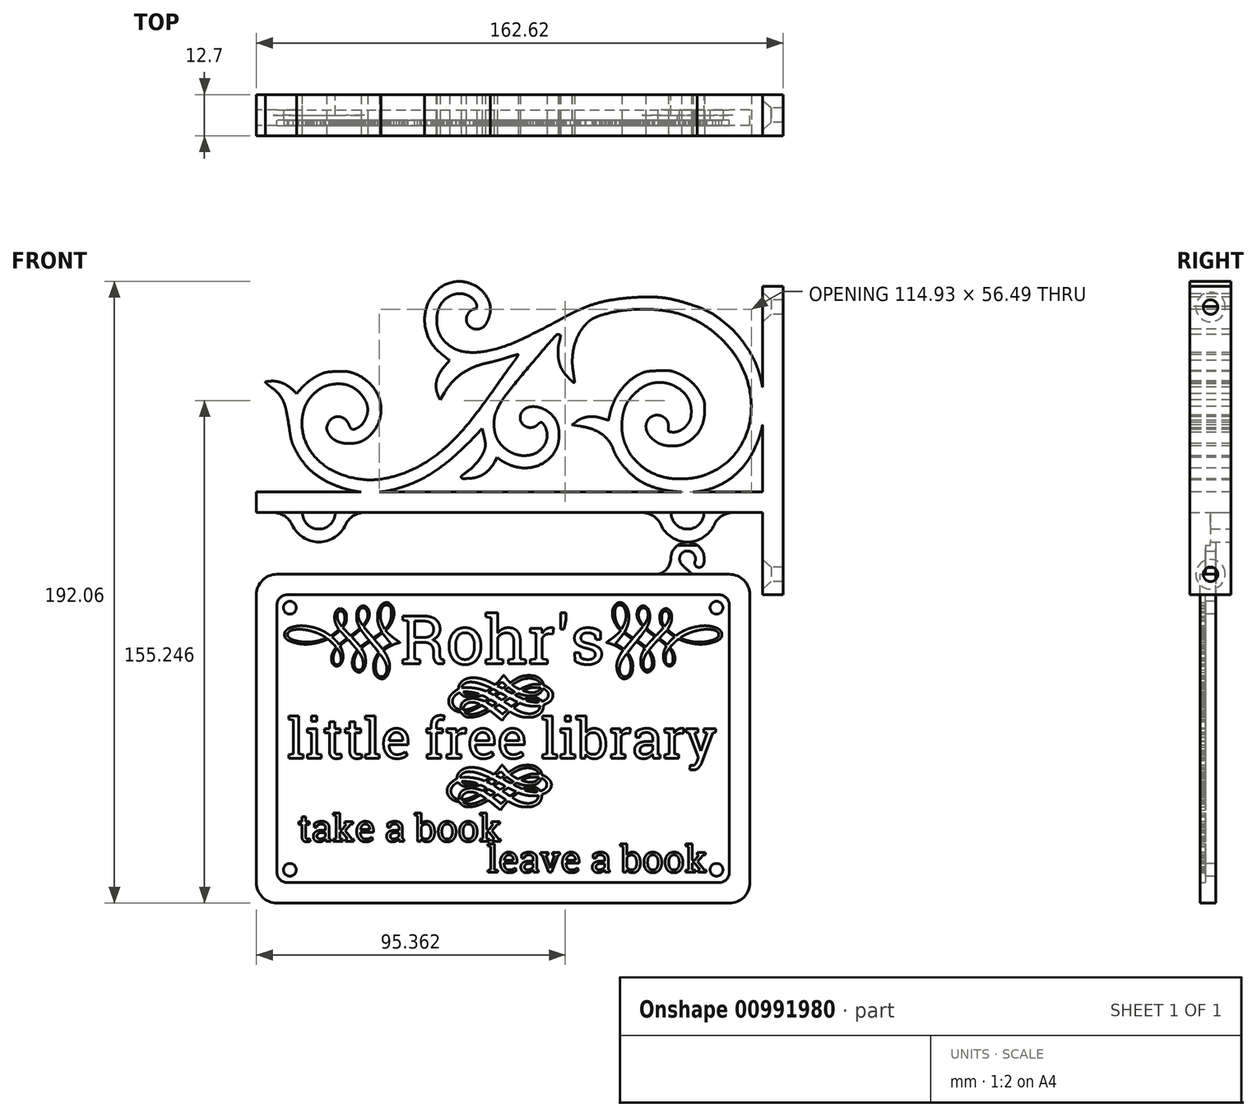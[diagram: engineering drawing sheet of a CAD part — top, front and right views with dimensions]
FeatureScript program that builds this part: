
annotation { "Feature Type Name" : "Feature", "Feature Type Description" : "" }
export const myFeature = defineFeature(function(context is Context, id is Id, definition is map)
    precondition{}
    {
        {
            var Q0;
            Q0=qCreatedBy(makeId("Front.planeOp"),FACE);
            var sketch = newSketch(context, id + "F0", { "sketchPlane" : qUnion([Q0])});
            skLineSegment(sketch, "E0.bottom", {"start": v(-69.85, 50.8) * mm, "end": v(69.85, 50.8) * mm});
            skLineSegment(sketch, "E0.top", {"start": v(-69.85, -50.8) * mm, "end": v(69.85, -50.8) * mm});
            skLineSegment(sketch, "E0.left", {"start": v(-76.2, 44.45) * mm, "end": v(-76.2, -44.45) * mm});
            skLineSegment(sketch, "E0.right", {"start": v(76.2, 44.45) * mm, "end": v(76.2, -44.45) * mm});
            skPoint(sketch, "E0.middle", {"position": v(0, 0) * mm});
            skPoint(sketch, "E1.visualSharp", {"position": v(-76.2, 50.8) * mm});
            skArc(sketch, "E1.filletArc", {"start": v(-69.85, 50.8) * mm, "mid": v(-74.34, 48.94) * mm, "end": v(-76.2, 44.45) * mm});
            skPoint(sketch, "E2.visualSharp", {"position": v(76.2, 50.8) * mm});
            skArc(sketch, "E2.filletArc", {"start": v(76.2, 44.45) * mm, "mid": v(74.34, 48.94) * mm, "end": v(69.85, 50.8) * mm});
            skPoint(sketch, "E3.visualSharp", {"position": v(76.2, -50.8) * mm});
            skArc(sketch, "E3.filletArc", {"start": v(69.85, -50.8) * mm, "mid": v(74.34, -48.94) * mm, "end": v(76.2, -44.45) * mm});
            skPoint(sketch, "E4.visualSharp", {"position": v(-76.2, -50.8) * mm});
            skArc(sketch, "E4.filletArc", {"start": v(-76.2, -44.45) * mm, "mid": v(-74.34, -48.94) * mm, "end": v(-69.85, -50.8) * mm});
            skSolve(sketch);
        }
        {
            var Q0;
            Q0=makeQuery(id+"F0.imprint","IMPRINT",FACE,{"disambiguationData":[TD([[makeQuery(id+"F0.imprint","IMPRINT",EDGE,{"derivedFrom":sQuery(id+"F0.wireOp",EDGE,"E0.bottom")}),-1.0]])]});
            extrude(context, id + "F1", {"entities" : qUnion([Q0]), "endBound" : BoundingType.SYMMETRIC, "depth" : 3.17 * mm, "offsetDistance" : 25.4 * mm});
        }
        {
            var Q0;
            Q0=makeQuery(id+"F1.opExtrude","CAP_FACE",FACE,{"disambiguationData":[OSD([sQuery(id+"F0.wireOp",EDGE,"E0.bottom"),sQuery(id+"F0.wireOp",EDGE,"E0.top"),sQuery(id+"F0.wireOp",EDGE,"E0.left"),sQuery(id+"F0.wireOp",EDGE,"E0.right"),sQuery(id+"F0.wireOp",EDGE,"E1.filletArc"),sQuery(id+"F0.wireOp",EDGE,"E2.filletArc"),sQuery(id+"F0.wireOp",EDGE,"E3.filletArc"),sQuery(id+"F0.wireOp",EDGE,"E4.filletArc")])],"isStart":false});
            var sketch = newSketch(context, id + "F2", { "sketchPlane" : qUnion([Q0])});
            skLineSegment(sketch, "E5.bottom", {"start": v(-66.67, 44.45) * mm, "end": v(66.67, 44.45) * mm});
            skLineSegment(sketch, "E5.top", {"start": v(-66.67, -44.45) * mm, "end": v(66.67, -44.45) * mm});
            skLineSegment(sketch, "E5.left", {"start": v(-69.85, 41.28) * mm, "end": v(-69.85, -41.27) * mm});
            skLineSegment(sketch, "E5.right", {"start": v(69.85, 41.28) * mm, "end": v(69.85, -41.27) * mm});
            skPoint(sketch, "E5.middle", {"position": v(0, 0) * mm});
            skPoint(sketch, "E6.visualSharp", {"position": v(-69.85, 44.45) * mm});
            skArc(sketch, "E6.filletArc", {"start": v(-66.67, 44.45) * mm, "mid": v(-68.92, 43.52) * mm, "end": v(-69.85, 41.28) * mm});
            skPoint(sketch, "E7.visualSharp", {"position": v(69.85, 44.45) * mm});
            skArc(sketch, "E7.filletArc", {"start": v(69.85, 41.28) * mm, "mid": v(68.92, 43.52) * mm, "end": v(66.67, 44.45) * mm});
            skPoint(sketch, "E8.visualSharp", {"position": v(69.85, -44.45) * mm});
            skArc(sketch, "E8.filletArc", {"start": v(66.67, -44.45) * mm, "mid": v(68.92, -43.52) * mm, "end": v(69.85, -41.27) * mm});
            skPoint(sketch, "E9.visualSharp", {"position": v(-69.85, -44.45) * mm});
            skArc(sketch, "E9.filletArc", {"start": v(-69.85, -41.27) * mm, "mid": v(-68.92, -43.52) * mm, "end": v(-66.67, -44.45) * mm});
            skSolve(sketch);
        }
        {
            var Q0;
            Q0=makeQuery(id+"F2.imprint","IMPRINT",FACE,{"disambiguationData":[TD([[makeQuery(id+"F2.imprint","IMPRINT",EDGE,{"derivedFrom":sQuery(id+"F2.wireOp",EDGE,"E5.bottom")}),1.0]])]});
            extrude(context, id + "F3", {"entities" : qUnion([Q0]), "operationType" : NewBodyOperationType.ADD, "depth" : 1.59 * mm, "offsetDistance" : 25.4 * mm});
        }
        {
            var Q0;
            Q0=makeQuery(id+"F1.opExtrude","CAP_FACE",FACE,{"disambiguationData":[OSD([sQuery(id+"F0.wireOp",EDGE,"E0.bottom"),sQuery(id+"F0.wireOp",EDGE,"E0.top"),sQuery(id+"F0.wireOp",EDGE,"E0.left"),sQuery(id+"F0.wireOp",EDGE,"E0.right"),sQuery(id+"F0.wireOp",EDGE,"E1.filletArc"),sQuery(id+"F0.wireOp",EDGE,"E2.filletArc"),sQuery(id+"F0.wireOp",EDGE,"E3.filletArc"),sQuery(id+"F0.wireOp",EDGE,"E4.filletArc")])],"isStart":false});
            var sketch = newSketch(context, id + "F4", { "sketchPlane" : qUnion([Q0])});
            skLineSegment(sketch, "E10", {"start": v(0, 0) * mm, "end": v(0, 25.75) * mm, "construction": true});
            skArc(sketch, "E11", {"start": v(-36.9, 41.88) * mm, "mid": v(-37.36, 41.59) * mm, "end": v(-37.75, 41.2) * mm});
            skArc(sketch, "E12", {"start": v(-37.75, 41.2) * mm, "mid": v(-38.1, 40.67) * mm, "end": v(-38.38, 40.1) * mm});
            skArc(sketch, "E13", {"start": v(-38.38, 40.1) * mm, "mid": v(-38.6, 39.42) * mm, "end": v(-38.75, 38.7) * mm});
            skArc(sketch, "E14", {"start": v(-38.75, 38.7) * mm, "mid": v(-38.82, 37.9) * mm, "end": v(-38.8, 37.1) * mm});
            skArc(sketch, "E15", {"start": v(-38.8, 37.1) * mm, "mid": v(-38.78, 36.68) * mm, "end": v(-38.72, 36.26) * mm});
            skArc(sketch, "E16", {"start": v(-38.72, 36.26) * mm, "mid": v(-38.65, 35.87) * mm, "end": v(-38.56, 35.49) * mm});
            skArc(sketch, "E17", {"start": v(-38.56, 35.49) * mm, "mid": v(-38.44, 35.1) * mm, "end": v(-38.3, 34.7) * mm});
            skArc(sketch, "E18", {"start": v(-38.3, 34.7) * mm, "mid": v(-38.1, 34.27) * mm, "end": v(-37.9, 33.83) * mm});
            skLineSegment(sketch, "E19", {"start": v(-37.9, 33.83) * mm, "end": v(-37.5, 32.99) * mm});
            skLineSegment(sketch, "E20", {"start": v(-37.5, 32.99) * mm, "end": v(-37.74, 32.8) * mm});
            skArc(sketch, "E21", {"start": v(-37.74, 32.8) * mm, "mid": v(-38, 32.6) * mm, "end": v(-38.27, 32.4) * mm});
            skArc(sketch, "E22", {"start": v(-38.27, 32.4) * mm, "mid": v(-38.7, 32.12) * mm, "end": v(-39.12, 31.84) * mm});
            skArc(sketch, "E23", {"start": v(-39.12, 31.84) * mm, "mid": v(-39.59, 31.53) * mm, "end": v(-40.05, 31.23) * mm});
            skArc(sketch, "E24", {"start": v(-40.05, 31.23) * mm, "mid": v(-40.1, 31.21) * mm, "end": v(-40.15, 31.22) * mm});
            skArc(sketch, "E25", {"start": v(-40.15, 31.22) * mm, "mid": v(-40.18, 31.23) * mm, "end": v(-40.2, 31.25) * mm});
            skArc(sketch, "E26", {"start": v(-40.2, 31.25) * mm, "mid": v(-40.41, 31.5) * mm, "end": v(-40.62, 31.74) * mm});
            skArc(sketch, "E27", {"start": v(-40.62, 31.74) * mm, "mid": v(-40.86, 32.01) * mm, "end": v(-41.1, 32.29) * mm});
            skArc(sketch, "E28", {"start": v(-41.1, 32.29) * mm, "mid": v(-41.38, 32.61) * mm, "end": v(-41.66, 32.94) * mm});
            skLineSegment(sketch, "E29", {"start": v(-41.66, 32.94) * mm, "end": v(-43.09, 34.63) * mm});
            skLineSegment(sketch, "E30", {"start": v(-43.09, 34.63) * mm, "end": v(-42.74, 35.06) * mm});
            skArc(sketch, "E31", {"start": v(-42.74, 35.06) * mm, "mid": v(-42.33, 35.6) * mm, "end": v(-41.96, 36.17) * mm});
            skArc(sketch, "E32", {"start": v(-41.96, 36.17) * mm, "mid": v(-41.7, 36.7) * mm, "end": v(-41.49, 37.24) * mm});
            skArc(sketch, "E33", {"start": v(-41.49, 37.24) * mm, "mid": v(-41.36, 37.75) * mm, "end": v(-41.3, 38.28) * mm});
            skArc(sketch, "E34", {"start": v(-41.3, 38.28) * mm, "mid": v(-41.32, 38.78) * mm, "end": v(-41.4, 39.28) * mm});
            skArc(sketch, "E35", {"start": v(-41.4, 39.28) * mm, "mid": v(-41.49, 39.56) * mm, "end": v(-41.6, 39.84) * mm});
            skArc(sketch, "E36", {"start": v(-41.6, 39.84) * mm, "mid": v(-41.7, 40.07) * mm, "end": v(-41.84, 40.29) * mm});
            skArc(sketch, "E37", {"start": v(-41.84, 40.29) * mm, "mid": v(-41.98, 40.47) * mm, "end": v(-42.14, 40.63) * mm});
            skArc(sketch, "E38", {"start": v(-42.14, 40.63) * mm, "mid": v(-42.32, 40.77) * mm, "end": v(-42.51, 40.88) * mm});
            skArc(sketch, "E39", {"start": v(-42.51, 40.88) * mm, "mid": v(-42.7, 40.96) * mm, "end": v(-42.9, 41.03) * mm});
            skArc(sketch, "E40", {"start": v(-42.9, 41.03) * mm, "mid": v(-43.07, 41.06) * mm, "end": v(-43.25, 41.07) * mm});
            skArc(sketch, "E41", {"start": v(-43.25, 41.07) * mm, "mid": v(-43.42, 41.06) * mm, "end": v(-43.6, 41.02) * mm});
            skArc(sketch, "E42", {"start": v(-43.6, 41.02) * mm, "mid": v(-43.8, 40.95) * mm, "end": v(-43.99, 40.86) * mm});
            skArc(sketch, "E43", {"start": v(-43.99, 40.86) * mm, "mid": v(-44.28, 40.67) * mm, "end": v(-44.53, 40.41) * mm});
            skArc(sketch, "E44", {"start": v(-44.53, 40.41) * mm, "mid": v(-44.76, 40.08) * mm, "end": v(-44.95, 39.7) * mm});
            skArc(sketch, "E45", {"start": v(-44.95, 39.7) * mm, "mid": v(-45.1, 39.26) * mm, "end": v(-45.2, 38.79) * mm});
            skArc(sketch, "E46", {"start": v(-45.2, 38.79) * mm, "mid": v(-45.27, 38.25) * mm, "end": v(-45.3, 37.7) * mm});
            skArc(sketch, "E47", {"start": v(-45.3, 37.7) * mm, "mid": v(-45.29, 37.34) * mm, "end": v(-45.26, 36.98) * mm});
            skArc(sketch, "E48", {"start": v(-45.26, 36.98) * mm, "mid": v(-45.2, 36.64) * mm, "end": v(-45.14, 36.3) * mm});
            skArc(sketch, "E49", {"start": v(-45.14, 36.3) * mm, "mid": v(-45.04, 35.97) * mm, "end": v(-44.93, 35.63) * mm});
            skArc(sketch, "E50", {"start": v(-44.93, 35.63) * mm, "mid": v(-44.78, 35.27) * mm, "end": v(-44.6, 34.9) * mm});
            skLineSegment(sketch, "E51", {"start": v(-44.6, 34.9) * mm, "end": v(-44.22, 34.12) * mm});
            skLineSegment(sketch, "E52", {"start": v(-44.22, 34.12) * mm, "end": v(-44.73, 33.68) * mm});
            skArc(sketch, "E53", {"start": v(-44.73, 33.68) * mm, "mid": v(-44.86, 33.57) * mm, "end": v(-45, 33.47) * mm});
            skArc(sketch, "E54", {"start": v(-45, 33.47) * mm, "mid": v(-45.19, 33.32) * mm, "end": v(-45.38, 33.16) * mm});
            skArc(sketch, "E55", {"start": v(-45.38, 33.16) * mm, "mid": v(-45.59, 33) * mm, "end": v(-45.8, 32.83) * mm});
            skArc(sketch, "E56", {"start": v(-45.8, 32.83) * mm, "mid": v(-46, 32.68) * mm, "end": v(-46.2, 32.53) * mm});
            skArc(sketch, "E57", {"start": v(-46.2, 32.53) * mm, "mid": v(-46.45, 32.34) * mm, "end": v(-46.7, 32.16) * mm});
            skArc(sketch, "E58", {"start": v(-46.7, 32.16) * mm, "mid": v(-46.84, 32.07) * mm, "end": v(-46.98, 31.98) * mm});
            skArc(sketch, "E59", {"start": v(-46.98, 31.98) * mm, "mid": v(-47.07, 31.93) * mm, "end": v(-47.17, 31.9) * mm});
            skArc(sketch, "E60", {"start": v(-47.17, 31.9) * mm, "mid": v(-47.22, 31.9) * mm, "end": v(-47.27, 31.93) * mm});
            skArc(sketch, "E61", {"start": v(-47.27, 31.93) * mm, "mid": v(-47.31, 31.97) * mm, "end": v(-47.36, 32.02) * mm});
            skArc(sketch, "E62", {"start": v(-47.36, 32.02) * mm, "mid": v(-47.51, 32.19) * mm, "end": v(-47.67, 32.35) * mm});
            skArc(sketch, "E63", {"start": v(-47.67, 32.35) * mm, "mid": v(-47.85, 32.55) * mm, "end": v(-48.04, 32.75) * mm});
            skArc(sketch, "E64", {"start": v(-48.04, 32.75) * mm, "mid": v(-48.25, 32.97) * mm, "end": v(-48.46, 33.2) * mm});
            skLineSegment(sketch, "E65", {"start": v(-48.46, 33.2) * mm, "end": v(-49.53, 34.33) * mm});
            skLineSegment(sketch, "E66", {"start": v(-49.53, 34.33) * mm, "end": v(-49.19, 34.78) * mm});
            skArc(sketch, "E67", {"start": v(-49.19, 34.78) * mm, "mid": v(-48.98, 35.07) * mm, "end": v(-48.8, 35.37) * mm});
            skArc(sketch, "E68", {"start": v(-48.8, 35.37) * mm, "mid": v(-48.67, 35.66) * mm, "end": v(-48.56, 35.96) * mm});
            skArc(sketch, "E69", {"start": v(-48.56, 35.96) * mm, "mid": v(-48.48, 36.29) * mm, "end": v(-48.42, 36.62) * mm});
            skArc(sketch, "E70", {"start": v(-48.42, 36.62) * mm, "mid": v(-48.39, 37.04) * mm, "end": v(-48.38, 37.45) * mm});
            skArc(sketch, "E71", {"start": v(-48.38, 37.45) * mm, "mid": v(-48.38, 37.75) * mm, "end": v(-48.38, 38.05) * mm});
            skArc(sketch, "E72", {"start": v(-48.38, 38.05) * mm, "mid": v(-48.4, 38.23) * mm, "end": v(-48.42, 38.4) * mm});
            skArc(sketch, "E73", {"start": v(-48.42, 38.4) * mm, "mid": v(-48.44, 38.54) * mm, "end": v(-48.48, 38.68) * mm});
            skArc(sketch, "E74", {"start": v(-48.48, 38.68) * mm, "mid": v(-48.54, 38.82) * mm, "end": v(-48.6, 38.97) * mm});
            skArc(sketch, "E75", {"start": v(-48.6, 38.97) * mm, "mid": v(-48.73, 39.18) * mm, "end": v(-48.85, 39.38) * mm});
            skArc(sketch, "E76", {"start": v(-48.85, 39.38) * mm, "mid": v(-48.97, 39.54) * mm, "end": v(-49.1, 39.68) * mm});
            skArc(sketch, "E77", {"start": v(-49.1, 39.68) * mm, "mid": v(-49.23, 39.8) * mm, "end": v(-49.37, 39.9) * mm});
            skArc(sketch, "E78", {"start": v(-49.37, 39.9) * mm, "mid": v(-49.54, 40.01) * mm, "end": v(-49.72, 40.1) * mm});
            skArc(sketch, "E79", {"start": v(-49.72, 40.1) * mm, "mid": v(-49.92, 40.18) * mm, "end": v(-50.13, 40.23) * mm});
            skArc(sketch, "E80", {"start": v(-50.13, 40.23) * mm, "mid": v(-50.32, 40.24) * mm, "end": v(-50.5, 40.23) * mm});
            skArc(sketch, "E81", {"start": v(-50.5, 40.23) * mm, "mid": v(-50.7, 40.17) * mm, "end": v(-50.87, 40.09) * mm});
            skArc(sketch, "E82", {"start": v(-50.87, 40.09) * mm, "mid": v(-51.07, 39.96) * mm, "end": v(-51.25, 39.81) * mm});
            skArc(sketch, "E83", {"start": v(-51.25, 39.81) * mm, "mid": v(-51.64, 39.34) * mm, "end": v(-51.89, 38.79) * mm});
            skArc(sketch, "E84", {"start": v(-51.89, 38.79) * mm, "mid": v(-52.04, 38.07) * mm, "end": v(-52.07, 37.34) * mm});
            skArc(sketch, "E85", {"start": v(-52.07, 37.34) * mm, "mid": v(-51.98, 36.52) * mm, "end": v(-51.77, 35.73) * mm});
            skArc(sketch, "E86", {"start": v(-51.77, 35.73) * mm, "mid": v(-51.46, 34.97) * mm, "end": v(-51.04, 34.26) * mm});
            skLineSegment(sketch, "E87", {"start": v(-51.04, 34.26) * mm, "end": v(-50.7, 33.78) * mm});
            skLineSegment(sketch, "E88", {"start": v(-50.7, 33.78) * mm, "end": v(-51.26, 33.3) * mm});
            skArc(sketch, "E89", {"start": v(-51.26, 33.3) * mm, "mid": v(-51.39, 33.18) * mm, "end": v(-51.52, 33.07) * mm});
            skArc(sketch, "E90", {"start": v(-51.52, 33.07) * mm, "mid": v(-51.69, 32.94) * mm, "end": v(-51.85, 32.8) * mm});
            skArc(sketch, "E91", {"start": v(-51.85, 32.8) * mm, "mid": v(-52.03, 32.67) * mm, "end": v(-52.2, 32.54) * mm});
            skArc(sketch, "E92", {"start": v(-52.2, 32.54) * mm, "mid": v(-52.37, 32.42) * mm, "end": v(-52.52, 32.3) * mm});
            skLineSegment(sketch, "E93", {"start": v(-52.52, 32.3) * mm, "end": v(-53.25, 31.8) * mm});
            skLineSegment(sketch, "E94", {"start": v(-53.25, 31.8) * mm, "end": v(-54.37, 32.55) * mm});
            skArc(sketch, "E95", {"start": v(-54.37, 32.55) * mm, "mid": v(-55.03, 32.97) * mm, "end": v(-55.72, 33.33) * mm});
            skArc(sketch, "E96", {"start": v(-55.72, 33.33) * mm, "mid": v(-56.45, 33.67) * mm, "end": v(-57.2, 33.95) * mm});
            skArc(sketch, "E97", {"start": v(-57.2, 33.95) * mm, "mid": v(-58.01, 34.22) * mm, "end": v(-58.85, 34.43) * mm});
            skArc(sketch, "E98", {"start": v(-58.85, 34.43) * mm, "mid": v(-59.79, 34.63) * mm, "end": v(-60.73, 34.79) * mm});
            skArc(sketch, "E99", {"start": v(-60.73, 34.79) * mm, "mid": v(-61.26, 34.85) * mm, "end": v(-61.78, 34.9) * mm});
            skArc(sketch, "E100", {"start": v(-61.78, 34.9) * mm, "mid": v(-62.29, 34.9) * mm, "end": v(-62.79, 34.9) * mm});
            skArc(sketch, "E101", {"start": v(-62.79, 34.9) * mm, "mid": v(-63.28, 34.86) * mm, "end": v(-63.77, 34.8) * mm});
            skArc(sketch, "E102", {"start": v(-63.77, 34.8) * mm, "mid": v(-64.28, 34.7) * mm, "end": v(-64.78, 34.6) * mm});
            skArc(sketch, "E103", {"start": v(-64.78, 34.6) * mm, "mid": v(-65.27, 34.45) * mm, "end": v(-65.75, 34.3) * mm});
            skArc(sketch, "E104", {"start": v(-65.75, 34.3) * mm, "mid": v(-66.11, 34.14) * mm, "end": v(-66.46, 33.95) * mm});
            skArc(sketch, "E105", {"start": v(-66.46, 33.95) * mm, "mid": v(-66.73, 33.75) * mm, "end": v(-66.98, 33.52) * mm});
            skArc(sketch, "E106", {"start": v(-66.98, 33.52) * mm, "mid": v(-67.19, 33.26) * mm, "end": v(-67.36, 32.98) * mm});
            skArc(sketch, "E107", {"start": v(-67.36, 32.98) * mm, "mid": v(-67.45, 32.78) * mm, "end": v(-67.5, 32.57) * mm});
            skArc(sketch, "E108", {"start": v(-67.5, 32.57) * mm, "mid": v(-67.53, 32.32) * mm, "end": v(-67.54, 32.06) * mm});
            skArc(sketch, "E109", {"start": v(-67.54, 32.06) * mm, "mid": v(-67.52, 31.82) * mm, "end": v(-67.48, 31.57) * mm});
            skArc(sketch, "E110", {"start": v(-67.48, 31.57) * mm, "mid": v(-67.43, 31.4) * mm, "end": v(-67.33, 31.23) * mm});
            skArc(sketch, "E111", {"start": v(-67.33, 31.23) * mm, "mid": v(-66.8, 30.66) * mm, "end": v(-66.12, 30.26) * mm});
            skArc(sketch, "E112", {"start": v(-66.12, 30.26) * mm, "mid": v(-65.05, 29.85) * mm, "end": v(-63.95, 29.55) * mm});
            skArc(sketch, "E113", {"start": v(-63.95, 29.55) * mm, "mid": v(-62.7, 29.31) * mm, "end": v(-61.44, 29.2) * mm});
            skArc(sketch, "E114", {"start": v(-61.44, 29.2) * mm, "mid": v(-60.25, 29.2) * mm, "end": v(-59.07, 29.33) * mm});
            skArc(sketch, "E115", {"start": v(-59.07, 29.33) * mm, "mid": v(-58.52, 29.42) * mm, "end": v(-57.97, 29.53) * mm});
            skArc(sketch, "E116", {"start": v(-57.97, 29.53) * mm, "mid": v(-57.44, 29.65) * mm, "end": v(-56.92, 29.78) * mm});
            skArc(sketch, "E117", {"start": v(-56.92, 29.78) * mm, "mid": v(-56.44, 29.92) * mm, "end": v(-55.96, 30.07) * mm});
            skArc(sketch, "E118", {"start": v(-55.96, 30.07) * mm, "mid": v(-55.53, 30.23) * mm, "end": v(-55.1, 30.4) * mm});
            skArc(sketch, "E119", {"start": v(-55.1, 30.4) * mm, "mid": v(-54.8, 30.52) * mm, "end": v(-54.5, 30.64) * mm});
            skArc(sketch, "E120", {"start": v(-54.5, 30.64) * mm, "mid": v(-54.37, 30.69) * mm, "end": v(-54.24, 30.72) * mm});
            skArc(sketch, "E121", {"start": v(-54.24, 30.72) * mm, "mid": v(-54.16, 30.72) * mm, "end": v(-54.09, 30.7) * mm});
            skArc(sketch, "E122", {"start": v(-54.09, 30.7) * mm, "mid": v(-54, 30.67) * mm, "end": v(-53.93, 30.62) * mm});
            skArc(sketch, "E123", {"start": v(-53.93, 30.62) * mm, "mid": v(-53.71, 30.43) * mm, "end": v(-53.5, 30.24) * mm});
            skArc(sketch, "E124", {"start": v(-53.5, 30.24) * mm, "mid": v(-53.25, 30) * mm, "end": v(-53, 29.77) * mm});
            skArc(sketch, "E125", {"start": v(-53, 29.77) * mm, "mid": v(-52.74, 29.53) * mm, "end": v(-52.5, 29.28) * mm});
            skArc(sketch, "E126", {"start": v(-52.5, 29.28) * mm, "mid": v(-52.29, 29.07) * mm, "end": v(-52.09, 28.85) * mm});
            skLineSegment(sketch, "E127", {"start": v(-52.09, 28.85) * mm, "end": v(-51.55, 28.28) * mm});
            skLineSegment(sketch, "E128", {"start": v(-51.55, 28.28) * mm, "end": v(-51.96, 27.74) * mm});
            skArc(sketch, "E129", {"start": v(-51.96, 27.74) * mm, "mid": v(-52.24, 27.34) * mm, "end": v(-52.49, 26.92) * mm});
            skArc(sketch, "E130", {"start": v(-52.49, 26.92) * mm, "mid": v(-52.69, 26.5) * mm, "end": v(-52.84, 26.06) * mm});
            skArc(sketch, "E131", {"start": v(-52.84, 26.06) * mm, "mid": v(-52.96, 25.63) * mm, "end": v(-53.02, 25.2) * mm});
            skArc(sketch, "E132", {"start": v(-53.02, 25.2) * mm, "mid": v(-53.04, 24.75) * mm, "end": v(-53.02, 24.31) * mm});
            skArc(sketch, "E133", {"start": v(-53.02, 24.31) * mm, "mid": v(-52.93, 23.82) * mm, "end": v(-52.75, 23.34) * mm});
            skArc(sketch, "E134", {"start": v(-52.75, 23.34) * mm, "mid": v(-52.52, 22.97) * mm, "end": v(-52.2, 22.68) * mm});
            skArc(sketch, "E135", {"start": v(-52.2, 22.68) * mm, "mid": v(-51.85, 22.5) * mm, "end": v(-51.46, 22.43) * mm});
            skArc(sketch, "E136", {"start": v(-51.46, 22.43) * mm, "mid": v(-51.04, 22.48) * mm, "end": v(-50.64, 22.62) * mm});
            skArc(sketch, "E137", {"start": v(-50.64, 22.62) * mm, "mid": v(-50.38, 22.8) * mm, "end": v(-50.17, 23.03) * mm});
            skArc(sketch, "E138", {"start": v(-50.17, 23.03) * mm, "mid": v(-49.95, 23.36) * mm, "end": v(-49.78, 23.7) * mm});
            skArc(sketch, "E139", {"start": v(-49.78, 23.7) * mm, "mid": v(-49.63, 24.13) * mm, "end": v(-49.52, 24.57) * mm});
            skArc(sketch, "E140", {"start": v(-49.52, 24.57) * mm, "mid": v(-49.45, 25.03) * mm, "end": v(-49.43, 25.5) * mm});
            skArc(sketch, "E141", {"start": v(-49.43, 25.5) * mm, "mid": v(-49.45, 25.8) * mm, "end": v(-49.48, 26.1) * mm});
            skArc(sketch, "E142", {"start": v(-49.48, 26.1) * mm, "mid": v(-49.55, 26.46) * mm, "end": v(-49.64, 26.82) * mm});
            skArc(sketch, "E143", {"start": v(-49.64, 26.82) * mm, "mid": v(-49.74, 27.19) * mm, "end": v(-49.86, 27.55) * mm});
            skArc(sketch, "E144", {"start": v(-49.86, 27.55) * mm, "mid": v(-49.99, 27.87) * mm, "end": v(-50.13, 28.18) * mm});
            skLineSegment(sketch, "E145", {"start": v(-50.13, 28.18) * mm, "end": v(-50.42, 28.74) * mm});
            skLineSegment(sketch, "E146", {"start": v(-50.42, 28.74) * mm, "end": v(-50.05, 29.04) * mm});
            skArc(sketch, "E147", {"start": v(-50.05, 29.04) * mm, "mid": v(-49.95, 29.12) * mm, "end": v(-49.85, 29.2) * mm});
            skArc(sketch, "E148", {"start": v(-49.85, 29.2) * mm, "mid": v(-49.7, 29.33) * mm, "end": v(-49.54, 29.46) * mm});
            skArc(sketch, "E149", {"start": v(-49.54, 29.46) * mm, "mid": v(-49.36, 29.6) * mm, "end": v(-49.17, 29.74) * mm});
            skArc(sketch, "E150", {"start": v(-49.17, 29.74) * mm, "mid": v(-49, 29.88) * mm, "end": v(-48.81, 30.02) * mm});
            skLineSegment(sketch, "E151", {"start": v(-48.81, 30.02) * mm, "end": v(-47.94, 30.7) * mm});
            skLineSegment(sketch, "E152", {"start": v(-47.94, 30.7) * mm, "end": v(-47.2, 29.86) * mm});
            skArc(sketch, "E153", {"start": v(-47.2, 29.86) * mm, "mid": v(-46.91, 29.54) * mm, "end": v(-46.63, 29.22) * mm});
            skArc(sketch, "E154", {"start": v(-46.63, 29.22) * mm, "mid": v(-46.32, 28.87) * mm, "end": v(-46.02, 28.52) * mm});
            skArc(sketch, "E155", {"start": v(-46.02, 28.52) * mm, "mid": v(-45.75, 28.2) * mm, "end": v(-45.48, 27.89) * mm});
            skArc(sketch, "E156", {"start": v(-45.48, 27.89) * mm, "mid": v(-45.34, 27.72) * mm, "end": v(-45.2, 27.55) * mm});
            skArc(sketch, "E157", {"start": v(-45.2, 27.55) * mm, "mid": v(-45.18, 27.5) * mm, "end": v(-45.16, 27.43) * mm});
            skArc(sketch, "E158", {"start": v(-45.16, 27.43) * mm, "mid": v(-45.16, 27.36) * mm, "end": v(-45.18, 27.3) * mm});
            skArc(sketch, "E159", {"start": v(-45.18, 27.3) * mm, "mid": v(-45.22, 27.2) * mm, "end": v(-45.27, 27.1) * mm});
            skArc(sketch, "E160", {"start": v(-45.27, 27.1) * mm, "mid": v(-45.38, 26.93) * mm, "end": v(-45.5, 26.76) * mm});
            skArc(sketch, "E161", {"start": v(-45.5, 26.76) * mm, "mid": v(-45.78, 26.3) * mm, "end": v(-46.03, 25.84) * mm});
            skArc(sketch, "E162", {"start": v(-46.03, 25.84) * mm, "mid": v(-46.23, 25.39) * mm, "end": v(-46.39, 24.92) * mm});
            skArc(sketch, "E163", {"start": v(-46.39, 24.92) * mm, "mid": v(-46.5, 24.46) * mm, "end": v(-46.57, 23.99) * mm});
            skArc(sketch, "E164", {"start": v(-46.57, 23.99) * mm, "mid": v(-46.6, 23.5) * mm, "end": v(-46.58, 23.02) * mm});
            skArc(sketch, "E165", {"start": v(-46.58, 23.02) * mm, "mid": v(-46.53, 22.6) * mm, "end": v(-46.43, 22.17) * mm});
            skArc(sketch, "E166", {"start": v(-46.43, 22.17) * mm, "mid": v(-46.28, 21.81) * mm, "end": v(-46.09, 21.48) * mm});
            skArc(sketch, "E167", {"start": v(-46.09, 21.48) * mm, "mid": v(-45.86, 21.2) * mm, "end": v(-45.58, 20.95) * mm});
            skArc(sketch, "E168", {"start": v(-45.58, 20.95) * mm, "mid": v(-45.26, 20.75) * mm, "end": v(-44.91, 20.6) * mm});
            skArc(sketch, "E169", {"start": v(-44.91, 20.6) * mm, "mid": v(-44.64, 20.54) * mm, "end": v(-44.35, 20.54) * mm});
            skArc(sketch, "E170", {"start": v(-44.35, 20.54) * mm, "mid": v(-44.06, 20.61) * mm, "end": v(-43.8, 20.74) * mm});
            skArc(sketch, "E171", {"start": v(-43.8, 20.74) * mm, "mid": v(-43.52, 20.95) * mm, "end": v(-43.29, 21.2) * mm});
            skArc(sketch, "E172", {"start": v(-43.29, 21.2) * mm, "mid": v(-43.05, 21.53) * mm, "end": v(-42.86, 21.9) * mm});
            skArc(sketch, "E173", {"start": v(-42.86, 21.9) * mm, "mid": v(-42.76, 22.1) * mm, "end": v(-42.67, 22.3) * mm});
            skArc(sketch, "E174", {"start": v(-42.67, 22.3) * mm, "mid": v(-42.61, 22.47) * mm, "end": v(-42.57, 22.63) * mm});
            skArc(sketch, "E175", {"start": v(-42.57, 22.63) * mm, "mid": v(-42.54, 22.82) * mm, "end": v(-42.52, 23) * mm});
            skArc(sketch, "E176", {"start": v(-42.52, 23) * mm, "mid": v(-42.5, 23.32) * mm, "end": v(-42.49, 23.64) * mm});
            skArc(sketch, "E177", {"start": v(-42.49, 23.64) * mm, "mid": v(-42.48, 24.17) * mm, "end": v(-42.51, 24.7) * mm});
            skArc(sketch, "E178", {"start": v(-42.51, 24.7) * mm, "mid": v(-42.57, 25.17) * mm, "end": v(-42.66, 25.63) * mm});
            skArc(sketch, "E179", {"start": v(-42.66, 25.63) * mm, "mid": v(-42.8, 26.07) * mm, "end": v(-42.96, 26.5) * mm});
            skArc(sketch, "E180", {"start": v(-42.96, 26.5) * mm, "mid": v(-43.18, 26.96) * mm, "end": v(-43.42, 27.4) * mm});
            skLineSegment(sketch, "E181", {"start": v(-43.42, 27.4) * mm, "end": v(-43.77, 27.97) * mm});
            skLineSegment(sketch, "E182", {"start": v(-43.77, 27.97) * mm, "end": v(-43.33, 28.34) * mm});
            skArc(sketch, "E183", {"start": v(-43.33, 28.34) * mm, "mid": v(-43.22, 28.43) * mm, "end": v(-43.1, 28.52) * mm});
            skArc(sketch, "E184", {"start": v(-43.1, 28.52) * mm, "mid": v(-42.93, 28.65) * mm, "end": v(-42.76, 28.78) * mm});
            skArc(sketch, "E185", {"start": v(-42.76, 28.78) * mm, "mid": v(-42.57, 28.93) * mm, "end": v(-42.37, 29.07) * mm});
            skArc(sketch, "E186", {"start": v(-42.37, 29.07) * mm, "mid": v(-42.19, 29.2) * mm, "end": v(-42, 29.34) * mm});
            skArc(sketch, "E187", {"start": v(-42, 29.34) * mm, "mid": v(-41.78, 29.5) * mm, "end": v(-41.55, 29.66) * mm});
            skArc(sketch, "E188", {"start": v(-41.55, 29.66) * mm, "mid": v(-41.42, 29.74) * mm, "end": v(-41.28, 29.82) * mm});
            skArc(sketch, "E189", {"start": v(-41.28, 29.82) * mm, "mid": v(-41.2, 29.86) * mm, "end": v(-41.1, 29.89) * mm});
            skArc(sketch, "E190", {"start": v(-41.1, 29.89) * mm, "mid": v(-41.05, 29.88) * mm, "end": v(-41, 29.86) * mm});
            skArc(sketch, "E191", {"start": v(-41, 29.86) * mm, "mid": v(-40.97, 29.8) * mm, "end": v(-40.93, 29.76) * mm});
            skArc(sketch, "E192", {"start": v(-40.93, 29.76) * mm, "mid": v(-40.75, 29.54) * mm, "end": v(-40.57, 29.31) * mm});
            skArc(sketch, "E193", {"start": v(-40.57, 29.31) * mm, "mid": v(-40.36, 29.05) * mm, "end": v(-40.15, 28.79) * mm});
            skArc(sketch, "E194", {"start": v(-40.15, 28.79) * mm, "mid": v(-39.9, 28.49) * mm, "end": v(-39.67, 28.2) * mm});
            skLineSegment(sketch, "E195", {"start": v(-39.67, 28.2) * mm, "end": v(-38.42, 26.65) * mm});
            skLineSegment(sketch, "E196", {"start": v(-38.42, 26.65) * mm, "end": v(-38.72, 26.28) * mm});
            skArc(sketch, "E197", {"start": v(-38.72, 26.28) * mm, "mid": v(-38.9, 26.04) * mm, "end": v(-39.05, 25.8) * mm});
            skArc(sketch, "E198", {"start": v(-39.05, 25.8) * mm, "mid": v(-39.21, 25.5) * mm, "end": v(-39.36, 25.2) * mm});
            skArc(sketch, "E199", {"start": v(-39.36, 25.2) * mm, "mid": v(-39.51, 24.87) * mm, "end": v(-39.64, 24.53) * mm});
            skArc(sketch, "E200", {"start": v(-39.64, 24.53) * mm, "mid": v(-39.76, 24.2) * mm, "end": v(-39.86, 23.87) * mm});
            skArc(sketch, "E201", {"start": v(-39.86, 23.87) * mm, "mid": v(-39.92, 23.64) * mm, "end": v(-39.97, 23.41) * mm});
            skArc(sketch, "E202", {"start": v(-39.97, 23.41) * mm, "mid": v(-40, 23.22) * mm, "end": v(-40.02, 23.02) * mm});
            skArc(sketch, "E203", {"start": v(-40.02, 23.02) * mm, "mid": v(-40.04, 22.8) * mm, "end": v(-40.04, 22.59) * mm});
            skArc(sketch, "E204", {"start": v(-40.04, 22.59) * mm, "mid": v(-40.04, 22.28) * mm, "end": v(-40.03, 21.97) * mm});
            skArc(sketch, "E205", {"start": v(-40.03, 21.97) * mm, "mid": v(-39.98, 21.37) * mm, "end": v(-39.9, 20.78) * mm});
            skArc(sketch, "E206", {"start": v(-39.9, 20.78) * mm, "mid": v(-39.78, 20.33) * mm, "end": v(-39.6, 19.9) * mm});
            skArc(sketch, "E207", {"start": v(-39.6, 19.9) * mm, "mid": v(-39.38, 19.54) * mm, "end": v(-39.11, 19.24) * mm});
            skArc(sketch, "E208", {"start": v(-39.11, 19.24) * mm, "mid": v(-38.78, 18.97) * mm, "end": v(-38.41, 18.75) * mm});
            skArc(sketch, "E209", {"start": v(-38.41, 18.75) * mm, "mid": v(-37.94, 18.57) * mm, "end": v(-37.45, 18.49) * mm});
            skArc(sketch, "E210", {"start": v(-37.45, 18.49) * mm, "mid": v(-37.01, 18.53) * mm, "end": v(-36.6, 18.7) * mm});
            skArc(sketch, "E211", {"start": v(-36.6, 18.7) * mm, "mid": v(-36.2, 19) * mm, "end": v(-35.9, 19.39) * mm});
            skArc(sketch, "E212", {"start": v(-35.9, 19.39) * mm, "mid": v(-35.6, 19.96) * mm, "end": v(-35.35, 20.55) * mm});
            skArc(sketch, "E213", {"start": v(-35.35, 20.55) * mm, "mid": v(-35.23, 20.97) * mm, "end": v(-35.15, 21.4) * mm});
            skArc(sketch, "E214", {"start": v(-35.15, 21.4) * mm, "mid": v(-35.1, 21.86) * mm, "end": v(-35.07, 22.33) * mm});
            skArc(sketch, "E215", {"start": v(-35.07, 22.33) * mm, "mid": v(-35.08, 22.79) * mm, "end": v(-35.12, 23.25) * mm});
            skArc(sketch, "E216", {"start": v(-35.12, 23.25) * mm, "mid": v(-35.2, 23.67) * mm, "end": v(-35.3, 24.09) * mm});
            skArc(sketch, "E217", {"start": v(-35.3, 24.09) * mm, "mid": v(-35.42, 24.4) * mm, "end": v(-35.54, 24.72) * mm});
            skArc(sketch, "E218", {"start": v(-35.54, 24.72) * mm, "mid": v(-35.7, 25.09) * mm, "end": v(-35.88, 25.45) * mm});
            skArc(sketch, "E219", {"start": v(-35.88, 25.45) * mm, "mid": v(-36.06, 25.82) * mm, "end": v(-36.25, 26.17) * mm});
            skArc(sketch, "E220", {"start": v(-36.25, 26.17) * mm, "mid": v(-36.43, 26.47) * mm, "end": v(-36.61, 26.76) * mm});
            skArc(sketch, "E221", {"start": v(-36.61, 26.76) * mm, "mid": v(-36.67, 26.85) * mm, "end": v(-36.73, 26.94) * mm});
            skArc(sketch, "E222", {"start": v(-36.73, 26.94) * mm, "mid": v(-36.78, 27.02) * mm, "end": v(-36.83, 27.1) * mm});
            skArc(sketch, "E223", {"start": v(-36.83, 27.1) * mm, "mid": v(-36.87, 27.17) * mm, "end": v(-36.91, 27.24) * mm});
            skArc(sketch, "E224", {"start": v(-36.91, 27.24) * mm, "mid": v(-36.92, 27.26) * mm, "end": v(-36.92, 27.28) * mm});
            skArc(sketch, "E225", {"start": v(-36.92, 27.28) * mm, "mid": v(-36.9, 27.36) * mm, "end": v(-36.85, 27.42) * mm});
            skArc(sketch, "E226", {"start": v(-36.85, 27.42) * mm, "mid": v(-36.44, 27.68) * mm, "end": v(-36.03, 27.94) * mm});
            skArc(sketch, "E227", {"start": v(-36.03, 27.94) * mm, "mid": v(-35.61, 28.2) * mm, "end": v(-35.2, 28.44) * mm});
            skArc(sketch, "E228", {"start": v(-35.2, 28.44) * mm, "mid": v(-34.83, 28.64) * mm, "end": v(-34.46, 28.83) * mm});
            skArc(sketch, "E229", {"start": v(-34.46, 28.83) * mm, "mid": v(-34.25, 28.92) * mm, "end": v(-34.05, 29.02) * mm});
            skArc(sketch, "E230", {"start": v(-34.05, 29.02) * mm, "mid": v(-33.81, 29.11) * mm, "end": v(-33.57, 29.2) * mm});
            skArc(sketch, "E231", {"start": v(-33.57, 29.2) * mm, "mid": v(-33.34, 29.3) * mm, "end": v(-33.11, 29.38) * mm});
            skArc(sketch, "E232", {"start": v(-33.11, 29.38) * mm, "mid": v(-32.92, 29.44) * mm, "end": v(-32.74, 29.5) * mm});
            skArc(sketch, "E233", {"start": v(-32.74, 29.5) * mm, "mid": v(-32.58, 29.53) * mm, "end": v(-32.42, 29.58) * mm});
            skArc(sketch, "E234", {"start": v(-32.42, 29.58) * mm, "mid": v(-32.3, 29.61) * mm, "end": v(-32.16, 29.65) * mm});
            skArc(sketch, "E235", {"start": v(-32.16, 29.65) * mm, "mid": v(-32.04, 29.69) * mm, "end": v(-31.93, 29.72) * mm});
            skArc(sketch, "E236", {"start": v(-31.93, 29.72) * mm, "mid": v(-31.91, 29.73) * mm, "end": v(-31.9, 29.73) * mm});
            skArc(sketch, "E237", {"start": v(-31.9, 29.73) * mm, "mid": v(-31.9, 29.74) * mm, "end": v(-31.9, 29.75) * mm});
            skArc(sketch, "E238", {"start": v(-31.9, 29.75) * mm, "mid": v(-32.08, 29.89) * mm, "end": v(-32.26, 30.02) * mm});
            skArc(sketch, "E239", {"start": v(-32.26, 30.02) * mm, "mid": v(-32.46, 30.16) * mm, "end": v(-32.67, 30.31) * mm});
            skArc(sketch, "E240", {"start": v(-32.67, 30.31) * mm, "mid": v(-32.91, 30.48) * mm, "end": v(-33.16, 30.66) * mm});
            skArc(sketch, "E241", {"start": v(-33.16, 30.66) * mm, "mid": v(-33.63, 31) * mm, "end": v(-34.09, 31.34) * mm});
            skArc(sketch, "E242", {"start": v(-34.09, 31.34) * mm, "mid": v(-34.56, 31.72) * mm, "end": v(-35.03, 32.12) * mm});
            skArc(sketch, "E243", {"start": v(-35.03, 32.12) * mm, "mid": v(-35.43, 32.48) * mm, "end": v(-35.83, 32.85) * mm});
            skArc(sketch, "E244", {"start": v(-35.83, 32.85) * mm, "mid": v(-36, 33.03) * mm, "end": v(-36.13, 33.25) * mm});
            skArc(sketch, "E245", {"start": v(-36.13, 33.25) * mm, "mid": v(-36.16, 33.3) * mm, "end": v(-36.17, 33.36) * mm});
            skArc(sketch, "E246", {"start": v(-36.17, 33.36) * mm, "mid": v(-36.16, 33.42) * mm, "end": v(-36.15, 33.47) * mm});
            skArc(sketch, "E247", {"start": v(-36.15, 33.47) * mm, "mid": v(-36.11, 33.54) * mm, "end": v(-36.07, 33.6) * mm});
            skArc(sketch, "E248", {"start": v(-36.07, 33.6) * mm, "mid": v(-35.98, 33.7) * mm, "end": v(-35.89, 33.8) * mm});
            skArc(sketch, "E249", {"start": v(-35.89, 33.8) * mm, "mid": v(-35.13, 34.7) * mm, "end": v(-34.5, 35.7) * mm});
            skArc(sketch, "E250", {"start": v(-34.5, 35.7) * mm, "mid": v(-34.06, 36.72) * mm, "end": v(-33.78, 37.8) * mm});
            skArc(sketch, "E251", {"start": v(-33.78, 37.8) * mm, "mid": v(-33.7, 38.77) * mm, "end": v(-33.8, 39.75) * mm});
            skArc(sketch, "E252", {"start": v(-33.8, 39.75) * mm, "mid": v(-34.08, 40.57) * mm, "end": v(-34.57, 41.28) * mm});
            skArc(sketch, "E253", {"start": v(-34.57, 41.28) * mm, "mid": v(-34.66, 41.39) * mm, "end": v(-34.77, 41.5) * mm});
            skArc(sketch, "E254", {"start": v(-34.77, 41.5) * mm, "mid": v(-34.87, 41.6) * mm, "end": v(-34.98, 41.7) * mm});
            skArc(sketch, "E255", {"start": v(-34.98, 41.7) * mm, "mid": v(-35.08, 41.77) * mm, "end": v(-35.18, 41.86) * mm});
            skArc(sketch, "E256", {"start": v(-35.18, 41.86) * mm, "mid": v(-35.24, 41.9) * mm, "end": v(-35.32, 41.95) * mm});
            skArc(sketch, "E257", {"start": v(-35.32, 41.95) * mm, "mid": v(-35.48, 42.02) * mm, "end": v(-35.66, 42.06) * mm});
            skArc(sketch, "E258", {"start": v(-35.66, 42.06) * mm, "mid": v(-35.86, 42.08) * mm, "end": v(-36.07, 42.09) * mm});
            skArc(sketch, "E259", {"start": v(-36.07, 42.09) * mm, "mid": v(-36.29, 42.07) * mm, "end": v(-36.5, 42.03) * mm});
            skArc(sketch, "E260", {"start": v(-36.5, 42.03) * mm, "mid": v(-36.7, 41.97) * mm, "end": v(-36.9, 41.88) * mm});
            skArc(sketch, "E261", {"start": v(-35.33, 41.15) * mm, "mid": v(-35.26, 41.1) * mm, "end": v(-35.2, 41.06) * mm});
            skArc(sketch, "E262", {"start": v(-35.2, 41.06) * mm, "mid": v(-35.13, 41) * mm, "end": v(-35.06, 40.92) * mm});
            skArc(sketch, "E263", {"start": v(-35.06, 40.92) * mm, "mid": v(-34.99, 40.83) * mm, "end": v(-34.92, 40.74) * mm});
            skArc(sketch, "E264", {"start": v(-34.92, 40.74) * mm, "mid": v(-34.86, 40.66) * mm, "end": v(-34.8, 40.57) * mm});
            skArc(sketch, "E265", {"start": v(-34.8, 40.57) * mm, "mid": v(-34.73, 40.43) * mm, "end": v(-34.67, 40.29) * mm});
            skArc(sketch, "E266", {"start": v(-34.67, 40.29) * mm, "mid": v(-34.63, 40.15) * mm, "end": v(-34.6, 40.01) * mm});
            skArc(sketch, "E267", {"start": v(-34.6, 40.01) * mm, "mid": v(-34.57, 39.83) * mm, "end": v(-34.55, 39.65) * mm});
            skArc(sketch, "E268", {"start": v(-34.55, 39.65) * mm, "mid": v(-34.53, 39.35) * mm, "end": v(-34.52, 39.05) * mm});
            skArc(sketch, "E269", {"start": v(-34.52, 39.05) * mm, "mid": v(-34.52, 38.37) * mm, "end": v(-34.58, 37.69) * mm});
            skArc(sketch, "E270", {"start": v(-34.58, 37.69) * mm, "mid": v(-34.68, 37.07) * mm, "end": v(-34.85, 36.46) * mm});
            skArc(sketch, "E271", {"start": v(-34.85, 36.46) * mm, "mid": v(-35.07, 35.9) * mm, "end": v(-35.34, 35.35) * mm});
            skArc(sketch, "E272", {"start": v(-35.34, 35.35) * mm, "mid": v(-35.67, 34.85) * mm, "end": v(-36.05, 34.38) * mm});
            skLineSegment(sketch, "E273", {"start": v(-36.05, 34.38) * mm, "end": v(-36.6, 33.77) * mm});
            skLineSegment(sketch, "E274", {"start": v(-36.6, 33.77) * mm, "end": v(-37.1, 34.83) * mm});
            skArc(sketch, "E275", {"start": v(-37.1, 34.83) * mm, "mid": v(-37.3, 35.28) * mm, "end": v(-37.5, 35.73) * mm});
            skArc(sketch, "E276", {"start": v(-37.5, 35.73) * mm, "mid": v(-37.64, 36.12) * mm, "end": v(-37.75, 36.51) * mm});
            skArc(sketch, "E277", {"start": v(-37.75, 36.51) * mm, "mid": v(-37.83, 36.88) * mm, "end": v(-37.89, 37.26) * mm});
            skArc(sketch, "E278", {"start": v(-37.89, 37.26) * mm, "mid": v(-37.92, 37.67) * mm, "end": v(-37.93, 38.08) * mm});
            skArc(sketch, "E279", {"start": v(-37.93, 38.08) * mm, "mid": v(-37.91, 38.57) * mm, "end": v(-37.85, 39.06) * mm});
            skArc(sketch, "E280", {"start": v(-37.85, 39.06) * mm, "mid": v(-37.76, 39.5) * mm, "end": v(-37.62, 39.93) * mm});
            skArc(sketch, "E281", {"start": v(-37.62, 39.93) * mm, "mid": v(-37.45, 40.29) * mm, "end": v(-37.24, 40.63) * mm});
            skArc(sketch, "E282", {"start": v(-37.24, 40.63) * mm, "mid": v(-37.02, 40.89) * mm, "end": v(-36.75, 41.1) * mm});
            skArc(sketch, "E283", {"start": v(-36.75, 41.1) * mm, "mid": v(-36.6, 41.18) * mm, "end": v(-36.45, 41.23) * mm});
            skArc(sketch, "E284", {"start": v(-36.45, 41.23) * mm, "mid": v(-36.25, 41.26) * mm, "end": v(-36.06, 41.28) * mm});
            skArc(sketch, "E285", {"start": v(-36.06, 41.28) * mm, "mid": v(-35.85, 41.28) * mm, "end": v(-35.65, 41.25) * mm});
            skArc(sketch, "E286", {"start": v(-35.65, 41.25) * mm, "mid": v(-35.49, 41.21) * mm, "end": v(-35.33, 41.15) * mm});
            skArc(sketch, "E287", {"start": v(-42.47, 40) * mm, "mid": v(-42.22, 39.7) * mm, "end": v(-42.03, 39.35) * mm});
            skArc(sketch, "E288", {"start": v(-42.03, 39.35) * mm, "mid": v(-41.89, 38.96) * mm, "end": v(-41.81, 38.55) * mm});
            skArc(sketch, "E289", {"start": v(-41.81, 38.55) * mm, "mid": v(-41.8, 38.1) * mm, "end": v(-41.84, 37.67) * mm});
            skArc(sketch, "E290", {"start": v(-41.84, 37.67) * mm, "mid": v(-41.94, 37.22) * mm, "end": v(-42.1, 36.8) * mm});
            skArc(sketch, "E291", {"start": v(-42.1, 36.8) * mm, "mid": v(-42.23, 36.56) * mm, "end": v(-42.36, 36.32) * mm});
            skArc(sketch, "E292", {"start": v(-42.36, 36.32) * mm, "mid": v(-42.56, 36.01) * mm, "end": v(-42.78, 35.7) * mm});
            skArc(sketch, "E293", {"start": v(-42.78, 35.7) * mm, "mid": v(-43, 35.4) * mm, "end": v(-43.22, 35.1) * mm});
            skArc(sketch, "E294", {"start": v(-43.22, 35.1) * mm, "mid": v(-43.28, 35.05) * mm, "end": v(-43.36, 35.03) * mm});
            skArc(sketch, "E295", {"start": v(-43.36, 35.03) * mm, "mid": v(-43.41, 35.05) * mm, "end": v(-43.45, 35.08) * mm});
            skArc(sketch, "E296", {"start": v(-43.45, 35.08) * mm, "mid": v(-43.62, 35.34) * mm, "end": v(-43.79, 35.6) * mm});
            skArc(sketch, "E297", {"start": v(-43.79, 35.6) * mm, "mid": v(-43.96, 35.87) * mm, "end": v(-44.12, 36.14) * mm});
            skArc(sketch, "E298", {"start": v(-44.12, 36.14) * mm, "mid": v(-44.25, 36.36) * mm, "end": v(-44.37, 36.6) * mm});
            skArc(sketch, "E299", {"start": v(-44.37, 36.6) * mm, "mid": v(-44.56, 37.06) * mm, "end": v(-44.69, 37.56) * mm});
            skArc(sketch, "E300", {"start": v(-44.69, 37.56) * mm, "mid": v(-44.75, 38.07) * mm, "end": v(-44.74, 38.58) * mm});
            skArc(sketch, "E301", {"start": v(-44.74, 38.58) * mm, "mid": v(-44.66, 39.05) * mm, "end": v(-44.52, 39.5) * mm});
            skArc(sketch, "E302", {"start": v(-44.52, 39.5) * mm, "mid": v(-44.33, 39.84) * mm, "end": v(-44.07, 40.13) * mm});
            skArc(sketch, "E303", {"start": v(-44.07, 40.13) * mm, "mid": v(-43.99, 40.2) * mm, "end": v(-43.9, 40.25) * mm});
            skArc(sketch, "E304", {"start": v(-43.9, 40.25) * mm, "mid": v(-43.82, 40.29) * mm, "end": v(-43.73, 40.32) * mm});
            skArc(sketch, "E305", {"start": v(-43.73, 40.32) * mm, "mid": v(-43.64, 40.35) * mm, "end": v(-43.54, 40.37) * mm});
            skArc(sketch, "E306", {"start": v(-43.54, 40.37) * mm, "mid": v(-43.43, 40.38) * mm, "end": v(-43.3, 40.38) * mm});
            skArc(sketch, "E307", {"start": v(-43.3, 40.38) * mm, "mid": v(-43.18, 40.37) * mm, "end": v(-43.05, 40.36) * mm});
            skArc(sketch, "E308", {"start": v(-43.05, 40.36) * mm, "mid": v(-42.95, 40.34) * mm, "end": v(-42.86, 40.31) * mm});
            skArc(sketch, "E309", {"start": v(-42.86, 40.31) * mm, "mid": v(-42.78, 40.26) * mm, "end": v(-42.7, 40.2) * mm});
            skArc(sketch, "E310", {"start": v(-42.7, 40.2) * mm, "mid": v(-42.58, 40.1) * mm, "end": v(-42.47, 40) * mm});
            skArc(sketch, "E311", {"start": v(-49.48, 39.14) * mm, "mid": v(-49.34, 38.98) * mm, "end": v(-49.22, 38.8) * mm});
            skArc(sketch, "E312", {"start": v(-49.22, 38.8) * mm, "mid": v(-49.12, 38.6) * mm, "end": v(-49.05, 38.4) * mm});
            skArc(sketch, "E313", {"start": v(-49.05, 38.4) * mm, "mid": v(-49, 38.15) * mm, "end": v(-48.96, 37.9) * mm});
            skArc(sketch, "E314", {"start": v(-48.96, 37.9) * mm, "mid": v(-48.94, 37.55) * mm, "end": v(-48.93, 37.2) * mm});
            skArc(sketch, "E315", {"start": v(-48.93, 37.2) * mm, "mid": v(-48.94, 36.9) * mm, "end": v(-48.96, 36.6) * mm});
            skArc(sketch, "E316", {"start": v(-48.96, 36.6) * mm, "mid": v(-49, 36.37) * mm, "end": v(-49.05, 36.14) * mm});
            skArc(sketch, "E317", {"start": v(-49.05, 36.14) * mm, "mid": v(-49.12, 35.91) * mm, "end": v(-49.2, 35.7) * mm});
            skArc(sketch, "E318", {"start": v(-49.2, 35.7) * mm, "mid": v(-49.34, 35.43) * mm, "end": v(-49.48, 35.17) * mm});
            skLineSegment(sketch, "E319", {"start": v(-49.48, 35.17) * mm, "end": v(-49.77, 34.69) * mm});
            skLineSegment(sketch, "E320", {"start": v(-49.77, 34.69) * mm, "end": v(-50.16, 35.14) * mm});
            skArc(sketch, "E321", {"start": v(-50.16, 35.14) * mm, "mid": v(-50.54, 35.65) * mm, "end": v(-50.86, 36.2) * mm});
            skArc(sketch, "E322", {"start": v(-50.86, 36.2) * mm, "mid": v(-51.08, 36.8) * mm, "end": v(-51.21, 37.4) * mm});
            skArc(sketch, "E323", {"start": v(-51.21, 37.4) * mm, "mid": v(-51.24, 37.94) * mm, "end": v(-51.17, 38.48) * mm});
            skArc(sketch, "E324", {"start": v(-51.17, 38.48) * mm, "mid": v(-51.02, 38.88) * mm, "end": v(-50.73, 39.21) * mm});
            skArc(sketch, "E325", {"start": v(-50.73, 39.21) * mm, "mid": v(-50.58, 39.32) * mm, "end": v(-50.41, 39.41) * mm});
            skArc(sketch, "E326", {"start": v(-50.41, 39.41) * mm, "mid": v(-50.26, 39.46) * mm, "end": v(-50.1, 39.47) * mm});
            skArc(sketch, "E327", {"start": v(-50.1, 39.47) * mm, "mid": v(-49.94, 39.44) * mm, "end": v(-49.8, 39.38) * mm});
            skArc(sketch, "E328", {"start": v(-49.8, 39.38) * mm, "mid": v(-49.63, 39.27) * mm, "end": v(-49.48, 39.14) * mm});
            skArc(sketch, "E329", {"start": v(-61.16, 33.66) * mm, "mid": v(-60.4, 33.53) * mm, "end": v(-59.65, 33.35) * mm});
            skArc(sketch, "E330", {"start": v(-59.65, 33.35) * mm, "mid": v(-58.83, 33.12) * mm, "end": v(-58.03, 32.86) * mm});
            skArc(sketch, "E331", {"start": v(-58.03, 32.86) * mm, "mid": v(-57.26, 32.57) * mm, "end": v(-56.5, 32.24) * mm});
            skArc(sketch, "E332", {"start": v(-56.5, 32.24) * mm, "mid": v(-55.88, 31.94) * mm, "end": v(-55.29, 31.59) * mm});
            skArc(sketch, "E333", {"start": v(-55.29, 31.59) * mm, "mid": v(-55.1, 31.46) * mm, "end": v(-54.9, 31.34) * mm});
            skArc(sketch, "E334", {"start": v(-54.9, 31.34) * mm, "mid": v(-54.83, 31.28) * mm, "end": v(-54.77, 31.22) * mm});
            skArc(sketch, "E335", {"start": v(-54.77, 31.22) * mm, "mid": v(-54.75, 31.18) * mm, "end": v(-54.75, 31.13) * mm});
            skArc(sketch, "E336", {"start": v(-54.75, 31.13) * mm, "mid": v(-54.78, 31.08) * mm, "end": v(-54.82, 31.04) * mm});
            skArc(sketch, "E337", {"start": v(-54.82, 31.04) * mm, "mid": v(-55, 30.93) * mm, "end": v(-55.2, 30.85) * mm});
            skArc(sketch, "E338", {"start": v(-55.2, 30.85) * mm, "mid": v(-55.72, 30.68) * mm, "end": v(-56.24, 30.52) * mm});
            skArc(sketch, "E339", {"start": v(-56.24, 30.52) * mm, "mid": v(-56.79, 30.36) * mm, "end": v(-57.34, 30.21) * mm});
            skArc(sketch, "E340", {"start": v(-57.34, 30.21) * mm, "mid": v(-57.77, 30.1) * mm, "end": v(-58.2, 30.02) * mm});
            skArc(sketch, "E341", {"start": v(-58.2, 30.02) * mm, "mid": v(-59.34, 29.88) * mm, "end": v(-60.47, 29.84) * mm});
            skArc(sketch, "E342", {"start": v(-60.47, 29.84) * mm, "mid": v(-61.66, 29.89) * mm, "end": v(-62.84, 30.03) * mm});
            skArc(sketch, "E343", {"start": v(-62.84, 30.03) * mm, "mid": v(-63.89, 30.24) * mm, "end": v(-64.91, 30.53) * mm});
            skArc(sketch, "E344", {"start": v(-64.91, 30.53) * mm, "mid": v(-65.6, 30.84) * mm, "end": v(-66.19, 31.3) * mm});
            skArc(sketch, "E345", {"start": v(-66.19, 31.3) * mm, "mid": v(-66.3, 31.4) * mm, "end": v(-66.4, 31.52) * mm});
            skArc(sketch, "E346", {"start": v(-66.4, 31.52) * mm, "mid": v(-66.47, 31.6) * mm, "end": v(-66.52, 31.69) * mm});
            skArc(sketch, "E347", {"start": v(-66.52, 31.69) * mm, "mid": v(-66.55, 31.77) * mm, "end": v(-66.57, 31.87) * mm});
            skArc(sketch, "E348", {"start": v(-66.57, 31.87) * mm, "mid": v(-66.58, 32) * mm, "end": v(-66.58, 32.13) * mm});
            skArc(sketch, "E349", {"start": v(-66.58, 32.13) * mm, "mid": v(-66.57, 32.34) * mm, "end": v(-66.52, 32.54) * mm});
            skArc(sketch, "E350", {"start": v(-66.52, 32.54) * mm, "mid": v(-66.44, 32.72) * mm, "end": v(-66.33, 32.89) * mm});
            skArc(sketch, "E351", {"start": v(-66.33, 32.89) * mm, "mid": v(-66.19, 33.04) * mm, "end": v(-66.01, 33.17) * mm});
            skArc(sketch, "E352", {"start": v(-66.01, 33.17) * mm, "mid": v(-65.78, 33.3) * mm, "end": v(-65.54, 33.41) * mm});
            skArc(sketch, "E353", {"start": v(-65.54, 33.41) * mm, "mid": v(-65.1, 33.56) * mm, "end": v(-64.66, 33.67) * mm});
            skArc(sketch, "E354", {"start": v(-64.66, 33.67) * mm, "mid": v(-64.15, 33.75) * mm, "end": v(-63.62, 33.8) * mm});
            skArc(sketch, "E355", {"start": v(-63.62, 33.8) * mm, "mid": v(-63.03, 33.81) * mm, "end": v(-62.44, 33.8) * mm});
            skArc(sketch, "E356", {"start": v(-62.44, 33.8) * mm, "mid": v(-61.8, 33.74) * mm, "end": v(-61.16, 33.66) * mm});
            skArc(sketch, "E357", {"start": v(-43.88, 33.64) * mm, "mid": v(-43.87, 33.58) * mm, "end": v(-43.84, 33.52) * mm});
            skArc(sketch, "E358", {"start": v(-43.84, 33.52) * mm, "mid": v(-43.55, 33.12) * mm, "end": v(-43.26, 32.71) * mm});
            skArc(sketch, "E359", {"start": v(-43.26, 32.71) * mm, "mid": v(-42.95, 32.3) * mm, "end": v(-42.64, 31.88) * mm});
            skArc(sketch, "E360", {"start": v(-42.64, 31.88) * mm, "mid": v(-42.34, 31.5) * mm, "end": v(-42.04, 31.12) * mm});
            skArc(sketch, "E361", {"start": v(-42.04, 31.12) * mm, "mid": v(-41.93, 30.98) * mm, "end": v(-41.82, 30.84) * mm});
            skArc(sketch, "E362", {"start": v(-41.82, 30.84) * mm, "mid": v(-41.73, 30.72) * mm, "end": v(-41.63, 30.6) * mm});
            skArc(sketch, "E363", {"start": v(-41.63, 30.6) * mm, "mid": v(-41.55, 30.5) * mm, "end": v(-41.47, 30.39) * mm});
            skArc(sketch, "E364", {"start": v(-41.47, 30.39) * mm, "mid": v(-41.47, 30.38) * mm, "end": v(-41.46, 30.36) * mm});
            skArc(sketch, "E365", {"start": v(-41.46, 30.36) * mm, "mid": v(-41.47, 30.35) * mm, "end": v(-41.48, 30.34) * mm});
            skArc(sketch, "E366", {"start": v(-41.48, 30.34) * mm, "mid": v(-41.57, 30.27) * mm, "end": v(-41.67, 30.2) * mm});
            skArc(sketch, "E367", {"start": v(-41.67, 30.2) * mm, "mid": v(-41.78, 30.12) * mm, "end": v(-41.89, 30.04) * mm});
            skArc(sketch, "E368", {"start": v(-41.89, 30.04) * mm, "mid": v(-42.02, 29.95) * mm, "end": v(-42.15, 29.86) * mm});
            skArc(sketch, "E369", {"start": v(-42.15, 29.86) * mm, "mid": v(-42.3, 29.76) * mm, "end": v(-42.46, 29.65) * mm});
            skArc(sketch, "E370", {"start": v(-42.46, 29.65) * mm, "mid": v(-42.63, 29.53) * mm, "end": v(-42.8, 29.4) * mm});
            skArc(sketch, "E371", {"start": v(-42.8, 29.4) * mm, "mid": v(-42.98, 29.28) * mm, "end": v(-43.14, 29.15) * mm});
            skArc(sketch, "E372", {"start": v(-43.14, 29.15) * mm, "mid": v(-43.28, 29.04) * mm, "end": v(-43.41, 28.94) * mm});
            skArc(sketch, "E373", {"start": v(-43.41, 28.94) * mm, "mid": v(-43.52, 28.85) * mm, "end": v(-43.64, 28.76) * mm});
            skArc(sketch, "E374", {"start": v(-43.64, 28.76) * mm, "mid": v(-43.74, 28.69) * mm, "end": v(-43.84, 28.61) * mm});
            skArc(sketch, "E375", {"start": v(-43.84, 28.61) * mm, "mid": v(-43.92, 28.55) * mm, "end": v(-44, 28.5) * mm});
            skArc(sketch, "E376", {"start": v(-44, 28.5) * mm, "mid": v(-44.03, 28.48) * mm, "end": v(-44.06, 28.48) * mm});
            skArc(sketch, "E377", {"start": v(-44.06, 28.48) * mm, "mid": v(-44.08, 28.48) * mm, "end": v(-44.1, 28.5) * mm});
            skArc(sketch, "E378", {"start": v(-44.1, 28.5) * mm, "mid": v(-44.16, 28.55) * mm, "end": v(-44.21, 28.6) * mm});
            skArc(sketch, "E379", {"start": v(-44.21, 28.6) * mm, "mid": v(-44.27, 28.68) * mm, "end": v(-44.33, 28.75) * mm});
            skArc(sketch, "E380", {"start": v(-44.33, 28.75) * mm, "mid": v(-44.4, 28.83) * mm, "end": v(-44.47, 28.92) * mm});
            skArc(sketch, "E381", {"start": v(-44.47, 28.92) * mm, "mid": v(-44.56, 29.04) * mm, "end": v(-44.66, 29.15) * mm});
            skArc(sketch, "E382", {"start": v(-44.66, 29.15) * mm, "mid": v(-44.82, 29.35) * mm, "end": v(-45, 29.54) * mm});
            skArc(sketch, "E383", {"start": v(-45, 29.54) * mm, "mid": v(-45.2, 29.76) * mm, "end": v(-45.4, 29.98) * mm});
            skArc(sketch, "E384", {"start": v(-45.4, 29.98) * mm, "mid": v(-45.6, 30.2) * mm, "end": v(-45.8, 30.42) * mm});
            skLineSegment(sketch, "E385", {"start": v(-45.8, 30.42) * mm, "end": v(-46.81, 31.48) * mm});
            skLineSegment(sketch, "E386", {"start": v(-46.81, 31.48) * mm, "end": v(-45.56, 32.45) * mm});
            skArc(sketch, "E387", {"start": v(-45.56, 32.45) * mm, "mid": v(-45.31, 32.64) * mm, "end": v(-45.07, 32.84) * mm});
            skArc(sketch, "E388", {"start": v(-45.07, 32.84) * mm, "mid": v(-44.85, 33) * mm, "end": v(-44.64, 33.18) * mm});
            skArc(sketch, "E389", {"start": v(-44.64, 33.18) * mm, "mid": v(-44.46, 33.33) * mm, "end": v(-44.28, 33.48) * mm});
            skArc(sketch, "E390", {"start": v(-44.28, 33.48) * mm, "mid": v(-44.23, 33.52) * mm, "end": v(-44.18, 33.57) * mm});
            skArc(sketch, "E391", {"start": v(-44.18, 33.57) * mm, "mid": v(-44.14, 33.62) * mm, "end": v(-44.08, 33.67) * mm});
            skArc(sketch, "E392", {"start": v(-44.08, 33.67) * mm, "mid": v(-44.04, 33.7) * mm, "end": v(-43.98, 33.71) * mm});
            skArc(sketch, "E393", {"start": v(-43.98, 33.71) * mm, "mid": v(-43.95, 33.72) * mm, "end": v(-43.91, 33.7) * mm});
            skArc(sketch, "E394", {"start": v(-43.91, 33.7) * mm, "mid": v(-43.9, 33.68) * mm, "end": v(-43.88, 33.64) * mm});
            skArc(sketch, "E395", {"start": v(-49.35, 32.22) * mm, "mid": v(-49.15, 32) * mm, "end": v(-48.95, 31.79) * mm});
            skArc(sketch, "E396", {"start": v(-48.95, 31.79) * mm, "mid": v(-48.79, 31.6) * mm, "end": v(-48.62, 31.41) * mm});
            skArc(sketch, "E397", {"start": v(-48.62, 31.41) * mm, "mid": v(-48.48, 31.25) * mm, "end": v(-48.35, 31.08) * mm});
            skArc(sketch, "E398", {"start": v(-48.35, 31.08) * mm, "mid": v(-48.33, 31.05) * mm, "end": v(-48.32, 31.02) * mm});
            skArc(sketch, "E399", {"start": v(-48.32, 31.02) * mm, "mid": v(-48.33, 31) * mm, "end": v(-48.34, 30.97) * mm});
            skArc(sketch, "E400", {"start": v(-48.34, 30.97) * mm, "mid": v(-48.37, 30.93) * mm, "end": v(-48.4, 30.9) * mm});
            skArc(sketch, "E401", {"start": v(-48.4, 30.9) * mm, "mid": v(-48.45, 30.85) * mm, "end": v(-48.5, 30.81) * mm});
            skArc(sketch, "E402", {"start": v(-48.5, 30.81) * mm, "mid": v(-48.55, 30.77) * mm, "end": v(-48.6, 30.74) * mm});
            skArc(sketch, "E403", {"start": v(-48.6, 30.74) * mm, "mid": v(-48.68, 30.68) * mm, "end": v(-48.76, 30.63) * mm});
            skArc(sketch, "E404", {"start": v(-48.76, 30.63) * mm, "mid": v(-48.9, 30.52) * mm, "end": v(-49.06, 30.4) * mm});
            skArc(sketch, "E405", {"start": v(-49.06, 30.4) * mm, "mid": v(-49.23, 30.27) * mm, "end": v(-49.4, 30.14) * mm});
            skArc(sketch, "E406", {"start": v(-49.4, 30.14) * mm, "mid": v(-49.59, 30) * mm, "end": v(-49.77, 29.85) * mm});
            skLineSegment(sketch, "E407", {"start": v(-49.77, 29.85) * mm, "end": v(-50.66, 29.15) * mm});
            skLineSegment(sketch, "E408", {"start": v(-50.66, 29.15) * mm, "end": v(-51.13, 29.7) * mm});
            skArc(sketch, "E409", {"start": v(-51.13, 29.7) * mm, "mid": v(-51.24, 29.82) * mm, "end": v(-51.35, 29.95) * mm});
            skArc(sketch, "E410", {"start": v(-51.35, 29.95) * mm, "mid": v(-51.5, 30.1) * mm, "end": v(-51.65, 30.26) * mm});
            skArc(sketch, "E411", {"start": v(-51.65, 30.26) * mm, "mid": v(-51.8, 30.42) * mm, "end": v(-51.96, 30.58) * mm});
            skArc(sketch, "E412", {"start": v(-51.96, 30.58) * mm, "mid": v(-52.1, 30.72) * mm, "end": v(-52.25, 30.86) * mm});
            skLineSegment(sketch, "E413", {"start": v(-52.25, 30.86) * mm, "end": v(-52.9, 31.47) * mm});
            skLineSegment(sketch, "E414", {"start": v(-52.9, 31.47) * mm, "end": v(-52.3, 31.88) * mm});
            skArc(sketch, "E415", {"start": v(-52.3, 31.88) * mm, "mid": v(-52.16, 31.98) * mm, "end": v(-52.03, 32.08) * mm});
            skArc(sketch, "E416", {"start": v(-52.03, 32.08) * mm, "mid": v(-51.86, 32.2) * mm, "end": v(-51.7, 32.32) * mm});
            skArc(sketch, "E417", {"start": v(-51.7, 32.32) * mm, "mid": v(-51.54, 32.45) * mm, "end": v(-51.37, 32.58) * mm});
            skArc(sketch, "E418", {"start": v(-51.37, 32.58) * mm, "mid": v(-51.23, 32.69) * mm, "end": v(-51.1, 32.8) * mm});
            skArc(sketch, "E419", {"start": v(-51.1, 32.8) * mm, "mid": v(-50.98, 32.9) * mm, "end": v(-50.86, 33) * mm});
            skArc(sketch, "E420", {"start": v(-50.86, 33) * mm, "mid": v(-50.76, 33.08) * mm, "end": v(-50.65, 33.16) * mm});
            skArc(sketch, "E421", {"start": v(-50.65, 33.16) * mm, "mid": v(-50.56, 33.23) * mm, "end": v(-50.47, 33.3) * mm});
            skArc(sketch, "E422", {"start": v(-50.47, 33.3) * mm, "mid": v(-50.45, 33.3) * mm, "end": v(-50.43, 33.31) * mm});
            skArc(sketch, "E423", {"start": v(-50.43, 33.31) * mm, "mid": v(-50.4, 33.3) * mm, "end": v(-50.39, 33.3) * mm});
            skArc(sketch, "E424", {"start": v(-50.39, 33.3) * mm, "mid": v(-50.24, 33.14) * mm, "end": v(-50.09, 33) * mm});
            skArc(sketch, "E425", {"start": v(-50.09, 33) * mm, "mid": v(-49.91, 32.82) * mm, "end": v(-49.74, 32.64) * mm});
            skArc(sketch, "E426", {"start": v(-49.74, 32.64) * mm, "mid": v(-49.54, 32.43) * mm, "end": v(-49.35, 32.22) * mm});
            skArc(sketch, "E427", {"start": v(-36.54, 31.68) * mm, "mid": v(-36.38, 31.47) * mm, "end": v(-36.23, 31.27) * mm});
            skArc(sketch, "E428", {"start": v(-36.23, 31.27) * mm, "mid": v(-36.05, 31.05) * mm, "end": v(-35.87, 30.83) * mm});
            skArc(sketch, "E429", {"start": v(-35.87, 30.83) * mm, "mid": v(-35.7, 30.62) * mm, "end": v(-35.54, 30.4) * mm});
            skArc(sketch, "E430", {"start": v(-35.54, 30.4) * mm, "mid": v(-35.4, 30.25) * mm, "end": v(-35.27, 30.1) * mm});
            skArc(sketch, "E431", {"start": v(-35.27, 30.1) * mm, "mid": v(-35.17, 29.97) * mm, "end": v(-35.06, 29.84) * mm});
            skArc(sketch, "E432", {"start": v(-35.06, 29.84) * mm, "mid": v(-34.98, 29.73) * mm, "end": v(-34.9, 29.61) * mm});
            skArc(sketch, "E433", {"start": v(-34.9, 29.61) * mm, "mid": v(-34.83, 29.52) * mm, "end": v(-34.76, 29.42) * mm});
            skArc(sketch, "E434", {"start": v(-34.76, 29.42) * mm, "mid": v(-34.75, 29.4) * mm, "end": v(-34.76, 29.37) * mm});
            skArc(sketch, "E435", {"start": v(-34.76, 29.37) * mm, "mid": v(-34.78, 29.35) * mm, "end": v(-34.8, 29.33) * mm});
            skArc(sketch, "E436", {"start": v(-34.8, 29.33) * mm, "mid": v(-34.9, 29.27) * mm, "end": v(-35, 29.2) * mm});
            skArc(sketch, "E437", {"start": v(-35, 29.2) * mm, "mid": v(-35.13, 29.12) * mm, "end": v(-35.25, 29.05) * mm});
            skArc(sketch, "E438", {"start": v(-35.25, 29.05) * mm, "mid": v(-35.4, 28.96) * mm, "end": v(-35.53, 28.88) * mm});
            skArc(sketch, "E439", {"start": v(-35.53, 28.88) * mm, "mid": v(-35.7, 28.78) * mm, "end": v(-35.85, 28.68) * mm});
            skArc(sketch, "E440", {"start": v(-35.85, 28.68) * mm, "mid": v(-36.03, 28.57) * mm, "end": v(-36.2, 28.46) * mm});
            skArc(sketch, "E441", {"start": v(-36.2, 28.46) * mm, "mid": v(-36.37, 28.35) * mm, "end": v(-36.53, 28.25) * mm});
            skArc(sketch, "E442", {"start": v(-36.53, 28.25) * mm, "mid": v(-36.65, 28.16) * mm, "end": v(-36.77, 28.07) * mm});
            skLineSegment(sketch, "E443", {"start": v(-36.77, 28.07) * mm, "end": v(-37.28, 27.7) * mm});
            skLineSegment(sketch, "E444", {"start": v(-37.28, 27.7) * mm, "end": v(-38.54, 29.21) * mm});
            skArc(sketch, "E445", {"start": v(-38.54, 29.21) * mm, "mid": v(-38.78, 29.5) * mm, "end": v(-39.02, 29.8) * mm});
            skArc(sketch, "E446", {"start": v(-39.02, 29.8) * mm, "mid": v(-39.23, 30.05) * mm, "end": v(-39.43, 30.3) * mm});
            skArc(sketch, "E447", {"start": v(-39.43, 30.3) * mm, "mid": v(-39.6, 30.52) * mm, "end": v(-39.79, 30.74) * mm});
            skArc(sketch, "E448", {"start": v(-39.79, 30.74) * mm, "mid": v(-39.8, 30.75) * mm, "end": v(-39.8, 30.77) * mm});
            skArc(sketch, "E449", {"start": v(-39.8, 30.77) * mm, "mid": v(-39.8, 30.78) * mm, "end": v(-39.78, 30.8) * mm});
            skArc(sketch, "E450", {"start": v(-39.78, 30.8) * mm, "mid": v(-39.17, 31.25) * mm, "end": v(-38.55, 31.7) * mm});
            skArc(sketch, "E451", {"start": v(-38.55, 31.7) * mm, "mid": v(-37.94, 32.14) * mm, "end": v(-37.33, 32.58) * mm});
            skArc(sketch, "E452", {"start": v(-37.33, 32.58) * mm, "mid": v(-37.3, 32.6) * mm, "end": v(-37.27, 32.6) * mm});
            skArc(sketch, "E453", {"start": v(-37.27, 32.6) * mm, "mid": v(-37.26, 32.6) * mm, "end": v(-37.26, 32.6) * mm});
            skArc(sketch, "E454", {"start": v(-37.26, 32.6) * mm, "mid": v(-37.15, 32.47) * mm, "end": v(-37.05, 32.34) * mm});
            skArc(sketch, "E455", {"start": v(-37.05, 32.34) * mm, "mid": v(-36.93, 32.19) * mm, "end": v(-36.82, 32.04) * mm});
            skArc(sketch, "E456", {"start": v(-36.82, 32.04) * mm, "mid": v(-36.68, 31.86) * mm, "end": v(-36.54, 31.68) * mm});
            skArc(sketch, "E457", {"start": v(-50.81, 27.22) * mm, "mid": v(-50.64, 26.9) * mm, "end": v(-50.48, 26.59) * mm});
            skArc(sketch, "E458", {"start": v(-50.48, 26.59) * mm, "mid": v(-50.36, 26.3) * mm, "end": v(-50.27, 26.03) * mm});
            skArc(sketch, "E459", {"start": v(-50.27, 26.03) * mm, "mid": v(-50.2, 25.74) * mm, "end": v(-50.15, 25.44) * mm});
            skArc(sketch, "E460", {"start": v(-50.15, 25.44) * mm, "mid": v(-50.12, 25.1) * mm, "end": v(-50.1, 24.74) * mm});
            skArc(sketch, "E461", {"start": v(-50.1, 24.74) * mm, "mid": v(-50.1, 24.52) * mm, "end": v(-50.1, 24.3) * mm});
            skArc(sketch, "E462", {"start": v(-50.1, 24.3) * mm, "mid": v(-50.11, 24.15) * mm, "end": v(-50.13, 24) * mm});
            skArc(sketch, "E463", {"start": v(-50.13, 24) * mm, "mid": v(-50.15, 23.88) * mm, "end": v(-50.18, 23.76) * mm});
            skArc(sketch, "E464", {"start": v(-50.18, 23.76) * mm, "mid": v(-50.22, 23.66) * mm, "end": v(-50.27, 23.56) * mm});
            skArc(sketch, "E465", {"start": v(-50.27, 23.56) * mm, "mid": v(-50.48, 23.27) * mm, "end": v(-50.75, 23.04) * mm});
            skArc(sketch, "E466", {"start": v(-50.75, 23.04) * mm, "mid": v(-51.06, 22.9) * mm, "end": v(-51.39, 22.88) * mm});
            skArc(sketch, "E467", {"start": v(-51.39, 22.88) * mm, "mid": v(-51.7, 22.95) * mm, "end": v(-51.98, 23.13) * mm});
            skArc(sketch, "E468", {"start": v(-51.98, 23.13) * mm, "mid": v(-52.22, 23.4) * mm, "end": v(-52.37, 23.72) * mm});
            skArc(sketch, "E469", {"start": v(-52.37, 23.72) * mm, "mid": v(-52.43, 23.94) * mm, "end": v(-52.46, 24.17) * mm});
            skArc(sketch, "E470", {"start": v(-52.46, 24.17) * mm, "mid": v(-52.48, 24.48) * mm, "end": v(-52.48, 24.8) * mm});
            skArc(sketch, "E471", {"start": v(-52.48, 24.8) * mm, "mid": v(-52.46, 25.13) * mm, "end": v(-52.43, 25.45) * mm});
            skArc(sketch, "E472", {"start": v(-52.43, 25.45) * mm, "mid": v(-52.38, 25.74) * mm, "end": v(-52.31, 26.02) * mm});
            skArc(sketch, "E473", {"start": v(-52.31, 26.02) * mm, "mid": v(-52.23, 26.25) * mm, "end": v(-52.13, 26.48) * mm});
            skArc(sketch, "E474", {"start": v(-52.13, 26.48) * mm, "mid": v(-51.96, 26.81) * mm, "end": v(-51.78, 27.14) * mm});
            skArc(sketch, "E475", {"start": v(-51.78, 27.14) * mm, "mid": v(-51.59, 27.46) * mm, "end": v(-51.4, 27.8) * mm});
            skArc(sketch, "E476", {"start": v(-51.4, 27.8) * mm, "mid": v(-51.33, 27.85) * mm, "end": v(-51.25, 27.87) * mm});
            skArc(sketch, "E477", {"start": v(-51.25, 27.87) * mm, "mid": v(-51.23, 27.86) * mm, "end": v(-51.22, 27.85) * mm});
            skArc(sketch, "E478", {"start": v(-51.22, 27.85) * mm, "mid": v(-51.16, 27.76) * mm, "end": v(-51.1, 27.68) * mm});
            skArc(sketch, "E479", {"start": v(-51.1, 27.68) * mm, "mid": v(-51.03, 27.57) * mm, "end": v(-50.96, 27.46) * mm});
            skArc(sketch, "E480", {"start": v(-50.96, 27.46) * mm, "mid": v(-50.89, 27.34) * mm, "end": v(-50.81, 27.22) * mm});
            skArc(sketch, "E481", {"start": v(-44.19, 26.18) * mm, "mid": v(-43.97, 25.82) * mm, "end": v(-43.77, 25.45) * mm});
            skArc(sketch, "E482", {"start": v(-43.77, 25.45) * mm, "mid": v(-43.6, 25.1) * mm, "end": v(-43.48, 24.72) * mm});
            skArc(sketch, "E483", {"start": v(-43.48, 24.72) * mm, "mid": v(-43.38, 24.36) * mm, "end": v(-43.3, 23.98) * mm});
            skArc(sketch, "E484", {"start": v(-43.3, 23.98) * mm, "mid": v(-43.26, 23.59) * mm, "end": v(-43.24, 23.19) * mm});
            skArc(sketch, "E485", {"start": v(-43.24, 23.19) * mm, "mid": v(-43.24, 22.97) * mm, "end": v(-43.25, 22.76) * mm});
            skArc(sketch, "E486", {"start": v(-43.25, 22.76) * mm, "mid": v(-43.26, 22.6) * mm, "end": v(-43.28, 22.45) * mm});
            skArc(sketch, "E487", {"start": v(-43.28, 22.45) * mm, "mid": v(-43.3, 22.33) * mm, "end": v(-43.35, 22.2) * mm});
            skArc(sketch, "E488", {"start": v(-43.35, 22.2) * mm, "mid": v(-43.4, 22.08) * mm, "end": v(-43.45, 21.96) * mm});
            skArc(sketch, "E489", {"start": v(-43.45, 21.96) * mm, "mid": v(-43.68, 21.64) * mm, "end": v(-43.98, 21.4) * mm});
            skArc(sketch, "E490", {"start": v(-43.98, 21.4) * mm, "mid": v(-44.32, 21.28) * mm, "end": v(-44.68, 21.26) * mm});
            skArc(sketch, "E491", {"start": v(-44.68, 21.26) * mm, "mid": v(-45.05, 21.36) * mm, "end": v(-45.37, 21.57) * mm});
            skArc(sketch, "E492", {"start": v(-45.37, 21.57) * mm, "mid": v(-45.65, 21.88) * mm, "end": v(-45.86, 22.24) * mm});
            skArc(sketch, "E493", {"start": v(-45.86, 22.24) * mm, "mid": v(-45.95, 22.52) * mm, "end": v(-46, 22.8) * mm});
            skArc(sketch, "E494", {"start": v(-46, 22.8) * mm, "mid": v(-46.03, 23.17) * mm, "end": v(-46.03, 23.53) * mm});
            skArc(sketch, "E495", {"start": v(-46.03, 23.53) * mm, "mid": v(-46, 23.93) * mm, "end": v(-45.95, 24.32) * mm});
            skArc(sketch, "E496", {"start": v(-45.95, 24.32) * mm, "mid": v(-45.88, 24.7) * mm, "end": v(-45.77, 25.08) * mm});
            skArc(sketch, "E497", {"start": v(-45.77, 25.08) * mm, "mid": v(-45.67, 25.37) * mm, "end": v(-45.55, 25.66) * mm});
            skArc(sketch, "E498", {"start": v(-45.55, 25.66) * mm, "mid": v(-45.4, 25.99) * mm, "end": v(-45.24, 26.3) * mm});
            skArc(sketch, "E499", {"start": v(-45.24, 26.3) * mm, "mid": v(-45.08, 26.6) * mm, "end": v(-44.92, 26.88) * mm});
            skArc(sketch, "E500", {"start": v(-44.92, 26.88) * mm, "mid": v(-44.86, 26.94) * mm, "end": v(-44.78, 26.96) * mm});
            skArc(sketch, "E501", {"start": v(-44.78, 26.96) * mm, "mid": v(-44.75, 26.96) * mm, "end": v(-44.73, 26.94) * mm});
            skArc(sketch, "E502", {"start": v(-44.73, 26.94) * mm, "mid": v(-44.65, 26.84) * mm, "end": v(-44.57, 26.73) * mm});
            skArc(sketch, "E503", {"start": v(-44.57, 26.73) * mm, "mid": v(-44.48, 26.6) * mm, "end": v(-44.4, 26.48) * mm});
            skArc(sketch, "E504", {"start": v(-44.4, 26.48) * mm, "mid": v(-44.29, 26.33) * mm, "end": v(-44.19, 26.18) * mm});
            skArc(sketch, "E505", {"start": v(-37.66, 25.62) * mm, "mid": v(-37.29, 25.1) * mm, "end": v(-36.94, 24.58) * mm});
            skArc(sketch, "E506", {"start": v(-36.94, 24.58) * mm, "mid": v(-36.66, 24.1) * mm, "end": v(-36.42, 23.6) * mm});
            skArc(sketch, "E507", {"start": v(-36.42, 23.6) * mm, "mid": v(-36.24, 23.16) * mm, "end": v(-36.09, 22.7) * mm});
            skArc(sketch, "E508", {"start": v(-36.09, 22.7) * mm, "mid": v(-36, 22.28) * mm, "end": v(-35.94, 21.84) * mm});
            skArc(sketch, "E509", {"start": v(-35.94, 21.84) * mm, "mid": v(-35.93, 21.5) * mm, "end": v(-35.93, 21.15) * mm});
            skArc(sketch, "E510", {"start": v(-35.93, 21.15) * mm, "mid": v(-35.97, 20.87) * mm, "end": v(-36.03, 20.6) * mm});
            skArc(sketch, "E511", {"start": v(-36.03, 20.6) * mm, "mid": v(-36.13, 20.36) * mm, "end": v(-36.26, 20.14) * mm});
            skArc(sketch, "E512", {"start": v(-36.26, 20.14) * mm, "mid": v(-36.43, 19.9) * mm, "end": v(-36.62, 19.68) * mm});
            skArc(sketch, "E513", {"start": v(-36.62, 19.68) * mm, "mid": v(-36.76, 19.53) * mm, "end": v(-36.91, 19.39) * mm});
            skArc(sketch, "E514", {"start": v(-36.91, 19.39) * mm, "mid": v(-37, 19.32) * mm, "end": v(-37.1, 19.26) * mm});
            skArc(sketch, "E515", {"start": v(-37.1, 19.26) * mm, "mid": v(-37.2, 19.23) * mm, "end": v(-37.3, 19.2) * mm});
            skArc(sketch, "E516", {"start": v(-37.3, 19.2) * mm, "mid": v(-37.45, 19.2) * mm, "end": v(-37.61, 19.2) * mm});
            skArc(sketch, "E517", {"start": v(-37.61, 19.2) * mm, "mid": v(-37.76, 19.2) * mm, "end": v(-37.91, 19.2) * mm});
            skArc(sketch, "E518", {"start": v(-37.91, 19.2) * mm, "mid": v(-38.01, 19.22) * mm, "end": v(-38.11, 19.25) * mm});
            skArc(sketch, "E519", {"start": v(-38.11, 19.25) * mm, "mid": v(-38.2, 19.3) * mm, "end": v(-38.3, 19.35) * mm});
            skArc(sketch, "E520", {"start": v(-38.3, 19.35) * mm, "mid": v(-38.4, 19.45) * mm, "end": v(-38.52, 19.55) * mm});
            skArc(sketch, "E521", {"start": v(-38.52, 19.55) * mm, "mid": v(-38.72, 19.75) * mm, "end": v(-38.9, 19.97) * mm});
            skArc(sketch, "E522", {"start": v(-38.9, 19.97) * mm, "mid": v(-39.04, 20.22) * mm, "end": v(-39.16, 20.49) * mm});
            skArc(sketch, "E523", {"start": v(-39.16, 20.49) * mm, "mid": v(-39.27, 20.8) * mm, "end": v(-39.34, 21.11) * mm});
            skArc(sketch, "E524", {"start": v(-39.34, 21.11) * mm, "mid": v(-39.4, 21.5) * mm, "end": v(-39.42, 21.88) * mm});
            skArc(sketch, "E525", {"start": v(-39.42, 21.88) * mm, "mid": v(-39.43, 22.24) * mm, "end": v(-39.43, 22.61) * mm});
            skArc(sketch, "E526", {"start": v(-39.43, 22.61) * mm, "mid": v(-39.4, 22.98) * mm, "end": v(-39.36, 23.34) * mm});
            skArc(sketch, "E527", {"start": v(-39.36, 23.34) * mm, "mid": v(-39.3, 23.7) * mm, "end": v(-39.24, 24.05) * mm});
            skArc(sketch, "E528", {"start": v(-39.24, 24.05) * mm, "mid": v(-39.15, 24.38) * mm, "end": v(-39.05, 24.7) * mm});
            skArc(sketch, "E529", {"start": v(-39.05, 24.7) * mm, "mid": v(-38.96, 24.93) * mm, "end": v(-38.86, 25.14) * mm});
            skArc(sketch, "E530", {"start": v(-38.86, 25.14) * mm, "mid": v(-38.72, 25.39) * mm, "end": v(-38.58, 25.63) * mm});
            skArc(sketch, "E531", {"start": v(-38.58, 25.63) * mm, "mid": v(-38.43, 25.86) * mm, "end": v(-38.28, 26.08) * mm});
            skArc(sketch, "E532", {"start": v(-38.28, 26.08) * mm, "mid": v(-38.22, 26.13) * mm, "end": v(-38.14, 26.15) * mm});
            skArc(sketch, "E533", {"start": v(-38.14, 26.15) * mm, "mid": v(-38.11, 26.15) * mm, "end": v(-38.1, 26.13) * mm});
            skArc(sketch, "E534", {"start": v(-38.1, 26.13) * mm, "mid": v(-38.03, 26.07) * mm, "end": v(-37.96, 26) * mm});
            skArc(sketch, "E535", {"start": v(-37.96, 26) * mm, "mid": v(-37.89, 25.91) * mm, "end": v(-37.82, 25.83) * mm});
            skArc(sketch, "E536", {"start": v(-37.82, 25.83) * mm, "mid": v(-37.74, 25.73) * mm, "end": v(-37.66, 25.62) * mm});
            skArc(sketch, "E537.MirrorCS", {"start": v(42.04, 31.12) * mm, "mid": v(41.93, 30.98) * mm, "end": v(41.82, 30.84) * mm});
            skArc(sketch, "E538.MirrorCS", {"start": v(44.06, 28.48) * mm, "mid": v(44.08, 28.48) * mm, "end": v(44.1, 28.5) * mm});
            skArc(sketch, "E539.MirrorCS", {"start": v(44.1, 28.5) * mm, "mid": v(44.16, 28.55) * mm, "end": v(44.21, 28.6) * mm});
            skArc(sketch, "E540.MirrorCS", {"start": v(41.82, 30.84) * mm, "mid": v(41.73, 30.72) * mm, "end": v(41.63, 30.6) * mm});
            skArc(sketch, "E541.MirrorCS", {"start": v(44.21, 28.6) * mm, "mid": v(44.27, 28.68) * mm, "end": v(44.33, 28.75) * mm});
            skArc(sketch, "E542.MirrorCS", {"start": v(41.63, 30.6) * mm, "mid": v(41.55, 30.5) * mm, "end": v(41.47, 30.39) * mm});
            skArc(sketch, "E543.MirrorCS", {"start": v(44.33, 28.75) * mm, "mid": v(44.4, 28.83) * mm, "end": v(44.47, 28.92) * mm});
            skArc(sketch, "E544.MirrorCS", {"start": v(41.47, 30.39) * mm, "mid": v(41.47, 30.38) * mm, "end": v(41.46, 30.36) * mm});
            skArc(sketch, "E545.MirrorCS", {"start": v(42, 29.34) * mm, "mid": v(41.78, 29.5) * mm, "end": v(41.55, 29.66) * mm});
            skArc(sketch, "E546.MirrorCS", {"start": v(43.41, 28.94) * mm, "mid": v(43.52, 28.85) * mm, "end": v(43.64, 28.76) * mm});
            skArc(sketch, "E547.MirrorCS", {"start": v(39.43, 30.3) * mm, "mid": v(39.6, 30.52) * mm, "end": v(39.79, 30.74) * mm});
            skArc(sketch, "E548.MirrorCS", {"start": v(41.1, 29.89) * mm, "mid": v(41.05, 29.88) * mm, "end": v(41, 29.86) * mm});
            skArc(sketch, "E549.MirrorCS", {"start": v(41.46, 30.36) * mm, "mid": v(41.47, 30.35) * mm, "end": v(41.48, 30.34) * mm});
            skArc(sketch, "E550.MirrorCS", {"start": v(41.55, 29.66) * mm, "mid": v(41.42, 29.74) * mm, "end": v(41.28, 29.82) * mm});
            skArc(sketch, "E551.MirrorCS", {"start": v(43.64, 28.76) * mm, "mid": v(43.74, 28.69) * mm, "end": v(43.84, 28.61) * mm});
            skArc(sketch, "E552.MirrorCS", {"start": v(42.46, 29.65) * mm, "mid": v(42.63, 29.53) * mm, "end": v(42.8, 29.4) * mm});
            skArc(sketch, "E553.MirrorCS", {"start": v(39.79, 30.74) * mm, "mid": v(39.8, 30.75) * mm, "end": v(39.8, 30.77) * mm});
            skArc(sketch, "E554.MirrorCS", {"start": v(41, 29.86) * mm, "mid": v(40.97, 29.8) * mm, "end": v(40.93, 29.76) * mm});
            skArc(sketch, "E555.MirrorCS", {"start": v(41.48, 30.34) * mm, "mid": v(41.57, 30.27) * mm, "end": v(41.67, 30.2) * mm});
            skArc(sketch, "E556.MirrorCS", {"start": v(41.28, 29.82) * mm, "mid": v(41.2, 29.86) * mm, "end": v(41.1, 29.89) * mm});
            skArc(sketch, "E557.MirrorCS", {"start": v(40.2, 31.25) * mm, "mid": v(40.41, 31.5) * mm, "end": v(40.62, 31.74) * mm});
            skArc(sketch, "E558.MirrorCS", {"start": v(42.76, 28.78) * mm, "mid": v(42.57, 28.93) * mm, "end": v(42.37, 29.07) * mm});
            skArc(sketch, "E559.MirrorCS", {"start": v(40.05, 31.23) * mm, "mid": v(40.1, 31.21) * mm, "end": v(40.15, 31.22) * mm});
            skArc(sketch, "E560.MirrorCS", {"start": v(39.12, 31.84) * mm, "mid": v(39.59, 31.53) * mm, "end": v(40.05, 31.23) * mm});
            skArc(sketch, "E561.MirrorCS", {"start": v(43.33, 28.34) * mm, "mid": v(43.22, 28.43) * mm, "end": v(43.1, 28.52) * mm});
            skArc(sketch, "E562.MirrorCS", {"start": v(43.84, 28.61) * mm, "mid": v(43.92, 28.55) * mm, "end": v(44, 28.5) * mm});
            skArc(sketch, "E563.MirrorCS", {"start": v(42.8, 29.4) * mm, "mid": v(42.98, 29.28) * mm, "end": v(43.14, 29.15) * mm});
            skArc(sketch, "E564.MirrorCS", {"start": v(39.8, 30.77) * mm, "mid": v(39.8, 30.78) * mm, "end": v(39.78, 30.8) * mm});
            skArc(sketch, "E565.MirrorCS", {"start": v(41.89, 30.04) * mm, "mid": v(42.02, 29.95) * mm, "end": v(42.15, 29.86) * mm});
            skArc(sketch, "E566.MirrorCS", {"start": v(40.93, 29.76) * mm, "mid": v(40.75, 29.54) * mm, "end": v(40.57, 29.31) * mm});
            skArc(sketch, "E567.MirrorCS", {"start": v(41.67, 30.2) * mm, "mid": v(41.78, 30.12) * mm, "end": v(41.89, 30.04) * mm});
            skArc(sketch, "E568.MirrorCS", {"start": v(40.62, 31.74) * mm, "mid": v(40.86, 32.01) * mm, "end": v(41.1, 32.29) * mm});
            skArc(sketch, "E569.MirrorCS", {"start": v(43.1, 28.52) * mm, "mid": v(42.93, 28.65) * mm, "end": v(42.76, 28.78) * mm});
            skArc(sketch, "E570.MirrorCS", {"start": v(38.27, 32.4) * mm, "mid": v(38.7, 32.12) * mm, "end": v(39.12, 31.84) * mm});
            skArc(sketch, "E571.MirrorCS", {"start": v(44, 28.5) * mm, "mid": v(44.03, 28.48) * mm, "end": v(44.06, 28.48) * mm});
            skArc(sketch, "E572.MirrorCS", {"start": v(42.64, 31.88) * mm, "mid": v(42.34, 31.5) * mm, "end": v(42.04, 31.12) * mm});
            skArc(sketch, "E573.MirrorCS", {"start": v(40.15, 31.22) * mm, "mid": v(40.18, 31.23) * mm, "end": v(40.2, 31.25) * mm});
            skArc(sketch, "E574.MirrorCS", {"start": v(43.26, 32.71) * mm, "mid": v(42.95, 32.3) * mm, "end": v(42.64, 31.88) * mm});
            skArc(sketch, "E575.MirrorCS", {"start": v(43.84, 33.52) * mm, "mid": v(43.55, 33.12) * mm, "end": v(43.26, 32.71) * mm});
            skLineSegment(sketch, "E576.MirrorCS", {"start": v(43.77, 27.97) * mm, "end": v(43.33, 28.34) * mm});
            skLineSegment(sketch, "E577.MirrorCS", {"start": v(43.42, 27.4) * mm, "end": v(43.77, 27.97) * mm});
            skArc(sketch, "E578.MirrorCS", {"start": v(43.14, 29.15) * mm, "mid": v(43.28, 29.04) * mm, "end": v(43.41, 28.94) * mm});
            skArc(sketch, "E579.MirrorCS", {"start": v(39.78, 30.8) * mm, "mid": v(39.17, 31.25) * mm, "end": v(38.55, 31.7) * mm});
            skArc(sketch, "E580.MirrorCS", {"start": v(40.15, 28.79) * mm, "mid": v(39.9, 28.49) * mm, "end": v(39.67, 28.2) * mm});
            skArc(sketch, "E581.MirrorCS", {"start": v(42.15, 29.86) * mm, "mid": v(42.3, 29.76) * mm, "end": v(42.46, 29.65) * mm});
            skArc(sketch, "E582.MirrorCS", {"start": v(40.57, 29.31) * mm, "mid": v(40.36, 29.05) * mm, "end": v(40.15, 28.79) * mm});
            skArc(sketch, "E583.MirrorCS", {"start": v(39.02, 29.8) * mm, "mid": v(39.23, 30.05) * mm, "end": v(39.43, 30.3) * mm});
            skArc(sketch, "E584.MirrorCS", {"start": v(48.35, 31.08) * mm, "mid": v(48.33, 31.05) * mm, "end": v(48.32, 31.02) * mm});
            skArc(sketch, "E585.MirrorCS", {"start": v(38.54, 29.21) * mm, "mid": v(38.78, 29.5) * mm, "end": v(39.02, 29.8) * mm});
            skArc(sketch, "E586.MirrorCS", {"start": v(41.1, 32.29) * mm, "mid": v(41.38, 32.61) * mm, "end": v(41.66, 32.94) * mm});
            skArc(sketch, "E587.MirrorCS", {"start": v(42.37, 29.07) * mm, "mid": v(42.19, 29.2) * mm, "end": v(42, 29.34) * mm});
            skArc(sketch, "E588.MirrorCS", {"start": v(48.32, 31.02) * mm, "mid": v(48.33, 31) * mm, "end": v(48.34, 30.97) * mm});
            skArc(sketch, "E589.MirrorCS", {"start": v(51.1, 32.8) * mm, "mid": v(50.98, 32.9) * mm, "end": v(50.86, 33) * mm});
            skArc(sketch, "E590.MirrorCS", {"start": v(48.34, 30.97) * mm, "mid": v(48.37, 30.93) * mm, "end": v(48.4, 30.9) * mm});
            skArc(sketch, "E591.MirrorCS", {"start": v(45.48, 27.89) * mm, "mid": v(45.34, 27.72) * mm, "end": v(45.2, 27.55) * mm});
            skArc(sketch, "E592.MirrorCS", {"start": v(43.98, 33.71) * mm, "mid": v(43.95, 33.72) * mm, "end": v(43.91, 33.7) * mm});
            skArc(sketch, "E593.MirrorCS", {"start": v(50.86, 33) * mm, "mid": v(50.76, 33.08) * mm, "end": v(50.65, 33.16) * mm});
            skArc(sketch, "E594.MirrorCS", {"start": v(48.4, 30.9) * mm, "mid": v(48.45, 30.85) * mm, "end": v(48.5, 30.81) * mm});
            skArc(sketch, "E595.MirrorCS", {"start": v(45.2, 27.55) * mm, "mid": v(45.18, 27.5) * mm, "end": v(45.16, 27.43) * mm});
            skArc(sketch, "E596.MirrorCS", {"start": v(46.98, 31.98) * mm, "mid": v(47.07, 31.93) * mm, "end": v(47.17, 31.9) * mm});
            skArc(sketch, "E597.MirrorCS", {"start": v(43.91, 33.7) * mm, "mid": v(43.9, 33.68) * mm, "end": v(43.88, 33.64) * mm});
            skArc(sketch, "E598.MirrorCS", {"start": v(50.65, 33.16) * mm, "mid": v(50.56, 33.23) * mm, "end": v(50.47, 33.3) * mm});
            skArc(sketch, "E599.MirrorCS", {"start": v(43.88, 33.64) * mm, "mid": v(43.87, 33.58) * mm, "end": v(43.84, 33.52) * mm});
            skArc(sketch, "E600.MirrorCS", {"start": v(45.07, 32.84) * mm, "mid": v(44.85, 33) * mm, "end": v(44.64, 33.18) * mm});
            skArc(sketch, "E601.MirrorCS", {"start": v(49.85, 29.2) * mm, "mid": v(49.7, 29.33) * mm, "end": v(49.54, 29.46) * mm});
            skArc(sketch, "E602.MirrorCS", {"start": v(48.5, 30.81) * mm, "mid": v(48.55, 30.77) * mm, "end": v(48.6, 30.74) * mm});
            skArc(sketch, "E603.MirrorCS", {"start": v(45.18, 27.3) * mm, "mid": v(45.22, 27.2) * mm, "end": v(45.27, 27.1) * mm});
            skArc(sketch, "E604.MirrorCS", {"start": v(47.17, 31.9) * mm, "mid": v(47.22, 31.9) * mm, "end": v(47.27, 31.93) * mm});
            skArc(sketch, "E605.MirrorCS", {"start": v(51.26, 33.3) * mm, "mid": v(51.39, 33.18) * mm, "end": v(51.52, 33.07) * mm});
            skArc(sketch, "E606.MirrorCS", {"start": v(50.47, 33.3) * mm, "mid": v(50.45, 33.3) * mm, "end": v(50.43, 33.31) * mm});
            skArc(sketch, "E607.MirrorCS", {"start": v(44.28, 33.48) * mm, "mid": v(44.23, 33.52) * mm, "end": v(44.18, 33.57) * mm});
            skArc(sketch, "E608.MirrorCS", {"start": v(44.64, 33.18) * mm, "mid": v(44.46, 33.33) * mm, "end": v(44.28, 33.48) * mm});
            skArc(sketch, "E609.MirrorCS", {"start": v(49.54, 29.46) * mm, "mid": v(49.36, 29.6) * mm, "end": v(49.17, 29.74) * mm});
            skArc(sketch, "E610.MirrorCS", {"start": v(44.92, 26.88) * mm, "mid": v(44.86, 26.94) * mm, "end": v(44.78, 26.96) * mm});
            skLineSegment(sketch, "E611.MirrorCS", {"start": v(38.42, 26.65) * mm, "end": v(38.72, 26.28) * mm});
            skArc(sketch, "E612.MirrorCS", {"start": v(48.6, 30.74) * mm, "mid": v(48.68, 30.68) * mm, "end": v(48.76, 30.63) * mm});
            skArc(sketch, "E613.MirrorCS", {"start": v(44.66, 29.15) * mm, "mid": v(44.82, 29.35) * mm, "end": v(45, 29.54) * mm});
            skArc(sketch, "E614.MirrorCS", {"start": v(47.27, 31.93) * mm, "mid": v(47.31, 31.97) * mm, "end": v(47.36, 32.02) * mm});
            skArc(sketch, "E615.MirrorCS", {"start": v(51.52, 33.07) * mm, "mid": v(51.69, 32.94) * mm, "end": v(51.85, 32.8) * mm});
            skLineSegment(sketch, "E616.MirrorCS", {"start": v(51.04, 34.26) * mm, "end": v(50.7, 33.78) * mm});
            skArc(sketch, "E617.MirrorCS", {"start": v(44.18, 33.57) * mm, "mid": v(44.14, 33.62) * mm, "end": v(44.08, 33.67) * mm});
            skArc(sketch, "E618.MirrorCS", {"start": v(50.43, 33.31) * mm, "mid": v(50.4, 33.3) * mm, "end": v(50.39, 33.3) * mm});
            skArc(sketch, "E619.MirrorCS", {"start": v(49.4, 30.14) * mm, "mid": v(49.59, 30) * mm, "end": v(49.77, 29.85) * mm});
            skArc(sketch, "E620.MirrorCS", {"start": v(49.17, 29.74) * mm, "mid": v(49, 29.88) * mm, "end": v(48.81, 30.02) * mm});
            skArc(sketch, "E621.MirrorCS", {"start": v(45, 33.47) * mm, "mid": v(45.19, 33.32) * mm, "end": v(45.38, 33.16) * mm});
            skArc(sketch, "E622.MirrorCS", {"start": v(44.78, 26.96) * mm, "mid": v(44.75, 26.96) * mm, "end": v(44.73, 26.94) * mm});
            skArc(sketch, "E623.MirrorCS", {"start": v(38.28, 26.08) * mm, "mid": v(38.22, 26.13) * mm, "end": v(38.14, 26.15) * mm});
            skArc(sketch, "E624.MirrorCS", {"start": v(37.33, 32.58) * mm, "mid": v(37.3, 32.6) * mm, "end": v(37.27, 32.6) * mm});
            skArc(sketch, "E625.MirrorCS", {"start": v(48.76, 30.63) * mm, "mid": v(48.9, 30.52) * mm, "end": v(49.06, 30.4) * mm});
            skLineSegment(sketch, "E626.MirrorCS", {"start": v(44.22, 34.12) * mm, "end": v(44.73, 33.68) * mm});
            skArc(sketch, "E627.MirrorCS", {"start": v(45.24, 26.3) * mm, "mid": v(45.08, 26.6) * mm, "end": v(44.92, 26.88) * mm});
            skLineSegment(sketch, "E628.MirrorCS", {"start": v(39.67, 28.2) * mm, "end": v(38.42, 26.65) * mm});
            skLineSegment(sketch, "E629.MirrorCS", {"start": v(50.13, 28.18) * mm, "end": v(50.42, 28.74) * mm});
            skArc(sketch, "E630.MirrorCS", {"start": v(48.04, 32.75) * mm, "mid": v(48.25, 32.97) * mm, "end": v(48.46, 33.2) * mm});
            skArc(sketch, "E631.MirrorCS", {"start": v(52.03, 32.08) * mm, "mid": v(51.86, 32.2) * mm, "end": v(51.7, 32.32) * mm});
            skArc(sketch, "E632.MirrorCS", {"start": v(45, 29.54) * mm, "mid": v(45.2, 29.76) * mm, "end": v(45.4, 29.98) * mm});
            skArc(sketch, "E633.MirrorCS", {"start": v(47.36, 32.02) * mm, "mid": v(47.51, 32.19) * mm, "end": v(47.67, 32.35) * mm});
            skArc(sketch, "E634.MirrorCS", {"start": v(51.78, 27.14) * mm, "mid": v(51.59, 27.46) * mm, "end": v(51.4, 27.8) * mm});
            skArc(sketch, "E635.MirrorCS", {"start": v(49.35, 32.22) * mm, "mid": v(49.15, 32) * mm, "end": v(48.95, 31.79) * mm});
            skArc(sketch, "E636.MirrorCS", {"start": v(51.65, 30.26) * mm, "mid": v(51.8, 30.42) * mm, "end": v(51.96, 30.58) * mm});
            skArc(sketch, "E637.MirrorCS", {"start": v(51.85, 32.8) * mm, "mid": v(52.03, 32.67) * mm, "end": v(52.2, 32.54) * mm});
            skArc(sketch, "E638.MirrorCS", {"start": v(47.2, 29.86) * mm, "mid": v(46.91, 29.54) * mm, "end": v(46.63, 29.22) * mm});
            skArc(sketch, "E639.MirrorCS", {"start": v(46.2, 32.53) * mm, "mid": v(46.45, 32.34) * mm, "end": v(46.7, 32.16) * mm});
            skArc(sketch, "E640.MirrorCS", {"start": v(51.13, 29.7) * mm, "mid": v(51.24, 29.82) * mm, "end": v(51.35, 29.95) * mm});
            skArc(sketch, "E641.MirrorCS", {"start": v(50.09, 33) * mm, "mid": v(49.91, 32.82) * mm, "end": v(49.74, 32.64) * mm});
            skLineSegment(sketch, "E642.MirrorCS", {"start": v(47.94, 30.7) * mm, "end": v(47.2, 29.86) * mm});
            skArc(sketch, "E643.MirrorCS", {"start": v(45.8, 32.83) * mm, "mid": v(46, 32.68) * mm, "end": v(46.2, 32.53) * mm});
            skLineSegment(sketch, "E644.MirrorCS", {"start": v(50.7, 33.78) * mm, "end": v(51.26, 33.3) * mm});
            skArc(sketch, "E645.MirrorCS", {"start": v(44.4, 26.48) * mm, "mid": v(44.29, 26.33) * mm, "end": v(44.19, 26.18) * mm});
            skArc(sketch, "E646.MirrorCS", {"start": v(44.08, 33.67) * mm, "mid": v(44.04, 33.7) * mm, "end": v(43.98, 33.71) * mm});
            skLineSegment(sketch, "E647.MirrorCS", {"start": v(50.66, 29.15) * mm, "end": v(51.13, 29.7) * mm});
            skArc(sketch, "E648.MirrorCS", {"start": v(50.39, 33.3) * mm, "mid": v(50.24, 33.14) * mm, "end": v(50.09, 33) * mm});
            skLineSegment(sketch, "E649.MirrorCS", {"start": v(48.81, 30.02) * mm, "end": v(47.94, 30.7) * mm});
            skArc(sketch, "E650.MirrorCS", {"start": v(45.38, 33.16) * mm, "mid": v(45.59, 33) * mm, "end": v(45.8, 32.83) * mm});
            skArc(sketch, "E651.MirrorCS", {"start": v(44.57, 26.73) * mm, "mid": v(44.48, 26.6) * mm, "end": v(44.4, 26.48) * mm});
            skLineSegment(sketch, "E652.MirrorCS", {"start": v(49.77, 29.85) * mm, "end": v(50.66, 29.15) * mm});
            skArc(sketch, "E653.MirrorCS", {"start": v(44.73, 26.94) * mm, "mid": v(44.65, 26.84) * mm, "end": v(44.57, 26.73) * mm});
            skArc(sketch, "E654.MirrorCS", {"start": v(38.14, 26.15) * mm, "mid": v(38.11, 26.15) * mm, "end": v(38.1, 26.13) * mm});
            skArc(sketch, "E655.MirrorCS", {"start": v(37.27, 32.6) * mm, "mid": v(37.26, 32.6) * mm, "end": v(37.26, 32.6) * mm});
            skArc(sketch, "E656.MirrorCS", {"start": v(49.06, 30.4) * mm, "mid": v(49.23, 30.27) * mm, "end": v(49.4, 30.14) * mm});
            skArc(sketch, "E657.MirrorCS", {"start": v(42.78, 35.7) * mm, "mid": v(43, 35.4) * mm, "end": v(43.22, 35.1) * mm});
            skArc(sketch, "E658.MirrorCS", {"start": v(38.72, 26.28) * mm, "mid": v(38.9, 26.04) * mm, "end": v(39.05, 25.8) * mm});
            skArc(sketch, "E659.MirrorCS", {"start": v(44.73, 33.68) * mm, "mid": v(44.86, 33.57) * mm, "end": v(45, 33.47) * mm});
            skArc(sketch, "E660.MirrorCS", {"start": v(42.96, 26.5) * mm, "mid": v(43.18, 26.96) * mm, "end": v(43.42, 27.4) * mm});
            skArc(sketch, "E661.MirrorCS", {"start": v(38.55, 31.7) * mm, "mid": v(37.94, 32.14) * mm, "end": v(37.33, 32.58) * mm});
            skArc(sketch, "E662.MirrorCS", {"start": v(45.56, 32.45) * mm, "mid": v(45.31, 32.64) * mm, "end": v(45.07, 32.84) * mm});
            skArc(sketch, "E663.MirrorCS", {"start": v(50.05, 29.04) * mm, "mid": v(49.95, 29.12) * mm, "end": v(49.85, 29.2) * mm});
            skArc(sketch, "E664.MirrorCS", {"start": v(51.37, 32.58) * mm, "mid": v(51.23, 32.69) * mm, "end": v(51.1, 32.8) * mm});
            skLineSegment(sketch, "E665.MirrorCS", {"start": v(46.81, 31.48) * mm, "end": v(45.56, 32.45) * mm});
            skLineSegment(sketch, "E666.MirrorCS", {"start": v(50.42, 28.74) * mm, "end": v(50.05, 29.04) * mm});
            skArc(sketch, "E667.MirrorCS", {"start": v(51.7, 32.32) * mm, "mid": v(51.54, 32.45) * mm, "end": v(51.37, 32.58) * mm});
            skLineSegment(sketch, "E668.MirrorCS", {"start": v(45.8, 30.42) * mm, "end": v(46.81, 31.48) * mm});
            skLineSegment(sketch, "E669.MirrorCS", {"start": v(48.46, 33.2) * mm, "end": v(49.53, 34.33) * mm});
            skArc(sketch, "E670.MirrorCS", {"start": v(45.4, 29.98) * mm, "mid": v(45.6, 30.2) * mm, "end": v(45.8, 30.42) * mm});
            skArc(sketch, "E671.MirrorCS", {"start": v(36.83, 27.1) * mm, "mid": v(36.87, 27.17) * mm, "end": v(36.91, 27.24) * mm});
            skLineSegment(sketch, "E672.MirrorCS", {"start": v(52.09, 28.85) * mm, "end": v(51.55, 28.28) * mm});
            skArc(sketch, "E673.MirrorCS", {"start": v(47.67, 32.35) * mm, "mid": v(47.85, 32.55) * mm, "end": v(48.04, 32.75) * mm});
            skArc(sketch, "E674.MirrorCS", {"start": v(35.27, 30.1) * mm, "mid": v(35.17, 29.97) * mm, "end": v(35.06, 29.84) * mm});
            skArc(sketch, "E675.MirrorCS", {"start": v(44.47, 28.92) * mm, "mid": v(44.56, 29.04) * mm, "end": v(44.66, 29.15) * mm});
            skArc(sketch, "E676.MirrorCS", {"start": v(48.62, 31.41) * mm, "mid": v(48.48, 31.25) * mm, "end": v(48.35, 31.08) * mm});
            skArc(sketch, "E677.MirrorCS", {"start": v(51.4, 27.8) * mm, "mid": v(51.33, 27.85) * mm, "end": v(51.25, 27.87) * mm});
            skArc(sketch, "E678.MirrorCS", {"start": v(48.95, 31.79) * mm, "mid": v(48.79, 31.6) * mm, "end": v(48.62, 31.41) * mm});
            skArc(sketch, "E679.MirrorCS", {"start": v(51.96, 30.58) * mm, "mid": v(52.1, 30.72) * mm, "end": v(52.25, 30.86) * mm});
            skArc(sketch, "E680.MirrorCS", {"start": v(46.02, 28.52) * mm, "mid": v(45.75, 28.2) * mm, "end": v(45.48, 27.89) * mm});
            skArc(sketch, "E681.MirrorCS", {"start": v(49.74, 32.64) * mm, "mid": v(49.54, 32.43) * mm, "end": v(49.35, 32.22) * mm});
            skArc(sketch, "E682.MirrorCS", {"start": v(51.35, 29.95) * mm, "mid": v(51.5, 30.1) * mm, "end": v(51.65, 30.26) * mm});
            skArc(sketch, "E683.MirrorCS", {"start": v(46.63, 29.22) * mm, "mid": v(46.32, 28.87) * mm, "end": v(46.02, 28.52) * mm});
            skArc(sketch, "E684.MirrorCS", {"start": v(46.7, 32.16) * mm, "mid": v(46.84, 32.07) * mm, "end": v(46.98, 31.98) * mm});
            skLineSegment(sketch, "E685.MirrorCS", {"start": v(37.5, 32.99) * mm, "end": v(37.74, 32.8) * mm});
            skArc(sketch, "E686.MirrorCS", {"start": v(38.1, 26.13) * mm, "mid": v(38.03, 26.07) * mm, "end": v(37.96, 26) * mm});
            skArc(sketch, "E687.MirrorCS", {"start": v(37.26, 32.6) * mm, "mid": v(37.15, 32.47) * mm, "end": v(37.05, 32.34) * mm});
            skArc(sketch, "E688.MirrorCS", {"start": v(43.22, 35.1) * mm, "mid": v(43.28, 35.05) * mm, "end": v(43.36, 35.03) * mm});
            skArc(sketch, "E689.MirrorCS", {"start": v(35.83, 32.85) * mm, "mid": v(36, 33.03) * mm, "end": v(36.13, 33.25) * mm});
            skArc(sketch, "E690.MirrorCS", {"start": v(44.93, 35.63) * mm, "mid": v(44.78, 35.27) * mm, "end": v(44.6, 34.9) * mm});
            skLineSegment(sketch, "E691.MirrorCS", {"start": v(49.53, 34.33) * mm, "end": v(49.19, 34.78) * mm});
            skArc(sketch, "E692.MirrorCS", {"start": v(45.5, 26.76) * mm, "mid": v(45.78, 26.3) * mm, "end": v(46.03, 25.84) * mm});
            skArc(sketch, "E693.MirrorCS", {"start": v(44.19, 26.18) * mm, "mid": v(43.97, 25.82) * mm, "end": v(43.77, 25.45) * mm});
            skArc(sketch, "E694.MirrorCS", {"start": v(45.77, 25.08) * mm, "mid": v(45.67, 25.37) * mm, "end": v(45.55, 25.66) * mm});
            skArc(sketch, "E695.MirrorCS", {"start": v(36.91, 27.24) * mm, "mid": v(36.92, 27.26) * mm, "end": v(36.92, 27.28) * mm});
            skArc(sketch, "E696.MirrorCS", {"start": v(35.06, 29.84) * mm, "mid": v(34.98, 29.73) * mm, "end": v(34.9, 29.61) * mm});
            skArc(sketch, "E697.MirrorCS", {"start": v(42.57, 22.63) * mm, "mid": v(42.54, 22.82) * mm, "end": v(42.52, 23) * mm});
            skLineSegment(sketch, "E698.MirrorCS", {"start": v(49.48, 35.17) * mm, "end": v(49.77, 34.69) * mm});
            skArc(sketch, "E699.MirrorCS", {"start": v(45.16, 27.43) * mm, "mid": v(45.16, 27.36) * mm, "end": v(45.18, 27.3) * mm});
            skLineSegment(sketch, "E700.MirrorCS", {"start": v(43.09, 34.63) * mm, "end": v(42.74, 35.06) * mm});
            skArc(sketch, "E701.MirrorCS", {"start": v(49.2, 35.7) * mm, "mid": v(49.34, 35.43) * mm, "end": v(49.48, 35.17) * mm});
            skLineSegment(sketch, "E702.MirrorCS", {"start": v(41.66, 32.94) * mm, "end": v(43.09, 34.63) * mm});
            skArc(sketch, "E703.MirrorCS", {"start": v(51.25, 27.87) * mm, "mid": v(51.23, 27.86) * mm, "end": v(51.22, 27.85) * mm});
            skLineSegment(sketch, "E704.MirrorCS", {"start": v(37.28, 27.7) * mm, "end": v(38.54, 29.21) * mm});
            skArc(sketch, "E705.MirrorCS", {"start": v(43.79, 35.6) * mm, "mid": v(43.96, 35.87) * mm, "end": v(44.12, 36.14) * mm});
            skArc(sketch, "E706.MirrorCS", {"start": v(43.45, 35.08) * mm, "mid": v(43.62, 35.34) * mm, "end": v(43.79, 35.6) * mm});
            skArc(sketch, "E707.MirrorCS", {"start": v(37.74, 32.8) * mm, "mid": v(38, 32.6) * mm, "end": v(38.27, 32.4) * mm});
            skLineSegment(sketch, "E708.MirrorCS", {"start": v(37.9, 33.83) * mm, "end": v(37.5, 32.99) * mm});
            skArc(sketch, "E709.MirrorCS", {"start": v(37.96, 26) * mm, "mid": v(37.89, 25.91) * mm, "end": v(37.82, 25.83) * mm});
            skArc(sketch, "E710.MirrorCS", {"start": v(37.05, 32.34) * mm, "mid": v(36.93, 32.19) * mm, "end": v(36.82, 32.04) * mm});
            skArc(sketch, "E711.MirrorCS", {"start": v(43.36, 35.03) * mm, "mid": v(43.41, 35.05) * mm, "end": v(43.45, 35.08) * mm});
            skArc(sketch, "E712.MirrorCS", {"start": v(43.25, 22.76) * mm, "mid": v(43.26, 22.6) * mm, "end": v(43.28, 22.45) * mm});
            skArc(sketch, "E713.MirrorCS", {"start": v(36.13, 33.25) * mm, "mid": v(36.16, 33.3) * mm, "end": v(36.17, 33.36) * mm});
            skArc(sketch, "E714.MirrorCS", {"start": v(48.8, 35.37) * mm, "mid": v(48.67, 35.66) * mm, "end": v(48.56, 35.96) * mm});
            skArc(sketch, "E715.MirrorCS", {"start": v(42.66, 25.63) * mm, "mid": v(42.8, 26.07) * mm, "end": v(42.96, 26.5) * mm});
            skLineSegment(sketch, "E716.MirrorCS", {"start": v(44.6, 34.9) * mm, "end": v(44.22, 34.12) * mm});
            skArc(sketch, "E717.MirrorCS", {"start": v(49.19, 34.78) * mm, "mid": v(48.98, 35.07) * mm, "end": v(48.8, 35.37) * mm});
            skArc(sketch, "E718.MirrorCS", {"start": v(43.77, 25.45) * mm, "mid": v(43.6, 25.1) * mm, "end": v(43.48, 24.72) * mm});
            skArc(sketch, "E719.MirrorCS", {"start": v(45.55, 25.66) * mm, "mid": v(45.4, 25.99) * mm, "end": v(45.24, 26.3) * mm});
            skArc(sketch, "E720.MirrorCS", {"start": v(46.03, 25.84) * mm, "mid": v(46.23, 25.39) * mm, "end": v(46.39, 24.92) * mm});
            skArc(sketch, "E721.MirrorCS", {"start": v(42.51, 24.7) * mm, "mid": v(42.57, 25.17) * mm, "end": v(42.66, 25.63) * mm});
            skArc(sketch, "E722.MirrorCS", {"start": v(34.9, 29.61) * mm, "mid": v(34.83, 29.52) * mm, "end": v(34.76, 29.42) * mm});
            skArc(sketch, "E723.MirrorCS", {"start": v(36.92, 27.28) * mm, "mid": v(36.9, 27.36) * mm, "end": v(36.85, 27.42) * mm});
            skArc(sketch, "E724.MirrorCS", {"start": v(41.49, 37.24) * mm, "mid": v(41.36, 37.75) * mm, "end": v(41.3, 38.28) * mm});
            skArc(sketch, "E725.MirrorCS", {"start": v(39.05, 24.7) * mm, "mid": v(38.96, 24.93) * mm, "end": v(38.86, 25.14) * mm});
            skLineSegment(sketch, "E726.MirrorCS", {"start": v(49.77, 34.69) * mm, "end": v(50.16, 35.14) * mm});
            skArc(sketch, "E727.MirrorCS", {"start": v(45.27, 27.1) * mm, "mid": v(45.38, 26.93) * mm, "end": v(45.5, 26.76) * mm});
            skArc(sketch, "E728.MirrorCS", {"start": v(42.52, 23) * mm, "mid": v(42.5, 23.32) * mm, "end": v(42.49, 23.64) * mm});
            skArc(sketch, "E729.MirrorCS", {"start": v(41.96, 36.17) * mm, "mid": v(41.7, 36.7) * mm, "end": v(41.49, 37.24) * mm});
            skArc(sketch, "E730.MirrorCS", {"start": v(45.95, 24.32) * mm, "mid": v(45.88, 24.7) * mm, "end": v(45.77, 25.08) * mm});
            skArc(sketch, "E731.MirrorCS", {"start": v(51.1, 27.68) * mm, "mid": v(51.03, 27.57) * mm, "end": v(50.96, 27.46) * mm});
            skArc(sketch, "E732.MirrorCS", {"start": v(42.67, 22.3) * mm, "mid": v(42.61, 22.47) * mm, "end": v(42.57, 22.63) * mm});
            skArc(sketch, "E733.MirrorCS", {"start": v(51.22, 27.85) * mm, "mid": v(51.16, 27.76) * mm, "end": v(51.1, 27.68) * mm});
            skArc(sketch, "E734.MirrorCS", {"start": v(44.69, 37.56) * mm, "mid": v(44.75, 38.07) * mm, "end": v(44.74, 38.58) * mm});
            skLineSegment(sketch, "E735.MirrorCS", {"start": v(36.77, 28.07) * mm, "end": v(37.28, 27.7) * mm});
            skArc(sketch, "E736.MirrorCS", {"start": v(44.12, 36.14) * mm, "mid": v(44.25, 36.36) * mm, "end": v(44.37, 36.6) * mm});
            skArc(sketch, "E737.MirrorCS", {"start": v(39.97, 23.41) * mm, "mid": v(40, 23.22) * mm, "end": v(40.02, 23.02) * mm});
            skArc(sketch, "E738.MirrorCS", {"start": v(43.28, 22.45) * mm, "mid": v(43.3, 22.33) * mm, "end": v(43.35, 22.2) * mm});
            skArc(sketch, "E739.MirrorCS", {"start": v(36.17, 33.36) * mm, "mid": v(36.16, 33.42) * mm, "end": v(36.15, 33.47) * mm});
            skArc(sketch, "E740.MirrorCS", {"start": v(39.05, 25.8) * mm, "mid": v(39.21, 25.5) * mm, "end": v(39.36, 25.2) * mm});
            skArc(sketch, "E741.MirrorCS", {"start": v(51.77, 35.73) * mm, "mid": v(51.46, 34.97) * mm, "end": v(51.04, 34.26) * mm});
            skArc(sketch, "E742.MirrorCS", {"start": v(43.24, 23.19) * mm, "mid": v(43.24, 22.97) * mm, "end": v(43.25, 22.76) * mm});
            skArc(sketch, "E743.MirrorCS", {"start": v(48.56, 35.96) * mm, "mid": v(48.48, 36.29) * mm, "end": v(48.42, 36.62) * mm});
            skArc(sketch, "E744.MirrorCS", {"start": v(43.3, 23.98) * mm, "mid": v(43.26, 23.59) * mm, "end": v(43.24, 23.19) * mm});
            skArc(sketch, "E745.MirrorCS", {"start": v(42.36, 36.32) * mm, "mid": v(42.56, 36.01) * mm, "end": v(42.78, 35.7) * mm});
            skArc(sketch, "E746.MirrorCS", {"start": v(46.57, 23.99) * mm, "mid": v(46.6, 23.5) * mm, "end": v(46.58, 23.02) * mm});
            skArc(sketch, "E747.MirrorCS", {"start": v(43.48, 24.72) * mm, "mid": v(43.38, 24.36) * mm, "end": v(43.3, 23.98) * mm});
            skArc(sketch, "E748.MirrorCS", {"start": v(43.3, 40.38) * mm, "mid": v(43.18, 40.37) * mm, "end": v(43.05, 40.36) * mm});
            skArc(sketch, "E749.MirrorCS", {"start": v(42.1, 36.8) * mm, "mid": v(42.23, 36.56) * mm, "end": v(42.36, 36.32) * mm});
            skArc(sketch, "E750.MirrorCS", {"start": v(46.39, 24.92) * mm, "mid": v(46.5, 24.46) * mm, "end": v(46.57, 23.99) * mm});
            skArc(sketch, "E751.MirrorCS", {"start": v(34.76, 29.42) * mm, "mid": v(34.75, 29.4) * mm, "end": v(34.76, 29.37) * mm});
            skArc(sketch, "E752.MirrorCS", {"start": v(41.84, 37.67) * mm, "mid": v(41.94, 37.22) * mm, "end": v(42.1, 36.8) * mm});
            skArc(sketch, "E753.MirrorCS", {"start": v(38.86, 25.14) * mm, "mid": v(38.72, 25.39) * mm, "end": v(38.58, 25.63) * mm});
            skArc(sketch, "E754.MirrorCS", {"start": v(41.81, 38.55) * mm, "mid": v(41.8, 38.1) * mm, "end": v(41.84, 37.67) * mm});
            skArc(sketch, "E755.MirrorCS", {"start": v(50.16, 35.14) * mm, "mid": v(50.54, 35.65) * mm, "end": v(50.86, 36.2) * mm});
            skLineSegment(sketch, "E756.MirrorCS", {"start": v(36.05, 34.38) * mm, "end": v(36.6, 33.77) * mm});
            skArc(sketch, "E757.MirrorCS", {"start": v(42.49, 23.64) * mm, "mid": v(42.48, 24.17) * mm, "end": v(42.51, 24.7) * mm});
            skArc(sketch, "E758.MirrorCS", {"start": v(45.14, 36.3) * mm, "mid": v(45.04, 35.97) * mm, "end": v(44.93, 35.63) * mm});
            skLineSegment(sketch, "E759.MirrorCS", {"start": v(51.55, 28.28) * mm, "end": v(51.96, 27.74) * mm});
            skArc(sketch, "E760.MirrorCS", {"start": v(49.86, 27.55) * mm, "mid": v(49.99, 27.87) * mm, "end": v(50.13, 28.18) * mm});
            skArc(sketch, "E761.MirrorCS", {"start": v(45.26, 36.98) * mm, "mid": v(45.2, 36.64) * mm, "end": v(45.14, 36.3) * mm});
            skArc(sketch, "E762.MirrorCS", {"start": v(50.96, 27.46) * mm, "mid": v(50.89, 27.34) * mm, "end": v(50.81, 27.22) * mm});
            skArc(sketch, "E763.MirrorCS", {"start": v(42.74, 35.06) * mm, "mid": v(42.33, 35.6) * mm, "end": v(41.96, 36.17) * mm});
            skArc(sketch, "E764.MirrorCS", {"start": v(45.3, 37.7) * mm, "mid": v(45.29, 37.34) * mm, "end": v(45.26, 36.98) * mm});
            skArc(sketch, "E765.MirrorCS", {"start": v(46.03, 23.53) * mm, "mid": v(46, 23.93) * mm, "end": v(45.95, 24.32) * mm});
            skArc(sketch, "E766.MirrorCS", {"start": v(50.13, 24) * mm, "mid": v(50.15, 23.88) * mm, "end": v(50.18, 23.76) * mm});
            skArc(sketch, "E767.MirrorCS", {"start": v(45.2, 38.79) * mm, "mid": v(45.27, 38.25) * mm, "end": v(45.3, 37.7) * mm});
            skArc(sketch, "E768.MirrorCS", {"start": v(46, 22.8) * mm, "mid": v(46.03, 23.17) * mm, "end": v(46.03, 23.53) * mm});
            skArc(sketch, "E769.MirrorCS", {"start": v(50.1, 24.3) * mm, "mid": v(50.11, 24.15) * mm, "end": v(50.13, 24) * mm});
            skArc(sketch, "E770.MirrorCS", {"start": v(45.86, 22.24) * mm, "mid": v(45.95, 22.52) * mm, "end": v(46, 22.8) * mm});
            skArc(sketch, "E771.MirrorCS", {"start": v(48.96, 36.6) * mm, "mid": v(49, 36.37) * mm, "end": v(49.05, 36.14) * mm});
            skArc(sketch, "E772.MirrorCS", {"start": v(36.54, 31.68) * mm, "mid": v(36.38, 31.47) * mm, "end": v(36.23, 31.27) * mm});
            skArc(sketch, "E773.MirrorCS", {"start": v(48.93, 37.2) * mm, "mid": v(48.94, 36.9) * mm, "end": v(48.96, 36.6) * mm});
            skArc(sketch, "E774.MirrorCS", {"start": v(44.37, 36.6) * mm, "mid": v(44.56, 37.06) * mm, "end": v(44.69, 37.56) * mm});
            skArc(sketch, "E775.MirrorCS", {"start": v(40.02, 23.02) * mm, "mid": v(40.04, 22.8) * mm, "end": v(40.04, 22.59) * mm});
            skArc(sketch, "E776.MirrorCS", {"start": v(34.8, 40.57) * mm, "mid": v(34.73, 40.43) * mm, "end": v(34.67, 40.29) * mm});
            skArc(sketch, "E777.MirrorCS", {"start": v(39.86, 23.87) * mm, "mid": v(39.92, 23.64) * mm, "end": v(39.97, 23.41) * mm});
            skArc(sketch, "E778.MirrorCS", {"start": v(48.42, 38.4) * mm, "mid": v(48.44, 38.54) * mm, "end": v(48.48, 38.68) * mm});
            skArc(sketch, "E779.MirrorCS", {"start": v(43.25, 41.07) * mm, "mid": v(43.42, 41.06) * mm, "end": v(43.6, 41.02) * mm});
            skArc(sketch, "E780.MirrorCS", {"start": v(43.45, 21.96) * mm, "mid": v(43.68, 21.64) * mm, "end": v(43.98, 21.4) * mm});
            skArc(sketch, "E781.MirrorCS", {"start": v(36.2, 28.46) * mm, "mid": v(36.37, 28.35) * mm, "end": v(36.53, 28.25) * mm});
            skArc(sketch, "E782.MirrorCS", {"start": v(50.81, 27.22) * mm, "mid": v(50.64, 26.9) * mm, "end": v(50.48, 26.59) * mm});
            skArc(sketch, "E783.MirrorCS", {"start": v(36.07, 33.6) * mm, "mid": v(35.98, 33.7) * mm, "end": v(35.89, 33.8) * mm});
            skArc(sketch, "E784.MirrorCS", {"start": v(39.64, 24.53) * mm, "mid": v(39.76, 24.2) * mm, "end": v(39.86, 23.87) * mm});
            skArc(sketch, "E785.MirrorCS", {"start": v(37.82, 25.83) * mm, "mid": v(37.74, 25.73) * mm, "end": v(37.66, 25.62) * mm});
            skArc(sketch, "E786.MirrorCS", {"start": v(43.35, 22.2) * mm, "mid": v(43.4, 22.08) * mm, "end": v(43.45, 21.96) * mm});
            skArc(sketch, "E787.MirrorCS", {"start": v(35.85, 28.68) * mm, "mid": v(36.03, 28.57) * mm, "end": v(36.2, 28.46) * mm});
            skArc(sketch, "E788.MirrorCS", {"start": v(36.82, 32.04) * mm, "mid": v(36.68, 31.86) * mm, "end": v(36.54, 31.68) * mm});
            skArc(sketch, "E789.MirrorCS", {"start": v(38.56, 35.49) * mm, "mid": v(38.44, 35.1) * mm, "end": v(38.3, 34.7) * mm});
            skArc(sketch, "E790.MirrorCS", {"start": v(39.36, 25.2) * mm, "mid": v(39.51, 24.87) * mm, "end": v(39.64, 24.53) * mm});
            skArc(sketch, "E791.MirrorCS", {"start": v(36.15, 33.47) * mm, "mid": v(36.11, 33.54) * mm, "end": v(36.07, 33.6) * mm});
            skArc(sketch, "E792.MirrorCS", {"start": v(48.42, 36.62) * mm, "mid": v(48.39, 37.04) * mm, "end": v(48.38, 37.45) * mm});
            skArc(sketch, "E793.MirrorCS", {"start": v(46.58, 23.02) * mm, "mid": v(46.53, 22.6) * mm, "end": v(46.43, 22.17) * mm});
            skArc(sketch, "E794.MirrorCS", {"start": v(43.05, 40.36) * mm, "mid": v(42.95, 40.34) * mm, "end": v(42.86, 40.31) * mm});
            skArc(sketch, "E795.MirrorCS", {"start": v(38.58, 25.63) * mm, "mid": v(38.43, 25.86) * mm, "end": v(38.28, 26.08) * mm});
            skArc(sketch, "E796.MirrorCS", {"start": v(34.76, 29.37) * mm, "mid": v(34.78, 29.35) * mm, "end": v(34.8, 29.33) * mm});
            skArc(sketch, "E797.MirrorCS", {"start": v(52.84, 26.06) * mm, "mid": v(52.96, 25.63) * mm, "end": v(53.02, 25.2) * mm});
            skArc(sketch, "E798.MirrorCS", {"start": v(50.86, 36.2) * mm, "mid": v(51.08, 36.8) * mm, "end": v(51.21, 37.4) * mm});
            skArc(sketch, "E799.MirrorCS", {"start": v(51.96, 27.74) * mm, "mid": v(52.24, 27.34) * mm, "end": v(52.49, 26.92) * mm});
            skArc(sketch, "E800.MirrorCS", {"start": v(50.5, 40.23) * mm, "mid": v(50.7, 40.17) * mm, "end": v(50.87, 40.09) * mm});
            skArc(sketch, "E801.MirrorCS", {"start": v(43.9, 40.25) * mm, "mid": v(43.82, 40.29) * mm, "end": v(43.73, 40.32) * mm});
            skArc(sketch, "E802.MirrorCS", {"start": v(50.18, 23.76) * mm, "mid": v(50.22, 23.66) * mm, "end": v(50.27, 23.56) * mm});
            skArc(sketch, "E803.MirrorCS", {"start": v(42.47, 40) * mm, "mid": v(42.22, 39.7) * mm, "end": v(42.03, 39.35) * mm});
            skArc(sketch, "E804.MirrorCS", {"start": v(39.36, 23.34) * mm, "mid": v(39.3, 23.7) * mm, "end": v(39.24, 24.05) * mm});
            skArc(sketch, "E805.MirrorCS", {"start": v(49.48, 26.1) * mm, "mid": v(49.55, 26.46) * mm, "end": v(49.64, 26.82) * mm});
            skArc(sketch, "E806.MirrorCS", {"start": v(53, 29.77) * mm, "mid": v(52.74, 29.53) * mm, "end": v(52.5, 29.28) * mm});
            skArc(sketch, "E807.MirrorCS", {"start": v(42.86, 21.9) * mm, "mid": v(42.76, 22.1) * mm, "end": v(42.67, 22.3) * mm});
            skArc(sketch, "E808.MirrorCS", {"start": v(49.1, 39.68) * mm, "mid": v(49.23, 39.8) * mm, "end": v(49.37, 39.9) * mm});
            skLineSegment(sketch, "E809.MirrorCS", {"start": v(52.52, 32.3) * mm, "end": v(53.25, 31.8) * mm});
            skArc(sketch, "E810.MirrorCS", {"start": v(49.05, 36.14) * mm, "mid": v(49.12, 35.91) * mm, "end": v(49.2, 35.7) * mm});
            skArc(sketch, "E811.MirrorCS", {"start": v(34.57, 41.28) * mm, "mid": v(34.66, 41.39) * mm, "end": v(34.77, 41.5) * mm});
            skArc(sketch, "E812.MirrorCS", {"start": v(44.74, 38.58) * mm, "mid": v(44.66, 39.05) * mm, "end": v(44.52, 39.5) * mm});
            skArc(sketch, "E813.MirrorCS", {"start": v(45.37, 21.57) * mm, "mid": v(45.65, 21.88) * mm, "end": v(45.86, 22.24) * mm});
            skArc(sketch, "E814.MirrorCS", {"start": v(36.23, 31.27) * mm, "mid": v(36.05, 31.05) * mm, "end": v(35.87, 30.83) * mm});
            skArc(sketch, "E815.MirrorCS", {"start": v(50.15, 25.44) * mm, "mid": v(50.12, 25.1) * mm, "end": v(50.1, 24.74) * mm});
            skArc(sketch, "E816.MirrorCS", {"start": v(49.78, 23.7) * mm, "mid": v(49.63, 24.13) * mm, "end": v(49.52, 24.57) * mm});
            skArc(sketch, "E817.MirrorCS", {"start": v(36.53, 28.25) * mm, "mid": v(36.65, 28.16) * mm, "end": v(36.77, 28.07) * mm});
            skArc(sketch, "E818.MirrorCS", {"start": v(50.48, 26.59) * mm, "mid": v(50.36, 26.3) * mm, "end": v(50.27, 26.03) * mm});
            skArc(sketch, "E819.MirrorCS", {"start": v(48.96, 37.9) * mm, "mid": v(48.94, 37.55) * mm, "end": v(48.93, 37.2) * mm});
            skArc(sketch, "E820.MirrorCS", {"start": v(48.48, 38.68) * mm, "mid": v(48.54, 38.82) * mm, "end": v(48.6, 38.97) * mm});
            skArc(sketch, "E821.MirrorCS", {"start": v(32.74, 29.5) * mm, "mid": v(32.58, 29.53) * mm, "end": v(32.42, 29.58) * mm});
            skArc(sketch, "E822.MirrorCS", {"start": v(50.64, 22.62) * mm, "mid": v(50.38, 22.8) * mm, "end": v(50.17, 23.03) * mm});
            skArc(sketch, "E823.MirrorCS", {"start": v(44.91, 20.6) * mm, "mid": v(44.64, 20.54) * mm, "end": v(44.35, 20.54) * mm});
            skArc(sketch, "E824.MirrorCS", {"start": v(52.31, 26.02) * mm, "mid": v(52.23, 26.25) * mm, "end": v(52.13, 26.48) * mm});
            skArc(sketch, "E825.MirrorCS", {"start": v(52.43, 25.45) * mm, "mid": v(52.38, 25.74) * mm, "end": v(52.31, 26.02) * mm});
            skArc(sketch, "E826.MirrorCS", {"start": v(38.3, 34.7) * mm, "mid": v(38.1, 34.27) * mm, "end": v(37.9, 33.83) * mm});
            skArc(sketch, "E827.MirrorCS", {"start": v(48.38, 37.45) * mm, "mid": v(48.38, 37.75) * mm, "end": v(48.38, 38.05) * mm});
            skArc(sketch, "E828.MirrorCS", {"start": v(42.51, 40.88) * mm, "mid": v(42.7, 40.96) * mm, "end": v(42.9, 41.03) * mm});
            skArc(sketch, "E829.MirrorCS", {"start": v(52.48, 24.8) * mm, "mid": v(52.46, 25.13) * mm, "end": v(52.43, 25.45) * mm});
            skArc(sketch, "E830.MirrorCS", {"start": v(52.46, 24.17) * mm, "mid": v(52.48, 24.48) * mm, "end": v(52.48, 24.8) * mm});
            skArc(sketch, "E831.MirrorCS", {"start": v(52.37, 23.72) * mm, "mid": v(52.43, 23.94) * mm, "end": v(52.46, 24.17) * mm});
            skArc(sketch, "E832.MirrorCS", {"start": v(42.86, 40.31) * mm, "mid": v(42.78, 40.26) * mm, "end": v(42.7, 40.2) * mm});
            skArc(sketch, "E833.MirrorCS", {"start": v(50.73, 39.21) * mm, "mid": v(50.58, 39.32) * mm, "end": v(50.41, 39.41) * mm});
            skArc(sketch, "E834.MirrorCS", {"start": v(35.33, 41.15) * mm, "mid": v(35.26, 41.1) * mm, "end": v(35.2, 41.06) * mm});
            skArc(sketch, "E835.MirrorCS", {"start": v(41.84, 40.29) * mm, "mid": v(41.98, 40.47) * mm, "end": v(42.14, 40.63) * mm});
            skArc(sketch, "E836.MirrorCS", {"start": v(51.98, 23.13) * mm, "mid": v(52.22, 23.4) * mm, "end": v(52.37, 23.72) * mm});
            skArc(sketch, "E837.MirrorCS", {"start": v(34.8, 29.33) * mm, "mid": v(34.9, 29.27) * mm, "end": v(35, 29.2) * mm});
            skArc(sketch, "E838.MirrorCS", {"start": v(35.2, 28.44) * mm, "mid": v(34.83, 28.64) * mm, "end": v(34.46, 28.83) * mm});
            skArc(sketch, "E839.MirrorCS", {"start": v(51.21, 37.4) * mm, "mid": v(51.24, 37.94) * mm, "end": v(51.17, 38.48) * mm});
            skArc(sketch, "E840.MirrorCS", {"start": v(37.1, 34.83) * mm, "mid": v(37.3, 35.28) * mm, "end": v(37.5, 35.73) * mm});
            skArc(sketch, "E841.MirrorCS", {"start": v(50.75, 23.04) * mm, "mid": v(51.06, 22.9) * mm, "end": v(51.39, 22.88) * mm});
            skLineSegment(sketch, "E842.MirrorCS", {"start": v(36.6, 33.77) * mm, "end": v(37.1, 34.83) * mm});
            skArc(sketch, "E843.MirrorCS", {"start": v(52.49, 26.92) * mm, "mid": v(52.69, 26.5) * mm, "end": v(52.84, 26.06) * mm});
            skArc(sketch, "E844.MirrorCS", {"start": v(43.73, 40.32) * mm, "mid": v(43.64, 40.35) * mm, "end": v(43.54, 40.37) * mm});
            skArc(sketch, "E845.MirrorCS", {"start": v(50.27, 23.56) * mm, "mid": v(50.48, 23.27) * mm, "end": v(50.75, 23.04) * mm});
            skArc(sketch, "E846.MirrorCS", {"start": v(42.03, 39.35) * mm, "mid": v(41.89, 38.96) * mm, "end": v(41.81, 38.55) * mm});
            skArc(sketch, "E847.MirrorCS", {"start": v(49.64, 26.82) * mm, "mid": v(49.74, 27.19) * mm, "end": v(49.86, 27.55) * mm});
            skArc(sketch, "E848.MirrorCS", {"start": v(36.73, 26.94) * mm, "mid": v(36.78, 27.02) * mm, "end": v(36.83, 27.1) * mm});
            skArc(sketch, "E849.MirrorCS", {"start": v(52.5, 29.28) * mm, "mid": v(52.29, 29.07) * mm, "end": v(52.09, 28.85) * mm});
            skArc(sketch, "E850.MirrorCS", {"start": v(49.37, 39.9) * mm, "mid": v(49.54, 40.01) * mm, "end": v(49.72, 40.1) * mm});
            skLineSegment(sketch, "E851.MirrorCS", {"start": v(52.9, 31.47) * mm, "end": v(52.3, 31.88) * mm});
            skArc(sketch, "E852.MirrorCS", {"start": v(34.77, 41.5) * mm, "mid": v(34.87, 41.6) * mm, "end": v(34.98, 41.7) * mm});
            skArc(sketch, "E853.MirrorCS", {"start": v(49.43, 25.5) * mm, "mid": v(49.45, 25.8) * mm, "end": v(49.48, 26.1) * mm});
            skArc(sketch, "E854.MirrorCS", {"start": v(44.95, 39.7) * mm, "mid": v(45.1, 39.26) * mm, "end": v(45.2, 38.79) * mm});
            skArc(sketch, "E855.MirrorCS", {"start": v(35.87, 30.83) * mm, "mid": v(35.7, 30.62) * mm, "end": v(35.54, 30.4) * mm});
            skArc(sketch, "E856.MirrorCS", {"start": v(50.1, 24.74) * mm, "mid": v(50.1, 24.52) * mm, "end": v(50.1, 24.3) * mm});
            skArc(sketch, "E857.MirrorCS", {"start": v(36.25, 26.17) * mm, "mid": v(36.43, 26.47) * mm, "end": v(36.61, 26.76) * mm});
            skArc(sketch, "E858.MirrorCS", {"start": v(49.52, 24.57) * mm, "mid": v(49.45, 25.03) * mm, "end": v(49.43, 25.5) * mm});
            skArc(sketch, "E859.MirrorCS", {"start": v(44.68, 21.26) * mm, "mid": v(45.05, 21.36) * mm, "end": v(45.37, 21.57) * mm});
            skArc(sketch, "E860.MirrorCS", {"start": v(43.99, 40.86) * mm, "mid": v(44.28, 40.67) * mm, "end": v(44.53, 40.41) * mm});
            skArc(sketch, "E861.MirrorCS", {"start": v(50.27, 26.03) * mm, "mid": v(50.2, 25.74) * mm, "end": v(50.15, 25.44) * mm});
            skArc(sketch, "E862.MirrorCS", {"start": v(32.16, 29.65) * mm, "mid": v(32.04, 29.69) * mm, "end": v(31.93, 29.72) * mm});
            skArc(sketch, "E863.MirrorCS", {"start": v(52.13, 26.48) * mm, "mid": v(51.96, 26.81) * mm, "end": v(51.78, 27.14) * mm});
            skArc(sketch, "E864.MirrorCS", {"start": v(43.98, 21.4) * mm, "mid": v(44.32, 21.28) * mm, "end": v(44.68, 21.26) * mm});
            skArc(sketch, "E865.MirrorCS", {"start": v(32.42, 29.58) * mm, "mid": v(32.3, 29.61) * mm, "end": v(32.16, 29.65) * mm});
            skArc(sketch, "E866.MirrorCS", {"start": v(49.05, 38.4) * mm, "mid": v(49, 38.15) * mm, "end": v(48.96, 37.9) * mm});
            skArc(sketch, "E867.MirrorCS", {"start": v(54.24, 30.72) * mm, "mid": v(54.16, 30.72) * mm, "end": v(54.09, 30.7) * mm});
            skArc(sketch, "E868.MirrorCS", {"start": v(37.66, 25.62) * mm, "mid": v(37.29, 25.1) * mm, "end": v(36.94, 24.58) * mm});
            skArc(sketch, "E869.MirrorCS", {"start": v(51.46, 22.43) * mm, "mid": v(51.04, 22.48) * mm, "end": v(50.64, 22.62) * mm});
            skArc(sketch, "E870.MirrorCS", {"start": v(45.58, 20.95) * mm, "mid": v(45.26, 20.75) * mm, "end": v(44.91, 20.6) * mm});
            skArc(sketch, "E871.MirrorCS", {"start": v(48.38, 38.05) * mm, "mid": v(48.4, 38.23) * mm, "end": v(48.42, 38.4) * mm});
            skArc(sketch, "E872.MirrorCS", {"start": v(42.9, 41.03) * mm, "mid": v(43.07, 41.06) * mm, "end": v(43.25, 41.07) * mm});
            skArc(sketch, "E873.MirrorCS", {"start": v(49.22, 38.8) * mm, "mid": v(49.12, 38.6) * mm, "end": v(49.05, 38.4) * mm});
            skArc(sketch, "E874.MirrorCS", {"start": v(46.09, 21.48) * mm, "mid": v(45.86, 21.2) * mm, "end": v(45.58, 20.95) * mm});
            skArc(sketch, "E875.MirrorCS", {"start": v(49.48, 39.14) * mm, "mid": v(49.34, 38.98) * mm, "end": v(49.22, 38.8) * mm});
            skArc(sketch, "E876.MirrorCS", {"start": v(35.25, 29.05) * mm, "mid": v(35.4, 28.96) * mm, "end": v(35.53, 28.88) * mm});
            skArc(sketch, "E877.MirrorCS", {"start": v(42.7, 40.2) * mm, "mid": v(42.58, 40.1) * mm, "end": v(42.47, 40) * mm});
            skArc(sketch, "E878.MirrorCS", {"start": v(50.41, 39.41) * mm, "mid": v(50.26, 39.46) * mm, "end": v(50.1, 39.47) * mm});
            skArc(sketch, "E879.MirrorCS", {"start": v(35.2, 41.06) * mm, "mid": v(35.13, 41) * mm, "end": v(35.06, 40.92) * mm});
            skArc(sketch, "E880.MirrorCS", {"start": v(46.43, 22.17) * mm, "mid": v(46.28, 21.81) * mm, "end": v(46.09, 21.48) * mm});
            skArc(sketch, "E881.MirrorCS", {"start": v(42.14, 40.63) * mm, "mid": v(42.32, 40.77) * mm, "end": v(42.51, 40.88) * mm});
            skArc(sketch, "E882.MirrorCS", {"start": v(35, 29.2) * mm, "mid": v(35.13, 29.12) * mm, "end": v(35.25, 29.05) * mm});
            skArc(sketch, "E883.MirrorCS", {"start": v(34.46, 28.83) * mm, "mid": v(34.25, 28.92) * mm, "end": v(34.05, 29.02) * mm});
            skArc(sketch, "E884.MirrorCS", {"start": v(51.17, 38.48) * mm, "mid": v(51.02, 38.88) * mm, "end": v(50.73, 39.21) * mm});
            skArc(sketch, "E885.MirrorCS", {"start": v(37.5, 35.73) * mm, "mid": v(37.64, 36.12) * mm, "end": v(37.75, 36.51) * mm});
            skArc(sketch, "E886.MirrorCS", {"start": v(41.6, 39.84) * mm, "mid": v(41.7, 40.07) * mm, "end": v(41.84, 40.29) * mm});
            skArc(sketch, "E887.MirrorCS", {"start": v(51.39, 22.88) * mm, "mid": v(51.7, 22.95) * mm, "end": v(51.98, 23.13) * mm});
            skArc(sketch, "E888.MirrorCS", {"start": v(35.03, 32.12) * mm, "mid": v(35.43, 32.48) * mm, "end": v(35.83, 32.85) * mm});
            skArc(sketch, "E889.MirrorCS", {"start": v(41.4, 39.28) * mm, "mid": v(41.49, 39.56) * mm, "end": v(41.6, 39.84) * mm});
            skArc(sketch, "E890.MirrorCS", {"start": v(43.54, 40.37) * mm, "mid": v(43.43, 40.38) * mm, "end": v(43.3, 40.38) * mm});
            skArc(sketch, "E891.MirrorCS", {"start": v(36.85, 27.42) * mm, "mid": v(36.44, 27.68) * mm, "end": v(36.03, 27.94) * mm});
            skArc(sketch, "E892.MirrorCS", {"start": v(35.66, 42.06) * mm, "mid": v(35.86, 42.08) * mm, "end": v(36.07, 42.09) * mm});
            skArc(sketch, "E893.MirrorCS", {"start": v(41.3, 38.28) * mm, "mid": v(41.32, 38.78) * mm, "end": v(41.4, 39.28) * mm});
            skArc(sketch, "E894.MirrorCS", {"start": v(35.34, 35.35) * mm, "mid": v(35.67, 34.85) * mm, "end": v(36.05, 34.38) * mm});
            skArc(sketch, "E895.MirrorCS", {"start": v(39.24, 24.05) * mm, "mid": v(39.15, 24.38) * mm, "end": v(39.05, 24.7) * mm});
            skArc(sketch, "E896.MirrorCS", {"start": v(34.98, 41.7) * mm, "mid": v(35.08, 41.77) * mm, "end": v(35.18, 41.86) * mm});
            skArc(sketch, "E897.MirrorCS", {"start": v(44.07, 40.13) * mm, "mid": v(43.99, 40.2) * mm, "end": v(43.9, 40.25) * mm});
            skArc(sketch, "E898.MirrorCS", {"start": v(32.26, 30.02) * mm, "mid": v(32.46, 30.16) * mm, "end": v(32.67, 30.31) * mm});
            skArc(sketch, "E899.MirrorCS", {"start": v(52.3, 31.88) * mm, "mid": v(52.16, 31.98) * mm, "end": v(52.03, 32.08) * mm});
            skArc(sketch, "E900.MirrorCS", {"start": v(39.43, 22.61) * mm, "mid": v(39.4, 22.98) * mm, "end": v(39.36, 23.34) * mm});
            skArc(sketch, "E901.MirrorCS", {"start": v(35.54, 30.4) * mm, "mid": v(35.4, 30.25) * mm, "end": v(35.27, 30.1) * mm});
            skArc(sketch, "E902.MirrorCS", {"start": v(44.52, 39.5) * mm, "mid": v(44.33, 39.84) * mm, "end": v(44.07, 40.13) * mm});
            skLineSegment(sketch, "E903.MirrorCS", {"start": v(52.25, 30.86) * mm, "end": v(52.9, 31.47) * mm});
            skArc(sketch, "E904.MirrorCS", {"start": v(36.61, 26.76) * mm, "mid": v(36.67, 26.85) * mm, "end": v(36.73, 26.94) * mm});
            skArc(sketch, "E905.MirrorCS", {"start": v(44.53, 40.41) * mm, "mid": v(44.76, 40.08) * mm, "end": v(44.95, 39.7) * mm});
            skArc(sketch, "E906.MirrorCS", {"start": v(36.45, 41.23) * mm, "mid": v(36.25, 41.26) * mm, "end": v(36.06, 41.28) * mm});
            skArc(sketch, "E907.MirrorCS", {"start": v(31.93, 29.72) * mm, "mid": v(31.91, 29.73) * mm, "end": v(31.9, 29.73) * mm});
            skArc(sketch, "E908.MirrorCS", {"start": v(43.29, 21.2) * mm, "mid": v(43.05, 21.53) * mm, "end": v(42.86, 21.9) * mm});
            skArc(sketch, "E909.MirrorCS", {"start": v(36.42, 23.6) * mm, "mid": v(36.24, 23.16) * mm, "end": v(36.09, 22.7) * mm});
            skArc(sketch, "E910.MirrorCS", {"start": v(35.88, 25.45) * mm, "mid": v(36.06, 25.82) * mm, "end": v(36.25, 26.17) * mm});
            skArc(sketch, "E911.MirrorCS", {"start": v(43.8, 20.74) * mm, "mid": v(43.52, 20.95) * mm, "end": v(43.29, 21.2) * mm});
            skArc(sketch, "E912.MirrorCS", {"start": v(48.6, 38.97) * mm, "mid": v(48.73, 39.18) * mm, "end": v(48.85, 39.38) * mm});
            skArc(sketch, "E913.MirrorCS", {"start": v(36.94, 24.58) * mm, "mid": v(36.66, 24.1) * mm, "end": v(36.42, 23.6) * mm});
            skArc(sketch, "E914.MirrorCS", {"start": v(37.24, 40.63) * mm, "mid": v(37.02, 40.89) * mm, "end": v(36.75, 41.1) * mm});
            skArc(sketch, "E915.MirrorCS", {"start": v(54.09, 30.7) * mm, "mid": v(54, 30.67) * mm, "end": v(53.93, 30.62) * mm});
            skArc(sketch, "E916.MirrorCS", {"start": v(50.17, 23.03) * mm, "mid": v(49.95, 23.36) * mm, "end": v(49.78, 23.7) * mm});
            skArc(sketch, "E917.MirrorCS", {"start": v(49.8, 39.38) * mm, "mid": v(49.63, 39.27) * mm, "end": v(49.48, 39.14) * mm});
            skArc(sketch, "E918.MirrorCS", {"start": v(38.72, 36.26) * mm, "mid": v(38.65, 35.87) * mm, "end": v(38.56, 35.49) * mm});
            skArc(sketch, "E919.MirrorCS", {"start": v(38.75, 38.7) * mm, "mid": v(38.82, 37.9) * mm, "end": v(38.8, 37.1) * mm});
            skArc(sketch, "E920.MirrorCS", {"start": v(33.57, 29.2) * mm, "mid": v(33.34, 29.3) * mm, "end": v(33.11, 29.38) * mm});
            skArc(sketch, "E921.MirrorCS", {"start": v(52.2, 22.68) * mm, "mid": v(51.85, 22.5) * mm, "end": v(51.46, 22.43) * mm});
            skArc(sketch, "E922.MirrorCS", {"start": v(35.53, 28.88) * mm, "mid": v(35.7, 28.78) * mm, "end": v(35.85, 28.68) * mm});
            skArc(sketch, "E923.MirrorCS", {"start": v(50.1, 39.47) * mm, "mid": v(49.94, 39.44) * mm, "end": v(49.8, 39.38) * mm});
            skArc(sketch, "E924.MirrorCS", {"start": v(35.06, 40.92) * mm, "mid": v(34.99, 40.83) * mm, "end": v(34.92, 40.74) * mm});
            skArc(sketch, "E925.MirrorCS", {"start": v(34.05, 29.02) * mm, "mid": v(33.81, 29.11) * mm, "end": v(33.57, 29.2) * mm});
            skArc(sketch, "E926.MirrorCS", {"start": v(52.75, 23.34) * mm, "mid": v(52.52, 22.97) * mm, "end": v(52.2, 22.68) * mm});
            skArc(sketch, "E927.MirrorCS", {"start": v(37.75, 36.51) * mm, "mid": v(37.83, 36.88) * mm, "end": v(37.89, 37.26) * mm});
            skArc(sketch, "E928.MirrorCS", {"start": v(36.03, 27.94) * mm, "mid": v(35.61, 28.2) * mm, "end": v(35.2, 28.44) * mm});
            skArc(sketch, "E929.MirrorCS", {"start": v(36.07, 42.09) * mm, "mid": v(36.29, 42.07) * mm, "end": v(36.5, 42.03) * mm});
            skArc(sketch, "E930.MirrorCS", {"start": v(51.25, 39.81) * mm, "mid": v(51.64, 39.34) * mm, "end": v(51.89, 38.79) * mm});
            skArc(sketch, "E931.MirrorCS", {"start": v(50.87, 40.09) * mm, "mid": v(51.07, 39.96) * mm, "end": v(51.25, 39.81) * mm});
            skArc(sketch, "E932.MirrorCS", {"start": v(35.18, 41.86) * mm, "mid": v(35.24, 41.9) * mm, "end": v(35.32, 41.95) * mm});
            skArc(sketch, "E933.MirrorCS", {"start": v(32.67, 30.31) * mm, "mid": v(32.91, 30.48) * mm, "end": v(33.16, 30.66) * mm});
            skArc(sketch, "E934.MirrorCS", {"start": v(50.13, 40.23) * mm, "mid": v(50.32, 40.24) * mm, "end": v(50.5, 40.23) * mm});
            skArc(sketch, "E935.MirrorCS", {"start": v(34.85, 36.46) * mm, "mid": v(35.07, 35.9) * mm, "end": v(35.34, 35.35) * mm});
            skArc(sketch, "E936.MirrorCS", {"start": v(49.72, 40.1) * mm, "mid": v(49.92, 40.18) * mm, "end": v(50.13, 40.23) * mm});
            skArc(sketch, "E937.MirrorCS", {"start": v(36.06, 41.28) * mm, "mid": v(35.85, 41.28) * mm, "end": v(35.65, 41.25) * mm});
            skArc(sketch, "E938.MirrorCS", {"start": v(31.9, 29.73) * mm, "mid": v(31.9, 29.74) * mm, "end": v(31.9, 29.75) * mm});
            skArc(sketch, "E939.MirrorCS", {"start": v(48.85, 39.38) * mm, "mid": v(48.97, 39.54) * mm, "end": v(49.1, 39.68) * mm});
            skArc(sketch, "E940.MirrorCS", {"start": v(40.04, 22.59) * mm, "mid": v(40.04, 22.28) * mm, "end": v(40.03, 21.97) * mm});
            skArc(sketch, "E941.MirrorCS", {"start": v(39.16, 20.49) * mm, "mid": v(39.27, 20.8) * mm, "end": v(39.34, 21.11) * mm});
            skArc(sketch, "E942.MirrorCS", {"start": v(36.75, 41.1) * mm, "mid": v(36.6, 41.18) * mm, "end": v(36.45, 41.23) * mm});
            skArc(sketch, "E943.MirrorCS", {"start": v(53.93, 30.62) * mm, "mid": v(53.71, 30.43) * mm, "end": v(53.5, 30.24) * mm});
            skArc(sketch, "E944.MirrorCS", {"start": v(34.67, 40.29) * mm, "mid": v(34.63, 40.15) * mm, "end": v(34.6, 40.01) * mm});
            skArc(sketch, "E945.MirrorCS", {"start": v(35.54, 24.72) * mm, "mid": v(35.7, 25.09) * mm, "end": v(35.88, 25.45) * mm});
            skArc(sketch, "E946.MirrorCS", {"start": v(43.6, 41.02) * mm, "mid": v(43.8, 40.95) * mm, "end": v(43.99, 40.86) * mm});
            skArc(sketch, "E947.MirrorCS", {"start": v(37.62, 39.93) * mm, "mid": v(37.45, 40.29) * mm, "end": v(37.24, 40.63) * mm});
            skArc(sketch, "E948.MirrorCS", {"start": v(35.3, 24.09) * mm, "mid": v(35.42, 24.4) * mm, "end": v(35.54, 24.72) * mm});
            skArc(sketch, "E949.MirrorCS", {"start": v(34.92, 40.74) * mm, "mid": v(34.86, 40.66) * mm, "end": v(34.8, 40.57) * mm});
            skArc(sketch, "E950.MirrorCS", {"start": v(37.85, 39.06) * mm, "mid": v(37.76, 39.5) * mm, "end": v(37.62, 39.93) * mm});
            skArc(sketch, "E951.MirrorCS", {"start": v(35.12, 23.25) * mm, "mid": v(35.2, 23.67) * mm, "end": v(35.3, 24.09) * mm});
            skArc(sketch, "E952.MirrorCS", {"start": v(33.11, 29.38) * mm, "mid": v(32.92, 29.44) * mm, "end": v(32.74, 29.5) * mm});
            skArc(sketch, "E953.MirrorCS", {"start": v(54.5, 30.64) * mm, "mid": v(54.37, 30.69) * mm, "end": v(54.24, 30.72) * mm});
            skArc(sketch, "E954.MirrorCS", {"start": v(38.8, 37.1) * mm, "mid": v(38.78, 36.68) * mm, "end": v(38.72, 36.26) * mm});
            skArc(sketch, "E955.MirrorCS", {"start": v(38.38, 40.1) * mm, "mid": v(38.6, 39.42) * mm, "end": v(38.75, 38.7) * mm});
            skArc(sketch, "E956.MirrorCS", {"start": v(37.75, 41.2) * mm, "mid": v(38.1, 40.67) * mm, "end": v(38.38, 40.1) * mm});
            skArc(sketch, "E957.MirrorCS", {"start": v(36.9, 41.88) * mm, "mid": v(37.36, 41.59) * mm, "end": v(37.75, 41.2) * mm});
            skArc(sketch, "E958.MirrorCS", {"start": v(37.93, 38.08) * mm, "mid": v(37.91, 38.57) * mm, "end": v(37.85, 39.06) * mm});
            skArc(sketch, "E959.MirrorCS", {"start": v(37.89, 37.26) * mm, "mid": v(37.92, 37.67) * mm, "end": v(37.93, 38.08) * mm});
            skArc(sketch, "E960.MirrorCS", {"start": v(36.5, 42.03) * mm, "mid": v(36.7, 41.97) * mm, "end": v(36.9, 41.88) * mm});
            skArc(sketch, "E961.MirrorCS", {"start": v(53.02, 25.2) * mm, "mid": v(53.04, 24.75) * mm, "end": v(53.02, 24.31) * mm});
            skArc(sketch, "E962.MirrorCS", {"start": v(34.09, 31.34) * mm, "mid": v(34.56, 31.72) * mm, "end": v(35.03, 32.12) * mm});
            skArc(sketch, "E963.MirrorCS", {"start": v(33.16, 30.66) * mm, "mid": v(33.63, 31) * mm, "end": v(34.09, 31.34) * mm});
            skArc(sketch, "E964.MirrorCS", {"start": v(35.32, 41.95) * mm, "mid": v(35.48, 42.02) * mm, "end": v(35.66, 42.06) * mm});
            skArc(sketch, "E965.MirrorCS", {"start": v(31.9, 29.75) * mm, "mid": v(32.08, 29.89) * mm, "end": v(32.26, 30.02) * mm});
            skLineSegment(sketch, "E966.MirrorCS", {"start": v(53.25, 31.8) * mm, "end": v(54.37, 32.55) * mm});
            skArc(sketch, "E967.MirrorCS", {"start": v(35.65, 41.25) * mm, "mid": v(35.49, 41.21) * mm, "end": v(35.33, 41.15) * mm});
            skArc(sketch, "E968.MirrorCS", {"start": v(39.42, 21.88) * mm, "mid": v(39.43, 22.24) * mm, "end": v(39.43, 22.61) * mm});
            skArc(sketch, "E969.MirrorCS", {"start": v(40.03, 21.97) * mm, "mid": v(39.98, 21.37) * mm, "end": v(39.9, 20.78) * mm});
            skArc(sketch, "E970.MirrorCS", {"start": v(52.2, 32.54) * mm, "mid": v(52.37, 32.42) * mm, "end": v(52.52, 32.3) * mm});
            skArc(sketch, "E971.MirrorCS", {"start": v(39.34, 21.11) * mm, "mid": v(39.4, 21.5) * mm, "end": v(39.42, 21.88) * mm});
            skArc(sketch, "E972.MirrorCS", {"start": v(53.5, 30.24) * mm, "mid": v(53.25, 30) * mm, "end": v(53, 29.77) * mm});
            skArc(sketch, "E973.MirrorCS", {"start": v(34.6, 40.01) * mm, "mid": v(34.57, 39.83) * mm, "end": v(34.55, 39.65) * mm});
            skArc(sketch, "E974.MirrorCS", {"start": v(38.52, 19.55) * mm, "mid": v(38.72, 19.75) * mm, "end": v(38.9, 19.97) * mm});
            skArc(sketch, "E975.MirrorCS", {"start": v(37.91, 19.2) * mm, "mid": v(38.01, 19.22) * mm, "end": v(38.11, 19.25) * mm});
            skArc(sketch, "E976.MirrorCS", {"start": v(54.77, 31.22) * mm, "mid": v(54.75, 31.18) * mm, "end": v(54.75, 31.13) * mm});
            skArc(sketch, "E977.MirrorCS", {"start": v(34.55, 39.65) * mm, "mid": v(34.53, 39.35) * mm, "end": v(34.52, 39.05) * mm});
            skArc(sketch, "E978.MirrorCS", {"start": v(38.9, 19.97) * mm, "mid": v(39.04, 20.22) * mm, "end": v(39.16, 20.49) * mm});
            skArc(sketch, "E979.MirrorCS", {"start": v(44.35, 20.54) * mm, "mid": v(44.06, 20.61) * mm, "end": v(43.8, 20.74) * mm});
            skArc(sketch, "E980.MirrorCS", {"start": v(38.11, 19.25) * mm, "mid": v(38.2, 19.3) * mm, "end": v(38.3, 19.35) * mm});
            skArc(sketch, "E981.MirrorCS", {"start": v(53.02, 24.31) * mm, "mid": v(52.93, 23.82) * mm, "end": v(52.75, 23.34) * mm});
            skArc(sketch, "E982.MirrorCS", {"start": v(36.91, 19.39) * mm, "mid": v(37, 19.32) * mm, "end": v(37.1, 19.26) * mm});
            skArc(sketch, "E983.MirrorCS", {"start": v(54.75, 31.13) * mm, "mid": v(54.78, 31.08) * mm, "end": v(54.82, 31.04) * mm});
            skArc(sketch, "E984.MirrorCS", {"start": v(39.9, 20.78) * mm, "mid": v(39.78, 20.33) * mm, "end": v(39.6, 19.9) * mm});
            skArc(sketch, "E985.MirrorCS", {"start": v(34.52, 39.05) * mm, "mid": v(34.52, 38.37) * mm, "end": v(34.58, 37.69) * mm});
            skArc(sketch, "E986.MirrorCS", {"start": v(33.8, 39.75) * mm, "mid": v(34.08, 40.57) * mm, "end": v(34.57, 41.28) * mm});
            skArc(sketch, "E987.MirrorCS", {"start": v(38.3, 19.35) * mm, "mid": v(38.4, 19.45) * mm, "end": v(38.52, 19.55) * mm});
            skArc(sketch, "E988.MirrorCS", {"start": v(35.15, 21.4) * mm, "mid": v(35.1, 21.86) * mm, "end": v(35.07, 22.33) * mm});
            skArc(sketch, "E989.MirrorCS", {"start": v(52.07, 37.34) * mm, "mid": v(51.98, 36.52) * mm, "end": v(51.77, 35.73) * mm});
            skArc(sketch, "E990.MirrorCS", {"start": v(51.89, 38.79) * mm, "mid": v(52.04, 38.07) * mm, "end": v(52.07, 37.34) * mm});
            skArc(sketch, "E991.MirrorCS", {"start": v(37.1, 19.26) * mm, "mid": v(37.2, 19.23) * mm, "end": v(37.3, 19.2) * mm});
            skArc(sketch, "E992.MirrorCS", {"start": v(54.82, 31.04) * mm, "mid": v(55, 30.93) * mm, "end": v(55.2, 30.85) * mm});
            skArc(sketch, "E993.MirrorCS", {"start": v(39.6, 19.9) * mm, "mid": v(39.38, 19.54) * mm, "end": v(39.11, 19.24) * mm});
            skArc(sketch, "E994.MirrorCS", {"start": v(34.58, 37.69) * mm, "mid": v(34.68, 37.07) * mm, "end": v(34.85, 36.46) * mm});
            skArc(sketch, "E995.MirrorCS", {"start": v(55.29, 31.59) * mm, "mid": v(55.1, 31.46) * mm, "end": v(54.9, 31.34) * mm});
            skArc(sketch, "E996.MirrorCS", {"start": v(36.09, 22.7) * mm, "mid": v(36, 22.28) * mm, "end": v(35.94, 21.84) * mm});
            skArc(sketch, "E997.MirrorCS", {"start": v(35.89, 33.8) * mm, "mid": v(35.13, 34.7) * mm, "end": v(34.5, 35.7) * mm});
            skArc(sketch, "E998.MirrorCS", {"start": v(35.07, 22.33) * mm, "mid": v(35.08, 22.79) * mm, "end": v(35.12, 23.25) * mm});
            skArc(sketch, "E999.MirrorCS", {"start": v(55.1, 30.4) * mm, "mid": v(54.8, 30.52) * mm, "end": v(54.5, 30.64) * mm});
            skArc(sketch, "E1000.MirrorCS", {"start": v(37.61, 19.2) * mm, "mid": v(37.76, 19.2) * mm, "end": v(37.91, 19.2) * mm});
            skArc(sketch, "E1001.MirrorCS", {"start": v(36.26, 20.14) * mm, "mid": v(36.43, 19.9) * mm, "end": v(36.62, 19.68) * mm});
            skArc(sketch, "E1002.MirrorCS", {"start": v(35.93, 21.15) * mm, "mid": v(35.97, 20.87) * mm, "end": v(36.03, 20.6) * mm});
            skArc(sketch, "E1003.MirrorCS", {"start": v(54.9, 31.34) * mm, "mid": v(54.83, 31.28) * mm, "end": v(54.77, 31.22) * mm});
            skArc(sketch, "E1004.MirrorCS", {"start": v(35.94, 21.84) * mm, "mid": v(35.93, 21.5) * mm, "end": v(35.93, 21.15) * mm});
            skArc(sketch, "E1005.MirrorCS", {"start": v(33.78, 37.8) * mm, "mid": v(33.7, 38.77) * mm, "end": v(33.8, 39.75) * mm});
            skArc(sketch, "E1006.MirrorCS", {"start": v(35.35, 20.55) * mm, "mid": v(35.23, 20.97) * mm, "end": v(35.15, 21.4) * mm});
            skArc(sketch, "E1007.MirrorCS", {"start": v(37.3, 19.2) * mm, "mid": v(37.45, 19.2) * mm, "end": v(37.61, 19.2) * mm});
            skArc(sketch, "E1008.MirrorCS", {"start": v(55.2, 30.85) * mm, "mid": v(55.72, 30.68) * mm, "end": v(56.24, 30.52) * mm});
            skArc(sketch, "E1009.MirrorCS", {"start": v(36.62, 19.68) * mm, "mid": v(36.76, 19.53) * mm, "end": v(36.91, 19.39) * mm});
            skArc(sketch, "E1010.MirrorCS", {"start": v(36.03, 20.6) * mm, "mid": v(36.13, 20.36) * mm, "end": v(36.26, 20.14) * mm});
            skArc(sketch, "E1011.MirrorCS", {"start": v(66.4, 31.52) * mm, "mid": v(66.47, 31.6) * mm, "end": v(66.52, 31.69) * mm});
            skArc(sketch, "E1012.MirrorCS", {"start": v(55.96, 30.07) * mm, "mid": v(55.53, 30.23) * mm, "end": v(55.1, 30.4) * mm});
            skArc(sketch, "E1013.MirrorCS", {"start": v(56.92, 29.78) * mm, "mid": v(56.44, 29.92) * mm, "end": v(55.96, 30.07) * mm});
            skArc(sketch, "E1014.MirrorCS", {"start": v(57.97, 29.53) * mm, "mid": v(57.44, 29.65) * mm, "end": v(56.92, 29.78) * mm});
            skArc(sketch, "E1015.MirrorCS", {"start": v(56.24, 30.52) * mm, "mid": v(56.79, 30.36) * mm, "end": v(57.34, 30.21) * mm});
            skArc(sketch, "E1016.MirrorCS", {"start": v(36.6, 18.7) * mm, "mid": v(36.2, 19) * mm, "end": v(35.9, 19.39) * mm});
            skArc(sketch, "E1017.MirrorCS", {"start": v(37.45, 18.49) * mm, "mid": v(37.01, 18.53) * mm, "end": v(36.6, 18.7) * mm});
            skArc(sketch, "E1018.MirrorCS", {"start": v(38.41, 18.75) * mm, "mid": v(37.94, 18.57) * mm, "end": v(37.45, 18.49) * mm});
            skArc(sketch, "E1019.MirrorCS", {"start": v(39.11, 19.24) * mm, "mid": v(38.78, 18.97) * mm, "end": v(38.41, 18.75) * mm});
            skArc(sketch, "E1020.MirrorCS", {"start": v(54.37, 32.55) * mm, "mid": v(55.03, 32.97) * mm, "end": v(55.72, 33.33) * mm});
            skArc(sketch, "E1021.MirrorCS", {"start": v(66.52, 32.54) * mm, "mid": v(66.44, 32.72) * mm, "end": v(66.33, 32.89) * mm});
            skArc(sketch, "E1022.MirrorCS", {"start": v(56.5, 32.24) * mm, "mid": v(55.88, 31.94) * mm, "end": v(55.29, 31.59) * mm});
            skArc(sketch, "E1023.MirrorCS", {"start": v(66.52, 31.69) * mm, "mid": v(66.55, 31.77) * mm, "end": v(66.57, 31.87) * mm});
            skArc(sketch, "E1024.MirrorCS", {"start": v(57.34, 30.21) * mm, "mid": v(57.77, 30.1) * mm, "end": v(58.2, 30.02) * mm});
            skArc(sketch, "E1025.MirrorCS", {"start": v(35.9, 19.39) * mm, "mid": v(35.6, 19.96) * mm, "end": v(35.35, 20.55) * mm});
            skArc(sketch, "E1026.MirrorCS", {"start": v(59.07, 29.33) * mm, "mid": v(58.52, 29.42) * mm, "end": v(57.97, 29.53) * mm});
            skArc(sketch, "E1027.MirrorCS", {"start": v(66.33, 32.89) * mm, "mid": v(66.19, 33.04) * mm, "end": v(66.01, 33.17) * mm});
            skArc(sketch, "E1028.MirrorCS", {"start": v(66.57, 31.87) * mm, "mid": v(66.58, 32) * mm, "end": v(66.58, 32.13) * mm});
            skArc(sketch, "E1029.MirrorCS", {"start": v(58.03, 32.86) * mm, "mid": v(57.26, 32.57) * mm, "end": v(56.5, 32.24) * mm});
            skArc(sketch, "E1030.MirrorCS", {"start": v(34.5, 35.7) * mm, "mid": v(34.06, 36.72) * mm, "end": v(33.78, 37.8) * mm});
            skArc(sketch, "E1031.MirrorCS", {"start": v(66.98, 33.52) * mm, "mid": v(67.19, 33.26) * mm, "end": v(67.36, 32.98) * mm});
            skArc(sketch, "E1032.MirrorCS", {"start": v(66.19, 31.3) * mm, "mid": v(66.3, 31.4) * mm, "end": v(66.4, 31.52) * mm});
            skArc(sketch, "E1033.MirrorCS", {"start": v(64.91, 30.53) * mm, "mid": v(65.6, 30.84) * mm, "end": v(66.19, 31.3) * mm});
            skArc(sketch, "E1034.MirrorCS", {"start": v(58.2, 30.02) * mm, "mid": v(59.34, 29.88) * mm, "end": v(60.47, 29.84) * mm});
            skArc(sketch, "E1035.MirrorCS", {"start": v(64.66, 33.67) * mm, "mid": v(64.15, 33.75) * mm, "end": v(63.62, 33.8) * mm});
            skArc(sketch, "E1036.MirrorCS", {"start": v(65.54, 33.41) * mm, "mid": v(65.1, 33.56) * mm, "end": v(64.66, 33.67) * mm});
            skArc(sketch, "E1037.MirrorCS", {"start": v(66.01, 33.17) * mm, "mid": v(65.78, 33.3) * mm, "end": v(65.54, 33.41) * mm});
            skArc(sketch, "E1038.MirrorCS", {"start": v(55.72, 33.33) * mm, "mid": v(56.45, 33.67) * mm, "end": v(57.2, 33.95) * mm});
            skArc(sketch, "E1039.MirrorCS", {"start": v(66.12, 30.26) * mm, "mid": v(65.05, 29.85) * mm, "end": v(63.95, 29.55) * mm});
            skArc(sketch, "E1040.MirrorCS", {"start": v(67.33, 31.23) * mm, "mid": v(66.8, 30.66) * mm, "end": v(66.12, 30.26) * mm});
            skArc(sketch, "E1041.MirrorCS", {"start": v(67.48, 31.57) * mm, "mid": v(67.43, 31.4) * mm, "end": v(67.33, 31.23) * mm});
            skArc(sketch, "E1042.MirrorCS", {"start": v(67.54, 32.06) * mm, "mid": v(67.52, 31.82) * mm, "end": v(67.48, 31.57) * mm});
            skArc(sketch, "E1043.MirrorCS", {"start": v(66.58, 32.13) * mm, "mid": v(66.57, 32.34) * mm, "end": v(66.52, 32.54) * mm});
            skArc(sketch, "E1044.MirrorCS", {"start": v(67.5, 32.57) * mm, "mid": v(67.53, 32.32) * mm, "end": v(67.54, 32.06) * mm});
            skArc(sketch, "E1045.MirrorCS", {"start": v(67.36, 32.98) * mm, "mid": v(67.45, 32.78) * mm, "end": v(67.5, 32.57) * mm});
            skArc(sketch, "E1046.MirrorCS", {"start": v(59.65, 33.35) * mm, "mid": v(58.83, 33.12) * mm, "end": v(58.03, 32.86) * mm});
            skArc(sketch, "E1047.MirrorCS", {"start": v(66.46, 33.95) * mm, "mid": v(66.73, 33.75) * mm, "end": v(66.98, 33.52) * mm});
            skArc(sketch, "E1048.MirrorCS", {"start": v(65.75, 34.3) * mm, "mid": v(66.11, 34.14) * mm, "end": v(66.46, 33.95) * mm});
            skArc(sketch, "E1049.MirrorCS", {"start": v(64.78, 34.6) * mm, "mid": v(65.27, 34.45) * mm, "end": v(65.75, 34.3) * mm});
            skArc(sketch, "E1050.MirrorCS", {"start": v(62.84, 30.03) * mm, "mid": v(63.89, 30.24) * mm, "end": v(64.91, 30.53) * mm});
            skArc(sketch, "E1051.MirrorCS", {"start": v(60.47, 29.84) * mm, "mid": v(61.66, 29.89) * mm, "end": v(62.84, 30.03) * mm});
            skArc(sketch, "E1052.MirrorCS", {"start": v(63.77, 34.8) * mm, "mid": v(64.28, 34.7) * mm, "end": v(64.78, 34.6) * mm});
            skArc(sketch, "E1053.MirrorCS", {"start": v(62.79, 34.9) * mm, "mid": v(63.28, 34.86) * mm, "end": v(63.77, 34.8) * mm});
            skArc(sketch, "E1054.MirrorCS", {"start": v(61.78, 34.9) * mm, "mid": v(62.29, 34.9) * mm, "end": v(62.79, 34.9) * mm});
            skArc(sketch, "E1055.MirrorCS", {"start": v(63.62, 33.8) * mm, "mid": v(63.03, 33.81) * mm, "end": v(62.44, 33.8) * mm});
            skArc(sketch, "E1056.MirrorCS", {"start": v(61.44, 29.2) * mm, "mid": v(60.25, 29.2) * mm, "end": v(59.07, 29.33) * mm});
            skArc(sketch, "E1057.MirrorCS", {"start": v(61.16, 33.66) * mm, "mid": v(60.4, 33.53) * mm, "end": v(59.65, 33.35) * mm});
            skArc(sketch, "E1058.MirrorCS", {"start": v(62.44, 33.8) * mm, "mid": v(61.8, 33.74) * mm, "end": v(61.16, 33.66) * mm});
            skArc(sketch, "E1059.MirrorCS", {"start": v(60.73, 34.79) * mm, "mid": v(61.26, 34.85) * mm, "end": v(61.78, 34.9) * mm});
            skArc(sketch, "E1060.MirrorCS", {"start": v(58.85, 34.43) * mm, "mid": v(59.79, 34.63) * mm, "end": v(60.73, 34.79) * mm});
            skArc(sketch, "E1061.MirrorCS", {"start": v(57.2, 33.95) * mm, "mid": v(58.01, 34.22) * mm, "end": v(58.85, 34.43) * mm});
            skArc(sketch, "E1062.MirrorCS", {"start": v(63.95, 29.55) * mm, "mid": v(62.7, 29.31) * mm, "end": v(61.44, 29.2) * mm});
            skSolve(sketch);
        }
        {
            var Q0;
            Q0=qSketchRegion(id+"F4",true);
            extrude(context, id + "F5", {"entities" : qUnion([Q0]), "operationType" : NewBodyOperationType.ADD, "depth" : 1.59 * mm, "offsetDistance" : 25.4 * mm});
        }
        {
            var Q0;
            Q0=makeQuery(id+"F5.boolean.opBoolean","SPLIT",FACE,{"disambiguationData":[TD([makeQuery(id+"F3.opExtrude","SWEPT_FACE",FACE,{"disambiguationData":[OSD([sQuery(id+"F2.wireOp",EDGE,"E5.bottom")])]})])],"derivedFrom":makeQuery(id+"F1.opExtrude","CAP_FACE",FACE,{"disambiguationData":[OSD([sQuery(id+"F0.wireOp",EDGE,"E0.bottom"),sQuery(id+"F0.wireOp",EDGE,"E0.top"),sQuery(id+"F0.wireOp",EDGE,"E0.left"),sQuery(id+"F0.wireOp",EDGE,"E0.right"),sQuery(id+"F0.wireOp",EDGE,"E1.filletArc"),sQuery(id+"F0.wireOp",EDGE,"E2.filletArc"),sQuery(id+"F0.wireOp",EDGE,"E3.filletArc"),sQuery(id+"F0.wireOp",EDGE,"E4.filletArc")])],"isStart":false})});
            var sketch = newSketch(context, id + "F6", { "sketchPlane" : qUnion([Q0])});
            skText(sketch, "E1063", { "text": "Rohr\'s", "fontName": "RobotoSlab-Regular.ttf"});
            const initialGuessF6  = {"E1063": [-0.03171, 0.02311, 1, 0, 0.01499]};
            skSetInitialGuess(sketch, initialGuessF6);
            skSolve(sketch);
        }
        {
            var Q0;
            Q0=qSketchRegion(id+"F6",true);
            extrude(context, id + "F7", {"entities" : qUnion([Q0]), "operationType" : NewBodyOperationType.ADD, "depth" : 1.59 * mm, "offsetDistance" : 25.4 * mm});
        }
        {
            var Q0;
            {var subQ295=makeQuery(id+"F3.opExtrude","SWEPT_FACE",FACE,{"disambiguationData":[OSD([sQuery(id+"F2.wireOp",EDGE,"E5.bottom")])]});Q0=makeQuery(id+"F7.boolean.opBoolean","SPLIT",FACE,{"disambiguationData":[TD([subQ295])],"derivedFrom":makeQuery(id+"F5.boolean.opBoolean","SPLIT",FACE,{"disambiguationData":[TD([subQ295])],"derivedFrom":makeQuery(id+"F1.opExtrude","CAP_FACE",FACE,{"disambiguationData":[OSD([sQuery(id+"F0.wireOp",EDGE,"E0.bottom"),sQuery(id+"F0.wireOp",EDGE,"E0.top"),sQuery(id+"F0.wireOp",EDGE,"E0.left"),sQuery(id+"F0.wireOp",EDGE,"E0.right"),sQuery(id+"F0.wireOp",EDGE,"E1.filletArc"),sQuery(id+"F0.wireOp",EDGE,"E2.filletArc"),sQuery(id+"F0.wireOp",EDGE,"E3.filletArc"),sQuery(id+"F0.wireOp",EDGE,"E4.filletArc")])],"isStart":false})})});}
            var sketch = newSketch(context, id + "F8", { "sketchPlane" : qUnion([Q0])});
            skArc(sketch, "E1064", {"start": v(-0.5, 18.82) * mm, "mid": v(-0.63, 18.64) * mm, "end": v(-0.77, 18.47) * mm});
            skArc(sketch, "E1065", {"start": v(-0.77, 18.47) * mm, "mid": v(-0.94, 18.26) * mm, "end": v(-1.11, 18.06) * mm});
            skArc(sketch, "E1066", {"start": v(-1.11, 18.06) * mm, "mid": v(-1.28, 17.86) * mm, "end": v(-1.45, 17.66) * mm});
            skArc(sketch, "E1067", {"start": v(-1.45, 17.66) * mm, "mid": v(-1.6, 17.5) * mm, "end": v(-1.75, 17.35) * mm});
            skLineSegment(sketch, "E1068", {"start": v(-1.75, 17.35) * mm, "end": v(-2.4, 16.67) * mm});
            skLineSegment(sketch, "E1069", {"start": v(-2.4, 16.67) * mm, "end": v(-3.66, 17.3) * mm});
            skArc(sketch, "E1070", {"start": v(-3.66, 17.3) * mm, "mid": v(-4.41, 17.66) * mm, "end": v(-5.17, 18) * mm});
            skArc(sketch, "E1071", {"start": v(-5.17, 18) * mm, "mid": v(-5.79, 18.23) * mm, "end": v(-6.41, 18.44) * mm});
            skArc(sketch, "E1072", {"start": v(-6.41, 18.44) * mm, "mid": v(-7, 18.59) * mm, "end": v(-7.58, 18.7) * mm});
            skArc(sketch, "E1073", {"start": v(-7.58, 18.7) * mm, "mid": v(-8.22, 18.78) * mm, "end": v(-8.85, 18.83) * mm});
            skArc(sketch, "E1074", {"start": v(-8.85, 18.83) * mm, "mid": v(-9.28, 18.84) * mm, "end": v(-9.72, 18.83) * mm});
            skArc(sketch, "E1075", {"start": v(-9.72, 18.83) * mm, "mid": v(-10.1, 18.8) * mm, "end": v(-10.48, 18.75) * mm});
            skArc(sketch, "E1076", {"start": v(-10.48, 18.75) * mm, "mid": v(-10.82, 18.68) * mm, "end": v(-11.16, 18.58) * mm});
            skArc(sketch, "E1077", {"start": v(-11.16, 18.58) * mm, "mid": v(-11.5, 18.46) * mm, "end": v(-11.81, 18.32) * mm});
            skArc(sketch, "E1078", {"start": v(-11.81, 18.32) * mm, "mid": v(-12.2, 18.1) * mm, "end": v(-12.58, 17.83) * mm});
            skArc(sketch, "E1079", {"start": v(-12.58, 17.83) * mm, "mid": v(-12.9, 17.54) * mm, "end": v(-13.2, 17.2) * mm});
            skArc(sketch, "E1080", {"start": v(-13.2, 17.2) * mm, "mid": v(-13.43, 16.87) * mm, "end": v(-13.61, 16.51) * mm});
            skArc(sketch, "E1081", {"start": v(-13.61, 16.51) * mm, "mid": v(-13.73, 16.17) * mm, "end": v(-13.77, 15.82) * mm});
            skArc(sketch, "E1082", {"start": v(-13.77, 15.82) * mm, "mid": v(-13.78, 15.7) * mm, "end": v(-13.8, 15.59) * mm});
            skArc(sketch, "E1083", {"start": v(-13.8, 15.59) * mm, "mid": v(-13.8, 15.52) * mm, "end": v(-13.84, 15.45) * mm});
            skArc(sketch, "E1084", {"start": v(-13.84, 15.45) * mm, "mid": v(-13.87, 15.4) * mm, "end": v(-13.92, 15.35) * mm});
            skArc(sketch, "E1085", {"start": v(-13.92, 15.35) * mm, "mid": v(-14, 15.3) * mm, "end": v(-14.07, 15.25) * mm});
            skArc(sketch, "E1086", {"start": v(-14.07, 15.25) * mm, "mid": v(-14.28, 15.12) * mm, "end": v(-14.48, 14.99) * mm});
            skArc(sketch, "E1087", {"start": v(-14.48, 14.99) * mm, "mid": v(-14.79, 14.76) * mm, "end": v(-15.09, 14.52) * mm});
            skArc(sketch, "E1088", {"start": v(-15.09, 14.52) * mm, "mid": v(-15.38, 14.27) * mm, "end": v(-15.67, 14.02) * mm});
            skArc(sketch, "E1089", {"start": v(-15.67, 14.02) * mm, "mid": v(-15.86, 13.85) * mm, "end": v(-16.03, 13.66) * mm});
            skArc(sketch, "E1090", {"start": v(-16.03, 13.66) * mm, "mid": v(-16.38, 13.2) * mm, "end": v(-16.64, 12.69) * mm});
            skArc(sketch, "E1091", {"start": v(-16.64, 12.69) * mm, "mid": v(-16.8, 12.16) * mm, "end": v(-16.86, 11.62) * mm});
            skArc(sketch, "E1092", {"start": v(-16.86, 11.62) * mm, "mid": v(-16.82, 11.08) * mm, "end": v(-16.67, 10.56) * mm});
            skArc(sketch, "E1093", {"start": v(-16.67, 10.56) * mm, "mid": v(-16.42, 10.07) * mm, "end": v(-16.08, 9.62) * mm});
            skArc(sketch, "E1094", {"start": v(-16.08, 9.62) * mm, "mid": v(-15.81, 9.35) * mm, "end": v(-15.52, 9.1) * mm});
            skArc(sketch, "E1095", {"start": v(-15.52, 9.1) * mm, "mid": v(-15.2, 8.88) * mm, "end": v(-14.87, 8.7) * mm});
            skArc(sketch, "E1096", {"start": v(-14.87, 8.7) * mm, "mid": v(-14.52, 8.53) * mm, "end": v(-14.15, 8.4) * mm});
            skArc(sketch, "E1097", {"start": v(-14.15, 8.4) * mm, "mid": v(-13.77, 8.3) * mm, "end": v(-13.37, 8.23) * mm});
            skArc(sketch, "E1098", {"start": v(-13.37, 8.23) * mm, "mid": v(-13.25, 8.2) * mm, "end": v(-13.13, 8.18) * mm});
            skArc(sketch, "E1099", {"start": v(-13.13, 8.18) * mm, "mid": v(-13.05, 8.16) * mm, "end": v(-12.98, 8.13) * mm});
            skArc(sketch, "E1100", {"start": v(-12.98, 8.13) * mm, "mid": v(-12.93, 8.1) * mm, "end": v(-12.88, 8.04) * mm});
            skArc(sketch, "E1101", {"start": v(-12.88, 8.04) * mm, "mid": v(-12.84, 7.98) * mm, "end": v(-12.8, 7.9) * mm});
            skArc(sketch, "E1102", {"start": v(-12.8, 7.9) * mm, "mid": v(-12.73, 7.75) * mm, "end": v(-12.63, 7.62) * mm});
            skArc(sketch, "E1103", {"start": v(-12.63, 7.62) * mm, "mid": v(-12.5, 7.46) * mm, "end": v(-12.36, 7.32) * mm});
            skArc(sketch, "E1104", {"start": v(-12.36, 7.32) * mm, "mid": v(-12.18, 7.18) * mm, "end": v(-12, 7.05) * mm});
            skArc(sketch, "E1105", {"start": v(-12, 7.05) * mm, "mid": v(-11.81, 6.94) * mm, "end": v(-11.61, 6.84) * mm});
            skArc(sketch, "E1106", {"start": v(-11.61, 6.84) * mm, "mid": v(-11.47, 6.78) * mm, "end": v(-11.32, 6.73) * mm});
            skArc(sketch, "E1107", {"start": v(-11.32, 6.73) * mm, "mid": v(-11.18, 6.7) * mm, "end": v(-11.04, 6.66) * mm});
            skArc(sketch, "E1108", {"start": v(-11.04, 6.66) * mm, "mid": v(-10.87, 6.64) * mm, "end": v(-10.7, 6.64) * mm});
            skArc(sketch, "E1109", {"start": v(-10.7, 6.64) * mm, "mid": v(-10.42, 6.63) * mm, "end": v(-10.14, 6.63) * mm});
            skArc(sketch, "E1110", {"start": v(-10.14, 6.63) * mm, "mid": v(-9.52, 6.66) * mm, "end": v(-8.9, 6.73) * mm});
            skArc(sketch, "E1111", {"start": v(-8.9, 6.73) * mm, "mid": v(-8.3, 6.84) * mm, "end": v(-7.69, 7) * mm});
            skArc(sketch, "E1112", {"start": v(-7.69, 7) * mm, "mid": v(-7.05, 7.22) * mm, "end": v(-6.42, 7.47) * mm});
            skArc(sketch, "E1113", {"start": v(-6.42, 7.47) * mm, "mid": v(-5.74, 7.8) * mm, "end": v(-5.07, 8.15) * mm});
            skLineSegment(sketch, "E1114", {"start": v(-5.07, 8.15) * mm, "end": v(-4.14, 8.68) * mm});
            skLineSegment(sketch, "E1115", {"start": v(-4.14, 8.68) * mm, "end": v(-3.83, 8.46) * mm});
            skArc(sketch, "E1116", {"start": v(-3.83, 8.46) * mm, "mid": v(-3.73, 8.39) * mm, "end": v(-3.63, 8.31) * mm});
            skArc(sketch, "E1117", {"start": v(-3.63, 8.31) * mm, "mid": v(-3.39, 8.12) * mm, "end": v(-3.14, 7.92) * mm});
            skArc(sketch, "E1118", {"start": v(-3.14, 7.92) * mm, "mid": v(-2.85, 7.68) * mm, "end": v(-2.56, 7.45) * mm});
            skArc(sketch, "E1119", {"start": v(-2.56, 7.45) * mm, "mid": v(-2.24, 7.2) * mm, "end": v(-1.93, 6.93) * mm});
            skLineSegment(sketch, "E1120", {"start": v(-1.93, 6.93) * mm, "end": v(-0.33, 5.63) * mm});
            skLineSegment(sketch, "E1121", {"start": v(-0.33, 5.63) * mm, "end": v(0.23, 6.4) * mm});
            skArc(sketch, "E1122", {"start": v(0.23, 6.4) * mm, "mid": v(0.36, 6.58) * mm, "end": v(0.49, 6.75) * mm});
            skArc(sketch, "E1123", {"start": v(0.49, 6.75) * mm, "mid": v(0.64, 6.95) * mm, "end": v(0.8, 7.14) * mm});
            skArc(sketch, "E1124", {"start": v(0.8, 7.14) * mm, "mid": v(0.95, 7.33) * mm, "end": v(1.1, 7.52) * mm});
            skArc(sketch, "E1125", {"start": v(1.1, 7.52) * mm, "mid": v(1.24, 7.66) * mm, "end": v(1.37, 7.8) * mm});
            skLineSegment(sketch, "E1126", {"start": v(1.37, 7.8) * mm, "end": v(1.94, 8.43) * mm});
            skLineSegment(sketch, "E1127", {"start": v(1.94, 8.43) * mm, "end": v(2.4, 8.16) * mm});
            skArc(sketch, "E1128", {"start": v(2.4, 8.16) * mm, "mid": v(2.79, 7.94) * mm, "end": v(3.18, 7.74) * mm});
            skArc(sketch, "E1129", {"start": v(3.18, 7.74) * mm, "mid": v(3.59, 7.54) * mm, "end": v(4, 7.35) * mm});
            skArc(sketch, "E1130", {"start": v(4, 7.35) * mm, "mid": v(4.39, 7.2) * mm, "end": v(4.78, 7.04) * mm});
            skArc(sketch, "E1131", {"start": v(4.78, 7.04) * mm, "mid": v(5.1, 6.93) * mm, "end": v(5.44, 6.84) * mm});
            skArc(sketch, "E1132", {"start": v(5.44, 6.84) * mm, "mid": v(5.7, 6.78) * mm, "end": v(5.94, 6.73) * mm});
            skArc(sketch, "E1133", {"start": v(5.94, 6.73) * mm, "mid": v(6.17, 6.7) * mm, "end": v(6.4, 6.67) * mm});
            skArc(sketch, "E1134", {"start": v(6.4, 6.67) * mm, "mid": v(6.68, 6.65) * mm, "end": v(6.95, 6.63) * mm});
            skArc(sketch, "E1135", {"start": v(6.95, 6.63) * mm, "mid": v(7.33, 6.63) * mm, "end": v(7.72, 6.62) * mm});
            skArc(sketch, "E1136", {"start": v(7.72, 6.62) * mm, "mid": v(8.15, 6.63) * mm, "end": v(8.58, 6.63) * mm});
            skArc(sketch, "E1137", {"start": v(8.58, 6.63) * mm, "mid": v(8.81, 6.64) * mm, "end": v(9.04, 6.66) * mm});
            skArc(sketch, "E1138", {"start": v(9.04, 6.66) * mm, "mid": v(9.24, 6.7) * mm, "end": v(9.43, 6.74) * mm});
            skArc(sketch, "E1139", {"start": v(9.43, 6.74) * mm, "mid": v(9.66, 6.8) * mm, "end": v(9.9, 6.89) * mm});
            skArc(sketch, "E1140", {"start": v(9.9, 6.89) * mm, "mid": v(10.43, 7.1) * mm, "end": v(10.94, 7.38) * mm});
            skArc(sketch, "E1141", {"start": v(10.94, 7.38) * mm, "mid": v(11.35, 7.67) * mm, "end": v(11.7, 8.02) * mm});
            skArc(sketch, "E1142", {"start": v(11.7, 8.02) * mm, "mid": v(11.98, 8.41) * mm, "end": v(12.2, 8.84) * mm});
            skArc(sketch, "E1143", {"start": v(12.2, 8.84) * mm, "mid": v(12.34, 9.33) * mm, "end": v(12.42, 9.84) * mm});
            skLineSegment(sketch, "E1144", {"start": v(12.42, 9.84) * mm, "end": v(12.48, 10.5) * mm});
            skLineSegment(sketch, "E1145", {"start": v(12.48, 10.5) * mm, "end": v(13, 10.7) * mm});
            skArc(sketch, "E1146", {"start": v(13, 10.7) * mm, "mid": v(13.53, 10.92) * mm, "end": v(14.03, 11.2) * mm});
            skArc(sketch, "E1147", {"start": v(14.03, 11.2) * mm, "mid": v(14.43, 11.49) * mm, "end": v(14.78, 11.84) * mm});
            skArc(sketch, "E1148", {"start": v(14.78, 11.84) * mm, "mid": v(15.04, 12.2) * mm, "end": v(15.23, 12.6) * mm});
            skArc(sketch, "E1149", {"start": v(15.23, 12.6) * mm, "mid": v(15.35, 13.03) * mm, "end": v(15.39, 13.48) * mm});
            skArc(sketch, "E1150", {"start": v(15.39, 13.48) * mm, "mid": v(15.37, 13.74) * mm, "end": v(15.32, 14) * mm});
            skArc(sketch, "E1151", {"start": v(15.32, 14) * mm, "mid": v(15.24, 14.25) * mm, "end": v(15.13, 14.5) * mm});
            skArc(sketch, "E1152", {"start": v(15.13, 14.5) * mm, "mid": v(14.98, 14.74) * mm, "end": v(14.8, 14.98) * mm});
            skArc(sketch, "E1153", {"start": v(14.8, 14.98) * mm, "mid": v(14.58, 15.23) * mm, "end": v(14.34, 15.46) * mm});
            skArc(sketch, "E1154", {"start": v(14.34, 15.46) * mm, "mid": v(14.14, 15.63) * mm, "end": v(13.93, 15.78) * mm});
            skArc(sketch, "E1155", {"start": v(13.93, 15.78) * mm, "mid": v(13.65, 15.95) * mm, "end": v(13.37, 16.12) * mm});
            skArc(sketch, "E1156", {"start": v(13.37, 16.12) * mm, "mid": v(13.1, 16.27) * mm, "end": v(12.82, 16.41) * mm});
            skArc(sketch, "E1157", {"start": v(12.82, 16.41) * mm, "mid": v(12.68, 16.46) * mm, "end": v(12.54, 16.48) * mm});
            skArc(sketch, "E1158", {"start": v(12.54, 16.48) * mm, "mid": v(12.52, 16.48) * mm, "end": v(12.5, 16.5) * mm});
            skArc(sketch, "E1159", {"start": v(12.5, 16.5) * mm, "mid": v(12.48, 16.52) * mm, "end": v(12.47, 16.55) * mm});
            skArc(sketch, "E1160", {"start": v(12.47, 16.55) * mm, "mid": v(12.45, 16.6) * mm, "end": v(12.44, 16.64) * mm});
            skArc(sketch, "E1161", {"start": v(12.44, 16.64) * mm, "mid": v(12.44, 16.69) * mm, "end": v(12.44, 16.74) * mm});
            skArc(sketch, "E1162", {"start": v(12.44, 16.74) * mm, "mid": v(12.42, 16.92) * mm, "end": v(12.37, 17.1) * mm});
            skArc(sketch, "E1163", {"start": v(12.37, 17.1) * mm, "mid": v(12.28, 17.32) * mm, "end": v(12.17, 17.54) * mm});
            skArc(sketch, "E1164", {"start": v(12.17, 17.54) * mm, "mid": v(12.04, 17.77) * mm, "end": v(11.89, 17.99) * mm});
            skArc(sketch, "E1165", {"start": v(11.89, 17.99) * mm, "mid": v(11.73, 18.17) * mm, "end": v(11.56, 18.34) * mm});
            skArc(sketch, "E1166", {"start": v(11.56, 18.34) * mm, "mid": v(11.2, 18.65) * mm, "end": v(10.8, 18.92) * mm});
            skArc(sketch, "E1167", {"start": v(10.8, 18.92) * mm, "mid": v(10.42, 19.13) * mm, "end": v(10.01, 19.3) * mm});
            skArc(sketch, "E1168", {"start": v(10.01, 19.3) * mm, "mid": v(9.56, 19.42) * mm, "end": v(9.09, 19.5) * mm});
            skArc(sketch, "E1169", {"start": v(9.09, 19.5) * mm, "mid": v(8.5, 19.54) * mm, "end": v(7.91, 19.55) * mm});
            skArc(sketch, "E1170", {"start": v(7.91, 19.55) * mm, "mid": v(7.27, 19.53) * mm, "end": v(6.63, 19.46) * mm});
            skArc(sketch, "E1171", {"start": v(6.63, 19.46) * mm, "mid": v(6.07, 19.36) * mm, "end": v(5.53, 19.2) * mm});
            skArc(sketch, "E1172", {"start": v(5.53, 19.2) * mm, "mid": v(4.97, 18.98) * mm, "end": v(4.43, 18.72) * mm});
            skArc(sketch, "E1173", {"start": v(4.43, 18.72) * mm, "mid": v(3.76, 18.34) * mm, "end": v(3.11, 17.93) * mm});
            skArc(sketch, "E1174", {"start": v(3.11, 17.93) * mm, "mid": v(2.94, 17.82) * mm, "end": v(2.76, 17.7) * mm});
            skArc(sketch, "E1175", {"start": v(2.76, 17.7) * mm, "mid": v(2.6, 17.6) * mm, "end": v(2.45, 17.5) * mm});
            skArc(sketch, "E1176", {"start": v(2.45, 17.5) * mm, "mid": v(2.32, 17.43) * mm, "end": v(2.18, 17.35) * mm});
            skArc(sketch, "E1177", {"start": v(2.18, 17.35) * mm, "mid": v(2.16, 17.34) * mm, "end": v(2.13, 17.33) * mm});
            skArc(sketch, "E1178", {"start": v(2.13, 17.33) * mm, "mid": v(2.1, 17.34) * mm, "end": v(2.08, 17.35) * mm});
            skArc(sketch, "E1179", {"start": v(2.08, 17.35) * mm, "mid": v(1.95, 17.51) * mm, "end": v(1.8, 17.67) * mm});
            skArc(sketch, "E1180", {"start": v(1.8, 17.67) * mm, "mid": v(1.65, 17.85) * mm, "end": v(1.5, 18.04) * mm});
            skArc(sketch, "E1181", {"start": v(1.5, 18.04) * mm, "mid": v(1.3, 18.26) * mm, "end": v(1.13, 18.48) * mm});
            skArc(sketch, "E1182", {"start": v(1.13, 18.48) * mm, "mid": v(0.95, 18.7) * mm, "end": v(0.77, 18.91) * mm});
            skArc(sketch, "E1183", {"start": v(0.77, 18.91) * mm, "mid": v(0.61, 19.1) * mm, "end": v(0.46, 19.28) * mm});
            skArc(sketch, "E1184", {"start": v(0.46, 19.28) * mm, "mid": v(0.32, 19.44) * mm, "end": v(0.18, 19.6) * mm});
            skArc(sketch, "E1185", {"start": v(0.18, 19.6) * mm, "mid": v(0.17, 19.62) * mm, "end": v(0.15, 19.62) * mm});
            skArc(sketch, "E1186", {"start": v(0.15, 19.62) * mm, "mid": v(0.13, 19.62) * mm, "end": v(0.11, 19.6) * mm});
            skArc(sketch, "E1187", {"start": v(0.11, 19.6) * mm, "mid": v(0.02, 19.5) * mm, "end": v(-0.06, 19.38) * mm});
            skArc(sketch, "E1188", {"start": v(-0.06, 19.38) * mm, "mid": v(-0.17, 19.26) * mm, "end": v(-0.27, 19.13) * mm});
            skArc(sketch, "E1189", {"start": v(-0.27, 19.13) * mm, "mid": v(-0.38, 18.97) * mm, "end": v(-0.5, 18.82) * mm});
            skArc(sketch, "E1190", {"start": v(9.27, 18.52) * mm, "mid": v(9.5, 18.46) * mm, "end": v(9.73, 18.4) * mm});
            skArc(sketch, "E1191", {"start": v(9.73, 18.4) * mm, "mid": v(9.96, 18.3) * mm, "end": v(10.18, 18.22) * mm});
            skArc(sketch, "E1192", {"start": v(10.18, 18.22) * mm, "mid": v(10.38, 18.12) * mm, "end": v(10.58, 18.01) * mm});
            skArc(sketch, "E1193", {"start": v(10.58, 18.01) * mm, "mid": v(10.75, 17.9) * mm, "end": v(10.91, 17.79) * mm});
            skArc(sketch, "E1194", {"start": v(10.91, 17.79) * mm, "mid": v(11, 17.7) * mm, "end": v(11.1, 17.61) * mm});
            skArc(sketch, "E1195", {"start": v(11.1, 17.61) * mm, "mid": v(11.21, 17.46) * mm, "end": v(11.33, 17.3) * mm});
            skArc(sketch, "E1196", {"start": v(11.33, 17.3) * mm, "mid": v(11.43, 17.15) * mm, "end": v(11.54, 17) * mm});
            skArc(sketch, "E1197", {"start": v(11.54, 17) * mm, "mid": v(11.57, 16.92) * mm, "end": v(11.58, 16.85) * mm});
            skArc(sketch, "E1198", {"start": v(11.58, 16.85) * mm, "mid": v(11.57, 16.83) * mm, "end": v(11.56, 16.83) * mm});
            skArc(sketch, "E1199", {"start": v(11.56, 16.83) * mm, "mid": v(11.42, 16.82) * mm, "end": v(11.29, 16.82) * mm});
            skArc(sketch, "E1200", {"start": v(11.29, 16.82) * mm, "mid": v(11.13, 16.82) * mm, "end": v(10.97, 16.82) * mm});
            skArc(sketch, "E1201", {"start": v(10.97, 16.82) * mm, "mid": v(10.78, 16.83) * mm, "end": v(10.59, 16.84) * mm});
            skArc(sketch, "E1202", {"start": v(10.59, 16.84) * mm, "mid": v(10.34, 16.85) * mm, "end": v(10.08, 16.85) * mm});
            skArc(sketch, "E1203", {"start": v(10.08, 16.85) * mm, "mid": v(9.87, 16.85) * mm, "end": v(9.66, 16.83) * mm});
            skArc(sketch, "E1204", {"start": v(9.66, 16.83) * mm, "mid": v(9.46, 16.82) * mm, "end": v(9.26, 16.8) * mm});
            skArc(sketch, "E1205", {"start": v(9.26, 16.8) * mm, "mid": v(9.06, 16.76) * mm, "end": v(8.86, 16.72) * mm});
            skArc(sketch, "E1206", {"start": v(8.86, 16.72) * mm, "mid": v(8.52, 16.63) * mm, "end": v(8.2, 16.53) * mm});
            skArc(sketch, "E1207", {"start": v(8.2, 16.53) * mm, "mid": v(7.74, 16.38) * mm, "end": v(7.29, 16.21) * mm});
            skArc(sketch, "E1208", {"start": v(7.29, 16.21) * mm, "mid": v(6.82, 16.03) * mm, "end": v(6.36, 15.84) * mm});
            skArc(sketch, "E1209", {"start": v(6.36, 15.84) * mm, "mid": v(5.98, 15.67) * mm, "end": v(5.61, 15.5) * mm});
            skLineSegment(sketch, "E1210", {"start": v(5.61, 15.5) * mm, "end": v(5.13, 15.25) * mm});
            skLineSegment(sketch, "E1211", {"start": v(5.13, 15.25) * mm, "end": v(4.57, 15.53) * mm});
            skArc(sketch, "E1212", {"start": v(4.57, 15.53) * mm, "mid": v(4.32, 15.67) * mm, "end": v(4.07, 15.8) * mm});
            skArc(sketch, "E1213", {"start": v(4.07, 15.8) * mm, "mid": v(3.77, 16) * mm, "end": v(3.47, 16.18) * mm});
            skArc(sketch, "E1214", {"start": v(3.47, 16.18) * mm, "mid": v(3.16, 16.38) * mm, "end": v(2.86, 16.58) * mm});
            skArc(sketch, "E1215", {"start": v(2.86, 16.58) * mm, "mid": v(2.83, 16.62) * mm, "end": v(2.82, 16.67) * mm});
            skArc(sketch, "E1216", {"start": v(2.82, 16.67) * mm, "mid": v(2.83, 16.72) * mm, "end": v(2.87, 16.75) * mm});
            skArc(sketch, "E1217", {"start": v(2.87, 16.75) * mm, "mid": v(3.3, 17) * mm, "end": v(3.73, 17.25) * mm});
            skArc(sketch, "E1218", {"start": v(3.73, 17.25) * mm, "mid": v(4.14, 17.49) * mm, "end": v(4.55, 17.72) * mm});
            skArc(sketch, "E1219", {"start": v(4.55, 17.72) * mm, "mid": v(4.88, 17.89) * mm, "end": v(5.2, 18.05) * mm});
            skArc(sketch, "E1220", {"start": v(5.2, 18.05) * mm, "mid": v(5.69, 18.25) * mm, "end": v(6.19, 18.41) * mm});
            skArc(sketch, "E1221", {"start": v(6.19, 18.41) * mm, "mid": v(6.7, 18.54) * mm, "end": v(7.24, 18.62) * mm});
            skArc(sketch, "E1222", {"start": v(7.24, 18.62) * mm, "mid": v(7.76, 18.66) * mm, "end": v(8.29, 18.66) * mm});
            skArc(sketch, "E1223", {"start": v(8.29, 18.66) * mm, "mid": v(8.78, 18.61) * mm, "end": v(9.27, 18.52) * mm});
            skArc(sketch, "E1224", {"start": v(0.91, 16.42) * mm, "mid": v(0.9, 16.41) * mm, "end": v(0.9, 16.4) * mm});
            skArc(sketch, "E1225", {"start": v(0.9, 16.4) * mm, "mid": v(0.82, 16.34) * mm, "end": v(0.74, 16.27) * mm});
            skArc(sketch, "E1226", {"start": v(0.74, 16.27) * mm, "mid": v(0.65, 16.2) * mm, "end": v(0.56, 16.13) * mm});
            skArc(sketch, "E1227", {"start": v(0.56, 16.13) * mm, "mid": v(0.45, 16.04) * mm, "end": v(0.34, 15.96) * mm});
            skLineSegment(sketch, "E1228", {"start": v(0.34, 15.96) * mm, "end": v(-0.22, 15.52) * mm});
            skLineSegment(sketch, "E1229", {"start": v(-0.22, 15.52) * mm, "end": v(-0.99, 15.93) * mm});
            skLineSegment(sketch, "E1230", {"start": v(-0.99, 15.93) * mm, "end": v(-1.75, 16.33) * mm});
            skLineSegment(sketch, "E1231", {"start": v(-1.75, 16.33) * mm, "end": v(-1.06, 16.96) * mm});
            skLineSegment(sketch, "E1232", {"start": v(-1.06, 16.96) * mm, "end": v(-0.37, 17.6) * mm});
            skLineSegment(sketch, "E1233", {"start": v(-0.37, 17.6) * mm, "end": v(0.27, 17.03) * mm});
            skArc(sketch, "E1234", {"start": v(0.27, 17.03) * mm, "mid": v(0.4, 16.92) * mm, "end": v(0.51, 16.8) * mm});
            skArc(sketch, "E1235", {"start": v(0.51, 16.8) * mm, "mid": v(0.62, 16.71) * mm, "end": v(0.72, 16.61) * mm});
            skArc(sketch, "E1236", {"start": v(0.72, 16.61) * mm, "mid": v(0.81, 16.53) * mm, "end": v(0.9, 16.45) * mm});
            skArc(sketch, "E1237", {"start": v(0.9, 16.45) * mm, "mid": v(0.9, 16.44) * mm, "end": v(0.91, 16.42) * mm});
            skArc(sketch, "E1238", {"start": v(-8.58, 17.38) * mm, "mid": v(-8.42, 17.35) * mm, "end": v(-8.26, 17.3) * mm});
            skArc(sketch, "E1239", {"start": v(-8.26, 17.3) * mm, "mid": v(-8.05, 17.25) * mm, "end": v(-7.84, 17.2) * mm});
            skArc(sketch, "E1240", {"start": v(-7.84, 17.2) * mm, "mid": v(-7.61, 17.13) * mm, "end": v(-7.4, 17.07) * mm});
            skArc(sketch, "E1241", {"start": v(-7.4, 17.07) * mm, "mid": v(-7.2, 17.01) * mm, "end": v(-7, 16.95) * mm});
            skArc(sketch, "E1242", {"start": v(-7, 16.95) * mm, "mid": v(-6.55, 16.8) * mm, "end": v(-6.1, 16.63) * mm});
            skArc(sketch, "E1243", {"start": v(-6.1, 16.63) * mm, "mid": v(-5.54, 16.42) * mm, "end": v(-4.98, 16.2) * mm});
            skArc(sketch, "E1244", {"start": v(-4.98, 16.2) * mm, "mid": v(-4.4, 15.96) * mm, "end": v(-3.81, 15.72) * mm});
            skArc(sketch, "E1245", {"start": v(-3.81, 15.72) * mm, "mid": v(-3.77, 15.68) * mm, "end": v(-3.76, 15.63) * mm});
            skArc(sketch, "E1246", {"start": v(-3.76, 15.63) * mm, "mid": v(-3.76, 15.61) * mm, "end": v(-3.78, 15.6) * mm});
            skArc(sketch, "E1247", {"start": v(-3.78, 15.6) * mm, "mid": v(-3.87, 15.53) * mm, "end": v(-3.97, 15.46) * mm});
            skArc(sketch, "E1248", {"start": v(-3.98, 15.46) * mm, "mid": v(-4.1, 15.38) * mm, "end": v(-4.22, 15.3) * mm});
            skArc(sketch, "E1249", {"start": v(-4.22, 15.3) * mm, "mid": v(-4.36, 15.2) * mm, "end": v(-4.5, 15.12) * mm});
            skLineSegment(sketch, "E1250", {"start": v(-4.5, 15.12) * mm, "end": v(-5.24, 14.68) * mm});
            skLineSegment(sketch, "E1251", {"start": v(-5.24, 14.68) * mm, "end": v(-5.9, 14.92) * mm});
            skArc(sketch, "E1252", {"start": v(-5.9, 14.92) * mm, "mid": v(-6.58, 15.14) * mm, "end": v(-7.26, 15.33) * mm});
            skArc(sketch, "E1253", {"start": v(-7.26, 15.33) * mm, "mid": v(-8, 15.49) * mm, "end": v(-8.74, 15.62) * mm});
            skArc(sketch, "E1254", {"start": v(-8.74, 15.62) * mm, "mid": v(-9.5, 15.71) * mm, "end": v(-10.25, 15.77) * mm});
            skArc(sketch, "E1255", {"start": v(-10.25, 15.77) * mm, "mid": v(-10.98, 15.8) * mm, "end": v(-11.72, 15.79) * mm});
            skLineSegment(sketch, "E1256", {"start": v(-11.72, 15.79) * mm, "end": v(-12.9, 15.73) * mm});
            skLineSegment(sketch, "E1257", {"start": v(-12.9, 15.73) * mm, "end": v(-12.75, 16.08) * mm});
            skArc(sketch, "E1258", {"start": v(-12.75, 16.08) * mm, "mid": v(-12.72, 16.15) * mm, "end": v(-12.68, 16.22) * mm});
            skArc(sketch, "E1259", {"start": v(-12.68, 16.22) * mm, "mid": v(-12.64, 16.3) * mm, "end": v(-12.6, 16.37) * mm});
            skArc(sketch, "E1260", {"start": v(-12.6, 16.37) * mm, "mid": v(-12.56, 16.44) * mm, "end": v(-12.52, 16.5) * mm});
            skArc(sketch, "E1261", {"start": v(-12.52, 16.5) * mm, "mid": v(-12.48, 16.56) * mm, "end": v(-12.44, 16.6) * mm});
            skArc(sketch, "E1262", {"start": v(-12.44, 16.6) * mm, "mid": v(-12.34, 16.7) * mm, "end": v(-12.23, 16.79) * mm});
            skArc(sketch, "E1263", {"start": v(-12.23, 16.79) * mm, "mid": v(-12.05, 16.9) * mm, "end": v(-11.87, 17.02) * mm});
            skArc(sketch, "E1264", {"start": v(-11.87, 17.02) * mm, "mid": v(-11.67, 17.13) * mm, "end": v(-11.47, 17.24) * mm});
            skArc(sketch, "E1265", {"start": v(-11.47, 17.24) * mm, "mid": v(-11.29, 17.32) * mm, "end": v(-11.1, 17.4) * mm});
            skArc(sketch, "E1266", {"start": v(-11.1, 17.4) * mm, "mid": v(-10.88, 17.45) * mm, "end": v(-10.66, 17.49) * mm});
            skArc(sketch, "E1267", {"start": v(-10.66, 17.49) * mm, "mid": v(-10.32, 17.5) * mm, "end": v(-9.98, 17.51) * mm});
            skArc(sketch, "E1268", {"start": v(-9.98, 17.51) * mm, "mid": v(-9.62, 17.5) * mm, "end": v(-9.25, 17.48) * mm});
            skArc(sketch, "E1269", {"start": v(-9.25, 17.48) * mm, "mid": v(-8.92, 17.44) * mm, "end": v(-8.58, 17.38) * mm});
            skArc(sketch, "E1270", {"start": v(2.3, 15.32) * mm, "mid": v(2.44, 15.22) * mm, "end": v(2.58, 15.12) * mm});
            skArc(sketch, "E1271", {"start": v(2.58, 15.12) * mm, "mid": v(2.71, 15.03) * mm, "end": v(2.85, 14.93) * mm});
            skArc(sketch, "E1272", {"start": v(2.85, 14.93) * mm, "mid": v(2.98, 14.85) * mm, "end": v(3.1, 14.77) * mm});
            skArc(sketch, "E1273", {"start": v(3.1, 14.77) * mm, "mid": v(3.18, 14.73) * mm, "end": v(3.26, 14.69) * mm});
            skArc(sketch, "E1274", {"start": v(3.26, 14.69) * mm, "mid": v(3.32, 14.66) * mm, "end": v(3.38, 14.62) * mm});
            skArc(sketch, "E1275", {"start": v(3.38, 14.62) * mm, "mid": v(3.44, 14.6) * mm, "end": v(3.49, 14.56) * mm});
            skArc(sketch, "E1276", {"start": v(3.49, 14.56) * mm, "mid": v(3.52, 14.53) * mm, "end": v(3.56, 14.5) * mm});
            skArc(sketch, "E1277", {"start": v(3.56, 14.5) * mm, "mid": v(3.57, 14.48) * mm, "end": v(3.58, 14.46) * mm});
            skArc(sketch, "E1278", {"start": v(3.58, 14.46) * mm, "mid": v(3.57, 14.43) * mm, "end": v(3.56, 14.42) * mm});
            skArc(sketch, "E1279", {"start": v(3.56, 14.42) * mm, "mid": v(3.5, 14.38) * mm, "end": v(3.46, 14.34) * mm});
            skArc(sketch, "E1280", {"start": v(3.46, 14.34) * mm, "mid": v(3.39, 14.3) * mm, "end": v(3.32, 14.26) * mm});
            skArc(sketch, "E1281", {"start": v(3.32, 14.26) * mm, "mid": v(3.24, 14.22) * mm, "end": v(3.16, 14.18) * mm});
            skLineSegment(sketch, "E1282", {"start": v(3.16, 14.18) * mm, "end": v(2.74, 13.97) * mm});
            skLineSegment(sketch, "E1283", {"start": v(2.74, 13.97) * mm, "end": v(1.68, 14.53) * mm});
            skArc(sketch, "E1284", {"start": v(1.68, 14.53) * mm, "mid": v(1.48, 14.64) * mm, "end": v(1.28, 14.75) * mm});
            skArc(sketch, "E1285", {"start": v(1.28, 14.75) * mm, "mid": v(1.1, 14.85) * mm, "end": v(0.94, 14.94) * mm});
            skArc(sketch, "E1286", {"start": v(0.94, 14.94) * mm, "mid": v(0.79, 15.03) * mm, "end": v(0.64, 15.11) * mm});
            skArc(sketch, "E1287", {"start": v(0.64, 15.11) * mm, "mid": v(0.63, 15.13) * mm, "end": v(0.63, 15.14) * mm});
            skArc(sketch, "E1288", {"start": v(0.63, 15.14) * mm, "mid": v(0.64, 15.18) * mm, "end": v(0.66, 15.21) * mm});
            skArc(sketch, "E1289", {"start": v(0.66, 15.21) * mm, "mid": v(0.87, 15.36) * mm, "end": v(1.08, 15.5) * mm});
            skArc(sketch, "E1290", {"start": v(1.08, 15.5) * mm, "mid": v(1.28, 15.64) * mm, "end": v(1.48, 15.78) * mm});
            skArc(sketch, "E1291", {"start": v(1.48, 15.78) * mm, "mid": v(1.54, 15.8) * mm, "end": v(1.6, 15.8) * mm});
            skArc(sketch, "E1292", {"start": v(1.6, 15.8) * mm, "mid": v(1.62, 15.8) * mm, "end": v(1.64, 15.8) * mm});
            skArc(sketch, "E1293", {"start": v(1.64, 15.8) * mm, "mid": v(1.74, 15.73) * mm, "end": v(1.83, 15.67) * mm});
            skArc(sketch, "E1294", {"start": v(1.83, 15.67) * mm, "mid": v(1.94, 15.59) * mm, "end": v(2.05, 15.5) * mm});
            skArc(sketch, "E1295", {"start": v(2.05, 15.5) * mm, "mid": v(2.18, 15.42) * mm, "end": v(2.3, 15.32) * mm});
            skArc(sketch, "E1296", {"start": v(11.44, 15.7) * mm, "mid": v(11.46, 15.65) * mm, "end": v(11.46, 15.6) * mm});
            skArc(sketch, "E1297", {"start": v(11.46, 15.6) * mm, "mid": v(11.41, 15.5) * mm, "end": v(11.36, 15.4) * mm});
            skArc(sketch, "E1298", {"start": v(11.36, 15.4) * mm, "mid": v(11.28, 15.28) * mm, "end": v(11.2, 15.17) * mm});
            skArc(sketch, "E1299", {"start": v(11.2, 15.17) * mm, "mid": v(11.1, 15.06) * mm, "end": v(10.98, 14.95) * mm});
            skArc(sketch, "E1300", {"start": v(10.98, 14.95) * mm, "mid": v(10.74, 14.75) * mm, "end": v(10.47, 14.6) * mm});
            skArc(sketch, "E1301", {"start": v(10.47, 14.6) * mm, "mid": v(10.15, 14.46) * mm, "end": v(9.81, 14.36) * mm});
            skArc(sketch, "E1302", {"start": v(9.81, 14.36) * mm, "mid": v(9.44, 14.29) * mm, "end": v(9.06, 14.25) * mm});
            skArc(sketch, "E1303", {"start": v(9.06, 14.25) * mm, "mid": v(8.67, 14.26) * mm, "end": v(8.28, 14.3) * mm});
            skArc(sketch, "E1304", {"start": v(8.28, 14.3) * mm, "mid": v(7.97, 14.34) * mm, "end": v(7.67, 14.4) * mm});
            skArc(sketch, "E1305", {"start": v(7.67, 14.4) * mm, "mid": v(7.32, 14.48) * mm, "end": v(6.98, 14.58) * mm});
            skArc(sketch, "E1306", {"start": v(6.98, 14.58) * mm, "mid": v(6.64, 14.67) * mm, "end": v(6.31, 14.77) * mm});
            skArc(sketch, "E1307", {"start": v(6.31, 14.77) * mm, "mid": v(6.26, 14.8) * mm, "end": v(6.24, 14.86) * mm});
            skArc(sketch, "E1308", {"start": v(6.24, 14.86) * mm, "mid": v(6.26, 14.92) * mm, "end": v(6.3, 14.96) * mm});
            skArc(sketch, "E1309", {"start": v(6.3, 14.96) * mm, "mid": v(6.65, 15.1) * mm, "end": v(6.99, 15.24) * mm});
            skArc(sketch, "E1310", {"start": v(6.99, 15.24) * mm, "mid": v(7.32, 15.37) * mm, "end": v(7.67, 15.5) * mm});
            skArc(sketch, "E1311", {"start": v(7.67, 15.5) * mm, "mid": v(7.94, 15.59) * mm, "end": v(8.22, 15.66) * mm});
            skArc(sketch, "E1312", {"start": v(8.22, 15.66) * mm, "mid": v(8.52, 15.72) * mm, "end": v(8.83, 15.75) * mm});
            skArc(sketch, "E1313", {"start": v(8.83, 15.75) * mm, "mid": v(9.4, 15.77) * mm, "end": v(10, 15.78) * mm});
            skArc(sketch, "E1314", {"start": v(10, 15.78) * mm, "mid": v(10.6, 15.79) * mm, "end": v(11.22, 15.78) * mm});
            skArc(sketch, "E1315", {"start": v(11.22, 15.78) * mm, "mid": v(11.34, 15.76) * mm, "end": v(11.44, 15.7) * mm});
            skArc(sketch, "E1316", {"start": v(13, 15.14) * mm, "mid": v(13.2, 14.97) * mm, "end": v(13.41, 14.79) * mm});
            skArc(sketch, "E1317", {"start": v(13.41, 14.79) * mm, "mid": v(13.57, 14.6) * mm, "end": v(13.71, 14.4) * mm});
            skArc(sketch, "E1318", {"start": v(13.71, 14.4) * mm, "mid": v(13.82, 14.21) * mm, "end": v(13.9, 14) * mm});
            skArc(sketch, "E1319", {"start": v(13.9, 14) * mm, "mid": v(13.94, 13.8) * mm, "end": v(13.96, 13.6) * mm});
            skArc(sketch, "E1320", {"start": v(13.96, 13.6) * mm, "mid": v(13.94, 13.3) * mm, "end": v(13.87, 13) * mm});
            skArc(sketch, "E1321", {"start": v(13.87, 13) * mm, "mid": v(13.76, 12.74) * mm, "end": v(13.6, 12.5) * mm});
            skArc(sketch, "E1322", {"start": v(13.6, 12.5) * mm, "mid": v(13.4, 12.27) * mm, "end": v(13.15, 12.07) * mm});
            skArc(sketch, "E1323", {"start": v(13.15, 12.07) * mm, "mid": v(12.83, 11.87) * mm, "end": v(12.5, 11.7) * mm});
            skLineSegment(sketch, "E1324", {"start": v(12.5, 11.7) * mm, "end": v(12.03, 11.5) * mm});
            skLineSegment(sketch, "E1325", {"start": v(12.03, 11.5) * mm, "end": v(11.6, 11.94) * mm});
            skArc(sketch, "E1326", {"start": v(11.6, 11.94) * mm, "mid": v(11.38, 12.13) * mm, "end": v(11.14, 12.3) * mm});
            skArc(sketch, "E1327", {"start": v(11.14, 12.3) * mm, "mid": v(10.9, 12.46) * mm, "end": v(10.66, 12.58) * mm});
            skArc(sketch, "E1328", {"start": v(10.66, 12.58) * mm, "mid": v(10.4, 12.68) * mm, "end": v(10.13, 12.75) * mm});
            skArc(sketch, "E1329", {"start": v(10.13, 12.75) * mm, "mid": v(9.83, 12.8) * mm, "end": v(9.52, 12.84) * mm});
            skArc(sketch, "E1330", {"start": v(9.52, 12.84) * mm, "mid": v(9.22, 12.84) * mm, "end": v(8.91, 12.83) * mm});
            skArc(sketch, "E1331", {"start": v(8.91, 12.83) * mm, "mid": v(8.55, 12.8) * mm, "end": v(8.18, 12.74) * mm});
            skArc(sketch, "E1332", {"start": v(8.18, 12.74) * mm, "mid": v(7.81, 12.67) * mm, "end": v(7.44, 12.59) * mm});
            skArc(sketch, "E1333", {"start": v(7.44, 12.59) * mm, "mid": v(7.12, 12.5) * mm, "end": v(6.8, 12.38) * mm});
            skLineSegment(sketch, "E1334", {"start": v(6.8, 12.38) * mm, "end": v(6.33, 12.2) * mm});
            skLineSegment(sketch, "E1335", {"start": v(6.33, 12.2) * mm, "end": v(5.05, 12.82) * mm});
            skArc(sketch, "E1336", {"start": v(5.05, 12.82) * mm, "mid": v(4.8, 12.94) * mm, "end": v(4.56, 13.06) * mm});
            skArc(sketch, "E1337", {"start": v(4.56, 13.06) * mm, "mid": v(4.35, 13.16) * mm, "end": v(4.15, 13.27) * mm});
            skArc(sketch, "E1338", {"start": v(4.15, 13.27) * mm, "mid": v(3.97, 13.37) * mm, "end": v(3.8, 13.46) * mm});
            skArc(sketch, "E1339", {"start": v(3.8, 13.46) * mm, "mid": v(3.77, 13.48) * mm, "end": v(3.77, 13.5) * mm});
            skArc(sketch, "E1340", {"start": v(3.77, 13.5) * mm, "mid": v(3.77, 13.52) * mm, "end": v(3.79, 13.54) * mm});
            skArc(sketch, "E1341", {"start": v(3.79, 13.54) * mm, "mid": v(3.84, 13.58) * mm, "end": v(3.89, 13.62) * mm});
            skArc(sketch, "E1342", {"start": v(3.89, 13.62) * mm, "mid": v(3.95, 13.67) * mm, "end": v(4.02, 13.7) * mm});
            skArc(sketch, "E1343", {"start": v(4.02, 13.7) * mm, "mid": v(4.1, 13.75) * mm, "end": v(4.18, 13.8) * mm});
            skLineSegment(sketch, "E1344", {"start": v(4.18, 13.8) * mm, "end": v(4.59, 14.02) * mm});
            skLineSegment(sketch, "E1345", {"start": v(4.59, 14.02) * mm, "end": v(5.3, 13.78) * mm});
            skArc(sketch, "E1346", {"start": v(5.3, 13.78) * mm, "mid": v(6.07, 13.55) * mm, "end": v(6.86, 13.38) * mm});
            skArc(sketch, "E1347", {"start": v(6.86, 13.38) * mm, "mid": v(7.64, 13.27) * mm, "end": v(8.42, 13.24) * mm});
            skArc(sketch, "E1348", {"start": v(8.42, 13.24) * mm, "mid": v(9.12, 13.27) * mm, "end": v(9.82, 13.37) * mm});
            skArc(sketch, "E1349", {"start": v(9.82, 13.37) * mm, "mid": v(10.37, 13.52) * mm, "end": v(10.89, 13.77) * mm});
            skArc(sketch, "E1350", {"start": v(10.89, 13.77) * mm, "mid": v(11.08, 13.9) * mm, "end": v(11.27, 14.03) * mm});
            skArc(sketch, "E1351", {"start": v(11.27, 14.03) * mm, "mid": v(11.45, 14.18) * mm, "end": v(11.61, 14.35) * mm});
            skArc(sketch, "E1352", {"start": v(11.61, 14.35) * mm, "mid": v(11.76, 14.52) * mm, "end": v(11.9, 14.7) * mm});
            skArc(sketch, "E1353", {"start": v(11.9, 14.7) * mm, "mid": v(12.01, 14.87) * mm, "end": v(12.1, 15.05) * mm});
            skArc(sketch, "E1354", {"start": v(12.1, 15.05) * mm, "mid": v(12.17, 15.19) * mm, "end": v(12.26, 15.32) * mm});
            skArc(sketch, "E1355", {"start": v(12.26, 15.32) * mm, "mid": v(12.33, 15.38) * mm, "end": v(12.43, 15.41) * mm});
            skArc(sketch, "E1356", {"start": v(12.43, 15.41) * mm, "mid": v(12.54, 15.4) * mm, "end": v(12.64, 15.37) * mm});
            skArc(sketch, "E1357", {"start": v(12.64, 15.37) * mm, "mid": v(12.82, 15.26) * mm, "end": v(13, 15.14) * mm});
            skArc(sketch, "E1358", {"start": v(-2.35, 14.95) * mm, "mid": v(-2.22, 14.87) * mm, "end": v(-2.09, 14.8) * mm});
            skArc(sketch, "E1359", {"start": v(-2.09, 14.8) * mm, "mid": v(-1.97, 14.73) * mm, "end": v(-1.86, 14.67) * mm});
            skArc(sketch, "E1360", {"start": v(-1.86, 14.67) * mm, "mid": v(-1.77, 14.6) * mm, "end": v(-1.67, 14.55) * mm});
            skArc(sketch, "E1361", {"start": v(-1.67, 14.55) * mm, "mid": v(-1.66, 14.54) * mm, "end": v(-1.66, 14.53) * mm});
            skArc(sketch, "E1362", {"start": v(-1.66, 14.53) * mm, "mid": v(-1.66, 14.52) * mm, "end": v(-1.67, 14.5) * mm});
            skArc(sketch, "E1363", {"start": v(-1.67, 14.5) * mm, "mid": v(-1.76, 14.43) * mm, "end": v(-1.85, 14.36) * mm});
            skArc(sketch, "E1364", {"start": v(-1.85, 14.36) * mm, "mid": v(-1.96, 14.28) * mm, "end": v(-2.06, 14.2) * mm});
            skArc(sketch, "E1365", {"start": v(-2.06, 14.2) * mm, "mid": v(-2.19, 14.1) * mm, "end": v(-2.3, 14.01) * mm});
            skLineSegment(sketch, "E1366", {"start": v(-2.3, 14.01) * mm, "end": v(-2.96, 13.53) * mm});
            skLineSegment(sketch, "E1367", {"start": v(-2.96, 13.53) * mm, "end": v(-3.79, 13.96) * mm});
            skLineSegment(sketch, "E1368", {"start": v(-3.79, 13.96) * mm, "end": v(-4.62, 14.4) * mm});
            skLineSegment(sketch, "E1369", {"start": v(-4.62, 14.4) * mm, "end": v(-3.93, 14.86) * mm});
            skArc(sketch, "E1370", {"start": v(-3.93, 14.86) * mm, "mid": v(-3.79, 14.95) * mm, "end": v(-3.65, 15.03) * mm});
            skArc(sketch, "E1371", {"start": v(-3.65, 15.03) * mm, "mid": v(-3.53, 15.1) * mm, "end": v(-3.4, 15.18) * mm});
            skArc(sketch, "E1372", {"start": v(-3.4, 15.18) * mm, "mid": v(-3.3, 15.25) * mm, "end": v(-3.2, 15.3) * mm});
            skArc(sketch, "E1373", {"start": v(-3.2, 15.3) * mm, "mid": v(-3.17, 15.32) * mm, "end": v(-3.14, 15.32) * mm});
            skArc(sketch, "E1374", {"start": v(-3.14, 15.32) * mm, "mid": v(-3.1, 15.32) * mm, "end": v(-3.07, 15.31) * mm});
            skArc(sketch, "E1375", {"start": v(-3.07, 15.31) * mm, "mid": v(-2.97, 15.27) * mm, "end": v(-2.87, 15.22) * mm});
            skArc(sketch, "E1376", {"start": v(-2.87, 15.22) * mm, "mid": v(-2.74, 15.16) * mm, "end": v(-2.62, 15.1) * mm});
            skArc(sketch, "E1377", {"start": v(-2.62, 15.1) * mm, "mid": v(-2.49, 15.02) * mm, "end": v(-2.35, 14.95) * mm});
            skArc(sketch, "E1378", {"start": v(-9.52, 14.34) * mm, "mid": v(-9.18, 14.28) * mm, "end": v(-8.84, 14.2) * mm});
            skArc(sketch, "E1379", {"start": v(-8.84, 14.2) * mm, "mid": v(-8.51, 14.13) * mm, "end": v(-8.2, 14.05) * mm});
            skArc(sketch, "E1380", {"start": v(-8.2, 14.05) * mm, "mid": v(-7.9, 13.97) * mm, "end": v(-7.62, 13.88) * mm});
            skArc(sketch, "E1381", {"start": v(-7.62, 13.88) * mm, "mid": v(-7.58, 13.85) * mm, "end": v(-7.57, 13.8) * mm});
            skArc(sketch, "E1382", {"start": v(-7.57, 13.8) * mm, "mid": v(-7.6, 13.74) * mm, "end": v(-7.66, 13.7) * mm});
            skArc(sketch, "E1383", {"start": v(-7.66, 13.7) * mm, "mid": v(-8.03, 13.65) * mm, "end": v(-8.4, 13.6) * mm});
            skArc(sketch, "E1384", {"start": v(-8.4, 13.6) * mm, "mid": v(-8.79, 13.57) * mm, "end": v(-9.18, 13.54) * mm});
            skArc(sketch, "E1385", {"start": v(-9.18, 13.54) * mm, "mid": v(-9.52, 13.54) * mm, "end": v(-9.87, 13.54) * mm});
            skArc(sketch, "E1386", {"start": v(-9.87, 13.54) * mm, "mid": v(-10.22, 13.57) * mm, "end": v(-10.56, 13.62) * mm});
            skArc(sketch, "E1387", {"start": v(-10.56, 13.62) * mm, "mid": v(-10.88, 13.68) * mm, "end": v(-11.2, 13.77) * mm});
            skArc(sketch, "E1388", {"start": v(-11.2, 13.77) * mm, "mid": v(-11.46, 13.86) * mm, "end": v(-11.72, 13.98) * mm});
            skArc(sketch, "E1389", {"start": v(-11.72, 13.98) * mm, "mid": v(-11.93, 14.1) * mm, "end": v(-12.12, 14.24) * mm});
            skLineSegment(sketch, "E1390", {"start": v(-12.12, 14.24) * mm, "end": v(-12.38, 14.47) * mm});
            skLineSegment(sketch, "E1391", {"start": v(-12.38, 14.47) * mm, "end": v(-11.33, 14.47) * mm});
            skArc(sketch, "E1392", {"start": v(-11.33, 14.47) * mm, "mid": v(-11.1, 14.47) * mm, "end": v(-10.87, 14.46) * mm});
            skArc(sketch, "E1393", {"start": v(-10.87, 14.46) * mm, "mid": v(-10.62, 14.45) * mm, "end": v(-10.36, 14.44) * mm});
            skArc(sketch, "E1394", {"start": v(-10.36, 14.44) * mm, "mid": v(-10.12, 14.42) * mm, "end": v(-9.89, 14.4) * mm});
            skArc(sketch, "E1395", {"start": v(-9.89, 14.4) * mm, "mid": v(-9.7, 14.37) * mm, "end": v(-9.52, 14.34) * mm});
            skArc(sketch, "E1396", {"start": v(-13.02, 13.77) * mm, "mid": v(-12.78, 13.55) * mm, "end": v(-12.53, 13.36) * mm});
            skArc(sketch, "E1397", {"start": v(-12.53, 13.36) * mm, "mid": v(-12.26, 13.21) * mm, "end": v(-11.98, 13.1) * mm});
            skArc(sketch, "E1398", {"start": v(-11.98, 13.1) * mm, "mid": v(-11.63, 13) * mm, "end": v(-11.27, 12.95) * mm});
            skArc(sketch, "E1399", {"start": v(-11.27, 12.95) * mm, "mid": v(-10.76, 12.9) * mm, "end": v(-10.25, 12.88) * mm});
            skArc(sketch, "E1400", {"start": v(-10.25, 12.88) * mm, "mid": v(-9.77, 12.87) * mm, "end": v(-9.29, 12.87) * mm});
            skArc(sketch, "E1401", {"start": v(-9.29, 12.87) * mm, "mid": v(-8.87, 12.9) * mm, "end": v(-8.45, 12.93) * mm});
            skArc(sketch, "E1402", {"start": v(-8.45, 12.93) * mm, "mid": v(-8.08, 12.98) * mm, "end": v(-7.71, 13.05) * mm});
            skArc(sketch, "E1403", {"start": v(-7.71, 13.05) * mm, "mid": v(-7.37, 13.14) * mm, "end": v(-7.03, 13.24) * mm});
            skLineSegment(sketch, "E1404", {"start": v(-7.03, 13.24) * mm, "end": v(-6.5, 13.42) * mm});
            skLineSegment(sketch, "E1405", {"start": v(-6.5, 13.42) * mm, "end": v(-5.68, 13) * mm});
            skArc(sketch, "E1406", {"start": v(-5.68, 13) * mm, "mid": v(-5.26, 12.79) * mm, "end": v(-4.85, 12.57) * mm});
            skArc(sketch, "E1407", {"start": v(-4.85, 12.57) * mm, "mid": v(-4.78, 12.52) * mm, "end": v(-4.73, 12.44) * mm});
            skArc(sketch, "E1408", {"start": v(-4.73, 12.44) * mm, "mid": v(-4.72, 12.37) * mm, "end": v(-4.76, 12.3) * mm});
            skArc(sketch, "E1409", {"start": v(-4.76, 12.3) * mm, "mid": v(-4.97, 12.15) * mm, "end": v(-5.2, 12) * mm});
            skLineSegment(sketch, "E1410", {"start": v(-5.2, 12) * mm, "end": v(-5.79, 11.59) * mm});
            skLineSegment(sketch, "E1411", {"start": v(-5.79, 11.59) * mm, "end": v(-6.8, 11.93) * mm});
            skArc(sketch, "E1412", {"start": v(-6.8, 11.93) * mm, "mid": v(-7.42, 12.13) * mm, "end": v(-8.05, 12.3) * mm});
            skArc(sketch, "E1413", {"start": v(-8.05, 12.3) * mm, "mid": v(-8.56, 12.4) * mm, "end": v(-9.08, 12.45) * mm});
            skArc(sketch, "E1414", {"start": v(-9.08, 12.45) * mm, "mid": v(-9.55, 12.45) * mm, "end": v(-10.03, 12.41) * mm});
            skArc(sketch, "E1415", {"start": v(-10.03, 12.41) * mm, "mid": v(-10.53, 12.32) * mm, "end": v(-11.01, 12.2) * mm});
            skArc(sketch, "E1416", {"start": v(-11.01, 12.2) * mm, "mid": v(-11.46, 12.02) * mm, "end": v(-11.9, 11.8) * mm});
            skArc(sketch, "E1417", {"start": v(-11.9, 11.8) * mm, "mid": v(-12.24, 11.53) * mm, "end": v(-12.55, 11.2) * mm});
            skArc(sketch, "E1418", {"start": v(-12.55, 11.2) * mm, "mid": v(-12.79, 10.85) * mm, "end": v(-12.96, 10.46) * mm});
            skArc(sketch, "E1419", {"start": v(-12.96, 10.46) * mm, "mid": v(-13.07, 10.02) * mm, "end": v(-13.12, 9.57) * mm});
            skArc(sketch, "E1420", {"start": v(-13.12, 9.57) * mm, "mid": v(-13.13, 9.34) * mm, "end": v(-13.16, 9.11) * mm});
            skArc(sketch, "E1421", {"start": v(-13.16, 9.11) * mm, "mid": v(-13.2, 9.02) * mm, "end": v(-13.28, 8.96) * mm});
            skArc(sketch, "E1422", {"start": v(-13.28, 8.96) * mm, "mid": v(-13.4, 8.94) * mm, "end": v(-13.51, 8.97) * mm});
            skArc(sketch, "E1423", {"start": v(-13.51, 8.97) * mm, "mid": v(-13.8, 9.1) * mm, "end": v(-14.1, 9.23) * mm});
            skArc(sketch, "E1424", {"start": v(-14.1, 9.23) * mm, "mid": v(-14.32, 9.34) * mm, "end": v(-14.53, 9.47) * mm});
            skArc(sketch, "E1425", {"start": v(-14.53, 9.47) * mm, "mid": v(-14.7, 9.6) * mm, "end": v(-14.87, 9.74) * mm});
            skArc(sketch, "E1426", {"start": v(-14.87, 9.74) * mm, "mid": v(-15.02, 9.9) * mm, "end": v(-15.15, 10.07) * mm});
            skArc(sketch, "E1427", {"start": v(-15.15, 10.07) * mm, "mid": v(-15.29, 10.29) * mm, "end": v(-15.42, 10.51) * mm});
            skArc(sketch, "E1428", {"start": v(-15.42, 10.51) * mm, "mid": v(-15.56, 10.85) * mm, "end": v(-15.65, 11.2) * mm});
            skArc(sketch, "E1429", {"start": v(-15.65, 11.2) * mm, "mid": v(-15.67, 11.55) * mm, "end": v(-15.63, 11.9) * mm});
            skArc(sketch, "E1430", {"start": v(-15.63, 11.9) * mm, "mid": v(-15.53, 12.27) * mm, "end": v(-15.38, 12.61) * mm});
            skArc(sketch, "E1431", {"start": v(-15.38, 12.61) * mm, "mid": v(-15.15, 12.97) * mm, "end": v(-14.88, 13.3) * mm});
            skArc(sketch, "E1432", {"start": v(-14.88, 13.3) * mm, "mid": v(-14.74, 13.44) * mm, "end": v(-14.58, 13.57) * mm});
            skArc(sketch, "E1433", {"start": v(-14.58, 13.57) * mm, "mid": v(-14.36, 13.73) * mm, "end": v(-14.14, 13.88) * mm});
            skArc(sketch, "E1434", {"start": v(-14.14, 13.88) * mm, "mid": v(-13.93, 14) * mm, "end": v(-13.7, 14.13) * mm});
            skArc(sketch, "E1435", {"start": v(-13.7, 14.13) * mm, "mid": v(-13.6, 14.17) * mm, "end": v(-13.47, 14.19) * mm});
            skArc(sketch, "E1436", {"start": v(-13.47, 14.19) * mm, "mid": v(-13.46, 14.18) * mm, "end": v(-13.44, 14.18) * mm});
            skArc(sketch, "E1437", {"start": v(-13.44, 14.18) * mm, "mid": v(-13.38, 14.12) * mm, "end": v(-13.32, 14.06) * mm});
            skArc(sketch, "E1438", {"start": v(-13.32, 14.06) * mm, "mid": v(-13.25, 14) * mm, "end": v(-13.18, 13.93) * mm});
            skArc(sketch, "E1439", {"start": v(-13.18, 13.93) * mm, "mid": v(-13.1, 13.85) * mm, "end": v(-13.02, 13.77) * mm});
            skArc(sketch, "E1440", {"start": v(0.15, 13.6) * mm, "mid": v(0.32, 13.5) * mm, "end": v(0.5, 13.4) * mm});
            skArc(sketch, "E1441", {"start": v(0.5, 13.4) * mm, "mid": v(0.64, 13.3) * mm, "end": v(0.78, 13.21) * mm});
            skArc(sketch, "E1442", {"start": v(0.78, 13.21) * mm, "mid": v(0.9, 13.13) * mm, "end": v(1.02, 13.05) * mm});
            skArc(sketch, "E1443", {"start": v(1.02, 13.05) * mm, "mid": v(1.04, 13.03) * mm, "end": v(1.04, 13) * mm});
            skArc(sketch, "E1444", {"start": v(1.04, 13) * mm, "mid": v(1.03, 12.97) * mm, "end": v(1.01, 12.95) * mm});
            skArc(sketch, "E1445", {"start": v(1.01, 12.95) * mm, "mid": v(0.92, 12.88) * mm, "end": v(0.82, 12.8) * mm});
            skArc(sketch, "E1446", {"start": v(0.82, 12.8) * mm, "mid": v(0.7, 12.72) * mm, "end": v(0.58, 12.63) * mm});
            skArc(sketch, "E1447", {"start": v(0.58, 12.63) * mm, "mid": v(0.44, 12.54) * mm, "end": v(0.3, 12.45) * mm});
            skLineSegment(sketch, "E1448", {"start": v(0.3, 12.45) * mm, "end": v(-0.43, 12) * mm});
            skLineSegment(sketch, "E1449", {"start": v(-0.43, 12) * mm, "end": v(-1.33, 12.54) * mm});
            skArc(sketch, "E1450", {"start": v(-1.33, 12.54) * mm, "mid": v(-1.5, 12.65) * mm, "end": v(-1.67, 12.76) * mm});
            skArc(sketch, "E1451", {"start": v(-1.67, 12.76) * mm, "mid": v(-1.82, 12.86) * mm, "end": v(-1.96, 12.95) * mm});
            skArc(sketch, "E1452", {"start": v(-1.96, 12.95) * mm, "mid": v(-2.08, 13.04) * mm, "end": v(-2.2, 13.12) * mm});
            skArc(sketch, "E1453", {"start": v(-2.2, 13.12) * mm, "mid": v(-2.2, 13.14) * mm, "end": v(-2.2, 13.16) * mm});
            skArc(sketch, "E1454", {"start": v(-2.2, 13.16) * mm, "mid": v(-2.18, 13.22) * mm, "end": v(-2.13, 13.27) * mm});
            skArc(sketch, "E1455", {"start": v(-2.13, 13.27) * mm, "mid": v(-1.84, 13.47) * mm, "end": v(-1.56, 13.66) * mm});
            skArc(sketch, "E1456", {"start": v(-1.56, 13.66) * mm, "mid": v(-1.27, 13.86) * mm, "end": v(-0.99, 14.05) * mm});
            skArc(sketch, "E1457", {"start": v(-0.99, 14.05) * mm, "mid": v(-0.92, 14.08) * mm, "end": v(-0.85, 14.1) * mm});
            skArc(sketch, "E1458", {"start": v(-0.85, 14.1) * mm, "mid": v(-0.82, 14.09) * mm, "end": v(-0.79, 14.08) * mm});
            skArc(sketch, "E1459", {"start": v(-0.79, 14.08) * mm, "mid": v(-0.65, 14.01) * mm, "end": v(-0.52, 13.95) * mm});
            skArc(sketch, "E1460", {"start": v(-0.52, 13.95) * mm, "mid": v(-0.36, 13.87) * mm, "end": v(-0.2, 13.78) * mm});
            skArc(sketch, "E1461", {"start": v(-0.2, 13.78) * mm, "mid": v(-0.03, 13.69) * mm, "end": v(0.15, 13.6) * mm});
            skLineSegment(sketch, "E1462", {"start": v(3.3, 11.9) * mm, "end": v(4.45, 11.32) * mm});
            skLineSegment(sketch, "E1463", {"start": v(4.45, 11.32) * mm, "end": v(3.75, 10.84) * mm});
            skArc(sketch, "E1464", {"start": v(3.75, 10.84) * mm, "mid": v(3.61, 10.74) * mm, "end": v(3.47, 10.65) * mm});
            skArc(sketch, "E1465", {"start": v(3.47, 10.65) * mm, "mid": v(3.34, 10.55) * mm, "end": v(3.2, 10.45) * mm});
            skArc(sketch, "E1466", {"start": v(3.2, 10.45) * mm, "mid": v(3.09, 10.37) * mm, "end": v(2.97, 10.28) * mm});
            skArc(sketch, "E1467", {"start": v(2.97, 10.28) * mm, "mid": v(2.91, 10.23) * mm, "end": v(2.86, 10.18) * mm});
            skArc(sketch, "E1468", {"start": v(2.86, 10.18) * mm, "mid": v(2.82, 10.15) * mm, "end": v(2.78, 10.11) * mm});
            skArc(sketch, "E1469", {"start": v(2.78, 10.11) * mm, "mid": v(2.74, 10.08) * mm, "end": v(2.7, 10.05) * mm});
            skArc(sketch, "E1470", {"start": v(2.7, 10.05) * mm, "mid": v(2.66, 10.03) * mm, "end": v(2.63, 10) * mm});
            skArc(sketch, "E1471", {"start": v(2.63, 10) * mm, "mid": v(2.61, 10) * mm, "end": v(2.6, 10) * mm});
            skArc(sketch, "E1472", {"start": v(2.6, 10) * mm, "mid": v(2.57, 10) * mm, "end": v(2.55, 10.01) * mm});
            skArc(sketch, "E1473", {"start": v(2.55, 10.01) * mm, "mid": v(2.38, 10.12) * mm, "end": v(2.22, 10.22) * mm});
            skArc(sketch, "E1474", {"start": v(2.22, 10.22) * mm, "mid": v(2.04, 10.34) * mm, "end": v(1.85, 10.46) * mm});
            skArc(sketch, "E1475", {"start": v(1.85, 10.46) * mm, "mid": v(1.64, 10.6) * mm, "end": v(1.43, 10.75) * mm});
            skLineSegment(sketch, "E1476", {"start": v(1.43, 10.75) * mm, "end": v(0.33, 11.5) * mm});
            skLineSegment(sketch, "E1477", {"start": v(0.33, 11.5) * mm, "end": v(1.12, 11.99) * mm});
            skArc(sketch, "E1478", {"start": v(1.12, 11.99) * mm, "mid": v(1.28, 12.08) * mm, "end": v(1.43, 12.17) * mm});
            skArc(sketch, "E1479", {"start": v(1.43, 12.17) * mm, "mid": v(1.57, 12.25) * mm, "end": v(1.71, 12.33) * mm});
            skArc(sketch, "E1480", {"start": v(1.71, 12.33) * mm, "mid": v(1.83, 12.4) * mm, "end": v(1.95, 12.45) * mm});
            skArc(sketch, "E1481", {"start": v(1.95, 12.45) * mm, "mid": v(2, 12.47) * mm, "end": v(2.03, 12.47) * mm});
            skArc(sketch, "E1482", {"start": v(2.03, 12.47) * mm, "mid": v(2.07, 12.47) * mm, "end": v(2.11, 12.46) * mm});
            skArc(sketch, "E1483", {"start": v(2.11, 12.46) * mm, "mid": v(2.28, 12.38) * mm, "end": v(2.45, 12.3) * mm});
            skArc(sketch, "E1484", {"start": v(2.45, 12.3) * mm, "mid": v(2.65, 12.21) * mm, "end": v(2.85, 12.12) * mm});
            skArc(sketch, "E1485", {"start": v(2.85, 12.12) * mm, "mid": v(3.08, 12) * mm, "end": v(3.3, 11.9) * mm});
            skArc(sketch, "E1486", {"start": v(10.3, 11.93) * mm, "mid": v(10.38, 11.88) * mm, "end": v(10.45, 11.84) * mm});
            skArc(sketch, "E1487", {"start": v(10.45, 11.84) * mm, "mid": v(10.54, 11.79) * mm, "end": v(10.62, 11.73) * mm});
            skArc(sketch, "E1488", {"start": v(10.62, 11.73) * mm, "mid": v(10.69, 11.68) * mm, "end": v(10.76, 11.63) * mm});
            skArc(sketch, "E1489", {"start": v(10.76, 11.63) * mm, "mid": v(10.8, 11.59) * mm, "end": v(10.85, 11.54) * mm});
            skArc(sketch, "E1490", {"start": v(10.85, 11.54) * mm, "mid": v(10.9, 11.48) * mm, "end": v(10.96, 11.41) * mm});
            skArc(sketch, "E1491", {"start": v(10.96, 11.41) * mm, "mid": v(10.96, 11.39) * mm, "end": v(10.96, 11.36) * mm});
            skArc(sketch, "E1492", {"start": v(10.96, 11.36) * mm, "mid": v(10.93, 11.34) * mm, "end": v(10.9, 11.33) * mm});
            skArc(sketch, "E1493", {"start": v(10.9, 11.33) * mm, "mid": v(10.78, 11.3) * mm, "end": v(10.67, 11.28) * mm});
            skArc(sketch, "E1494", {"start": v(10.67, 11.28) * mm, "mid": v(10.31, 11.24) * mm, "end": v(9.96, 11.25) * mm});
            skArc(sketch, "E1495", {"start": v(9.96, 11.25) * mm, "mid": v(9.34, 11.32) * mm, "end": v(8.72, 11.41) * mm});
            skArc(sketch, "E1496", {"start": v(8.72, 11.41) * mm, "mid": v(8.08, 11.52) * mm, "end": v(7.45, 11.64) * mm});
            skArc(sketch, "E1497", {"start": v(7.45, 11.64) * mm, "mid": v(7.34, 11.7) * mm, "end": v(7.3, 11.83) * mm});
            skArc(sketch, "E1498", {"start": v(7.3, 11.83) * mm, "mid": v(7.3, 11.85) * mm, "end": v(7.31, 11.86) * mm});
            skArc(sketch, "E1499", {"start": v(7.31, 11.86) * mm, "mid": v(7.35, 11.88) * mm, "end": v(7.4, 11.9) * mm});
            skArc(sketch, "E1500", {"start": v(7.4, 11.9) * mm, "mid": v(7.45, 11.93) * mm, "end": v(7.51, 11.95) * mm});
            skArc(sketch, "E1501", {"start": v(7.51, 11.95) * mm, "mid": v(7.58, 11.97) * mm, "end": v(7.65, 11.99) * mm});
            skArc(sketch, "E1502", {"start": v(7.65, 11.99) * mm, "mid": v(7.73, 12) * mm, "end": v(7.8, 12.03) * mm});
            skArc(sketch, "E1503", {"start": v(7.8, 12.03) * mm, "mid": v(7.88, 12.05) * mm, "end": v(7.96, 12.07) * mm});
            skArc(sketch, "E1504", {"start": v(7.96, 12.07) * mm, "mid": v(8.03, 12.09) * mm, "end": v(8.1, 12.1) * mm});
            skArc(sketch, "E1505", {"start": v(8.1, 12.1) * mm, "mid": v(8.15, 12.12) * mm, "end": v(8.2, 12.13) * mm});
            skArc(sketch, "E1506", {"start": v(8.2, 12.13) * mm, "mid": v(8.4, 12.17) * mm, "end": v(8.62, 12.18) * mm});
            skArc(sketch, "E1507", {"start": v(8.62, 12.18) * mm, "mid": v(8.94, 12.17) * mm, "end": v(9.27, 12.14) * mm});
            skArc(sketch, "E1508", {"start": v(9.27, 12.14) * mm, "mid": v(9.6, 12.1) * mm, "end": v(9.91, 12.05) * mm});
            skArc(sketch, "E1509", {"start": v(9.91, 12.05) * mm, "mid": v(10.11, 12) * mm, "end": v(10.3, 11.93) * mm});
            skArc(sketch, "E1510", {"start": v(-2.97, 11.52) * mm, "mid": v(-2.81, 11.42) * mm, "end": v(-2.65, 11.33) * mm});
            skArc(sketch, "E1511", {"start": v(-2.65, 11.33) * mm, "mid": v(-2.52, 11.24) * mm, "end": v(-2.38, 11.15) * mm});
            skArc(sketch, "E1512", {"start": v(-2.38, 11.16) * mm, "mid": v(-2.27, 11.08) * mm, "end": v(-2.16, 11) * mm});
            skArc(sketch, "E1513", {"start": v(-2.16, 11) * mm, "mid": v(-2.14, 10.99) * mm, "end": v(-2.14, 10.97) * mm});
            skArc(sketch, "E1514", {"start": v(-2.14, 10.97) * mm, "mid": v(-2.14, 10.95) * mm, "end": v(-2.16, 10.93) * mm});
            skArc(sketch, "E1515", {"start": v(-2.16, 10.93) * mm, "mid": v(-2.24, 10.87) * mm, "end": v(-2.32, 10.81) * mm});
            skArc(sketch, "E1516", {"start": v(-2.32, 10.81) * mm, "mid": v(-2.42, 10.74) * mm, "end": v(-2.53, 10.68) * mm});
            skArc(sketch, "E1517", {"start": v(-2.53, 10.68) * mm, "mid": v(-2.65, 10.6) * mm, "end": v(-2.77, 10.53) * mm});
            skArc(sketch, "E1518", {"start": v(-2.77, 10.53) * mm, "mid": v(-2.97, 10.41) * mm, "end": v(-3.17, 10.3) * mm});
            skArc(sketch, "E1519", {"start": v(-3.17, 10.3) * mm, "mid": v(-3.26, 10.26) * mm, "end": v(-3.34, 10.23) * mm});
            skArc(sketch, "E1520", {"start": v(-3.34, 10.23) * mm, "mid": v(-3.41, 10.22) * mm, "end": v(-3.48, 10.24) * mm});
            skArc(sketch, "E1521", {"start": v(-3.48, 10.24) * mm, "mid": v(-3.56, 10.27) * mm, "end": v(-3.65, 10.32) * mm});
            skArc(sketch, "E1522", {"start": v(-3.65, 10.32) * mm, "mid": v(-3.71, 10.36) * mm, "end": v(-3.78, 10.4) * mm});
            skArc(sketch, "E1523", {"start": v(-3.78, 10.4) * mm, "mid": v(-3.9, 10.47) * mm, "end": v(-4, 10.54) * mm});
            skArc(sketch, "E1524", {"start": v(-4, 10.54) * mm, "mid": v(-4.12, 10.61) * mm, "end": v(-4.25, 10.69) * mm});
            skArc(sketch, "E1525", {"start": v(-4.25, 10.69) * mm, "mid": v(-4.37, 10.76) * mm, "end": v(-4.5, 10.83) * mm});
            skArc(sketch, "E1526", {"start": v(-4.5, 10.83) * mm, "mid": v(-4.6, 10.9) * mm, "end": v(-4.72, 10.97) * mm});
            skArc(sketch, "E1527", {"start": v(-4.72, 10.97) * mm, "mid": v(-4.82, 11.04) * mm, "end": v(-4.91, 11.1) * mm});
            skArc(sketch, "E1528", {"start": v(-4.91, 11.1) * mm, "mid": v(-5, 11.15) * mm, "end": v(-5.07, 11.2) * mm});
            skArc(sketch, "E1529", {"start": v(-5.07, 11.2) * mm, "mid": v(-5.08, 11.22) * mm, "end": v(-5.09, 11.24) * mm});
            skArc(sketch, "E1530", {"start": v(-5.09, 11.24) * mm, "mid": v(-5.08, 11.28) * mm, "end": v(-5.05, 11.31) * mm});
            skArc(sketch, "E1531", {"start": v(-5.05, 11.31) * mm, "mid": v(-4.8, 11.48) * mm, "end": v(-4.54, 11.64) * mm});
            skArc(sketch, "E1532", {"start": v(-4.54, 11.64) * mm, "mid": v(-4.29, 11.8) * mm, "end": v(-4.03, 11.96) * mm});
            skArc(sketch, "E1533", {"start": v(-4.03, 11.96) * mm, "mid": v(-3.97, 11.99) * mm, "end": v(-3.9, 12) * mm});
            skArc(sketch, "E1534", {"start": v(-3.9, 12) * mm, "mid": v(-3.87, 12) * mm, "end": v(-3.83, 11.98) * mm});
            skArc(sketch, "E1535", {"start": v(-3.83, 11.98) * mm, "mid": v(-3.71, 11.92) * mm, "end": v(-3.59, 11.86) * mm});
            skArc(sketch, "E1536", {"start": v(-3.59, 11.86) * mm, "mid": v(-3.44, 11.78) * mm, "end": v(-3.3, 11.7) * mm});
            skArc(sketch, "E1537", {"start": v(-3.3, 11.7) * mm, "mid": v(-3.13, 11.6) * mm, "end": v(-2.97, 11.52) * mm});
            skArc(sketch, "E1538", {"start": v(-8.01, 10.97) * mm, "mid": v(-7.87, 10.93) * mm, "end": v(-7.73, 10.88) * mm});
            skArc(sketch, "E1539", {"start": v(-7.73, 10.88) * mm, "mid": v(-7.62, 10.83) * mm, "end": v(-7.51, 10.78) * mm});
            skArc(sketch, "E1540", {"start": v(-7.51, 10.78) * mm, "mid": v(-7.43, 10.74) * mm, "end": v(-7.35, 10.7) * mm});
            skArc(sketch, "E1541", {"start": v(-7.35, 10.7) * mm, "mid": v(-7.34, 10.68) * mm, "end": v(-7.35, 10.66) * mm});
            skArc(sketch, "E1542", {"start": v(-7.35, 10.66) * mm, "mid": v(-7.45, 10.57) * mm, "end": v(-7.56, 10.5) * mm});
            skArc(sketch, "E1543", {"start": v(-7.56, 10.5) * mm, "mid": v(-7.85, 10.34) * mm, "end": v(-8.13, 10.19) * mm});
            skArc(sketch, "E1544", {"start": v(-8.13, 10.19) * mm, "mid": v(-8.45, 10.03) * mm, "end": v(-8.78, 9.87) * mm});
            skArc(sketch, "E1545", {"start": v(-8.78, 9.87) * mm, "mid": v(-9.08, 9.73) * mm, "end": v(-9.38, 9.6) * mm});
            skArc(sketch, "E1546", {"start": v(-9.38, 9.6) * mm, "mid": v(-9.71, 9.46) * mm, "end": v(-10.05, 9.33) * mm});
            skArc(sketch, "E1547", {"start": v(-10.05, 9.33) * mm, "mid": v(-10.45, 9.2) * mm, "end": v(-10.85, 9.1) * mm});
            skArc(sketch, "E1548", {"start": v(-10.85, 9.1) * mm, "mid": v(-11.23, 9) * mm, "end": v(-11.6, 8.9) * mm});
            skArc(sketch, "E1549", {"start": v(-11.6, 8.9) * mm, "mid": v(-11.83, 8.87) * mm, "end": v(-12.07, 8.86) * mm});
            skArc(sketch, "E1550", {"start": v(-12.07, 8.86) * mm, "mid": v(-12.14, 8.86) * mm, "end": v(-12.21, 8.87) * mm});
            skArc(sketch, "E1551", {"start": v(-12.21, 8.87) * mm, "mid": v(-12.25, 8.88) * mm, "end": v(-12.28, 8.9) * mm});
            skArc(sketch, "E1552", {"start": v(-12.28, 8.9) * mm, "mid": v(-12.3, 8.94) * mm, "end": v(-12.32, 8.98) * mm});
            skArc(sketch, "E1553", {"start": v(-12.32, 8.98) * mm, "mid": v(-12.33, 9.06) * mm, "end": v(-12.33, 9.14) * mm});
            skArc(sketch, "E1554", {"start": v(-12.33, 9.14) * mm, "mid": v(-12.32, 9.3) * mm, "end": v(-12.29, 9.47) * mm});
            skArc(sketch, "E1555", {"start": v(-12.29, 9.47) * mm, "mid": v(-12.23, 9.64) * mm, "end": v(-12.16, 9.82) * mm});
            skArc(sketch, "E1556", {"start": v(-12.16, 9.82) * mm, "mid": v(-12.07, 10) * mm, "end": v(-11.97, 10.16) * mm});
            skArc(sketch, "E1557", {"start": v(-11.97, 10.16) * mm, "mid": v(-11.86, 10.31) * mm, "end": v(-11.73, 10.46) * mm});
            skArc(sketch, "E1558", {"start": v(-11.73, 10.46) * mm, "mid": v(-11.4, 10.75) * mm, "end": v(-11.02, 10.98) * mm});
            skArc(sketch, "E1559", {"start": v(-11.02, 10.98) * mm, "mid": v(-10.6, 11.14) * mm, "end": v(-10.17, 11.24) * mm});
            skArc(sketch, "E1560", {"start": v(-10.17, 11.24) * mm, "mid": v(-9.66, 11.28) * mm, "end": v(-9.16, 11.24) * mm});
            skArc(sketch, "E1561", {"start": v(-9.16, 11.24) * mm, "mid": v(-8.58, 11.13) * mm, "end": v(-8.01, 10.97) * mm});
            skArc(sketch, "E1562", {"start": v(6.01, 10.67) * mm, "mid": v(6.5, 10.5) * mm, "end": v(7, 10.36) * mm});
            skArc(sketch, "E1563", {"start": v(7, 10.36) * mm, "mid": v(7.42, 10.26) * mm, "end": v(7.84, 10.19) * mm});
            skArc(sketch, "E1564", {"start": v(7.84, 10.19) * mm, "mid": v(8.29, 10.14) * mm, "end": v(8.74, 10.11) * mm});
            skArc(sketch, "E1565", {"start": v(8.74, 10.11) * mm, "mid": v(9.31, 10.1) * mm, "end": v(9.89, 10.12) * mm});
            skArc(sketch, "E1566", {"start": v(9.89, 10.12) * mm, "mid": v(10.25, 10.13) * mm, "end": v(10.62, 10.13) * mm});
            skArc(sketch, "E1567", {"start": v(10.62, 10.13) * mm, "mid": v(10.84, 10.14) * mm, "end": v(11.06, 10.13) * mm});
            skArc(sketch, "E1568", {"start": v(11.06, 10.13) * mm, "mid": v(11.2, 10.12) * mm, "end": v(11.34, 10.1) * mm});
            skArc(sketch, "E1569", {"start": v(11.34, 10.1) * mm, "mid": v(11.37, 10.09) * mm, "end": v(11.39, 10.05) * mm});
            skArc(sketch, "E1570", {"start": v(11.39, 10.05) * mm, "mid": v(11.39, 10.02) * mm, "end": v(11.38, 9.98) * mm});
            skArc(sketch, "E1571", {"start": v(11.38, 9.98) * mm, "mid": v(11.36, 9.9) * mm, "end": v(11.35, 9.83) * mm});
            skArc(sketch, "E1572", {"start": v(11.35, 9.83) * mm, "mid": v(11.33, 9.74) * mm, "end": v(11.3, 9.66) * mm});
            skArc(sketch, "E1573", {"start": v(11.3, 9.66) * mm, "mid": v(11.28, 9.56) * mm, "end": v(11.25, 9.47) * mm});
            skArc(sketch, "E1574", {"start": v(11.25, 9.47) * mm, "mid": v(11.14, 9.2) * mm, "end": v(10.99, 8.94) * mm});
            skArc(sketch, "E1575", {"start": v(10.99, 8.94) * mm, "mid": v(10.78, 8.7) * mm, "end": v(10.54, 8.49) * mm});
            skArc(sketch, "E1576", {"start": v(10.54, 8.49) * mm, "mid": v(10.24, 8.28) * mm, "end": v(9.92, 8.12) * mm});
            skArc(sketch, "E1577", {"start": v(9.92, 8.12) * mm, "mid": v(9.54, 7.96) * mm, "end": v(9.15, 7.84) * mm});
            skArc(sketch, "E1578", {"start": v(9.15, 7.84) * mm, "mid": v(8.56, 7.73) * mm, "end": v(7.96, 7.72) * mm});
            skArc(sketch, "E1579", {"start": v(7.96, 7.72) * mm, "mid": v(7.24, 7.8) * mm, "end": v(6.54, 7.95) * mm});
            skArc(sketch, "E1580", {"start": v(6.54, 7.95) * mm, "mid": v(5.8, 8.18) * mm, "end": v(5.07, 8.47) * mm});
            skArc(sketch, "E1581", {"start": v(5.07, 8.47) * mm, "mid": v(4.36, 8.84) * mm, "end": v(3.69, 9.26) * mm});
            skLineSegment(sketch, "E1582", {"start": v(3.69, 9.26) * mm, "end": v(3.27, 9.55) * mm});
            skLineSegment(sketch, "E1583", {"start": v(3.27, 9.55) * mm, "end": v(3.5, 9.77) * mm});
            skArc(sketch, "E1584", {"start": v(3.5, 9.77) * mm, "mid": v(3.61, 9.87) * mm, "end": v(3.73, 9.97) * mm});
            skArc(sketch, "E1585", {"start": v(3.73, 9.97) * mm, "mid": v(4.05, 10.2) * mm, "end": v(4.37, 10.42) * mm});
            skArc(sketch, "E1586", {"start": v(4.37, 10.42) * mm, "mid": v(4.71, 10.66) * mm, "end": v(5.06, 10.9) * mm});
            skArc(sketch, "E1587", {"start": v(5.06, 10.9) * mm, "mid": v(5.12, 10.93) * mm, "end": v(5.18, 10.95) * mm});
            skArc(sketch, "E1588", {"start": v(5.18, 10.95) * mm, "mid": v(5.2, 10.95) * mm, "end": v(5.2, 10.94) * mm});
            skArc(sketch, "E1589", {"start": v(5.2, 10.94) * mm, "mid": v(5.32, 10.9) * mm, "end": v(5.44, 10.87) * mm});
            skArc(sketch, "E1590", {"start": v(5.44, 10.87) * mm, "mid": v(5.57, 10.82) * mm, "end": v(5.7, 10.78) * mm});
            skArc(sketch, "E1591", {"start": v(5.7, 10.78) * mm, "mid": v(5.86, 10.72) * mm, "end": v(6.01, 10.67) * mm});
            skArc(sketch, "E1592", {"start": v(0.05, 9.66) * mm, "mid": v(0.27, 9.52) * mm, "end": v(0.5, 9.38) * mm});
            skArc(sketch, "E1593", {"start": v(0.5, 9.38) * mm, "mid": v(0.68, 9.25) * mm, "end": v(0.86, 9.13) * mm});
            skArc(sketch, "E1594", {"start": v(0.86, 9.13) * mm, "mid": v(1.02, 9.02) * mm, "end": v(1.17, 8.9) * mm});
            skArc(sketch, "E1595", {"start": v(1.17, 8.9) * mm, "mid": v(1.2, 8.89) * mm, "end": v(1.2, 8.86) * mm});
            skArc(sketch, "E1596", {"start": v(1.2, 8.86) * mm, "mid": v(1.19, 8.82) * mm, "end": v(1.16, 8.78) * mm});
            skArc(sketch, "E1597", {"start": v(1.16, 8.78) * mm, "mid": v(0.86, 8.51) * mm, "end": v(0.55, 8.25) * mm});
            skArc(sketch, "E1598", {"start": v(0.55, 8.25) * mm, "mid": v(0.26, 8) * mm, "end": v(-0.04, 7.75) * mm});
            skArc(sketch, "E1599", {"start": v(-0.04, 7.75) * mm, "mid": v(-0.1, 7.7) * mm, "end": v(-0.17, 7.68) * mm});
            skArc(sketch, "E1600", {"start": v(-0.17, 7.68) * mm, "mid": v(-0.23, 7.68) * mm, "end": v(-0.27, 7.7) * mm});
            skArc(sketch, "E1601", {"start": v(-0.27, 7.7) * mm, "mid": v(-0.85, 8.15) * mm, "end": v(-1.42, 8.6) * mm});
            skArc(sketch, "E1602", {"start": v(-1.42, 8.6) * mm, "mid": v(-2, 9.06) * mm, "end": v(-2.57, 9.51) * mm});
            skArc(sketch, "E1603", {"start": v(-2.57, 9.51) * mm, "mid": v(-2.6, 9.55) * mm, "end": v(-2.61, 9.6) * mm});
            skArc(sketch, "E1604", {"start": v(-2.61, 9.6) * mm, "mid": v(-2.6, 9.67) * mm, "end": v(-2.55, 9.72) * mm});
            skArc(sketch, "E1605", {"start": v(-2.55, 9.72) * mm, "mid": v(-2.25, 9.9) * mm, "end": v(-1.96, 10.08) * mm});
            skArc(sketch, "E1606", {"start": v(-1.96, 10.08) * mm, "mid": v(-1.66, 10.25) * mm, "end": v(-1.36, 10.42) * mm});
            skArc(sketch, "E1607", {"start": v(-1.36, 10.42) * mm, "mid": v(-1.29, 10.44) * mm, "end": v(-1.2, 10.43) * mm});
            skArc(sketch, "E1608", {"start": v(-1.2, 10.43) * mm, "mid": v(-1.17, 10.41) * mm, "end": v(-1.13, 10.4) * mm});
            skArc(sketch, "E1609", {"start": v(-1.13, 10.4) * mm, "mid": v(-0.96, 10.29) * mm, "end": v(-0.79, 10.19) * mm});
            skArc(sketch, "E1610", {"start": v(-0.79, 10.19) * mm, "mid": v(-0.6, 10.06) * mm, "end": v(-0.4, 9.94) * mm});
            skArc(sketch, "E1611", {"start": v(-0.4, 9.94) * mm, "mid": v(-0.17, 9.8) * mm, "end": v(0.05, 9.66) * mm});
            skArc(sketch, "E1612", {"start": v(-5.7, 9.78) * mm, "mid": v(-5.54, 9.69) * mm, "end": v(-5.4, 9.59) * mm});
            skArc(sketch, "E1613", {"start": v(-5.4, 9.59) * mm, "mid": v(-5.26, 9.5) * mm, "end": v(-5.13, 9.42) * mm});
            skArc(sketch, "E1614", {"start": v(-5.13, 9.42) * mm, "mid": v(-5.03, 9.34) * mm, "end": v(-4.92, 9.26) * mm});
            skArc(sketch, "E1615", {"start": v(-4.92, 9.26) * mm, "mid": v(-4.9, 9.25) * mm, "end": v(-4.9, 9.23) * mm});
            skArc(sketch, "E1616", {"start": v(-4.9, 9.23) * mm, "mid": v(-4.92, 9.15) * mm, "end": v(-4.98, 9.1) * mm});
            skArc(sketch, "E1617", {"start": v(-4.98, 9.1) * mm, "mid": v(-5.6, 8.82) * mm, "end": v(-6.24, 8.54) * mm});
            skArc(sketch, "E1618", {"start": v(-6.24, 8.54) * mm, "mid": v(-6.82, 8.28) * mm, "end": v(-7.4, 8.04) * mm});
            skArc(sketch, "E1619", {"start": v(-7.4, 8.04) * mm, "mid": v(-7.74, 7.9) * mm, "end": v(-8.1, 7.8) * mm});
            skArc(sketch, "E1620", {"start": v(-8.1, 7.8) * mm, "mid": v(-8.63, 7.68) * mm, "end": v(-9.17, 7.6) * mm});
            skArc(sketch, "E1621", {"start": v(-9.17, 7.6) * mm, "mid": v(-9.67, 7.55) * mm, "end": v(-10.16, 7.55) * mm});
            skArc(sketch, "E1622", {"start": v(-10.16, 7.55) * mm, "mid": v(-10.6, 7.58) * mm, "end": v(-11.01, 7.66) * mm});
            skArc(sketch, "E1623", {"start": v(-11.01, 7.66) * mm, "mid": v(-11.35, 7.76) * mm, "end": v(-11.66, 7.92) * mm});
            skLineSegment(sketch, "E1624", {"start": v(-11.66, 7.92) * mm, "end": v(-12, 8.13) * mm});
            skLineSegment(sketch, "E1625", {"start": v(-12, 8.13) * mm, "end": v(-11.19, 8.3) * mm});
            skArc(sketch, "E1626", {"start": v(-11.19, 8.3) * mm, "mid": v(-11.01, 8.33) * mm, "end": v(-10.84, 8.37) * mm});
            skArc(sketch, "E1627", {"start": v(-10.84, 8.37) * mm, "mid": v(-10.66, 8.41) * mm, "end": v(-10.47, 8.46) * mm});
            skArc(sketch, "E1628", {"start": v(-10.47, 8.46) * mm, "mid": v(-10.3, 8.5) * mm, "end": v(-10.14, 8.55) * mm});
            skArc(sketch, "E1629", {"start": v(-10.14, 8.55) * mm, "mid": v(-10.02, 8.58) * mm, "end": v(-9.9, 8.62) * mm});
            skArc(sketch, "E1630", {"start": v(-9.9, 8.62) * mm, "mid": v(-9.63, 8.72) * mm, "end": v(-9.36, 8.83) * mm});
            skArc(sketch, "E1631", {"start": v(-9.36, 8.83) * mm, "mid": v(-8.95, 9.03) * mm, "end": v(-8.55, 9.22) * mm});
            skArc(sketch, "E1632", {"start": v(-8.55, 9.22) * mm, "mid": v(-8.13, 9.43) * mm, "end": v(-7.72, 9.64) * mm});
            skArc(sketch, "E1633", {"start": v(-7.72, 9.64) * mm, "mid": v(-7.43, 9.8) * mm, "end": v(-7.13, 9.99) * mm});
            skArc(sketch, "E1634", {"start": v(-7.13, 9.99) * mm, "mid": v(-7.04, 10.04) * mm, "end": v(-6.95, 10.1) * mm});
            skArc(sketch, "E1635", {"start": v(-6.95, 10.1) * mm, "mid": v(-6.86, 10.15) * mm, "end": v(-6.78, 10.2) * mm});
            skArc(sketch, "E1636", {"start": v(-6.78, 10.2) * mm, "mid": v(-6.7, 10.23) * mm, "end": v(-6.63, 10.27) * mm});
            skArc(sketch, "E1637", {"start": v(-6.63, 10.27) * mm, "mid": v(-6.6, 10.28) * mm, "end": v(-6.58, 10.28) * mm});
            skArc(sketch, "E1638", {"start": v(-6.58, 10.28) * mm, "mid": v(-6.55, 10.28) * mm, "end": v(-6.52, 10.27) * mm});
            skArc(sketch, "E1639", {"start": v(-6.52, 10.27) * mm, "mid": v(-6.4, 10.2) * mm, "end": v(-6.28, 10.14) * mm});
            skArc(sketch, "E1640", {"start": v(-6.28, 10.14) * mm, "mid": v(-6.15, 10.06) * mm, "end": v(-6, 9.98) * mm});
            skArc(sketch, "E1641", {"start": v(-6, 9.98) * mm, "mid": v(-5.85, 9.88) * mm, "end": v(-5.7, 9.78) * mm});
            skLineSegment(sketch, "E1642", {"start": v(0, 44.45) * mm, "end": v(0, -44.45) * mm, "construction": true});
            skSolve(sketch);
        }
        {
            var Q0;
            Q0=qSketchRegion(id+"F8",true);
            extrude(context, id + "F9", {"entities" : qUnion([Q0]), "operationType" : NewBodyOperationType.ADD, "depth" : 1.59 * mm, "offsetDistance" : 25.4 * mm});
        }
        {
            var Q0;
            {var subQ350=makeQuery(id+"F3.opExtrude","SWEPT_FACE",FACE,{"disambiguationData":[OSD([sQuery(id+"F2.wireOp",EDGE,"E5.bottom")])]});Q0=makeQuery(id+"F9.boolean.opBoolean","SPLIT",FACE,{"disambiguationData":[TD([subQ350])],"derivedFrom":makeQuery(id+"F7.boolean.opBoolean","SPLIT",FACE,{"disambiguationData":[TD([subQ350])],"derivedFrom":makeQuery(id+"F5.boolean.opBoolean","SPLIT",FACE,{"disambiguationData":[TD([subQ350])],"derivedFrom":makeQuery(id+"F1.opExtrude","CAP_FACE",FACE,{"disambiguationData":[OSD([sQuery(id+"F0.wireOp",EDGE,"E0.bottom"),sQuery(id+"F0.wireOp",EDGE,"E0.top"),sQuery(id+"F0.wireOp",EDGE,"E0.left"),sQuery(id+"F0.wireOp",EDGE,"E0.right"),sQuery(id+"F0.wireOp",EDGE,"E1.filletArc"),sQuery(id+"F0.wireOp",EDGE,"E2.filletArc"),sQuery(id+"F0.wireOp",EDGE,"E3.filletArc"),sQuery(id+"F0.wireOp",EDGE,"E4.filletArc")])],"isStart":false})})})});}
            var sketch = newSketch(context, id + "F10", { "sketchPlane" : qUnion([Q0])});
            skText(sketch, "E1643", { "text": "little free library", "fontName": "RobotoSlab-Regular.ttf"});
            const initialGuessF10  = {"E1643": [-0.06668, -0.006, 1, 0, 0.01234]};
            skSetInitialGuess(sketch, initialGuessF10);
            skSolve(sketch);
        }
        {
            var Q0;
            Q0=qSketchRegion(id+"F10",true);
            extrude(context, id + "F11", {"entities" : qUnion([Q0]), "operationType" : NewBodyOperationType.ADD, "depth" : 1.59 * mm, "offsetDistance" : 25.4 * mm});
        }
        {
            var Q0;
            {var subQ400=makeQuery(id+"F3.opExtrude","SWEPT_FACE",FACE,{"disambiguationData":[OSD([sQuery(id+"F2.wireOp",EDGE,"E5.bottom")])]});Q0=makeQuery(id+"F11.boolean.opBoolean","SPLIT",FACE,{"disambiguationData":[TD([subQ400])],"derivedFrom":makeQuery(id+"F9.boolean.opBoolean","SPLIT",FACE,{"disambiguationData":[TD([subQ400])],"derivedFrom":makeQuery(id+"F7.boolean.opBoolean","SPLIT",FACE,{"disambiguationData":[TD([subQ400])],"derivedFrom":makeQuery(id+"F5.boolean.opBoolean","SPLIT",FACE,{"disambiguationData":[TD([subQ400])],"derivedFrom":makeQuery(id+"F1.opExtrude","CAP_FACE",FACE,{"disambiguationData":[OSD([sQuery(id+"F0.wireOp",EDGE,"E0.bottom"),sQuery(id+"F0.wireOp",EDGE,"E0.top"),sQuery(id+"F0.wireOp",EDGE,"E0.left"),sQuery(id+"F0.wireOp",EDGE,"E0.right"),sQuery(id+"F0.wireOp",EDGE,"E1.filletArc"),sQuery(id+"F0.wireOp",EDGE,"E2.filletArc"),sQuery(id+"F0.wireOp",EDGE,"E3.filletArc"),sQuery(id+"F0.wireOp",EDGE,"E4.filletArc")])],"isStart":false})})})})});}
            var sketch = newSketch(context, id + "F12", { "sketchPlane" : qUnion([Q0])});
            skArc(sketch, "E1644", {"start": v(-0.98, -8.87) * mm, "mid": v(-1.11, -9.05) * mm, "end": v(-1.25, -9.22) * mm});
            skArc(sketch, "E1645", {"start": v(-1.25, -9.22) * mm, "mid": v(-1.42, -9.43) * mm, "end": v(-1.6, -9.63) * mm});
            skArc(sketch, "E1646", {"start": v(-1.6, -9.63) * mm, "mid": v(-1.76, -9.83) * mm, "end": v(-1.93, -10.03) * mm});
            skArc(sketch, "E1647", {"start": v(-1.93, -10.03) * mm, "mid": v(-2.08, -10.19) * mm, "end": v(-2.23, -10.34) * mm});
            skLineSegment(sketch, "E1648", {"start": v(-2.23, -10.34) * mm, "end": v(-2.89, -11.02) * mm});
            skLineSegment(sketch, "E1649", {"start": v(-2.89, -11.02) * mm, "end": v(-4.14, -10.4) * mm});
            skArc(sketch, "E1650", {"start": v(-4.14, -10.4) * mm, "mid": v(-4.9, -10.03) * mm, "end": v(-5.65, -9.7) * mm});
            skArc(sketch, "E1651", {"start": v(-5.65, -9.7) * mm, "mid": v(-6.27, -9.46) * mm, "end": v(-6.9, -9.25) * mm});
            skArc(sketch, "E1652", {"start": v(-6.9, -9.25) * mm, "mid": v(-7.48, -9.1) * mm, "end": v(-8.06, -8.99) * mm});
            skArc(sketch, "E1653", {"start": v(-8.06, -8.99) * mm, "mid": v(-8.7, -8.9) * mm, "end": v(-9.33, -8.86) * mm});
            skArc(sketch, "E1654", {"start": v(-9.33, -8.86) * mm, "mid": v(-9.77, -8.85) * mm, "end": v(-10.2, -8.86) * mm});
            skArc(sketch, "E1655", {"start": v(-10.2, -8.86) * mm, "mid": v(-10.58, -8.89) * mm, "end": v(-10.96, -8.94) * mm});
            skArc(sketch, "E1656", {"start": v(-10.96, -8.94) * mm, "mid": v(-11.3, -9.01) * mm, "end": v(-11.64, -9.11) * mm});
            skArc(sketch, "E1657", {"start": v(-11.64, -9.11) * mm, "mid": v(-11.97, -9.23) * mm, "end": v(-12.3, -9.37) * mm});
            skArc(sketch, "E1658", {"start": v(-12.3, -9.37) * mm, "mid": v(-12.69, -9.6) * mm, "end": v(-13.06, -9.86) * mm});
            skArc(sketch, "E1659", {"start": v(-13.06, -9.86) * mm, "mid": v(-13.39, -10.15) * mm, "end": v(-13.68, -10.48) * mm});
            skArc(sketch, "E1660", {"start": v(-13.68, -10.48) * mm, "mid": v(-13.9, -10.81) * mm, "end": v(-14.1, -11.18) * mm});
            skArc(sketch, "E1661", {"start": v(-14.1, -11.18) * mm, "mid": v(-14.2, -11.52) * mm, "end": v(-14.25, -11.87) * mm});
            skArc(sketch, "E1662", {"start": v(-14.25, -11.87) * mm, "mid": v(-14.26, -11.99) * mm, "end": v(-14.27, -12.1) * mm});
            skArc(sketch, "E1663", {"start": v(-14.27, -12.1) * mm, "mid": v(-14.29, -12.17) * mm, "end": v(-14.32, -12.24) * mm});
            skArc(sketch, "E1664", {"start": v(-14.32, -12.24) * mm, "mid": v(-14.35, -12.3) * mm, "end": v(-14.4, -12.34) * mm});
            skArc(sketch, "E1665", {"start": v(-14.4, -12.34) * mm, "mid": v(-14.48, -12.4) * mm, "end": v(-14.55, -12.44) * mm});
            skArc(sketch, "E1666", {"start": v(-14.55, -12.44) * mm, "mid": v(-14.76, -12.57) * mm, "end": v(-14.96, -12.7) * mm});
            skArc(sketch, "E1667", {"start": v(-14.96, -12.7) * mm, "mid": v(-15.27, -12.93) * mm, "end": v(-15.57, -13.17) * mm});
            skArc(sketch, "E1668", {"start": v(-15.57, -13.17) * mm, "mid": v(-15.86, -13.42) * mm, "end": v(-16.16, -13.67) * mm});
            skArc(sketch, "E1669", {"start": v(-16.16, -13.67) * mm, "mid": v(-16.34, -13.84) * mm, "end": v(-16.51, -14.03) * mm});
            skArc(sketch, "E1670", {"start": v(-16.51, -14.03) * mm, "mid": v(-16.86, -14.5) * mm, "end": v(-17.12, -15) * mm});
            skArc(sketch, "E1671", {"start": v(-17.12, -15) * mm, "mid": v(-17.28, -15.53) * mm, "end": v(-17.34, -16.07) * mm});
            skArc(sketch, "E1672", {"start": v(-17.34, -16.07) * mm, "mid": v(-17.3, -16.61) * mm, "end": v(-17.15, -17.13) * mm});
            skArc(sketch, "E1673", {"start": v(-17.15, -17.13) * mm, "mid": v(-16.9, -17.62) * mm, "end": v(-16.56, -18.07) * mm});
            skArc(sketch, "E1674", {"start": v(-16.56, -18.07) * mm, "mid": v(-16.3, -18.34) * mm, "end": v(-16, -18.59) * mm});
            skArc(sketch, "E1675", {"start": v(-16, -18.59) * mm, "mid": v(-15.69, -18.8) * mm, "end": v(-15.35, -19) * mm});
            skArc(sketch, "E1676", {"start": v(-15.35, -19) * mm, "mid": v(-15, -19.16) * mm, "end": v(-14.63, -19.3) * mm});
            skArc(sketch, "E1677", {"start": v(-14.63, -19.3) * mm, "mid": v(-14.25, -19.4) * mm, "end": v(-13.85, -19.46) * mm});
            skArc(sketch, "E1678", {"start": v(-13.85, -19.46) * mm, "mid": v(-13.73, -19.48) * mm, "end": v(-13.6, -19.5) * mm});
            skArc(sketch, "E1679", {"start": v(-13.6, -19.5) * mm, "mid": v(-13.53, -19.53) * mm, "end": v(-13.46, -19.56) * mm});
            skArc(sketch, "E1680", {"start": v(-13.46, -19.56) * mm, "mid": v(-13.4, -19.6) * mm, "end": v(-13.36, -19.65) * mm});
            skArc(sketch, "E1681", {"start": v(-13.36, -19.65) * mm, "mid": v(-13.32, -19.71) * mm, "end": v(-13.29, -19.78) * mm});
            skArc(sketch, "E1682", {"start": v(-13.29, -19.78) * mm, "mid": v(-13.21, -19.94) * mm, "end": v(-13.11, -20.07) * mm});
            skArc(sketch, "E1683", {"start": v(-13.11, -20.07) * mm, "mid": v(-12.98, -20.23) * mm, "end": v(-12.84, -20.37) * mm});
            skArc(sketch, "E1684", {"start": v(-12.84, -20.37) * mm, "mid": v(-12.67, -20.5) * mm, "end": v(-12.48, -20.64) * mm});
            skArc(sketch, "E1685", {"start": v(-12.48, -20.64) * mm, "mid": v(-12.3, -20.75) * mm, "end": v(-12.1, -20.85) * mm});
            skArc(sketch, "E1686", {"start": v(-12.1, -20.85) * mm, "mid": v(-11.95, -20.91) * mm, "end": v(-11.8, -20.96) * mm});
            skArc(sketch, "E1687", {"start": v(-11.8, -20.96) * mm, "mid": v(-11.66, -21) * mm, "end": v(-11.52, -21.03) * mm});
            skArc(sketch, "E1688", {"start": v(-11.52, -21.03) * mm, "mid": v(-11.35, -21.04) * mm, "end": v(-11.17, -21.05) * mm});
            skArc(sketch, "E1689", {"start": v(-11.17, -21.05) * mm, "mid": v(-10.9, -21.06) * mm, "end": v(-10.62, -21.06) * mm});
            skArc(sketch, "E1690", {"start": v(-10.62, -21.06) * mm, "mid": v(-10, -21.03) * mm, "end": v(-9.39, -20.96) * mm});
            skArc(sketch, "E1691", {"start": v(-9.39, -20.96) * mm, "mid": v(-8.77, -20.85) * mm, "end": v(-8.17, -20.69) * mm});
            skArc(sketch, "E1692", {"start": v(-8.17, -20.69) * mm, "mid": v(-7.53, -20.47) * mm, "end": v(-6.9, -20.22) * mm});
            skArc(sketch, "E1693", {"start": v(-6.9, -20.22) * mm, "mid": v(-6.22, -19.9) * mm, "end": v(-5.55, -19.54) * mm});
            skLineSegment(sketch, "E1694", {"start": v(-5.55, -19.54) * mm, "end": v(-4.62, -19.01) * mm});
            skLineSegment(sketch, "E1695", {"start": v(-4.62, -19.01) * mm, "end": v(-4.3, -19.23) * mm});
            skArc(sketch, "E1696", {"start": v(-4.3, -19.23) * mm, "mid": v(-4.2, -19.3) * mm, "end": v(-4.11, -19.38) * mm});
            skArc(sketch, "E1697", {"start": v(-4.11, -19.38) * mm, "mid": v(-3.87, -19.57) * mm, "end": v(-3.62, -19.77) * mm});
            skArc(sketch, "E1698", {"start": v(-3.62, -19.77) * mm, "mid": v(-3.33, -20) * mm, "end": v(-3.04, -20.24) * mm});
            skArc(sketch, "E1699", {"start": v(-3.04, -20.24) * mm, "mid": v(-2.72, -20.5) * mm, "end": v(-2.4, -20.76) * mm});
            skLineSegment(sketch, "E1700", {"start": v(-2.4, -20.76) * mm, "end": v(-0.81, -22.06) * mm});
            skLineSegment(sketch, "E1701", {"start": v(-0.81, -22.06) * mm, "end": v(-0.25, -21.28) * mm});
            skArc(sketch, "E1702", {"start": v(-0.25, -21.28) * mm, "mid": v(-0.12, -21.1) * mm, "end": v(0, -20.94) * mm});
            skArc(sketch, "E1703", {"start": v(0, -20.94) * mm, "mid": v(0.16, -20.74) * mm, "end": v(0.32, -20.55) * mm});
            skArc(sketch, "E1704", {"start": v(0.32, -20.55) * mm, "mid": v(0.47, -20.36) * mm, "end": v(0.63, -20.17) * mm});
            skArc(sketch, "E1705", {"start": v(0.63, -20.17) * mm, "mid": v(0.76, -20.03) * mm, "end": v(0.89, -19.88) * mm});
            skLineSegment(sketch, "E1706", {"start": v(0.89, -19.88) * mm, "end": v(1.46, -19.26) * mm});
            skLineSegment(sketch, "E1707", {"start": v(1.46, -19.26) * mm, "end": v(1.92, -19.53) * mm});
            skArc(sketch, "E1708", {"start": v(1.92, -19.53) * mm, "mid": v(2.3, -19.75) * mm, "end": v(2.7, -19.95) * mm});
            skArc(sketch, "E1709", {"start": v(2.7, -19.95) * mm, "mid": v(3.1, -20.15) * mm, "end": v(3.52, -20.34) * mm});
            skArc(sketch, "E1710", {"start": v(3.52, -20.34) * mm, "mid": v(3.9, -20.5) * mm, "end": v(4.3, -20.65) * mm});
            skArc(sketch, "E1711", {"start": v(4.3, -20.65) * mm, "mid": v(4.63, -20.76) * mm, "end": v(4.96, -20.85) * mm});
            skArc(sketch, "E1712", {"start": v(4.96, -20.85) * mm, "mid": v(5.21, -20.9) * mm, "end": v(5.46, -20.96) * mm});
            skArc(sketch, "E1713", {"start": v(5.46, -20.96) * mm, "mid": v(5.7, -21) * mm, "end": v(5.92, -21.02) * mm});
            skArc(sketch, "E1714", {"start": v(5.92, -21.02) * mm, "mid": v(6.2, -21.04) * mm, "end": v(6.47, -21.06) * mm});
            skArc(sketch, "E1715", {"start": v(6.47, -21.06) * mm, "mid": v(6.85, -21.06) * mm, "end": v(7.24, -21.07) * mm});
            skArc(sketch, "E1716", {"start": v(7.24, -21.07) * mm, "mid": v(7.67, -21.06) * mm, "end": v(8.1, -21.06) * mm});
            skArc(sketch, "E1717", {"start": v(8.1, -21.06) * mm, "mid": v(8.33, -21.05) * mm, "end": v(8.56, -21.03) * mm});
            skArc(sketch, "E1718", {"start": v(8.56, -21.03) * mm, "mid": v(8.76, -21) * mm, "end": v(8.94, -20.95) * mm});
            skArc(sketch, "E1719", {"start": v(8.94, -20.95) * mm, "mid": v(9.18, -20.88) * mm, "end": v(9.42, -20.8) * mm});
            skArc(sketch, "E1720", {"start": v(9.42, -20.8) * mm, "mid": v(9.95, -20.59) * mm, "end": v(10.46, -20.31) * mm});
            skArc(sketch, "E1721", {"start": v(10.46, -20.31) * mm, "mid": v(10.87, -20.02) * mm, "end": v(11.22, -19.66) * mm});
            skArc(sketch, "E1722", {"start": v(11.22, -19.66) * mm, "mid": v(11.5, -19.28) * mm, "end": v(11.71, -18.85) * mm});
            skArc(sketch, "E1723", {"start": v(11.71, -18.85) * mm, "mid": v(11.86, -18.36) * mm, "end": v(11.94, -17.85) * mm});
            skLineSegment(sketch, "E1724", {"start": v(11.94, -17.85) * mm, "end": v(12, -17.2) * mm});
            skLineSegment(sketch, "E1725", {"start": v(12, -17.2) * mm, "end": v(12.53, -17) * mm});
            skArc(sketch, "E1726", {"start": v(12.53, -17) * mm, "mid": v(13.05, -16.77) * mm, "end": v(13.55, -16.5) * mm});
            skArc(sketch, "E1727", {"start": v(13.55, -16.5) * mm, "mid": v(13.95, -16.2) * mm, "end": v(14.3, -15.85) * mm});
            skArc(sketch, "E1728", {"start": v(14.3, -15.85) * mm, "mid": v(14.56, -15.49) * mm, "end": v(14.75, -15.09) * mm});
            skArc(sketch, "E1729", {"start": v(14.75, -15.09) * mm, "mid": v(14.87, -14.66) * mm, "end": v(14.9, -14.21) * mm});
            skArc(sketch, "E1730", {"start": v(14.9, -14.21) * mm, "mid": v(14.9, -13.95) * mm, "end": v(14.84, -13.7) * mm});
            skArc(sketch, "E1731", {"start": v(14.84, -13.7) * mm, "mid": v(14.76, -13.44) * mm, "end": v(14.65, -13.2) * mm});
            skArc(sketch, "E1732", {"start": v(14.65, -13.2) * mm, "mid": v(14.5, -12.95) * mm, "end": v(14.33, -12.71) * mm});
            skArc(sketch, "E1733", {"start": v(14.33, -12.71) * mm, "mid": v(14.1, -12.46) * mm, "end": v(13.86, -12.23) * mm});
            skArc(sketch, "E1734", {"start": v(13.86, -12.23) * mm, "mid": v(13.66, -12.06) * mm, "end": v(13.45, -11.91) * mm});
            skArc(sketch, "E1735", {"start": v(13.45, -11.91) * mm, "mid": v(13.17, -11.74) * mm, "end": v(12.9, -11.57) * mm});
            skArc(sketch, "E1736", {"start": v(12.9, -11.57) * mm, "mid": v(12.62, -11.42) * mm, "end": v(12.34, -11.28) * mm});
            skArc(sketch, "E1737", {"start": v(12.34, -11.28) * mm, "mid": v(12.2, -11.23) * mm, "end": v(12.06, -11.21) * mm});
            skArc(sketch, "E1738", {"start": v(12.06, -11.21) * mm, "mid": v(12.04, -11.2) * mm, "end": v(12.02, -11.2) * mm});
            skArc(sketch, "E1739", {"start": v(12.02, -11.2) * mm, "mid": v(12, -11.17) * mm, "end": v(11.99, -11.14) * mm});
            skArc(sketch, "E1740", {"start": v(11.99, -11.14) * mm, "mid": v(11.97, -11.1) * mm, "end": v(11.96, -11.05) * mm});
            skArc(sketch, "E1741", {"start": v(11.96, -11.05) * mm, "mid": v(11.96, -11) * mm, "end": v(11.95, -10.95) * mm});
            skArc(sketch, "E1742", {"start": v(11.95, -10.95) * mm, "mid": v(11.94, -10.77) * mm, "end": v(11.9, -10.6) * mm});
            skArc(sketch, "E1743", {"start": v(11.9, -10.6) * mm, "mid": v(11.8, -10.37) * mm, "end": v(11.69, -10.15) * mm});
            skArc(sketch, "E1744", {"start": v(11.69, -10.15) * mm, "mid": v(11.56, -9.92) * mm, "end": v(11.4, -9.7) * mm});
            skArc(sketch, "E1745", {"start": v(11.4, -9.7) * mm, "mid": v(11.25, -9.52) * mm, "end": v(11.08, -9.35) * mm});
            skArc(sketch, "E1746", {"start": v(11.08, -9.35) * mm, "mid": v(10.72, -9.04) * mm, "end": v(10.32, -8.77) * mm});
            skArc(sketch, "E1747", {"start": v(10.32, -8.76) * mm, "mid": v(9.94, -8.56) * mm, "end": v(9.53, -8.4) * mm});
            skArc(sketch, "E1748", {"start": v(9.53, -8.4) * mm, "mid": v(9.08, -8.27) * mm, "end": v(8.6, -8.2) * mm});
            skArc(sketch, "E1749", {"start": v(8.6, -8.2) * mm, "mid": v(8.02, -8.15) * mm, "end": v(7.43, -8.14) * mm});
            skArc(sketch, "E1750", {"start": v(7.43, -8.14) * mm, "mid": v(6.79, -8.16) * mm, "end": v(6.15, -8.23) * mm});
            skArc(sketch, "E1751", {"start": v(6.15, -8.23) * mm, "mid": v(5.6, -8.33) * mm, "end": v(5.05, -8.49) * mm});
            skArc(sketch, "E1752", {"start": v(5.05, -8.49) * mm, "mid": v(4.49, -8.7) * mm, "end": v(3.95, -8.97) * mm});
            skArc(sketch, "E1753", {"start": v(3.95, -8.97) * mm, "mid": v(3.28, -9.35) * mm, "end": v(2.63, -9.76) * mm});
            skArc(sketch, "E1754", {"start": v(2.63, -9.76) * mm, "mid": v(2.46, -9.87) * mm, "end": v(2.28, -9.99) * mm});
            skArc(sketch, "E1755", {"start": v(2.28, -9.99) * mm, "mid": v(2.13, -10.09) * mm, "end": v(1.97, -10.18) * mm});
            skArc(sketch, "E1756", {"start": v(1.97, -10.18) * mm, "mid": v(1.84, -10.26) * mm, "end": v(1.7, -10.34) * mm});
            skArc(sketch, "E1757", {"start": v(1.7, -10.34) * mm, "mid": v(1.68, -10.35) * mm, "end": v(1.65, -10.36) * mm});
            skArc(sketch, "E1758", {"start": v(1.65, -10.36) * mm, "mid": v(1.63, -10.35) * mm, "end": v(1.6, -10.34) * mm});
            skArc(sketch, "E1759", {"start": v(1.6, -10.34) * mm, "mid": v(1.46, -10.18) * mm, "end": v(1.33, -10.02) * mm});
            skArc(sketch, "E1760", {"start": v(1.33, -10.02) * mm, "mid": v(1.17, -9.84) * mm, "end": v(1.01, -9.65) * mm});
            skArc(sketch, "E1761", {"start": v(1.01, -9.65) * mm, "mid": v(0.83, -9.43) * mm, "end": v(0.65, -9.21) * mm});
            skArc(sketch, "E1762", {"start": v(0.65, -9.21) * mm, "mid": v(0.47, -9) * mm, "end": v(0.29, -8.78) * mm});
            skArc(sketch, "E1763", {"start": v(0.29, -8.78) * mm, "mid": v(0.13, -8.6) * mm, "end": v(-0.02, -8.4) * mm});
            skArc(sketch, "E1764", {"start": v(-0.02, -8.4) * mm, "mid": v(-0.16, -8.25) * mm, "end": v(-0.3, -8.09) * mm});
            skArc(sketch, "E1765", {"start": v(-0.3, -8.09) * mm, "mid": v(-0.31, -8.07) * mm, "end": v(-0.33, -8.07) * mm});
            skArc(sketch, "E1766", {"start": v(-0.33, -8.07) * mm, "mid": v(-0.35, -8.07) * mm, "end": v(-0.37, -8.09) * mm});
            skArc(sketch, "E1767", {"start": v(-0.37, -8.09) * mm, "mid": v(-0.46, -8.2) * mm, "end": v(-0.55, -8.3) * mm});
            skArc(sketch, "E1768", {"start": v(-0.55, -8.3) * mm, "mid": v(-0.65, -8.43) * mm, "end": v(-0.75, -8.56) * mm});
            skArc(sketch, "E1769", {"start": v(-0.75, -8.56) * mm, "mid": v(-0.86, -8.72) * mm, "end": v(-0.98, -8.87) * mm});
            skArc(sketch, "E1770", {"start": v(8.8, -9.17) * mm, "mid": v(9.02, -9.23) * mm, "end": v(9.25, -9.3) * mm});
            skArc(sketch, "E1771", {"start": v(9.25, -9.3) * mm, "mid": v(9.48, -9.38) * mm, "end": v(9.7, -9.47) * mm});
            skArc(sketch, "E1772", {"start": v(9.7, -9.47) * mm, "mid": v(9.9, -9.57) * mm, "end": v(10.1, -9.68) * mm});
            skArc(sketch, "E1773", {"start": v(10.1, -9.68) * mm, "mid": v(10.27, -9.78) * mm, "end": v(10.43, -9.9) * mm});
            skArc(sketch, "E1774", {"start": v(10.43, -9.9) * mm, "mid": v(10.53, -9.98) * mm, "end": v(10.61, -10.08) * mm});
            skArc(sketch, "E1775", {"start": v(10.61, -10.08) * mm, "mid": v(10.73, -10.23) * mm, "end": v(10.85, -10.38) * mm});
            skArc(sketch, "E1776", {"start": v(10.85, -10.38) * mm, "mid": v(10.95, -10.54) * mm, "end": v(11.06, -10.7) * mm});
            skArc(sketch, "E1777", {"start": v(11.06, -10.7) * mm, "mid": v(11.09, -10.76) * mm, "end": v(11.1, -10.84) * mm});
            skArc(sketch, "E1778", {"start": v(11.1, -10.84) * mm, "mid": v(11.1, -10.86) * mm, "end": v(11.08, -10.86) * mm});
            skArc(sketch, "E1779", {"start": v(11.08, -10.86) * mm, "mid": v(10.94, -10.87) * mm, "end": v(10.8, -10.87) * mm});
            skArc(sketch, "E1780", {"start": v(10.8, -10.87) * mm, "mid": v(10.65, -10.87) * mm, "end": v(10.49, -10.87) * mm});
            skArc(sketch, "E1781", {"start": v(10.49, -10.87) * mm, "mid": v(10.3, -10.86) * mm, "end": v(10.1, -10.85) * mm});
            skArc(sketch, "E1782", {"start": v(10.1, -10.85) * mm, "mid": v(9.86, -10.84) * mm, "end": v(9.6, -10.84) * mm});
            skArc(sketch, "E1783", {"start": v(9.6, -10.84) * mm, "mid": v(9.39, -10.84) * mm, "end": v(9.18, -10.86) * mm});
            skArc(sketch, "E1784", {"start": v(9.18, -10.86) * mm, "mid": v(8.98, -10.87) * mm, "end": v(8.78, -10.9) * mm});
            skArc(sketch, "E1785", {"start": v(8.78, -10.9) * mm, "mid": v(8.58, -10.93) * mm, "end": v(8.38, -10.97) * mm});
            skArc(sketch, "E1786", {"start": v(8.38, -10.97) * mm, "mid": v(8.04, -11.06) * mm, "end": v(7.71, -11.16) * mm});
            skArc(sketch, "E1787", {"start": v(7.71, -11.16) * mm, "mid": v(7.26, -11.31) * mm, "end": v(6.8, -11.48) * mm});
            skArc(sketch, "E1788", {"start": v(6.8, -11.48) * mm, "mid": v(6.34, -11.66) * mm, "end": v(5.88, -11.85) * mm});
            skArc(sketch, "E1789", {"start": v(5.88, -11.85) * mm, "mid": v(5.5, -12.02) * mm, "end": v(5.13, -12.2) * mm});
            skLineSegment(sketch, "E1790", {"start": v(5.13, -12.2) * mm, "end": v(4.65, -12.44) * mm});
            skLineSegment(sketch, "E1791", {"start": v(4.65, -12.44) * mm, "end": v(4.09, -12.16) * mm});
            skArc(sketch, "E1792", {"start": v(4.09, -12.16) * mm, "mid": v(3.83, -12.02) * mm, "end": v(3.59, -11.88) * mm});
            skArc(sketch, "E1793", {"start": v(3.59, -11.88) * mm, "mid": v(3.29, -11.7) * mm, "end": v(2.99, -11.5) * mm});
            skArc(sketch, "E1794", {"start": v(2.99, -11.5) * mm, "mid": v(2.68, -11.3) * mm, "end": v(2.38, -11.1) * mm});
            skArc(sketch, "E1795", {"start": v(2.38, -11.1) * mm, "mid": v(2.35, -11.07) * mm, "end": v(2.34, -11.02) * mm});
            skArc(sketch, "E1796", {"start": v(2.34, -11.02) * mm, "mid": v(2.35, -10.97) * mm, "end": v(2.39, -10.94) * mm});
            skArc(sketch, "E1797", {"start": v(2.39, -10.94) * mm, "mid": v(2.82, -10.69) * mm, "end": v(3.25, -10.44) * mm});
            skArc(sketch, "E1798", {"start": v(3.25, -10.44) * mm, "mid": v(3.66, -10.2) * mm, "end": v(4.07, -9.97) * mm});
            skArc(sketch, "E1799", {"start": v(4.07, -9.97) * mm, "mid": v(4.4, -9.8) * mm, "end": v(4.72, -9.64) * mm});
            skArc(sketch, "E1800", {"start": v(4.72, -9.64) * mm, "mid": v(5.2, -9.44) * mm, "end": v(5.7, -9.28) * mm});
            skArc(sketch, "E1801", {"start": v(5.7, -9.28) * mm, "mid": v(6.23, -9.15) * mm, "end": v(6.76, -9.07) * mm});
            skArc(sketch, "E1802", {"start": v(6.76, -9.07) * mm, "mid": v(7.28, -9.03) * mm, "end": v(7.8, -9.03) * mm});
            skArc(sketch, "E1803", {"start": v(7.8, -9.03) * mm, "mid": v(8.3, -9.08) * mm, "end": v(8.8, -9.17) * mm});
            skArc(sketch, "E1804", {"start": v(0.43, -11.27) * mm, "mid": v(0.43, -11.28) * mm, "end": v(0.42, -11.29) * mm});
            skArc(sketch, "E1805", {"start": v(0.42, -11.29) * mm, "mid": v(0.34, -11.35) * mm, "end": v(0.26, -11.42) * mm});
            skArc(sketch, "E1806", {"start": v(0.26, -11.42) * mm, "mid": v(0.17, -11.5) * mm, "end": v(0.08, -11.56) * mm});
            skArc(sketch, "E1807", {"start": v(0.08, -11.56) * mm, "mid": v(-0.03, -11.65) * mm, "end": v(-0.14, -11.73) * mm});
            skLineSegment(sketch, "E1808", {"start": v(-0.14, -11.73) * mm, "end": v(-0.7, -12.17) * mm});
            skLineSegment(sketch, "E1809", {"start": v(-0.7, -12.17) * mm, "end": v(-1.47, -11.76) * mm});
            skLineSegment(sketch, "E1810", {"start": v(-1.47, -11.76) * mm, "end": v(-2.23, -11.36) * mm});
            skLineSegment(sketch, "E1811", {"start": v(-2.23, -11.36) * mm, "end": v(-1.54, -10.73) * mm});
            skLineSegment(sketch, "E1812", {"start": v(-1.54, -10.73) * mm, "end": v(-0.86, -10.1) * mm});
            skLineSegment(sketch, "E1813", {"start": v(-0.86, -10.1) * mm, "end": v(-0.21, -10.66) * mm});
            skArc(sketch, "E1814", {"start": v(-0.21, -10.66) * mm, "mid": v(-0.09, -10.77) * mm, "end": v(0.03, -10.88) * mm});
            skArc(sketch, "E1815", {"start": v(0.03, -10.88) * mm, "mid": v(0.14, -10.98) * mm, "end": v(0.24, -11.08) * mm});
            skArc(sketch, "E1816", {"start": v(0.24, -11.08) * mm, "mid": v(0.33, -11.16) * mm, "end": v(0.42, -11.24) * mm});
            skArc(sketch, "E1817", {"start": v(0.42, -11.24) * mm, "mid": v(0.43, -11.25) * mm, "end": v(0.43, -11.27) * mm});
            skArc(sketch, "E1818", {"start": v(-9.06, -10.3) * mm, "mid": v(-8.9, -10.34) * mm, "end": v(-8.74, -10.38) * mm});
            skArc(sketch, "E1819", {"start": v(-8.74, -10.38) * mm, "mid": v(-8.53, -10.44) * mm, "end": v(-8.32, -10.5) * mm});
            skArc(sketch, "E1820", {"start": v(-8.32, -10.5) * mm, "mid": v(-8.1, -10.56) * mm, "end": v(-7.87, -10.62) * mm});
            skArc(sketch, "E1821", {"start": v(-7.87, -10.62) * mm, "mid": v(-7.68, -10.68) * mm, "end": v(-7.48, -10.74) * mm});
            skArc(sketch, "E1822", {"start": v(-7.48, -10.74) * mm, "mid": v(-7.03, -10.9) * mm, "end": v(-6.58, -11.06) * mm});
            skArc(sketch, "E1823", {"start": v(-6.58, -11.06) * mm, "mid": v(-6.02, -11.27) * mm, "end": v(-5.46, -11.5) * mm});
            skArc(sketch, "E1824", {"start": v(-5.46, -11.5) * mm, "mid": v(-4.88, -11.73) * mm, "end": v(-4.3, -11.97) * mm});
            skArc(sketch, "E1825", {"start": v(-4.3, -11.97) * mm, "mid": v(-4.25, -12) * mm, "end": v(-4.24, -12.06) * mm});
            skArc(sketch, "E1826", {"start": v(-4.24, -12.06) * mm, "mid": v(-4.24, -12.08) * mm, "end": v(-4.26, -12.1) * mm});
            skArc(sketch, "E1827", {"start": v(-4.26, -12.1) * mm, "mid": v(-4.36, -12.16) * mm, "end": v(-4.46, -12.23) * mm});
            skArc(sketch, "E1828", {"start": v(-4.46, -12.23) * mm, "mid": v(-4.57, -12.31) * mm, "end": v(-4.7, -12.4) * mm});
            skArc(sketch, "E1829", {"start": v(-4.7, -12.4) * mm, "mid": v(-4.84, -12.48) * mm, "end": v(-4.98, -12.57) * mm});
            skLineSegment(sketch, "E1830", {"start": v(-4.98, -12.57) * mm, "end": v(-5.73, -13.01) * mm});
            skLineSegment(sketch, "E1831", {"start": v(-5.73, -13.01) * mm, "end": v(-6.39, -12.77) * mm});
            skArc(sketch, "E1832", {"start": v(-6.39, -12.77) * mm, "mid": v(-7.06, -12.55) * mm, "end": v(-7.74, -12.36) * mm});
            skArc(sketch, "E1833", {"start": v(-7.74, -12.36) * mm, "mid": v(-8.48, -12.2) * mm, "end": v(-9.22, -12.07) * mm});
            skArc(sketch, "E1834", {"start": v(-9.22, -12.07) * mm, "mid": v(-9.98, -11.98) * mm, "end": v(-10.73, -11.92) * mm});
            skArc(sketch, "E1835", {"start": v(-10.73, -11.92) * mm, "mid": v(-11.46, -11.9) * mm, "end": v(-12.2, -11.9) * mm});
            skLineSegment(sketch, "E1836", {"start": v(-12.2, -11.9) * mm, "end": v(-13.37, -11.96) * mm});
            skLineSegment(sketch, "E1837", {"start": v(-13.37, -11.96) * mm, "end": v(-13.23, -11.61) * mm});
            skArc(sketch, "E1838", {"start": v(-13.23, -11.61) * mm, "mid": v(-13.2, -11.54) * mm, "end": v(-13.16, -11.47) * mm});
            skArc(sketch, "E1839", {"start": v(-13.16, -11.47) * mm, "mid": v(-13.12, -11.4) * mm, "end": v(-13.08, -11.32) * mm});
            skArc(sketch, "E1840", {"start": v(-13.08, -11.32) * mm, "mid": v(-13.04, -11.25) * mm, "end": v(-13, -11.18) * mm});
            skArc(sketch, "E1841", {"start": v(-13, -11.18) * mm, "mid": v(-12.96, -11.13) * mm, "end": v(-12.92, -11.09) * mm});
            skArc(sketch, "E1842", {"start": v(-12.92, -11.09) * mm, "mid": v(-12.82, -10.99) * mm, "end": v(-12.71, -10.9) * mm});
            skArc(sketch, "E1843", {"start": v(-12.71, -10.9) * mm, "mid": v(-12.53, -10.78) * mm, "end": v(-12.35, -10.67) * mm});
            skArc(sketch, "E1844", {"start": v(-12.35, -10.67) * mm, "mid": v(-12.15, -10.56) * mm, "end": v(-11.95, -10.45) * mm});
            skArc(sketch, "E1845", {"start": v(-11.95, -10.45) * mm, "mid": v(-11.77, -10.37) * mm, "end": v(-11.59, -10.3) * mm});
            skArc(sketch, "E1846", {"start": v(-11.59, -10.3) * mm, "mid": v(-11.36, -10.24) * mm, "end": v(-11.14, -10.2) * mm});
            skArc(sketch, "E1847", {"start": v(-11.14, -10.2) * mm, "mid": v(-10.8, -10.18) * mm, "end": v(-10.46, -10.18) * mm});
            skArc(sketch, "E1848", {"start": v(-10.46, -10.18) * mm, "mid": v(-10.1, -10.18) * mm, "end": v(-9.73, -10.2) * mm});
            skArc(sketch, "E1849", {"start": v(-9.73, -10.2) * mm, "mid": v(-9.4, -10.25) * mm, "end": v(-9.06, -10.3) * mm});
            skArc(sketch, "E1850", {"start": v(1.83, -12.37) * mm, "mid": v(1.96, -12.47) * mm, "end": v(2.1, -12.56) * mm});
            skArc(sketch, "E1851", {"start": v(2.1, -12.56) * mm, "mid": v(2.23, -12.66) * mm, "end": v(2.37, -12.76) * mm});
            skArc(sketch, "E1852", {"start": v(2.37, -12.76) * mm, "mid": v(2.5, -12.84) * mm, "end": v(2.62, -12.92) * mm});
            skArc(sketch, "E1853", {"start": v(2.62, -12.92) * mm, "mid": v(2.7, -12.96) * mm, "end": v(2.78, -13) * mm});
            skArc(sketch, "E1854", {"start": v(2.78, -13) * mm, "mid": v(2.84, -13.03) * mm, "end": v(2.9, -13.07) * mm});
            skArc(sketch, "E1855", {"start": v(2.9, -13.07) * mm, "mid": v(2.96, -13.1) * mm, "end": v(3, -13.13) * mm});
            skArc(sketch, "E1856", {"start": v(3, -13.13) * mm, "mid": v(3.04, -13.16) * mm, "end": v(3.08, -13.2) * mm});
            skArc(sketch, "E1857", {"start": v(3.08, -13.2) * mm, "mid": v(3.1, -13.21) * mm, "end": v(3.1, -13.23) * mm});
            skArc(sketch, "E1858", {"start": v(3.1, -13.23) * mm, "mid": v(3.1, -13.26) * mm, "end": v(3.08, -13.27) * mm});
            skArc(sketch, "E1859", {"start": v(3.08, -13.27) * mm, "mid": v(3.03, -13.31) * mm, "end": v(2.98, -13.35) * mm});
            skArc(sketch, "E1860", {"start": v(2.98, -13.35) * mm, "mid": v(2.9, -13.4) * mm, "end": v(2.84, -13.43) * mm});
            skArc(sketch, "E1861", {"start": v(2.84, -13.43) * mm, "mid": v(2.76, -13.47) * mm, "end": v(2.68, -13.51) * mm});
            skLineSegment(sketch, "E1862", {"start": v(2.68, -13.51) * mm, "end": v(2.26, -13.72) * mm});
            skLineSegment(sketch, "E1863", {"start": v(2.26, -13.72) * mm, "end": v(1.2, -13.16) * mm});
            skArc(sketch, "E1864", {"start": v(1.2, -13.16) * mm, "mid": v(1, -13.05) * mm, "end": v(0.8, -12.94) * mm});
            skArc(sketch, "E1865", {"start": v(0.8, -12.94) * mm, "mid": v(0.63, -12.84) * mm, "end": v(0.46, -12.75) * mm});
            skArc(sketch, "E1866", {"start": v(0.46, -12.75) * mm, "mid": v(0.3, -12.66) * mm, "end": v(0.16, -12.57) * mm});
            skArc(sketch, "E1867", {"start": v(0.16, -12.57) * mm, "mid": v(0.15, -12.56) * mm, "end": v(0.15, -12.55) * mm});
            skArc(sketch, "E1868", {"start": v(0.15, -12.55) * mm, "mid": v(0.16, -12.5) * mm, "end": v(0.18, -12.48) * mm});
            skArc(sketch, "E1869", {"start": v(0.18, -12.48) * mm, "mid": v(0.39, -12.33) * mm, "end": v(0.6, -12.2) * mm});
            skArc(sketch, "E1870", {"start": v(0.6, -12.2) * mm, "mid": v(0.8, -12.05) * mm, "end": v(1, -11.91) * mm});
            skArc(sketch, "E1871", {"start": v(1, -11.91) * mm, "mid": v(1.06, -11.89) * mm, "end": v(1.11, -11.88) * mm});
            skArc(sketch, "E1872", {"start": v(1.11, -11.88) * mm, "mid": v(1.14, -11.88) * mm, "end": v(1.16, -11.9) * mm});
            skArc(sketch, "E1873", {"start": v(1.16, -11.9) * mm, "mid": v(1.26, -11.96) * mm, "end": v(1.35, -12.02) * mm});
            skArc(sketch, "E1874", {"start": v(1.35, -12.02) * mm, "mid": v(1.46, -12.1) * mm, "end": v(1.57, -12.18) * mm});
            skArc(sketch, "E1875", {"start": v(1.57, -12.18) * mm, "mid": v(1.7, -12.27) * mm, "end": v(1.83, -12.37) * mm});
            skArc(sketch, "E1876", {"start": v(10.96, -12) * mm, "mid": v(10.98, -12.04) * mm, "end": v(10.98, -12.1) * mm});
            skArc(sketch, "E1877", {"start": v(10.98, -12.1) * mm, "mid": v(10.93, -12.2) * mm, "end": v(10.88, -12.3) * mm});
            skArc(sketch, "E1878", {"start": v(10.88, -12.3) * mm, "mid": v(10.8, -12.4) * mm, "end": v(10.71, -12.52) * mm});
            skArc(sketch, "E1879", {"start": v(10.71, -12.52) * mm, "mid": v(10.61, -12.63) * mm, "end": v(10.5, -12.74) * mm});
            skArc(sketch, "E1880", {"start": v(10.5, -12.74) * mm, "mid": v(10.26, -12.94) * mm, "end": v(10, -13.1) * mm});
            skArc(sketch, "E1881", {"start": v(10, -13.1) * mm, "mid": v(9.67, -13.23) * mm, "end": v(9.33, -13.33) * mm});
            skArc(sketch, "E1882", {"start": v(9.33, -13.33) * mm, "mid": v(8.96, -13.4) * mm, "end": v(8.58, -13.44) * mm});
            skArc(sketch, "E1883", {"start": v(8.58, -13.44) * mm, "mid": v(8.19, -13.43) * mm, "end": v(7.8, -13.4) * mm});
            skArc(sketch, "E1884", {"start": v(7.8, -13.4) * mm, "mid": v(7.5, -13.35) * mm, "end": v(7.19, -13.29) * mm});
            skArc(sketch, "E1885", {"start": v(7.19, -13.29) * mm, "mid": v(6.84, -13.2) * mm, "end": v(6.5, -13.11) * mm});
            skArc(sketch, "E1886", {"start": v(6.5, -13.11) * mm, "mid": v(6.16, -13.02) * mm, "end": v(5.83, -12.92) * mm});
            skArc(sketch, "E1887", {"start": v(5.83, -12.92) * mm, "mid": v(5.78, -12.88) * mm, "end": v(5.76, -12.83) * mm});
            skArc(sketch, "E1888", {"start": v(5.76, -12.83) * mm, "mid": v(5.78, -12.77) * mm, "end": v(5.83, -12.73) * mm});
            skArc(sketch, "E1889", {"start": v(5.83, -12.73) * mm, "mid": v(6.17, -12.59) * mm, "end": v(6.5, -12.45) * mm});
            skArc(sketch, "E1890", {"start": v(6.5, -12.45) * mm, "mid": v(6.84, -12.32) * mm, "end": v(7.19, -12.2) * mm});
            skArc(sketch, "E1891", {"start": v(7.19, -12.2) * mm, "mid": v(7.46, -12.1) * mm, "end": v(7.74, -12.03) * mm});
            skArc(sketch, "E1892", {"start": v(7.74, -12.03) * mm, "mid": v(8.04, -11.97) * mm, "end": v(8.35, -11.94) * mm});
            skArc(sketch, "E1893", {"start": v(8.35, -11.94) * mm, "mid": v(8.93, -11.92) * mm, "end": v(9.51, -11.9) * mm});
            skArc(sketch, "E1894", {"start": v(9.51, -11.9) * mm, "mid": v(10.13, -11.9) * mm, "end": v(10.74, -11.9) * mm});
            skArc(sketch, "E1895", {"start": v(10.74, -11.9) * mm, "mid": v(10.86, -11.93) * mm, "end": v(10.96, -12) * mm});
            skArc(sketch, "E1896", {"start": v(12.51, -12.55) * mm, "mid": v(12.73, -12.72) * mm, "end": v(12.93, -12.9) * mm});
            skArc(sketch, "E1897", {"start": v(12.93, -12.9) * mm, "mid": v(13.1, -13.09) * mm, "end": v(13.23, -13.28) * mm});
            skArc(sketch, "E1898", {"start": v(13.23, -13.28) * mm, "mid": v(13.34, -13.48) * mm, "end": v(13.42, -13.68) * mm});
            skArc(sketch, "E1899", {"start": v(13.42, -13.68) * mm, "mid": v(13.46, -13.88) * mm, "end": v(13.48, -14.09) * mm});
            skArc(sketch, "E1900", {"start": v(13.48, -14.09) * mm, "mid": v(13.46, -14.39) * mm, "end": v(13.39, -14.68) * mm});
            skArc(sketch, "E1901", {"start": v(13.39, -14.68) * mm, "mid": v(13.28, -14.95) * mm, "end": v(13.12, -15.19) * mm});
            skArc(sketch, "E1902", {"start": v(13.12, -15.19) * mm, "mid": v(12.91, -15.42) * mm, "end": v(12.67, -15.62) * mm});
            skArc(sketch, "E1903", {"start": v(12.67, -15.62) * mm, "mid": v(12.35, -15.82) * mm, "end": v(12.01, -15.98) * mm});
            skLineSegment(sketch, "E1904", {"start": v(12.01, -15.98) * mm, "end": v(11.55, -16.19) * mm});
            skLineSegment(sketch, "E1905", {"start": v(11.55, -16.19) * mm, "end": v(11.11, -15.75) * mm});
            skArc(sketch, "E1906", {"start": v(11.11, -15.75) * mm, "mid": v(10.9, -15.56) * mm, "end": v(10.66, -15.38) * mm});
            skArc(sketch, "E1907", {"start": v(10.66, -15.38) * mm, "mid": v(10.43, -15.23) * mm, "end": v(10.18, -15.11) * mm});
            skArc(sketch, "E1908", {"start": v(10.18, -15.11) * mm, "mid": v(9.92, -15.01) * mm, "end": v(9.65, -14.94) * mm});
            skArc(sketch, "E1909", {"start": v(9.65, -14.94) * mm, "mid": v(9.35, -14.88) * mm, "end": v(9.04, -14.85) * mm});
            skArc(sketch, "E1910", {"start": v(9.04, -14.85) * mm, "mid": v(8.74, -14.85) * mm, "end": v(8.43, -14.86) * mm});
            skArc(sketch, "E1911", {"start": v(8.43, -14.86) * mm, "mid": v(8.07, -14.9) * mm, "end": v(7.7, -14.95) * mm});
            skArc(sketch, "E1912", {"start": v(7.7, -14.95) * mm, "mid": v(7.33, -15.02) * mm, "end": v(6.96, -15.1) * mm});
            skArc(sketch, "E1913", {"start": v(6.96, -15.1) * mm, "mid": v(6.64, -15.2) * mm, "end": v(6.32, -15.3) * mm});
            skLineSegment(sketch, "E1914", {"start": v(6.32, -15.3) * mm, "end": v(5.85, -15.48) * mm});
            skLineSegment(sketch, "E1915", {"start": v(5.85, -15.48) * mm, "end": v(4.57, -14.87) * mm});
            skArc(sketch, "E1916", {"start": v(4.57, -14.87) * mm, "mid": v(4.32, -14.75) * mm, "end": v(4.08, -14.63) * mm});
            skArc(sketch, "E1917", {"start": v(4.08, -14.63) * mm, "mid": v(3.87, -14.53) * mm, "end": v(3.67, -14.42) * mm});
            skArc(sketch, "E1918", {"start": v(3.67, -14.42) * mm, "mid": v(3.49, -14.32) * mm, "end": v(3.31, -14.23) * mm});
            skArc(sketch, "E1919", {"start": v(3.31, -14.23) * mm, "mid": v(3.3, -14.21) * mm, "end": v(3.29, -14.19) * mm});
            skArc(sketch, "E1920", {"start": v(3.29, -14.19) * mm, "mid": v(3.3, -14.17) * mm, "end": v(3.3, -14.15) * mm});
            skArc(sketch, "E1921", {"start": v(3.3, -14.15) * mm, "mid": v(3.36, -14.1) * mm, "end": v(3.4, -14.07) * mm});
            skArc(sketch, "E1922", {"start": v(3.4, -14.07) * mm, "mid": v(3.47, -14.02) * mm, "end": v(3.54, -13.98) * mm});
            skArc(sketch, "E1923", {"start": v(3.54, -13.98) * mm, "mid": v(3.62, -13.94) * mm, "end": v(3.7, -13.9) * mm});
            skLineSegment(sketch, "E1924", {"start": v(3.7, -13.9) * mm, "end": v(4.1, -13.67) * mm});
            skLineSegment(sketch, "E1925", {"start": v(4.1, -13.67) * mm, "end": v(4.82, -13.9) * mm});
            skArc(sketch, "E1926", {"start": v(4.82, -13.9) * mm, "mid": v(5.6, -14.14) * mm, "end": v(6.38, -14.31) * mm});
            skArc(sketch, "E1927", {"start": v(6.38, -14.31) * mm, "mid": v(7.16, -14.42) * mm, "end": v(7.94, -14.45) * mm});
            skArc(sketch, "E1928", {"start": v(7.94, -14.45) * mm, "mid": v(8.64, -14.42) * mm, "end": v(9.34, -14.32) * mm});
            skArc(sketch, "E1929", {"start": v(9.34, -14.32) * mm, "mid": v(9.89, -14.17) * mm, "end": v(10.4, -13.92) * mm});
            skArc(sketch, "E1930", {"start": v(10.4, -13.92) * mm, "mid": v(10.6, -13.8) * mm, "end": v(10.79, -13.66) * mm});
            skArc(sketch, "E1931", {"start": v(10.79, -13.66) * mm, "mid": v(10.97, -13.5) * mm, "end": v(11.13, -13.34) * mm});
            skArc(sketch, "E1932", {"start": v(11.13, -13.34) * mm, "mid": v(11.28, -13.17) * mm, "end": v(11.42, -13) * mm});
            skArc(sketch, "E1933", {"start": v(11.42, -13) * mm, "mid": v(11.53, -12.82) * mm, "end": v(11.62, -12.64) * mm});
            skArc(sketch, "E1934", {"start": v(11.62, -12.64) * mm, "mid": v(11.7, -12.5) * mm, "end": v(11.78, -12.37) * mm});
            skArc(sketch, "E1935", {"start": v(11.78, -12.37) * mm, "mid": v(11.85, -12.3) * mm, "end": v(11.95, -12.28) * mm});
            skArc(sketch, "E1936", {"start": v(11.95, -12.28) * mm, "mid": v(12.06, -12.28) * mm, "end": v(12.16, -12.32) * mm});
            skArc(sketch, "E1937", {"start": v(12.16, -12.32) * mm, "mid": v(12.34, -12.43) * mm, "end": v(12.51, -12.55) * mm});
            skArc(sketch, "E1938", {"start": v(-2.83, -12.74) * mm, "mid": v(-2.7, -12.82) * mm, "end": v(-2.57, -12.9) * mm});
            skArc(sketch, "E1939", {"start": v(-2.57, -12.9) * mm, "mid": v(-2.46, -12.96) * mm, "end": v(-2.34, -13.02) * mm});
            skArc(sketch, "E1940", {"start": v(-2.34, -13.02) * mm, "mid": v(-2.25, -13.08) * mm, "end": v(-2.15, -13.14) * mm});
            skArc(sketch, "E1941", {"start": v(-2.15, -13.14) * mm, "mid": v(-2.14, -13.15) * mm, "end": v(-2.14, -13.16) * mm});
            skArc(sketch, "E1942", {"start": v(-2.14, -13.16) * mm, "mid": v(-2.14, -13.17) * mm, "end": v(-2.15, -13.18) * mm});
            skArc(sketch, "E1943", {"start": v(-2.15, -13.18) * mm, "mid": v(-2.24, -13.25) * mm, "end": v(-2.33, -13.33) * mm});
            skArc(sketch, "E1944", {"start": v(-2.33, -13.33) * mm, "mid": v(-2.44, -13.4) * mm, "end": v(-2.54, -13.49) * mm});
            skArc(sketch, "E1945", {"start": v(-2.54, -13.49) * mm, "mid": v(-2.67, -13.58) * mm, "end": v(-2.8, -13.68) * mm});
            skLineSegment(sketch, "E1946", {"start": v(-2.79, -13.68) * mm, "end": v(-3.44, -14.16) * mm});
            skLineSegment(sketch, "E1947", {"start": v(-3.44, -14.16) * mm, "end": v(-4.27, -13.73) * mm});
            skLineSegment(sketch, "E1948", {"start": v(-4.27, -13.73) * mm, "end": v(-5.1, -13.3) * mm});
            skLineSegment(sketch, "E1949", {"start": v(-5.1, -13.3) * mm, "end": v(-4.4, -12.83) * mm});
            skArc(sketch, "E1950", {"start": v(-4.4, -12.83) * mm, "mid": v(-4.27, -12.74) * mm, "end": v(-4.13, -12.66) * mm});
            skArc(sketch, "E1951", {"start": v(-4.13, -12.66) * mm, "mid": v(-4.01, -12.58) * mm, "end": v(-3.89, -12.5) * mm});
            skArc(sketch, "E1952", {"start": v(-3.89, -12.5) * mm, "mid": v(-3.78, -12.44) * mm, "end": v(-3.68, -12.38) * mm});
            skArc(sketch, "E1953", {"start": v(-3.68, -12.38) * mm, "mid": v(-3.65, -12.37) * mm, "end": v(-3.62, -12.37) * mm});
            skArc(sketch, "E1954", {"start": v(-3.62, -12.37) * mm, "mid": v(-3.59, -12.37) * mm, "end": v(-3.55, -12.38) * mm});
            skArc(sketch, "E1955", {"start": v(-3.55, -12.38) * mm, "mid": v(-3.45, -12.42) * mm, "end": v(-3.35, -12.47) * mm});
            skArc(sketch, "E1956", {"start": v(-3.35, -12.47) * mm, "mid": v(-3.22, -12.53) * mm, "end": v(-3.1, -12.6) * mm});
            skArc(sketch, "E1957", {"start": v(-3.1, -12.6) * mm, "mid": v(-2.97, -12.67) * mm, "end": v(-2.83, -12.74) * mm});
            skArc(sketch, "E1958", {"start": v(-10, -13.35) * mm, "mid": v(-9.66, -13.41) * mm, "end": v(-9.32, -13.48) * mm});
            skArc(sketch, "E1959", {"start": v(-9.32, -13.48) * mm, "mid": v(-9, -13.56) * mm, "end": v(-8.67, -13.64) * mm});
            skArc(sketch, "E1960", {"start": v(-8.67, -13.64) * mm, "mid": v(-8.39, -13.72) * mm, "end": v(-8.1, -13.8) * mm});
            skArc(sketch, "E1961", {"start": v(-8.1, -13.8) * mm, "mid": v(-8.06, -13.83) * mm, "end": v(-8.05, -13.88) * mm});
            skArc(sketch, "E1962", {"start": v(-8.05, -13.88) * mm, "mid": v(-8.07, -13.95) * mm, "end": v(-8.14, -13.99) * mm});
            skArc(sketch, "E1963", {"start": v(-8.14, -13.99) * mm, "mid": v(-8.5, -14.04) * mm, "end": v(-8.88, -14.08) * mm});
            skArc(sketch, "E1964", {"start": v(-8.88, -14.08) * mm, "mid": v(-9.27, -14.12) * mm, "end": v(-9.66, -14.15) * mm});
            skArc(sketch, "E1965", {"start": v(-9.66, -14.15) * mm, "mid": v(-10, -14.15) * mm, "end": v(-10.35, -14.14) * mm});
            skArc(sketch, "E1966", {"start": v(-10.35, -14.14) * mm, "mid": v(-10.7, -14.12) * mm, "end": v(-11.04, -14.07) * mm});
            skArc(sketch, "E1967", {"start": v(-11.04, -14.07) * mm, "mid": v(-11.36, -14) * mm, "end": v(-11.67, -13.92) * mm});
            skArc(sketch, "E1968", {"start": v(-11.67, -13.92) * mm, "mid": v(-11.94, -13.83) * mm, "end": v(-12.2, -13.71) * mm});
            skArc(sketch, "E1969", {"start": v(-12.2, -13.71) * mm, "mid": v(-12.4, -13.6) * mm, "end": v(-12.6, -13.45) * mm});
            skLineSegment(sketch, "E1970", {"start": v(-12.6, -13.45) * mm, "end": v(-12.86, -13.22) * mm});
            skLineSegment(sketch, "E1971", {"start": v(-12.86, -13.22) * mm, "end": v(-11.8, -13.22) * mm});
            skArc(sketch, "E1972", {"start": v(-11.8, -13.22) * mm, "mid": v(-11.58, -13.22) * mm, "end": v(-11.35, -13.23) * mm});
            skArc(sketch, "E1973", {"start": v(-11.35, -13.23) * mm, "mid": v(-11.1, -13.24) * mm, "end": v(-10.85, -13.25) * mm});
            skArc(sketch, "E1974", {"start": v(-10.85, -13.25) * mm, "mid": v(-10.6, -13.27) * mm, "end": v(-10.37, -13.3) * mm});
            skArc(sketch, "E1975", {"start": v(-10.37, -13.3) * mm, "mid": v(-10.18, -13.32) * mm, "end": v(-10, -13.35) * mm});
            skArc(sketch, "E1976", {"start": v(-13.5, -13.92) * mm, "mid": v(-13.26, -14.14) * mm, "end": v(-13, -14.33) * mm});
            skArc(sketch, "E1977", {"start": v(-13, -14.33) * mm, "mid": v(-12.74, -14.48) * mm, "end": v(-12.46, -14.59) * mm});
            skArc(sketch, "E1978", {"start": v(-12.46, -14.59) * mm, "mid": v(-12.11, -14.68) * mm, "end": v(-11.75, -14.74) * mm});
            skArc(sketch, "E1979", {"start": v(-11.75, -14.74) * mm, "mid": v(-11.24, -14.78) * mm, "end": v(-10.73, -14.81) * mm});
            skArc(sketch, "E1980", {"start": v(-10.73, -14.81) * mm, "mid": v(-10.25, -14.82) * mm, "end": v(-9.77, -14.82) * mm});
            skArc(sketch, "E1981", {"start": v(-9.77, -14.82) * mm, "mid": v(-9.35, -14.8) * mm, "end": v(-8.93, -14.76) * mm});
            skArc(sketch, "E1982", {"start": v(-8.93, -14.76) * mm, "mid": v(-8.56, -14.7) * mm, "end": v(-8.2, -14.64) * mm});
            skArc(sketch, "E1983", {"start": v(-8.2, -14.64) * mm, "mid": v(-7.85, -14.55) * mm, "end": v(-7.5, -14.45) * mm});
            skLineSegment(sketch, "E1984", {"start": v(-7.5, -14.45) * mm, "end": v(-6.98, -14.27) * mm});
            skLineSegment(sketch, "E1985", {"start": v(-6.98, -14.27) * mm, "end": v(-6.16, -14.69) * mm});
            skArc(sketch, "E1986", {"start": v(-6.16, -14.69) * mm, "mid": v(-5.75, -14.9) * mm, "end": v(-5.33, -15.12) * mm});
            skArc(sketch, "E1987", {"start": v(-5.33, -15.12) * mm, "mid": v(-5.26, -15.17) * mm, "end": v(-5.2, -15.25) * mm});
            skArc(sketch, "E1988", {"start": v(-5.2, -15.25) * mm, "mid": v(-5.2, -15.32) * mm, "end": v(-5.24, -15.38) * mm});
            skArc(sketch, "E1989", {"start": v(-5.24, -15.38) * mm, "mid": v(-5.45, -15.54) * mm, "end": v(-5.67, -15.7) * mm});
            skLineSegment(sketch, "E1990", {"start": v(-5.67, -15.7) * mm, "end": v(-6.27, -16.1) * mm});
            skLineSegment(sketch, "E1991", {"start": v(-6.27, -16.1) * mm, "end": v(-7.28, -15.76) * mm});
            skArc(sketch, "E1992", {"start": v(-7.28, -15.76) * mm, "mid": v(-7.9, -15.56) * mm, "end": v(-8.53, -15.4) * mm});
            skArc(sketch, "E1993", {"start": v(-8.53, -15.4) * mm, "mid": v(-9.04, -15.3) * mm, "end": v(-9.56, -15.24) * mm});
            skArc(sketch, "E1994", {"start": v(-9.56, -15.24) * mm, "mid": v(-10.03, -15.24) * mm, "end": v(-10.5, -15.28) * mm});
            skArc(sketch, "E1995", {"start": v(-10.5, -15.28) * mm, "mid": v(-11, -15.37) * mm, "end": v(-11.5, -15.5) * mm});
            skArc(sketch, "E1996", {"start": v(-11.5, -15.5) * mm, "mid": v(-11.95, -15.67) * mm, "end": v(-12.37, -15.9) * mm});
            skArc(sketch, "E1997", {"start": v(-12.37, -15.9) * mm, "mid": v(-12.72, -16.16) * mm, "end": v(-13.03, -16.48) * mm});
            skArc(sketch, "E1998", {"start": v(-13.03, -16.48) * mm, "mid": v(-13.27, -16.84) * mm, "end": v(-13.44, -17.23) * mm});
            skArc(sketch, "E1999", {"start": v(-13.44, -17.23) * mm, "mid": v(-13.55, -17.67) * mm, "end": v(-13.6, -18.12) * mm});
            skArc(sketch, "E2000", {"start": v(-13.6, -18.12) * mm, "mid": v(-13.61, -18.35) * mm, "end": v(-13.64, -18.58) * mm});
            skArc(sketch, "E2001", {"start": v(-13.64, -18.58) * mm, "mid": v(-13.68, -18.67) * mm, "end": v(-13.76, -18.73) * mm});
            skArc(sketch, "E2002", {"start": v(-13.76, -18.73) * mm, "mid": v(-13.88, -18.75) * mm, "end": v(-14, -18.72) * mm});
            skArc(sketch, "E2003", {"start": v(-14, -18.72) * mm, "mid": v(-14.28, -18.6) * mm, "end": v(-14.57, -18.46) * mm});
            skArc(sketch, "E2004", {"start": v(-14.57, -18.46) * mm, "mid": v(-14.8, -18.35) * mm, "end": v(-15.01, -18.22) * mm});
            skArc(sketch, "E2005", {"start": v(-15.01, -18.22) * mm, "mid": v(-15.19, -18.1) * mm, "end": v(-15.35, -17.95) * mm});
            skArc(sketch, "E2006", {"start": v(-15.35, -17.95) * mm, "mid": v(-15.5, -17.8) * mm, "end": v(-15.63, -17.62) * mm});
            skArc(sketch, "E2007", {"start": v(-15.63, -17.62) * mm, "mid": v(-15.77, -17.4) * mm, "end": v(-15.9, -17.18) * mm});
            skArc(sketch, "E2008", {"start": v(-15.9, -17.18) * mm, "mid": v(-16.04, -16.84) * mm, "end": v(-16.13, -16.5) * mm});
            skArc(sketch, "E2009", {"start": v(-16.13, -16.5) * mm, "mid": v(-16.15, -16.14) * mm, "end": v(-16.11, -15.78) * mm});
            skArc(sketch, "E2010", {"start": v(-16.11, -15.78) * mm, "mid": v(-16.01, -15.42) * mm, "end": v(-15.86, -15.08) * mm});
            skArc(sketch, "E2011", {"start": v(-15.86, -15.08) * mm, "mid": v(-15.63, -14.72) * mm, "end": v(-15.36, -14.4) * mm});
            skArc(sketch, "E2012", {"start": v(-15.36, -14.4) * mm, "mid": v(-15.22, -14.25) * mm, "end": v(-15.06, -14.12) * mm});
            skArc(sketch, "E2013", {"start": v(-15.06, -14.12) * mm, "mid": v(-14.84, -13.96) * mm, "end": v(-14.62, -13.81) * mm});
            skArc(sketch, "E2014", {"start": v(-14.62, -13.81) * mm, "mid": v(-14.4, -13.68) * mm, "end": v(-14.19, -13.56) * mm});
            skArc(sketch, "E2015", {"start": v(-14.19, -13.56) * mm, "mid": v(-14.07, -13.52) * mm, "end": v(-13.95, -13.5) * mm});
            skArc(sketch, "E2016", {"start": v(-13.95, -13.5) * mm, "mid": v(-13.94, -13.5) * mm, "end": v(-13.92, -13.51) * mm});
            skArc(sketch, "E2017", {"start": v(-13.92, -13.51) * mm, "mid": v(-13.86, -13.57) * mm, "end": v(-13.8, -13.63) * mm});
            skArc(sketch, "E2018", {"start": v(-13.8, -13.63) * mm, "mid": v(-13.73, -13.7) * mm, "end": v(-13.66, -13.76) * mm});
            skArc(sketch, "E2019", {"start": v(-13.66, -13.76) * mm, "mid": v(-13.58, -13.84) * mm, "end": v(-13.5, -13.92) * mm});
            skArc(sketch, "E2020", {"start": v(-0.33, -14.1) * mm, "mid": v(-0.16, -14.2) * mm, "end": v(0.01, -14.3) * mm});
            skArc(sketch, "E2021", {"start": v(0.01, -14.3) * mm, "mid": v(0.16, -14.38) * mm, "end": v(0.3, -14.48) * mm});
            skArc(sketch, "E2022", {"start": v(0.3, -14.48) * mm, "mid": v(0.42, -14.56) * mm, "end": v(0.54, -14.64) * mm});
            skArc(sketch, "E2023", {"start": v(0.54, -14.64) * mm, "mid": v(0.56, -14.66) * mm, "end": v(0.56, -14.69) * mm});
            skArc(sketch, "E2024", {"start": v(0.56, -14.69) * mm, "mid": v(0.55, -14.72) * mm, "end": v(0.53, -14.74) * mm});
            skArc(sketch, "E2025", {"start": v(0.53, -14.74) * mm, "mid": v(0.44, -14.81) * mm, "end": v(0.34, -14.89) * mm});
            skArc(sketch, "E2026", {"start": v(0.34, -14.89) * mm, "mid": v(0.22, -14.97) * mm, "end": v(0.1, -15.06) * mm});
            skArc(sketch, "E2027", {"start": v(0.1, -15.06) * mm, "mid": v(-0.04, -15.15) * mm, "end": v(-0.18, -15.24) * mm});
            skLineSegment(sketch, "E2028", {"start": v(-0.18, -15.24) * mm, "end": v(-0.9, -15.7) * mm});
            skLineSegment(sketch, "E2029", {"start": v(-0.9, -15.7) * mm, "end": v(-1.8, -15.15) * mm});
            skArc(sketch, "E2030", {"start": v(-1.8, -15.15) * mm, "mid": v(-1.98, -15.04) * mm, "end": v(-2.15, -14.93) * mm});
            skArc(sketch, "E2031", {"start": v(-2.15, -14.93) * mm, "mid": v(-2.3, -14.83) * mm, "end": v(-2.44, -14.74) * mm});
            skArc(sketch, "E2032", {"start": v(-2.44, -14.74) * mm, "mid": v(-2.56, -14.65) * mm, "end": v(-2.68, -14.57) * mm});
            skArc(sketch, "E2033", {"start": v(-2.68, -14.57) * mm, "mid": v(-2.69, -14.55) * mm, "end": v(-2.69, -14.53) * mm});
            skArc(sketch, "E2034", {"start": v(-2.69, -14.53) * mm, "mid": v(-2.66, -14.47) * mm, "end": v(-2.6, -14.42) * mm});
            skArc(sketch, "E2035", {"start": v(-2.6, -14.42) * mm, "mid": v(-2.32, -14.22) * mm, "end": v(-2.04, -14.02) * mm});
            skArc(sketch, "E2036", {"start": v(-2.04, -14.03) * mm, "mid": v(-1.75, -13.83) * mm, "end": v(-1.47, -13.64) * mm});
            skArc(sketch, "E2037", {"start": v(-1.47, -13.64) * mm, "mid": v(-1.4, -13.6) * mm, "end": v(-1.33, -13.6) * mm});
            skArc(sketch, "E2038", {"start": v(-1.33, -13.6) * mm, "mid": v(-1.3, -13.6) * mm, "end": v(-1.27, -13.61) * mm});
            skArc(sketch, "E2039", {"start": v(-1.27, -13.61) * mm, "mid": v(-1.13, -13.68) * mm, "end": v(-1, -13.74) * mm});
            skArc(sketch, "E2040", {"start": v(-1, -13.74) * mm, "mid": v(-0.84, -13.82) * mm, "end": v(-0.69, -13.9) * mm});
            skArc(sketch, "E2041", {"start": v(-0.69, -13.9) * mm, "mid": v(-0.5, -14) * mm, "end": v(-0.33, -14.1) * mm});
            skLineSegment(sketch, "E2042", {"start": v(2.82, -15.8) * mm, "end": v(3.97, -16.37) * mm});
            skLineSegment(sketch, "E2043", {"start": v(3.97, -16.37) * mm, "end": v(3.27, -16.85) * mm});
            skArc(sketch, "E2044", {"start": v(3.27, -16.85) * mm, "mid": v(3.13, -16.95) * mm, "end": v(3, -17.04) * mm});
            skArc(sketch, "E2045", {"start": v(3, -17.04) * mm, "mid": v(2.86, -17.14) * mm, "end": v(2.72, -17.24) * mm});
            skArc(sketch, "E2046", {"start": v(2.72, -17.24) * mm, "mid": v(2.6, -17.32) * mm, "end": v(2.5, -17.41) * mm});
            skArc(sketch, "E2047", {"start": v(2.5, -17.41) * mm, "mid": v(2.43, -17.46) * mm, "end": v(2.38, -17.5) * mm});
            skArc(sketch, "E2048", {"start": v(2.38, -17.5) * mm, "mid": v(2.34, -17.54) * mm, "end": v(2.3, -17.58) * mm});
            skArc(sketch, "E2049", {"start": v(2.3, -17.58) * mm, "mid": v(2.26, -17.6) * mm, "end": v(2.22, -17.64) * mm});
            skArc(sketch, "E2050", {"start": v(2.22, -17.64) * mm, "mid": v(2.18, -17.66) * mm, "end": v(2.15, -17.68) * mm});
            skArc(sketch, "E2051", {"start": v(2.15, -17.68) * mm, "mid": v(2.13, -17.69) * mm, "end": v(2.11, -17.7) * mm});
            skArc(sketch, "E2052", {"start": v(2.11, -17.7) * mm, "mid": v(2.09, -17.69) * mm, "end": v(2.07, -17.68) * mm});
            skArc(sketch, "E2053", {"start": v(2.07, -17.68) * mm, "mid": v(1.9, -17.57) * mm, "end": v(1.74, -17.47) * mm});
            skArc(sketch, "E2054", {"start": v(1.74, -17.47) * mm, "mid": v(1.56, -17.35) * mm, "end": v(1.37, -17.23) * mm});
            skArc(sketch, "E2055", {"start": v(1.37, -17.23) * mm, "mid": v(1.16, -17.08) * mm, "end": v(0.95, -16.94) * mm});
            skLineSegment(sketch, "E2056", {"start": v(0.95, -16.94) * mm, "end": v(-0.15, -16.18) * mm});
            skLineSegment(sketch, "E2057", {"start": v(-0.15, -16.18) * mm, "end": v(0.64, -15.7) * mm});
            skArc(sketch, "E2058", {"start": v(0.64, -15.7) * mm, "mid": v(0.8, -15.6) * mm, "end": v(0.95, -15.52) * mm});
            skArc(sketch, "E2059", {"start": v(0.95, -15.52) * mm, "mid": v(1.1, -15.44) * mm, "end": v(1.23, -15.36) * mm});
            skArc(sketch, "E2060", {"start": v(1.23, -15.36) * mm, "mid": v(1.35, -15.3) * mm, "end": v(1.47, -15.24) * mm});
            skArc(sketch, "E2061", {"start": v(1.47, -15.24) * mm, "mid": v(1.51, -15.22) * mm, "end": v(1.55, -15.22) * mm});
            skArc(sketch, "E2062", {"start": v(1.55, -15.22) * mm, "mid": v(1.6, -15.22) * mm, "end": v(1.63, -15.23) * mm});
            skArc(sketch, "E2063", {"start": v(1.63, -15.23) * mm, "mid": v(1.8, -15.3) * mm, "end": v(1.97, -15.38) * mm});
            skArc(sketch, "E2064", {"start": v(1.97, -15.38) * mm, "mid": v(2.17, -15.48) * mm, "end": v(2.37, -15.57) * mm});
            skArc(sketch, "E2065", {"start": v(2.37, -15.57) * mm, "mid": v(2.6, -15.68) * mm, "end": v(2.82, -15.8) * mm});
            skArc(sketch, "E2066", {"start": v(9.82, -15.76) * mm, "mid": v(9.9, -15.8) * mm, "end": v(9.97, -15.85) * mm});
            skArc(sketch, "E2067", {"start": v(9.97, -15.85) * mm, "mid": v(10.06, -15.9) * mm, "end": v(10.13, -15.96) * mm});
            skArc(sketch, "E2068", {"start": v(10.13, -15.96) * mm, "mid": v(10.2, -16) * mm, "end": v(10.28, -16.06) * mm});
            skArc(sketch, "E2069", {"start": v(10.28, -16.06) * mm, "mid": v(10.32, -16.1) * mm, "end": v(10.37, -16.15) * mm});
            skArc(sketch, "E2070", {"start": v(10.37, -16.15) * mm, "mid": v(10.42, -16.21) * mm, "end": v(10.48, -16.28) * mm});
            skArc(sketch, "E2071", {"start": v(10.48, -16.28) * mm, "mid": v(10.48, -16.3) * mm, "end": v(10.48, -16.33) * mm});
            skArc(sketch, "E2072", {"start": v(10.48, -16.33) * mm, "mid": v(10.45, -16.35) * mm, "end": v(10.42, -16.36) * mm});
            skArc(sketch, "E2073", {"start": v(10.42, -16.36) * mm, "mid": v(10.3, -16.39) * mm, "end": v(10.19, -16.41) * mm});
            skArc(sketch, "E2074", {"start": v(10.19, -16.41) * mm, "mid": v(9.83, -16.45) * mm, "end": v(9.48, -16.44) * mm});
            skArc(sketch, "E2075", {"start": v(9.48, -16.44) * mm, "mid": v(8.86, -16.37) * mm, "end": v(8.24, -16.28) * mm});
            skArc(sketch, "E2076", {"start": v(8.24, -16.28) * mm, "mid": v(7.6, -16.17) * mm, "end": v(6.97, -16.05) * mm});
            skArc(sketch, "E2077", {"start": v(6.97, -16.05) * mm, "mid": v(6.86, -15.98) * mm, "end": v(6.81, -15.86) * mm});
            skArc(sketch, "E2078", {"start": v(6.81, -15.86) * mm, "mid": v(6.82, -15.84) * mm, "end": v(6.83, -15.83) * mm});
            skArc(sketch, "E2079", {"start": v(6.83, -15.83) * mm, "mid": v(6.87, -15.8) * mm, "end": v(6.92, -15.79) * mm});
            skArc(sketch, "E2080", {"start": v(6.92, -15.79) * mm, "mid": v(6.97, -15.76) * mm, "end": v(7.03, -15.74) * mm});
            skArc(sketch, "E2081", {"start": v(7.03, -15.74) * mm, "mid": v(7.1, -15.72) * mm, "end": v(7.17, -15.7) * mm});
            skArc(sketch, "E2082", {"start": v(7.17, -15.7) * mm, "mid": v(7.24, -15.68) * mm, "end": v(7.32, -15.66) * mm});
            skArc(sketch, "E2083", {"start": v(7.32, -15.66) * mm, "mid": v(7.4, -15.64) * mm, "end": v(7.48, -15.62) * mm});
            skArc(sketch, "E2084", {"start": v(7.48, -15.62) * mm, "mid": v(7.55, -15.6) * mm, "end": v(7.62, -15.59) * mm});
            skArc(sketch, "E2085", {"start": v(7.62, -15.59) * mm, "mid": v(7.67, -15.57) * mm, "end": v(7.72, -15.56) * mm});
            skArc(sketch, "E2086", {"start": v(7.72, -15.56) * mm, "mid": v(7.92, -15.52) * mm, "end": v(8.14, -15.5) * mm});
            skArc(sketch, "E2087", {"start": v(8.14, -15.5) * mm, "mid": v(8.46, -15.52) * mm, "end": v(8.79, -15.55) * mm});
            skArc(sketch, "E2088", {"start": v(8.79, -15.55) * mm, "mid": v(9.11, -15.59) * mm, "end": v(9.43, -15.64) * mm});
            skArc(sketch, "E2089", {"start": v(9.43, -15.64) * mm, "mid": v(9.63, -15.69) * mm, "end": v(9.82, -15.76) * mm});
            skArc(sketch, "E2090", {"start": v(-3.45, -16.17) * mm, "mid": v(-3.3, -16.27) * mm, "end": v(-3.13, -16.36) * mm});
            skArc(sketch, "E2091", {"start": v(-3.13, -16.36) * mm, "mid": v(-3, -16.45) * mm, "end": v(-2.86, -16.53) * mm});
            skArc(sketch, "E2092", {"start": v(-2.86, -16.53) * mm, "mid": v(-2.75, -16.6) * mm, "end": v(-2.64, -16.68) * mm});
            skArc(sketch, "E2093", {"start": v(-2.64, -16.68) * mm, "mid": v(-2.62, -16.7) * mm, "end": v(-2.62, -16.72) * mm});
            skArc(sketch, "E2094", {"start": v(-2.62, -16.72) * mm, "mid": v(-2.62, -16.74) * mm, "end": v(-2.64, -16.76) * mm});
            skArc(sketch, "E2095", {"start": v(-2.64, -16.76) * mm, "mid": v(-2.72, -16.82) * mm, "end": v(-2.8, -16.88) * mm});
            skArc(sketch, "E2096", {"start": v(-2.8, -16.88) * mm, "mid": v(-2.9, -16.95) * mm, "end": v(-3, -17.01) * mm});
            skArc(sketch, "E2097", {"start": v(-3, -17.01) * mm, "mid": v(-3.13, -17.09) * mm, "end": v(-3.25, -17.16) * mm});
            skArc(sketch, "E2098", {"start": v(-3.25, -17.16) * mm, "mid": v(-3.45, -17.28) * mm, "end": v(-3.65, -17.4) * mm});
            skArc(sketch, "E2099", {"start": v(-3.65, -17.4) * mm, "mid": v(-3.74, -17.43) * mm, "end": v(-3.83, -17.46) * mm});
            skArc(sketch, "E2100", {"start": v(-3.83, -17.46) * mm, "mid": v(-3.9, -17.47) * mm, "end": v(-3.96, -17.45) * mm});
            skArc(sketch, "E2101", {"start": v(-3.96, -17.45) * mm, "mid": v(-4.05, -17.42) * mm, "end": v(-4.13, -17.37) * mm});
            skArc(sketch, "E2102", {"start": v(-4.13, -17.37) * mm, "mid": v(-4.2, -17.33) * mm, "end": v(-4.26, -17.29) * mm});
            skArc(sketch, "E2103", {"start": v(-4.26, -17.29) * mm, "mid": v(-4.37, -17.22) * mm, "end": v(-4.48, -17.15) * mm});
            skArc(sketch, "E2104", {"start": v(-4.48, -17.15) * mm, "mid": v(-4.6, -17.08) * mm, "end": v(-4.73, -17) * mm});
            skArc(sketch, "E2105", {"start": v(-4.73, -17) * mm, "mid": v(-4.85, -16.93) * mm, "end": v(-4.97, -16.86) * mm});
            skArc(sketch, "E2106", {"start": v(-4.97, -16.85) * mm, "mid": v(-5.09, -16.79) * mm, "end": v(-5.2, -16.72) * mm});
            skArc(sketch, "E2107", {"start": v(-5.2, -16.72) * mm, "mid": v(-5.3, -16.65) * mm, "end": v(-5.4, -16.6) * mm});
            skArc(sketch, "E2108", {"start": v(-5.4, -16.6) * mm, "mid": v(-5.47, -16.54) * mm, "end": v(-5.55, -16.48) * mm});
            skArc(sketch, "E2109", {"start": v(-5.55, -16.48) * mm, "mid": v(-5.56, -16.47) * mm, "end": v(-5.57, -16.45) * mm});
            skArc(sketch, "E2110", {"start": v(-5.57, -16.45) * mm, "mid": v(-5.56, -16.41) * mm, "end": v(-5.53, -16.38) * mm});
            skArc(sketch, "E2111", {"start": v(-5.53, -16.38) * mm, "mid": v(-5.27, -16.21) * mm, "end": v(-5.02, -16.05) * mm});
            skArc(sketch, "E2112", {"start": v(-5.02, -16.05) * mm, "mid": v(-4.77, -15.89) * mm, "end": v(-4.51, -15.73) * mm});
            skArc(sketch, "E2113", {"start": v(-4.51, -15.73) * mm, "mid": v(-4.45, -15.7) * mm, "end": v(-4.38, -15.7) * mm});
            skArc(sketch, "E2114", {"start": v(-4.38, -15.7) * mm, "mid": v(-4.35, -15.7) * mm, "end": v(-4.32, -15.7) * mm});
            skArc(sketch, "E2115", {"start": v(-4.32, -15.7) * mm, "mid": v(-4.2, -15.77) * mm, "end": v(-4.07, -15.83) * mm});
            skArc(sketch, "E2116", {"start": v(-4.07, -15.83) * mm, "mid": v(-3.92, -15.9) * mm, "end": v(-3.78, -15.99) * mm});
            skArc(sketch, "E2117", {"start": v(-3.78, -15.99) * mm, "mid": v(-3.61, -16.08) * mm, "end": v(-3.45, -16.17) * mm});
            skArc(sketch, "E2118", {"start": v(-8.5, -16.72) * mm, "mid": v(-8.35, -16.76) * mm, "end": v(-8.21, -16.81) * mm});
            skArc(sketch, "E2119", {"start": v(-8.21, -16.81) * mm, "mid": v(-8.1, -16.86) * mm, "end": v(-8, -16.9) * mm});
            skArc(sketch, "E2120", {"start": v(-8, -16.9) * mm, "mid": v(-7.91, -16.95) * mm, "end": v(-7.83, -17) * mm});
            skArc(sketch, "E2121", {"start": v(-7.83, -17) * mm, "mid": v(-7.82, -17) * mm, "end": v(-7.83, -17.03) * mm});
            skArc(sketch, "E2122", {"start": v(-7.83, -17.03) * mm, "mid": v(-7.93, -17.12) * mm, "end": v(-8.04, -17.19) * mm});
            skArc(sketch, "E2123", {"start": v(-8.04, -17.19) * mm, "mid": v(-8.33, -17.35) * mm, "end": v(-8.62, -17.5) * mm});
            skArc(sketch, "E2124", {"start": v(-8.62, -17.5) * mm, "mid": v(-8.94, -17.66) * mm, "end": v(-9.26, -17.82) * mm});
            skArc(sketch, "E2125", {"start": v(-9.26, -17.82) * mm, "mid": v(-9.56, -17.96) * mm, "end": v(-9.86, -18.1) * mm});
            skArc(sketch, "E2126", {"start": v(-9.86, -18.1) * mm, "mid": v(-10.2, -18.23) * mm, "end": v(-10.54, -18.35) * mm});
            skArc(sketch, "E2127", {"start": v(-10.54, -18.35) * mm, "mid": v(-10.93, -18.48) * mm, "end": v(-11.33, -18.6) * mm});
            skArc(sketch, "E2128", {"start": v(-11.33, -18.6) * mm, "mid": v(-11.7, -18.7) * mm, "end": v(-12.08, -18.78) * mm});
            skArc(sketch, "E2129", {"start": v(-12.08, -18.78) * mm, "mid": v(-12.31, -18.82) * mm, "end": v(-12.55, -18.83) * mm});
            skArc(sketch, "E2130", {"start": v(-12.55, -18.83) * mm, "mid": v(-12.62, -18.83) * mm, "end": v(-12.7, -18.82) * mm});
            skArc(sketch, "E2131", {"start": v(-12.7, -18.82) * mm, "mid": v(-12.73, -18.8) * mm, "end": v(-12.76, -18.78) * mm});
            skArc(sketch, "E2132", {"start": v(-12.76, -18.78) * mm, "mid": v(-12.79, -18.75) * mm, "end": v(-12.8, -18.7) * mm});
            skArc(sketch, "E2133", {"start": v(-12.8, -18.7) * mm, "mid": v(-12.8, -18.62) * mm, "end": v(-12.8, -18.54) * mm});
            skArc(sketch, "E2134", {"start": v(-12.8, -18.54) * mm, "mid": v(-12.8, -18.38) * mm, "end": v(-12.77, -18.22) * mm});
            skArc(sketch, "E2135", {"start": v(-12.77, -18.22) * mm, "mid": v(-12.71, -18.05) * mm, "end": v(-12.64, -17.87) * mm});
            skArc(sketch, "E2136", {"start": v(-12.64, -17.87) * mm, "mid": v(-12.55, -17.7) * mm, "end": v(-12.45, -17.53) * mm});
            skArc(sketch, "E2137", {"start": v(-12.45, -17.53) * mm, "mid": v(-12.34, -17.37) * mm, "end": v(-12.2, -17.23) * mm});
            skArc(sketch, "E2138", {"start": v(-12.2, -17.23) * mm, "mid": v(-11.88, -16.94) * mm, "end": v(-11.5, -16.71) * mm});
            skArc(sketch, "E2139", {"start": v(-11.5, -16.71) * mm, "mid": v(-11.09, -16.55) * mm, "end": v(-10.65, -16.45) * mm});
            skArc(sketch, "E2140", {"start": v(-10.65, -16.45) * mm, "mid": v(-10.14, -16.41) * mm, "end": v(-9.64, -16.45) * mm});
            skArc(sketch, "E2141", {"start": v(-9.64, -16.45) * mm, "mid": v(-9.06, -16.56) * mm, "end": v(-8.5, -16.72) * mm});
            skArc(sketch, "E2142", {"start": v(5.53, -17.02) * mm, "mid": v(6.02, -17.18) * mm, "end": v(6.52, -17.33) * mm});
            skArc(sketch, "E2143", {"start": v(6.52, -17.33) * mm, "mid": v(6.94, -17.43) * mm, "end": v(7.36, -17.5) * mm});
            skArc(sketch, "E2144", {"start": v(7.36, -17.5) * mm, "mid": v(7.8, -17.55) * mm, "end": v(8.26, -17.58) * mm});
            skArc(sketch, "E2145", {"start": v(8.26, -17.58) * mm, "mid": v(8.83, -17.58) * mm, "end": v(9.4, -17.57) * mm});
            skArc(sketch, "E2146", {"start": v(9.4, -17.57) * mm, "mid": v(9.77, -17.56) * mm, "end": v(10.14, -17.55) * mm});
            skArc(sketch, "E2147", {"start": v(10.14, -17.55) * mm, "mid": v(10.36, -17.55) * mm, "end": v(10.58, -17.56) * mm});
            skArc(sketch, "E2148", {"start": v(10.58, -17.56) * mm, "mid": v(10.72, -17.57) * mm, "end": v(10.86, -17.58) * mm});
            skArc(sketch, "E2149", {"start": v(10.86, -17.58) * mm, "mid": v(10.9, -17.6) * mm, "end": v(10.9, -17.64) * mm});
            skArc(sketch, "E2150", {"start": v(10.9, -17.64) * mm, "mid": v(10.9, -17.67) * mm, "end": v(10.9, -17.7) * mm});
            skArc(sketch, "E2151", {"start": v(10.9, -17.7) * mm, "mid": v(10.88, -17.78) * mm, "end": v(10.87, -17.86) * mm});
            skArc(sketch, "E2152", {"start": v(10.87, -17.86) * mm, "mid": v(10.84, -17.95) * mm, "end": v(10.82, -18.03) * mm});
            skArc(sketch, "E2153", {"start": v(10.82, -18.03) * mm, "mid": v(10.8, -18.13) * mm, "end": v(10.77, -18.22) * mm});
            skArc(sketch, "E2154", {"start": v(10.77, -18.22) * mm, "mid": v(10.66, -18.5) * mm, "end": v(10.5, -18.75) * mm});
            skArc(sketch, "E2155", {"start": v(10.5, -18.75) * mm, "mid": v(10.3, -19) * mm, "end": v(10.06, -19.2) * mm});
            skArc(sketch, "E2156", {"start": v(10.06, -19.2) * mm, "mid": v(9.76, -19.4) * mm, "end": v(9.44, -19.57) * mm});
            skArc(sketch, "E2157", {"start": v(9.44, -19.57) * mm, "mid": v(9.06, -19.73) * mm, "end": v(8.67, -19.85) * mm});
            skArc(sketch, "E2158", {"start": v(8.67, -19.85) * mm, "mid": v(8.08, -19.96) * mm, "end": v(7.48, -19.97) * mm});
            skArc(sketch, "E2159", {"start": v(7.48, -19.97) * mm, "mid": v(6.76, -19.89) * mm, "end": v(6.06, -19.74) * mm});
            skArc(sketch, "E2160", {"start": v(6.06, -19.74) * mm, "mid": v(5.31, -19.51) * mm, "end": v(4.59, -19.22) * mm});
            skArc(sketch, "E2161", {"start": v(4.59, -19.22) * mm, "mid": v(3.88, -18.85) * mm, "end": v(3.2, -18.43) * mm});
            skLineSegment(sketch, "E2162", {"start": v(3.2, -18.43) * mm, "end": v(2.8, -18.14) * mm});
            skLineSegment(sketch, "E2163", {"start": v(2.8, -18.14) * mm, "end": v(3.02, -17.92) * mm});
            skArc(sketch, "E2164", {"start": v(3.02, -17.92) * mm, "mid": v(3.13, -17.82) * mm, "end": v(3.25, -17.72) * mm});
            skArc(sketch, "E2165", {"start": v(3.25, -17.72) * mm, "mid": v(3.57, -17.5) * mm, "end": v(3.9, -17.27) * mm});
            skArc(sketch, "E2166", {"start": v(3.9, -17.27) * mm, "mid": v(4.23, -17.03) * mm, "end": v(4.58, -16.8) * mm});
            skArc(sketch, "E2167", {"start": v(4.58, -16.8) * mm, "mid": v(4.64, -16.76) * mm, "end": v(4.7, -16.74) * mm});
            skArc(sketch, "E2168", {"start": v(4.7, -16.74) * mm, "mid": v(4.71, -16.74) * mm, "end": v(4.72, -16.74) * mm});
            skArc(sketch, "E2169", {"start": v(4.72, -16.74) * mm, "mid": v(4.84, -16.78) * mm, "end": v(4.96, -16.82) * mm});
            skArc(sketch, "E2170", {"start": v(4.96, -16.82) * mm, "mid": v(5.1, -16.87) * mm, "end": v(5.22, -16.91) * mm});
            skArc(sketch, "E2171", {"start": v(5.22, -16.91) * mm, "mid": v(5.38, -16.97) * mm, "end": v(5.53, -17.02) * mm});
            skArc(sketch, "E2172", {"start": v(-0.43, -18.03) * mm, "mid": v(-0.2, -18.17) * mm, "end": v(0.01, -18.31) * mm});
            skArc(sketch, "E2173", {"start": v(0.01, -18.31) * mm, "mid": v(0.2, -18.43) * mm, "end": v(0.38, -18.56) * mm});
            skArc(sketch, "E2174", {"start": v(0.38, -18.56) * mm, "mid": v(0.54, -18.67) * mm, "end": v(0.7, -18.78) * mm});
            skArc(sketch, "E2175", {"start": v(0.7, -18.78) * mm, "mid": v(0.71, -18.8) * mm, "end": v(0.72, -18.83) * mm});
            skArc(sketch, "E2176", {"start": v(0.72, -18.83) * mm, "mid": v(0.7, -18.87) * mm, "end": v(0.68, -18.91) * mm});
            skArc(sketch, "E2177", {"start": v(0.68, -18.91) * mm, "mid": v(0.38, -19.18) * mm, "end": v(0.07, -19.44) * mm});
            skArc(sketch, "E2178", {"start": v(0.07, -19.44) * mm, "mid": v(-0.22, -19.7) * mm, "end": v(-0.52, -19.94) * mm});
            skArc(sketch, "E2179", {"start": v(-0.52, -19.94) * mm, "mid": v(-0.58, -19.99) * mm, "end": v(-0.65, -20.01) * mm});
            skArc(sketch, "E2180", {"start": v(-0.65, -20.01) * mm, "mid": v(-0.7, -20.01) * mm, "end": v(-0.75, -19.99) * mm});
            skArc(sketch, "E2181", {"start": v(-0.75, -19.99) * mm, "mid": v(-1.33, -19.54) * mm, "end": v(-1.9, -19.08) * mm});
            skArc(sketch, "E2182", {"start": v(-1.9, -19.08) * mm, "mid": v(-2.48, -18.63) * mm, "end": v(-3.05, -18.18) * mm});
            skArc(sketch, "E2183", {"start": v(-3.05, -18.18) * mm, "mid": v(-3.08, -18.14) * mm, "end": v(-3.1, -18.08) * mm});
            skArc(sketch, "E2184", {"start": v(-3.1, -18.08) * mm, "mid": v(-3.08, -18.02) * mm, "end": v(-3.03, -17.97) * mm});
            skArc(sketch, "E2185", {"start": v(-3.03, -17.97) * mm, "mid": v(-2.73, -17.79) * mm, "end": v(-2.44, -17.61) * mm});
            skArc(sketch, "E2186", {"start": v(-2.44, -17.61) * mm, "mid": v(-2.14, -17.44) * mm, "end": v(-1.84, -17.27) * mm});
            skArc(sketch, "E2187", {"start": v(-1.84, -17.27) * mm, "mid": v(-1.77, -17.25) * mm, "end": v(-1.69, -17.26) * mm});
            skArc(sketch, "E2188", {"start": v(-1.69, -17.26) * mm, "mid": v(-1.65, -17.28) * mm, "end": v(-1.6, -17.3) * mm});
            skArc(sketch, "E2189", {"start": v(-1.6, -17.3) * mm, "mid": v(-1.44, -17.4) * mm, "end": v(-1.27, -17.5) * mm});
            skArc(sketch, "E2190", {"start": v(-1.27, -17.5) * mm, "mid": v(-1.07, -17.62) * mm, "end": v(-0.87, -17.75) * mm});
            skArc(sketch, "E2191", {"start": v(-0.87, -17.75) * mm, "mid": v(-0.65, -17.89) * mm, "end": v(-0.43, -18.03) * mm});
            skArc(sketch, "E2192", {"start": v(-6.18, -17.9) * mm, "mid": v(-6.02, -18) * mm, "end": v(-5.87, -18.1) * mm});
            skArc(sketch, "E2193", {"start": v(-5.87, -18.1) * mm, "mid": v(-5.74, -18.19) * mm, "end": v(-5.61, -18.27) * mm});
            skArc(sketch, "E2194", {"start": v(-5.61, -18.27) * mm, "mid": v(-5.5, -18.35) * mm, "end": v(-5.4, -18.43) * mm});
            skArc(sketch, "E2195", {"start": v(-5.4, -18.43) * mm, "mid": v(-5.38, -18.44) * mm, "end": v(-5.38, -18.46) * mm});
            skArc(sketch, "E2196", {"start": v(-5.38, -18.46) * mm, "mid": v(-5.4, -18.54) * mm, "end": v(-5.46, -18.59) * mm});
            skArc(sketch, "E2197", {"start": v(-5.46, -18.59) * mm, "mid": v(-6.09, -18.87) * mm, "end": v(-6.72, -19.15) * mm});
            skArc(sketch, "E2198", {"start": v(-6.72, -19.15) * mm, "mid": v(-7.3, -19.4) * mm, "end": v(-7.88, -19.65) * mm});
            skArc(sketch, "E2199", {"start": v(-7.88, -19.65) * mm, "mid": v(-8.23, -19.78) * mm, "end": v(-8.57, -19.88) * mm});
            skArc(sketch, "E2200", {"start": v(-8.57, -19.88) * mm, "mid": v(-9.11, -20) * mm, "end": v(-9.65, -20.1) * mm});
            skArc(sketch, "E2201", {"start": v(-9.65, -20.1) * mm, "mid": v(-10.15, -20.14) * mm, "end": v(-10.64, -20.14) * mm});
            skArc(sketch, "E2202", {"start": v(-10.64, -20.14) * mm, "mid": v(-11.07, -20.1) * mm, "end": v(-11.5, -20.03) * mm});
            skArc(sketch, "E2203", {"start": v(-11.5, -20.03) * mm, "mid": v(-11.83, -19.93) * mm, "end": v(-12.14, -19.77) * mm});
            skLineSegment(sketch, "E2204", {"start": v(-12.14, -19.77) * mm, "end": v(-12.48, -19.56) * mm});
            skLineSegment(sketch, "E2205", {"start": v(-12.48, -19.56) * mm, "end": v(-11.67, -19.4) * mm});
            skArc(sketch, "E2206", {"start": v(-11.67, -19.4) * mm, "mid": v(-11.5, -19.36) * mm, "end": v(-11.32, -19.32) * mm});
            skArc(sketch, "E2207", {"start": v(-11.32, -19.32) * mm, "mid": v(-11.14, -19.28) * mm, "end": v(-10.95, -19.23) * mm});
            skArc(sketch, "E2208", {"start": v(-10.95, -19.23) * mm, "mid": v(-10.79, -19.19) * mm, "end": v(-10.62, -19.14) * mm});
            skArc(sketch, "E2209", {"start": v(-10.62, -19.14) * mm, "mid": v(-10.5, -19.1) * mm, "end": v(-10.38, -19.07) * mm});
            skArc(sketch, "E2210", {"start": v(-10.38, -19.07) * mm, "mid": v(-10.1, -18.97) * mm, "end": v(-9.84, -18.86) * mm});
            skArc(sketch, "E2211", {"start": v(-9.84, -18.86) * mm, "mid": v(-9.43, -18.66) * mm, "end": v(-9.03, -18.47) * mm});
            skArc(sketch, "E2212", {"start": v(-9.03, -18.47) * mm, "mid": v(-8.61, -18.26) * mm, "end": v(-8.2, -18.05) * mm});
            skArc(sketch, "E2213", {"start": v(-8.2, -18.05) * mm, "mid": v(-7.9, -17.88) * mm, "end": v(-7.61, -17.7) * mm});
            skArc(sketch, "E2214", {"start": v(-7.61, -17.7) * mm, "mid": v(-7.52, -17.65) * mm, "end": v(-7.43, -17.6) * mm});
            skArc(sketch, "E2215", {"start": v(-7.43, -17.6) * mm, "mid": v(-7.34, -17.54) * mm, "end": v(-7.26, -17.5) * mm});
            skArc(sketch, "E2216", {"start": v(-7.26, -17.5) * mm, "mid": v(-7.18, -17.46) * mm, "end": v(-7.11, -17.42) * mm});
            skArc(sketch, "E2217", {"start": v(-7.11, -17.42) * mm, "mid": v(-7.09, -17.41) * mm, "end": v(-7.06, -17.4) * mm});
            skArc(sketch, "E2218", {"start": v(-7.06, -17.4) * mm, "mid": v(-7.03, -17.4) * mm, "end": v(-7, -17.42) * mm});
            skArc(sketch, "E2219", {"start": v(-7, -17.42) * mm, "mid": v(-6.88, -17.49) * mm, "end": v(-6.76, -17.55) * mm});
            skArc(sketch, "E2220", {"start": v(-6.76, -17.55) * mm, "mid": v(-6.63, -17.63) * mm, "end": v(-6.49, -17.71) * mm});
            skArc(sketch, "E2221", {"start": v(-6.49, -17.71) * mm, "mid": v(-6.33, -17.8) * mm, "end": v(-6.18, -17.9) * mm});
            skSolve(sketch);
        }
        {
            var Q0;
            Q0=qSketchRegion(id+"F12",true);
            extrude(context, id + "F13", {"entities" : qUnion([Q0]), "operationType" : NewBodyOperationType.ADD, "depth" : 1.59 * mm, "offsetDistance" : 25.4 * mm});
        }
        {
            var Q0;
            {var subQ481=makeQuery(id+"F3.opExtrude","SWEPT_FACE",FACE,{"disambiguationData":[OSD([sQuery(id+"F2.wireOp",EDGE,"E5.bottom")])]});Q0=makeQuery(id+"F13.boolean.opBoolean","SPLIT",FACE,{"disambiguationData":[TD([subQ481])],"derivedFrom":makeQuery(id+"F11.boolean.opBoolean","SPLIT",FACE,{"disambiguationData":[TD([subQ481])],"derivedFrom":makeQuery(id+"F9.boolean.opBoolean","SPLIT",FACE,{"disambiguationData":[TD([subQ481])],"derivedFrom":makeQuery(id+"F7.boolean.opBoolean","SPLIT",FACE,{"disambiguationData":[TD([subQ481])],"derivedFrom":makeQuery(id+"F5.boolean.opBoolean","SPLIT",FACE,{"disambiguationData":[TD([subQ481])],"derivedFrom":makeQuery(id+"F1.opExtrude","CAP_FACE",FACE,{"disambiguationData":[OSD([sQuery(id+"F0.wireOp",EDGE,"E0.bottom"),sQuery(id+"F0.wireOp",EDGE,"E0.top"),sQuery(id+"F0.wireOp",EDGE,"E0.left"),sQuery(id+"F0.wireOp",EDGE,"E0.right"),sQuery(id+"F0.wireOp",EDGE,"E1.filletArc"),sQuery(id+"F0.wireOp",EDGE,"E2.filletArc"),sQuery(id+"F0.wireOp",EDGE,"E3.filletArc"),sQuery(id+"F0.wireOp",EDGE,"E4.filletArc")])],"isStart":false})})})})})});}
            var sketch = newSketch(context, id + "F14", { "sketchPlane" : qUnion([Q0])});
            skText(sketch, "E2222", { "text": "take a book", "fontName": "RobotoSlab-Regular.ttf"});
            skText(sketch, "E2223", { "text": "leave a book", "fontName": "RobotoSlab-Regular.ttf"});
            const initialGuessF14  = {"E2222": [-0.0635, -0.03175, 1, 0, 0.00838], "E2223": [-0.00506, -0.04128, 1, 0, 0.00838]};
            skSetInitialGuess(sketch, initialGuessF14);
            skSolve(sketch);
        }
        {
            var Q0;
            Q0=qSketchRegion(id+"F14",true);
            extrude(context, id + "F15", {"entities" : qUnion([Q0]), "operationType" : NewBodyOperationType.ADD, "depth" : 1.59 * mm, "offsetDistance" : 25.4 * mm});
        }
        {
            var Q0;
            {var subQ538=makeQuery(id+"F3.opExtrude","SWEPT_FACE",FACE,{"disambiguationData":[OSD([sQuery(id+"F2.wireOp",EDGE,"E5.bottom")])]});Q0=makeQuery(id+"F15.boolean.opBoolean","SPLIT",FACE,{"disambiguationData":[TD([subQ538])],"derivedFrom":makeQuery(id+"F13.boolean.opBoolean","SPLIT",FACE,{"disambiguationData":[TD([subQ538])],"derivedFrom":makeQuery(id+"F11.boolean.opBoolean","SPLIT",FACE,{"disambiguationData":[TD([subQ538])],"derivedFrom":makeQuery(id+"F9.boolean.opBoolean","SPLIT",FACE,{"disambiguationData":[TD([subQ538])],"derivedFrom":makeQuery(id+"F7.boolean.opBoolean","SPLIT",FACE,{"disambiguationData":[TD([subQ538])],"derivedFrom":makeQuery(id+"F5.boolean.opBoolean","SPLIT",FACE,{"disambiguationData":[TD([subQ538])],"derivedFrom":makeQuery(id+"F1.opExtrude","CAP_FACE",FACE,{"disambiguationData":[OSD([sQuery(id+"F0.wireOp",EDGE,"E0.bottom"),sQuery(id+"F0.wireOp",EDGE,"E0.top"),sQuery(id+"F0.wireOp",EDGE,"E0.left"),sQuery(id+"F0.wireOp",EDGE,"E0.right"),sQuery(id+"F0.wireOp",EDGE,"E1.filletArc"),sQuery(id+"F0.wireOp",EDGE,"E2.filletArc"),sQuery(id+"F0.wireOp",EDGE,"E3.filletArc"),sQuery(id+"F0.wireOp",EDGE,"E4.filletArc")])],"isStart":false})})})})})})});}
            var sketch = newSketch(context, id + "F16", { "sketchPlane" : qUnion([Q0])});
            skCircle(sketch, "E2224", {"center": v(-65.88, 40.48) * mm, "radius": 1.98 * mm});
            skLineSegment(sketch, "E2225.bottom", {"start": v(-65.88, 40.48) * mm, "end": v(65.88, 40.48) * mm, "construction": true});
            skLineSegment(sketch, "E2225.top", {"start": v(-65.88, -40.48) * mm, "end": v(65.88, -40.48) * mm, "construction": true});
            skLineSegment(sketch, "E2225.left", {"start": v(-65.88, 40.48) * mm, "end": v(-65.88, -40.48) * mm, "construction": true});
            skLineSegment(sketch, "E2225.right", {"start": v(65.88, 40.48) * mm, "end": v(65.88, -40.48) * mm, "construction": true});
            skPoint(sketch, "E2225.middle", {"position": v(0, 0) * mm});
            skCircle(sketch, "E2226", {"center": v(65.88, 40.48) * mm, "radius": 1.98 * mm});
            skCircle(sketch, "E2227", {"center": v(65.88, -40.48) * mm, "radius": 1.98 * mm});
            skCircle(sketch, "E2228", {"center": v(-65.88, -40.48) * mm, "radius": 1.98 * mm});
            skSolve(sketch);
        }
        {
            var Q0;
            Q0=qSketchRegion(id+"F16",true);
            extrude(context, id + "F17", {"entities" : qUnion([Q0]), "operationType" : NewBodyOperationType.REMOVE, "endBound" : BoundingType.THROUGH_ALL, "oppositeDirection" : true, "depth" : 25.4 * mm, "offsetDistance" : 25.4 * mm});
        }
        {
            var Q0;
            Q0=makeQuery(id+"F1.opExtrude","CAP_FACE",FACE,{"disambiguationData":[OSD([sQuery(id+"F0.wireOp",EDGE,"E0.bottom"),sQuery(id+"F0.wireOp",EDGE,"E0.top"),sQuery(id+"F0.wireOp",EDGE,"E0.left"),sQuery(id+"F0.wireOp",EDGE,"E0.right"),sQuery(id+"F0.wireOp",EDGE,"E1.filletArc"),sQuery(id+"F0.wireOp",EDGE,"E2.filletArc"),sQuery(id+"F0.wireOp",EDGE,"E3.filletArc"),sQuery(id+"F0.wireOp",EDGE,"E4.filletArc")])],"isStart":true});
            var sketch = newSketch(context, id + "F18", { "sketchPlane" : qUnion([Q0])});
            skArc(sketch, "E2229", {"start": v(-51.76, 55.67) * mm, "mid": v(-57.88, 60.64) * mm, "end": v(-61.79, 53.8) * mm});
            skArc(sketch, "E2230", {"start": v(-55.13, 53.9) * mm, "mid": v(-56.44, 57.97) * mm, "end": v(-59.24, 54.72) * mm});
            skArc(sketch, "E2231", {"start": v(-61.79, 53.8) * mm, "mid": v(-60.05, 52.98) * mm, "end": v(-59.24, 54.72) * mm});
            skLineSegment(sketch, "E2232", {"start": v(-56.93, 55.56) * mm, "end": v(-61.79, 53.8) * mm, "construction": true});
            skLineSegment(sketch, "E2233", {"start": v(-56.93, 55.56) * mm, "end": v(-67.77, 55.56) * mm, "construction": true});
            skArc(sketch, "E2234", {"start": v(-51.76, 55.67) * mm, "mid": v(-50.64, 52.58) * mm, "end": v(-47.87, 50.8) * mm});
            skArc(sketch, "E2235", {"start": v(-58.52, 50.8) * mm, "mid": v(-56.76, 52.28) * mm, "end": v(-55.13, 53.9) * mm});
            skLineSegment(sketch, "E2236", {"start": v(-58.52, 50.8) * mm, "end": v(-47.87, 50.8) * mm});
            skLineSegment(sketch, "E2237", {"start": v(0, 50.8) * mm, "end": v(0, 58.15) * mm, "construction": true});
            skLineSegment(sketch, "E2238.MirrorCS", {"start": v(56.93, 55.56) * mm, "end": v(61.79, 53.8) * mm, "construction": true});
            skLineSegment(sketch, "E2239.MirrorCS", {"start": v(56.93, 55.56) * mm, "end": v(67.77, 55.56) * mm, "construction": true});
            skArc(sketch, "E2240.MirrorCS", {"start": v(61.79, 53.8) * mm, "mid": v(60.05, 52.98) * mm, "end": v(59.24, 54.72) * mm});
            skArc(sketch, "E2241.MirrorCS", {"start": v(58.52, 50.8) * mm, "mid": v(56.76, 52.28) * mm, "end": v(55.13, 53.9) * mm});
            skArc(sketch, "E2242.MirrorCS", {"start": v(55.13, 53.9) * mm, "mid": v(56.44, 57.97) * mm, "end": v(59.24, 54.72) * mm});
            skArc(sketch, "E2243.MirrorCS", {"start": v(51.76, 55.67) * mm, "mid": v(57.88, 60.64) * mm, "end": v(61.79, 53.8) * mm});
            skArc(sketch, "E2244.MirrorCS", {"start": v(51.76, 55.67) * mm, "mid": v(50.64, 52.58) * mm, "end": v(47.87, 50.8) * mm});
            skLineSegment(sketch, "E2245.MirrorCS", {"start": v(58.52, 50.8) * mm, "end": v(47.87, 50.8) * mm});
            skSolve(sketch);
        }
        {
            var Q0;
            Q0=makeQuery(id+"F18.imprint","IMPRINT",FACE,{"disambiguationData":[TD([[makeQuery(id+"F18.imprint","IMPRINT",EDGE,{"derivedFrom":sQuery(id+"F18.wireOp",EDGE,"E2229")}),1.0]])]});
            var Q1;
            Q1=makeQuery(id+"F18.imprint","IMPRINT",FACE,{"disambiguationData":[TD([[makeQuery(id+"F18.imprint","IMPRINT",EDGE,{"derivedFrom":sQuery(id+"F18.wireOp",EDGE,"E2240.MirrorCS")}),-1.0]])]});
            extrude(context, id + "F19", {"entities" : qUnion([Q0, Q1]), "operationType" : NewBodyOperationType.ADD, "oppositeDirection" : true, "depth" : 3.17 * mm, "offsetDistance" : 25.4 * mm});
        }
        {
            var Q0;
            Q0=qCreatedBy(makeId("Front.planeOp"),FACE);
            var sketch = newSketch(context, id + "F20", { "sketchPlane" : qUnion([Q0])});
            skLineSegment(sketch, "E2246", {"start": v(-76.2, 69.85) * mm, "end": v(-70.97, 69.85) * mm});
            skLineSegment(sketch, "E2247", {"start": v(-76.2, 69.85) * mm, "end": v(-76.2, 76.2) * mm});
            skLineSegment(sketch, "E2248", {"start": v(-76.2, 76.2) * mm, "end": v(80.07, 76.2) * mm});
            skLineSegment(sketch, "E2249", {"start": v(-56.93, 55.56) * mm, "end": v(-56.93, 69.85) * mm, "construction": true});
            skLineSegment(sketch, "E2250", {"start": v(0, 50.8) * mm, "end": v(0, 61.94) * mm, "construction": true});
            skLineSegment(sketch, "E2251.bottom", {"start": v(80.07, 139.7) * mm, "end": v(86.42, 139.7) * mm});
            skLineSegment(sketch, "E2251.top", {"start": v(80.07, 44.45) * mm, "end": v(86.42, 44.45) * mm});
            skLineSegment(sketch, "E2251.left", {"start": v(80.07, 139.7) * mm, "end": v(80.07, 76.2) * mm});
            skLineSegment(sketch, "E2251.right", {"start": v(86.42, 139.7) * mm, "end": v(86.42, 44.45) * mm});
            skLineSegment(sketch, "E2252.trimOffspring", {"start": v(80.07, 69.85) * mm, "end": v(80.07, 44.45) * mm});
            skLineSegment(sketch, "E2253.0.0", {"start": v(-58.52, 50.8) * mm, "end": v(-47.87, 50.8) * mm, "construction": true});
            skArc(sketch, "E2253.0.1", {"start": v(-47.87, 50.8) * mm, "mid": v(-50.64, 52.58) * mm, "end": v(-51.76, 55.67) * mm, "construction": true});
            skArc(sketch, "E2253.0.2", {"start": v(-51.76, 55.67) * mm, "mid": v(-57.88, 60.64) * mm, "end": v(-61.79, 53.8) * mm, "construction": true});
            skArc(sketch, "E2253.0.3", {"start": v(-61.79, 53.8) * mm, "mid": v(-60.05, 52.98) * mm, "end": v(-59.24, 54.72) * mm, "construction": true});
            skArc(sketch, "E2253.0.4", {"start": v(-59.24, 54.72) * mm, "mid": v(-56.44, 57.97) * mm, "end": v(-55.13, 53.9) * mm, "construction": true});
            skArc(sketch, "E2253.0.5", {"start": v(-55.13, 53.9) * mm, "mid": v(-56.76, 52.28) * mm, "end": v(-58.52, 50.8) * mm, "construction": true});
            skArc(sketch, "E2253.1.0", {"start": v(58.52, 50.8) * mm, "mid": v(56.76, 52.28) * mm, "end": v(55.13, 53.9) * mm, "construction": true});
            skArc(sketch, "E2253.1.1", {"start": v(55.13, 53.9) * mm, "mid": v(56.44, 57.97) * mm, "end": v(59.24, 54.72) * mm, "construction": true});
            skArc(sketch, "E2253.1.2", {"start": v(59.24, 54.72) * mm, "mid": v(60.05, 52.98) * mm, "end": v(61.79, 53.8) * mm, "construction": true});
            skArc(sketch, "E2253.1.3", {"start": v(61.79, 53.8) * mm, "mid": v(57.88, 60.64) * mm, "end": v(51.76, 55.67) * mm, "construction": true});
            skArc(sketch, "E2253.1.4", {"start": v(51.76, 55.67) * mm, "mid": v(50.64, 52.58) * mm, "end": v(47.87, 50.8) * mm, "construction": true});
            skLineSegment(sketch, "E2253.1.5", {"start": v(47.87, 50.8) * mm, "end": v(58.52, 50.8) * mm, "construction": true});
            skArc(sketch, "E2254", {"start": v(48.67, 66.12) * mm, "mid": v(56.93, 60.79) * mm, "end": v(65.19, 66.12) * mm});
            skArc(sketch, "E2255.0", {"start": v(51.84, 69.85) * mm, "mid": v(56.93, 64.76) * mm, "end": v(62.02, 69.85) * mm});
            skArc(sketch, "E2256.MirrorCS", {"start": v(-51.84, 69.85) * mm, "mid": v(-56.93, 64.76) * mm, "end": v(-62.02, 69.85) * mm});
            skArc(sketch, "E2257.MirrorCS", {"start": v(-48.67, 66.12) * mm, "mid": v(-56.93, 60.79) * mm, "end": v(-65.19, 66.12) * mm});
            skLineSegment(sketch, "E2258.trimOffspring", {"start": v(-42.89, 69.85) * mm, "end": v(42.89, 69.85) * mm});
            skLineSegment(sketch, "E2259.trimOffspring", {"start": v(-62.02, 69.85) * mm, "end": v(-51.84, 69.85) * mm});
            skLineSegment(sketch, "E2260.trimOffspring", {"start": v(70.97, 69.85) * mm, "end": v(80.07, 69.85) * mm});
            skLineSegment(sketch, "E2261.trimOffspring", {"start": v(51.84, 69.85) * mm, "end": v(62.02, 69.85) * mm});
            skPoint(sketch, "E2262.visualSharp", {"position": v(47.87, 69.85) * mm});
            skArc(sketch, "E2262.filletArc", {"start": v(48.67, 66.12) * mm, "mid": v(46.33, 68.84) * mm, "end": v(42.89, 69.85) * mm});
            skPoint(sketch, "E2263.visualSharp", {"position": v(66, 69.85) * mm});
            skArc(sketch, "E2263.filletArc", {"start": v(70.97, 69.85) * mm, "mid": v(67.53, 68.84) * mm, "end": v(65.19, 66.12) * mm});
            skPoint(sketch, "E2264.visualSharp", {"position": v(-66, 69.85) * mm});
            skArc(sketch, "E2264.filletArc", {"start": v(-65.19, 66.12) * mm, "mid": v(-67.53, 68.84) * mm, "end": v(-70.97, 69.85) * mm});
            skPoint(sketch, "E2265.visualSharp", {"position": v(-47.87, 69.85) * mm});
            skArc(sketch, "E2265.filletArc", {"start": v(-42.89, 69.85) * mm, "mid": v(-46.33, 68.84) * mm, "end": v(-48.67, 66.12) * mm});
            skPoint(sketch, "E2266.orphan", {"position": v(88, 76.2) * mm});
            skPoint(sketch, "E2267.orphan", {"position": v(88, 69.85) * mm});
            skSolve(sketch);
        }
        {
            var Q0;
            Q0=qSketchRegion(id+"F20",true);
            extrude(context, id + "F21", {"entities" : qUnion([Q0]), "endBound" : BoundingType.SYMMETRIC, "depth" : 12.7 * mm, "offsetDistance" : 25.4 * mm});
        }
        {
            var Q0;
            Q0=makeQuery(id+"F21.opExtrude","CAP_FACE",FACE,{"disambiguationData":[OSD([sQuery(id+"F20.wireOp",EDGE,"E2246"),sQuery(id+"F20.wireOp",EDGE,"E2247"),sQuery(id+"F20.wireOp",EDGE,"E2248"),sQuery(id+"F20.wireOp",EDGE,"E2251.bottom"),sQuery(id+"F20.wireOp",EDGE,"E2251.top"),sQuery(id+"F20.wireOp",EDGE,"E2251.left"),sQuery(id+"F20.wireOp",EDGE,"E2251.right"),sQuery(id+"F20.wireOp",EDGE,"E2252.trimOffspring"),sQuery(id+"F20.wireOp",EDGE,"E2254"),sQuery(id+"F20.wireOp",EDGE,"E2255.0"),sQuery(id+"F20.wireOp",EDGE,"E2256.MirrorCS"),sQuery(id+"F20.wireOp",EDGE,"E2257.MirrorCS"),sQuery(id+"F20.wireOp",EDGE,"E2258.trimOffspring"),sQuery(id+"F20.wireOp",EDGE,"E2259.trimOffspring"),sQuery(id+"F20.wireOp",EDGE,"E2260.trimOffspring"),sQuery(id+"F20.wireOp",EDGE,"E2261.trimOffspring"),sQuery(id+"F20.wireOp",EDGE,"E2262.filletArc"),sQuery(id+"F20.wireOp",EDGE,"E2263.filletArc"),sQuery(id+"F20.wireOp",EDGE,"E2264.filletArc"),sQuery(id+"F20.wireOp",EDGE,"E2265.filletArc")])],"isStart":false});
            var sketch = newSketch(context, id + "F22", { "sketchPlane" : qUnion([Q0])});
            skLineSegment(sketch, "E2268", {"start": v(67.64, 129.12) * mm, "end": v(69.78, 127.33) * mm});
            skArc(sketch, "E2269", {"start": v(69.78, 127.33) * mm, "mid": v(70.95, 126.27) * mm, "end": v(72.03, 125.12) * mm});
            skArc(sketch, "E2270", {"start": v(72.03, 125.12) * mm, "mid": v(73.24, 123.66) * mm, "end": v(74.38, 122.15) * mm});
            skArc(sketch, "E2271", {"start": v(74.38, 122.15) * mm, "mid": v(75.47, 120.56) * mm, "end": v(76.48, 118.93) * mm});
            skArc(sketch, "E2272", {"start": v(76.48, 118.93) * mm, "mid": v(77.28, 117.46) * mm, "end": v(77.97, 115.94) * mm});
            skArc(sketch, "E2273", {"start": v(77.97, 115.94) * mm, "mid": v(78.58, 114.33) * mm, "end": v(79.13, 112.7) * mm});
            skArc(sketch, "E2274", {"start": v(79.13, 112.7) * mm, "mid": v(79.56, 111.14) * mm, "end": v(79.9, 109.57) * mm});
            skArc(sketch, "E2275", {"start": v(79.9, 109.57) * mm, "mid": v(80.16, 107.94) * mm, "end": v(80.33, 106.3) * mm});
            skArc(sketch, "E2276", {"start": v(80.33, 106.3) * mm, "mid": v(80.43, 104.47) * mm, "end": v(80.46, 102.63) * mm});
            skArc(sketch, "E2277", {"start": v(80.46, 102.63) * mm, "mid": v(80.42, 100.83) * mm, "end": v(80.31, 99.02) * mm});
            skArc(sketch, "E2278", {"start": v(80.31, 99.02) * mm, "mid": v(80.16, 97.58) * mm, "end": v(79.9, 96.14) * mm});
            skArc(sketch, "E2279", {"start": v(79.9, 96.14) * mm, "mid": v(79.56, 94.74) * mm, "end": v(79.13, 93.36) * mm});
            skArc(sketch, "E2280", {"start": v(79.13, 93.36) * mm, "mid": v(78.51, 91.7) * mm, "end": v(77.84, 90.08) * mm});
            skArc(sketch, "E2281", {"start": v(77.84, 90.08) * mm, "mid": v(76.67, 87.74) * mm, "end": v(75.26, 85.53) * mm});
            skArc(sketch, "E2282", {"start": v(75.26, 85.53) * mm, "mid": v(73.67, 83.54) * mm, "end": v(71.87, 81.74) * mm});
            skArc(sketch, "E2283", {"start": v(71.87, 81.74) * mm, "mid": v(69.9, 80.17) * mm, "end": v(67.77, 78.84) * mm});
            skArc(sketch, "E2284", {"start": v(67.77, 78.84) * mm, "mid": v(65.5, 77.76) * mm, "end": v(63.11, 76.94) * mm});
            skArc(sketch, "E2285", {"start": v(63.11, 76.94) * mm, "mid": v(60.88, 76.44) * mm, "end": v(58.6, 76.2) * mm});
            skArc(sketch, "E2286", {"start": v(58.6, 76.2) * mm, "mid": v(55.94, 76.17) * mm, "end": v(53.3, 76.33) * mm});
            skArc(sketch, "E2287", {"start": v(53.3, 76.33) * mm, "mid": v(50.66, 76.68) * mm, "end": v(48.05, 77.23) * mm});
            skArc(sketch, "E2288", {"start": v(48.05, 77.23) * mm, "mid": v(45.85, 77.9) * mm, "end": v(43.73, 78.82) * mm});
            skArc(sketch, "E2289", {"start": v(43.73, 78.82) * mm, "mid": v(42.16, 79.71) * mm, "end": v(40.7, 80.76) * mm});
            skArc(sketch, "E2290", {"start": v(40.7, 80.76) * mm, "mid": v(39.22, 82.02) * mm, "end": v(37.85, 83.4) * mm});
            skArc(sketch, "E2291", {"start": v(37.85, 83.4) * mm, "mid": v(36.61, 84.87) * mm, "end": v(35.5, 86.43) * mm});
            skArc(sketch, "E2292", {"start": v(35.5, 86.43) * mm, "mid": v(34.65, 87.92) * mm, "end": v(33.97, 89.5) * mm});
            skArc(sketch, "E2293", {"start": v(33.97, 89.5) * mm, "mid": v(33.35, 90.88) * mm, "end": v(32.51, 92.14) * mm});
            skArc(sketch, "E2294", {"start": v(32.51, 92.14) * mm, "mid": v(31.5, 93.26) * mm, "end": v(30.32, 94.22) * mm});
            skArc(sketch, "E2295", {"start": v(30.32, 94.22) * mm, "mid": v(28.9, 95.05) * mm, "end": v(27.36, 95.68) * mm});
            skArc(sketch, "E2296", {"start": v(27.36, 95.68) * mm, "mid": v(25.54, 96.2) * mm, "end": v(23.68, 96.55) * mm});
            skLineSegment(sketch, "E2297", {"start": v(23.68, 96.55) * mm, "end": v(21.13, 96.9) * mm});
            skLineSegment(sketch, "E2298", {"start": v(21.13, 96.9) * mm, "end": v(22.66, 98.02) * mm});
            skArc(sketch, "E2299", {"start": v(22.66, 98.02) * mm, "mid": v(23.49, 98.55) * mm, "end": v(24.37, 98.96) * mm});
            skArc(sketch, "E2300", {"start": v(24.37, 98.96) * mm, "mid": v(25.3, 99.27) * mm, "end": v(26.28, 99.46) * mm});
            skArc(sketch, "E2301", {"start": v(26.28, 99.46) * mm, "mid": v(27.29, 99.53) * mm, "end": v(28.3, 99.48) * mm});
            skArc(sketch, "E2302", {"start": v(28.3, 99.48) * mm, "mid": v(29.34, 99.31) * mm, "end": v(30.36, 99.03) * mm});
            skArc(sketch, "E2303", {"start": v(30.36, 99.03) * mm, "mid": v(30.76, 98.9) * mm, "end": v(31.17, 98.77) * mm});
            skArc(sketch, "E2304", {"start": v(31.17, 98.77) * mm, "mid": v(31.52, 98.67) * mm, "end": v(31.86, 98.56) * mm});
            skArc(sketch, "E2305", {"start": v(31.86, 98.57) * mm, "mid": v(32.16, 98.48) * mm, "end": v(32.46, 98.4) * mm});
            skArc(sketch, "E2306", {"start": v(32.46, 98.4) * mm, "mid": v(32.5, 98.4) * mm, "end": v(32.52, 98.42) * mm});
            skArc(sketch, "E2307", {"start": v(32.52, 98.42) * mm, "mid": v(32.54, 98.46) * mm, "end": v(32.55, 98.5) * mm});
            skArc(sketch, "E2308", {"start": v(32.55, 98.5) * mm, "mid": v(32.61, 98.77) * mm, "end": v(32.68, 99.05) * mm});
            skArc(sketch, "E2309", {"start": v(32.68, 99.05) * mm, "mid": v(32.75, 99.37) * mm, "end": v(32.82, 99.7) * mm});
            skArc(sketch, "E2310", {"start": v(32.82, 99.7) * mm, "mid": v(32.9, 100.06) * mm, "end": v(32.98, 100.44) * mm});
            skArc(sketch, "E2311", {"start": v(32.98, 100.44) * mm, "mid": v(33.47, 102.24) * mm, "end": v(34.15, 103.97) * mm});
            skArc(sketch, "E2312", {"start": v(34.15, 103.97) * mm, "mid": v(35.03, 105.69) * mm, "end": v(36.08, 107.3) * mm});
            skArc(sketch, "E2313", {"start": v(36.08, 107.3) * mm, "mid": v(37.26, 108.8) * mm, "end": v(38.59, 110.15) * mm});
            skArc(sketch, "E2314", {"start": v(38.59, 110.15) * mm, "mid": v(39.97, 111.3) * mm, "end": v(41.48, 112.27) * mm});
            skArc(sketch, "E2315", {"start": v(41.48, 112.27) * mm, "mid": v(42.16, 112.63) * mm, "end": v(42.85, 112.96) * mm});
            skArc(sketch, "E2316", {"start": v(42.85, 112.96) * mm, "mid": v(43.39, 113.17) * mm, "end": v(43.94, 113.33) * mm});
            skArc(sketch, "E2317", {"start": v(43.94, 113.33) * mm, "mid": v(44.6, 113.45) * mm, "end": v(45.27, 113.53) * mm});
            skArc(sketch, "E2318", {"start": v(45.27, 113.53) * mm, "mid": v(46.46, 113.6) * mm, "end": v(47.66, 113.67) * mm});
            skArc(sketch, "E2319", {"start": v(47.66, 113.67) * mm, "mid": v(48.81, 113.71) * mm, "end": v(49.97, 113.74) * mm});
            skArc(sketch, "E2320", {"start": v(49.97, 113.74) * mm, "mid": v(50.66, 113.73) * mm, "end": v(51.35, 113.67) * mm});
            skArc(sketch, "E2321", {"start": v(51.35, 113.67) * mm, "mid": v(51.93, 113.57) * mm, "end": v(52.5, 113.42) * mm});
            skArc(sketch, "E2322", {"start": v(52.5, 113.42) * mm, "mid": v(53.18, 113.2) * mm, "end": v(53.86, 112.93) * mm});
            skArc(sketch, "E2323", {"start": v(53.86, 112.93) * mm, "mid": v(54.97, 112.42) * mm, "end": v(56.03, 111.81) * mm});
            skArc(sketch, "E2324", {"start": v(56.03, 111.81) * mm, "mid": v(57.04, 111.12) * mm, "end": v(57.99, 110.35) * mm});
            skArc(sketch, "E2325", {"start": v(57.99, 110.35) * mm, "mid": v(58.86, 109.5) * mm, "end": v(59.66, 108.59) * mm});
            skArc(sketch, "E2326", {"start": v(59.66, 108.59) * mm, "mid": v(60.37, 107.62) * mm, "end": v(60.99, 106.6) * mm});
            skArc(sketch, "E2327", {"start": v(60.99, 106.6) * mm, "mid": v(61.37, 105.87) * mm, "end": v(61.73, 105.14) * mm});
            skArc(sketch, "E2328", {"start": v(61.73, 105.14) * mm, "mid": v(61.93, 104.65) * mm, "end": v(62.08, 104.14) * mm});
            skArc(sketch, "E2329", {"start": v(62.08, 104.14) * mm, "mid": v(62.18, 103.6) * mm, "end": v(62.22, 103.05) * mm});
            skArc(sketch, "E2330", {"start": v(62.22, 103.05) * mm, "mid": v(62.24, 102.16) * mm, "end": v(62.24, 101.26) * mm});
            skArc(sketch, "E2331", {"start": v(62.24, 101.26) * mm, "mid": v(62.13, 99.66) * mm, "end": v(61.83, 98.08) * mm});
            skArc(sketch, "E2332", {"start": v(61.83, 98.08) * mm, "mid": v(61.38, 96.68) * mm, "end": v(60.73, 95.37) * mm});
            skArc(sketch, "E2333", {"start": v(60.73, 95.37) * mm, "mid": v(59.9, 94.18) * mm, "end": v(58.92, 93.13) * mm});
            skArc(sketch, "E2334", {"start": v(58.92, 93.13) * mm, "mid": v(57.72, 92.16) * mm, "end": v(56.4, 91.34) * mm});
            skArc(sketch, "E2335", {"start": v(56.4, 91.34) * mm, "mid": v(55.43, 90.9) * mm, "end": v(54.4, 90.62) * mm});
            skArc(sketch, "E2336", {"start": v(54.4, 90.62) * mm, "mid": v(53.2, 90.46) * mm, "end": v(51.98, 90.41) * mm});
            skArc(sketch, "E2337", {"start": v(51.98, 90.41) * mm, "mid": v(50.77, 90.5) * mm, "end": v(49.58, 90.7) * mm});
            skArc(sketch, "E2338", {"start": v(49.58, 90.7) * mm, "mid": v(48.59, 91.01) * mm, "end": v(47.66, 91.48) * mm});
            skArc(sketch, "E2339", {"start": v(47.66, 91.48) * mm, "mid": v(46.9, 91.98) * mm, "end": v(46.2, 92.53) * mm});
            skArc(sketch, "E2340", {"start": v(46.2, 92.53) * mm, "mid": v(45.61, 93.08) * mm, "end": v(45.1, 93.68) * mm});
            skArc(sketch, "E2341", {"start": v(45.1, 93.68) * mm, "mid": v(44.7, 94.28) * mm, "end": v(44.4, 94.91) * mm});
            skArc(sketch, "E2342", {"start": v(44.4, 94.91) * mm, "mid": v(44.2, 95.54) * mm, "end": v(44.1, 96.2) * mm});
            skArc(sketch, "E2343", {"start": v(44.1, 96.2) * mm, "mid": v(44.15, 97.1) * mm, "end": v(44.43, 97.97) * mm});
            skArc(sketch, "E2344", {"start": v(44.43, 97.97) * mm, "mid": v(44.91, 98.73) * mm, "end": v(45.57, 99.34) * mm});
            skArc(sketch, "E2345", {"start": v(45.57, 99.34) * mm, "mid": v(46.37, 99.76) * mm, "end": v(47.24, 99.95) * mm});
            skArc(sketch, "E2346", {"start": v(47.24, 99.95) * mm, "mid": v(48.14, 99.91) * mm, "end": v(49, 99.64) * mm});
            skArc(sketch, "E2347", {"start": v(49, 99.64) * mm, "mid": v(49.5, 99.37) * mm, "end": v(49.97, 99.04) * mm});
            skArc(sketch, "E2348", {"start": v(49.97, 99.04) * mm, "mid": v(50.33, 98.7) * mm, "end": v(50.62, 98.3) * mm});
            skArc(sketch, "E2349", {"start": v(50.62, 98.3) * mm, "mid": v(50.83, 97.84) * mm, "end": v(50.96, 97.36) * mm});
            skArc(sketch, "E2350", {"start": v(50.96, 97.36) * mm, "mid": v(51.03, 96.76) * mm, "end": v(51.04, 96.16) * mm});
            skArc(sketch, "E2351", {"start": v(51.04, 96.16) * mm, "mid": v(51.03, 95.71) * mm, "end": v(51.03, 95.26) * mm});
            skArc(sketch, "E2352", {"start": v(51.03, 95.26) * mm, "mid": v(51.07, 95.08) * mm, "end": v(51.18, 94.93) * mm});
            skArc(sketch, "E2353", {"start": v(51.18, 94.93) * mm, "mid": v(51.34, 94.82) * mm, "end": v(51.53, 94.77) * mm});
            skArc(sketch, "E2354", {"start": v(51.53, 94.77) * mm, "mid": v(52.02, 94.73) * mm, "end": v(52.52, 94.7) * mm});
            skArc(sketch, "E2355", {"start": v(52.52, 94.7) * mm, "mid": v(53.16, 94.74) * mm, "end": v(53.8, 94.87) * mm});
            skArc(sketch, "E2356", {"start": v(53.8, 94.87) * mm, "mid": v(54.45, 95.11) * mm, "end": v(55.07, 95.44) * mm});
            skArc(sketch, "E2357", {"start": v(55.07, 95.44) * mm, "mid": v(55.69, 95.87) * mm, "end": v(56.25, 96.36) * mm});
            skArc(sketch, "E2358", {"start": v(56.25, 96.36) * mm, "mid": v(56.8, 96.96) * mm, "end": v(57.27, 97.6) * mm});
            skArc(sketch, "E2359", {"start": v(57.27, 97.6) * mm, "mid": v(57.66, 98.32) * mm, "end": v(57.9, 99.1) * mm});
            skArc(sketch, "E2360", {"start": v(57.9, 99.1) * mm, "mid": v(58.05, 100.08) * mm, "end": v(58.1, 101.08) * mm});
            skArc(sketch, "E2361", {"start": v(58.1, 101.08) * mm, "mid": v(58.03, 102.13) * mm, "end": v(57.86, 103.16) * mm});
            skArc(sketch, "E2362", {"start": v(57.86, 103.16) * mm, "mid": v(57.6, 104.06) * mm, "end": v(57.2, 104.92) * mm});
            skArc(sketch, "E2363", {"start": v(57.2, 104.92) * mm, "mid": v(56.48, 106.05) * mm, "end": v(55.6, 107.06) * mm});
            skArc(sketch, "E2364", {"start": v(55.6, 107.06) * mm, "mid": v(54.52, 107.97) * mm, "end": v(53.33, 108.74) * mm});
            skArc(sketch, "E2365", {"start": v(53.33, 108.74) * mm, "mid": v(52.05, 109.35) * mm, "end": v(50.7, 109.79) * mm});
            skArc(sketch, "E2366", {"start": v(50.7, 109.79) * mm, "mid": v(49.35, 110.02) * mm, "end": v(47.98, 110.06) * mm});
            skArc(sketch, "E2367", {"start": v(47.98, 110.06) * mm, "mid": v(46.88, 109.96) * mm, "end": v(45.8, 109.75) * mm});
            skArc(sketch, "E2368", {"start": v(45.8, 109.75) * mm, "mid": v(44.79, 109.44) * mm, "end": v(43.82, 109.01) * mm});
            skArc(sketch, "E2369", {"start": v(43.82, 109.01) * mm, "mid": v(42.86, 108.46) * mm, "end": v(41.95, 107.8) * mm});
            skArc(sketch, "E2370", {"start": v(41.95, 107.8) * mm, "mid": v(41, 106.98) * mm, "end": v(40.12, 106.09) * mm});
            skArc(sketch, "E2371", {"start": v(40.12, 106.09) * mm, "mid": v(39.5, 105.4) * mm, "end": v(38.9, 104.69) * mm});
            skArc(sketch, "E2372", {"start": v(38.9, 104.69) * mm, "mid": v(38.51, 104.17) * mm, "end": v(38.16, 103.62) * mm});
            skArc(sketch, "E2373", {"start": v(38.16, 103.62) * mm, "mid": v(37.88, 103.09) * mm, "end": v(37.65, 102.52) * mm});
            skArc(sketch, "E2374", {"start": v(37.65, 102.52) * mm, "mid": v(37.4, 101.79) * mm, "end": v(37.2, 101.04) * mm});
            skArc(sketch, "E2375", {"start": v(37.2, 101.04) * mm, "mid": v(36.92, 99.79) * mm, "end": v(36.73, 98.52) * mm});
            skArc(sketch, "E2376", {"start": v(36.73, 98.52) * mm, "mid": v(36.64, 97.26) * mm, "end": v(36.64, 96) * mm});
            skArc(sketch, "E2377", {"start": v(36.64, 96) * mm, "mid": v(36.74, 94.78) * mm, "end": v(36.93, 93.56) * mm});
            skArc(sketch, "E2378", {"start": v(36.93, 93.56) * mm, "mid": v(37.21, 92.41) * mm, "end": v(37.6, 91.3) * mm});
            skArc(sketch, "E2379", {"start": v(37.6, 91.3) * mm, "mid": v(38, 90.3) * mm, "end": v(38.46, 89.3) * mm});
            skArc(sketch, "E2380", {"start": v(38.46, 89.3) * mm, "mid": v(38.88, 88.53) * mm, "end": v(39.36, 87.78) * mm});
            skArc(sketch, "E2381", {"start": v(39.36, 87.78) * mm, "mid": v(39.9, 87.05) * mm, "end": v(40.5, 86.36) * mm});
            skArc(sketch, "E2382", {"start": v(40.5, 86.36) * mm, "mid": v(41.31, 85.52) * mm, "end": v(42.15, 84.72) * mm});
            skArc(sketch, "E2383", {"start": v(42.15, 84.72) * mm, "mid": v(43.48, 83.62) * mm, "end": v(44.93, 82.67) * mm});
            skArc(sketch, "E2384", {"start": v(44.93, 82.67) * mm, "mid": v(46.5, 81.86) * mm, "end": v(48.15, 81.23) * mm});
            skArc(sketch, "E2385", {"start": v(48.15, 81.23) * mm, "mid": v(49.93, 80.74) * mm, "end": v(51.75, 80.43) * mm});
            skArc(sketch, "E2386", {"start": v(51.75, 80.43) * mm, "mid": v(53.72, 80.27) * mm, "end": v(55.68, 80.28) * mm});
            skArc(sketch, "E2387", {"start": v(55.68, 80.28) * mm, "mid": v(57.07, 80.37) * mm, "end": v(58.46, 80.52) * mm});
            skArc(sketch, "E2388", {"start": v(58.46, 80.52) * mm, "mid": v(59.64, 80.72) * mm, "end": v(60.8, 81) * mm});
            skArc(sketch, "E2389", {"start": v(60.8, 81) * mm, "mid": v(61.95, 81.36) * mm, "end": v(63.08, 81.8) * mm});
            skArc(sketch, "E2390", {"start": v(63.08, 81.8) * mm, "mid": v(64.36, 82.37) * mm, "end": v(65.6, 83) * mm});
            skArc(sketch, "E2391", {"start": v(65.6, 83) * mm, "mid": v(69.17, 85.44) * mm, "end": v(72.1, 88.6) * mm});
            skArc(sketch, "E2392", {"start": v(72.1, 88.6) * mm, "mid": v(74.4, 92.44) * mm, "end": v(75.9, 96.65) * mm});
            skArc(sketch, "E2393", {"start": v(75.9, 96.65) * mm, "mid": v(76.59, 101.3) * mm, "end": v(76.4, 105.99) * mm});
            skArc(sketch, "E2394", {"start": v(76.4, 105.99) * mm, "mid": v(75.36, 110.73) * mm, "end": v(73.54, 115.23) * mm});
            skArc(sketch, "E2395", {"start": v(73.54, 115.23) * mm, "mid": v(72.06, 117.8) * mm, "end": v(70.34, 120.22) * mm});
            skArc(sketch, "E2396", {"start": v(70.34, 120.22) * mm, "mid": v(68.33, 122.54) * mm, "end": v(66.13, 124.67) * mm});
            skArc(sketch, "E2397", {"start": v(66.13, 124.67) * mm, "mid": v(63.75, 126.58) * mm, "end": v(61.21, 128.27) * mm});
            skArc(sketch, "E2398", {"start": v(61.21, 128.27) * mm, "mid": v(58.63, 129.65) * mm, "end": v(55.92, 130.75) * mm});
            skArc(sketch, "E2399", {"start": v(55.92, 130.75) * mm, "mid": v(52.91, 131.64) * mm, "end": v(49.83, 132.23) * mm});
            skArc(sketch, "E2400", {"start": v(49.83, 132.23) * mm, "mid": v(46.37, 132.59) * mm, "end": v(42.9, 132.7) * mm});
            skArc(sketch, "E2401", {"start": v(42.9, 132.7) * mm, "mid": v(39.4, 132.54) * mm, "end": v(35.92, 132.14) * mm});
            skArc(sketch, "E2402", {"start": v(35.92, 132.14) * mm, "mid": v(32.73, 131.5) * mm, "end": v(29.6, 130.57) * mm});
            skArc(sketch, "E2403", {"start": v(29.6, 130.57) * mm, "mid": v(28.92, 130.32) * mm, "end": v(28.23, 130.04) * mm});
            skArc(sketch, "E2404", {"start": v(28.23, 130.04) * mm, "mid": v(27.7, 129.78) * mm, "end": v(27.2, 129.48) * mm});
            skArc(sketch, "E2405", {"start": v(27.2, 129.48) * mm, "mid": v(26.74, 129.16) * mm, "end": v(26.3, 128.8) * mm});
            skArc(sketch, "E2406", {"start": v(26.3, 128.8) * mm, "mid": v(25.8, 128.32) * mm, "end": v(25.33, 127.82) * mm});
            skArc(sketch, "E2407", {"start": v(25.33, 127.82) * mm, "mid": v(24.21, 126.4) * mm, "end": v(23.29, 124.86) * mm});
            skArc(sketch, "E2408", {"start": v(23.29, 124.86) * mm, "mid": v(22.51, 123.1) * mm, "end": v(21.93, 121.27) * mm});
            skArc(sketch, "E2409", {"start": v(21.93, 121.27) * mm, "mid": v(21.54, 119.3) * mm, "end": v(21.36, 117.32) * mm});
            skArc(sketch, "E2410", {"start": v(21.36, 117.32) * mm, "mid": v(21.39, 115.3) * mm, "end": v(21.62, 113.28) * mm});
            skArc(sketch, "E2411", {"start": v(21.62, 113.28) * mm, "mid": v(21.72, 112.7) * mm, "end": v(21.8, 112.1) * mm});
            skArc(sketch, "E2412", {"start": v(21.8, 112.1) * mm, "mid": v(21.88, 111.6) * mm, "end": v(21.95, 111.1) * mm});
            skArc(sketch, "E2413", {"start": v(21.95, 111.1) * mm, "mid": v(22, 110.66) * mm, "end": v(22.05, 110.22) * mm});
            skArc(sketch, "E2414", {"start": v(22.05, 110.22) * mm, "mid": v(22.04, 110.15) * mm, "end": v(22, 110.08) * mm});
            skArc(sketch, "E2415", {"start": v(22, 110.08) * mm, "mid": v(21.85, 110) * mm, "end": v(21.67, 110.05) * mm});
            skArc(sketch, "E2416", {"start": v(21.67, 110.05) * mm, "mid": v(21.08, 110.59) * mm, "end": v(20.5, 111.15) * mm});
            skArc(sketch, "E2417", {"start": v(20.5, 111.15) * mm, "mid": v(19.89, 111.77) * mm, "end": v(19.3, 112.42) * mm});
            skArc(sketch, "E2418", {"start": v(19.3, 112.42) * mm, "mid": v(18.83, 113.02) * mm, "end": v(18.4, 113.64) * mm});
            skArc(sketch, "E2419", {"start": v(18.4, 113.64) * mm, "mid": v(17.9, 114.53) * mm, "end": v(17.53, 115.49) * mm});
            skArc(sketch, "E2420", {"start": v(17.53, 115.49) * mm, "mid": v(17.23, 116.63) * mm, "end": v(17.03, 117.8) * mm});
            skArc(sketch, "E2421", {"start": v(17.03, 117.8) * mm, "mid": v(16.93, 119.02) * mm, "end": v(16.94, 120.24) * mm});
            skArc(sketch, "E2422", {"start": v(16.94, 120.24) * mm, "mid": v(17.06, 121.36) * mm, "end": v(17.3, 122.46) * mm});
            skArc(sketch, "E2423", {"start": v(17.3, 122.46) * mm, "mid": v(17.4, 122.84) * mm, "end": v(17.5, 123.23) * mm});
            skArc(sketch, "E2424", {"start": v(17.5, 123.23) * mm, "mid": v(17.57, 123.57) * mm, "end": v(17.63, 123.91) * mm});
            skArc(sketch, "E2425", {"start": v(17.63, 123.91) * mm, "mid": v(17.68, 124.2) * mm, "end": v(17.71, 124.48) * mm});
            skArc(sketch, "E2426", {"start": v(17.71, 124.48) * mm, "mid": v(17.7, 124.56) * mm, "end": v(17.66, 124.63) * mm});
            skArc(sketch, "E2427", {"start": v(17.66, 124.63) * mm, "mid": v(16.92, 124.89) * mm, "end": v(16.22, 124.55) * mm});
            skArc(sketch, "E2428", {"start": v(16.22, 124.55) * mm, "mid": v(12.2, 119.91) * mm, "end": v(8.22, 115.25) * mm});
            skArc(sketch, "E2429", {"start": v(8.22, 115.25) * mm, "mid": v(4.54, 110.82) * mm, "end": v(0.94, 106.33) * mm});
            skArc(sketch, "E2430", {"start": v(0.94, 106.33) * mm, "mid": v(-0.69, 103.98) * mm, "end": v(-2, 101.44) * mm});
            skArc(sketch, "E2431", {"start": v(-2, 101.44) * mm, "mid": v(-2.4, 100.38) * mm, "end": v(-2.66, 99.27) * mm});
            skArc(sketch, "E2432", {"start": v(-2.66, 99.27) * mm, "mid": v(-2.8, 98.07) * mm, "end": v(-2.83, 96.85) * mm});
            skArc(sketch, "E2433", {"start": v(-2.83, 96.85) * mm, "mid": v(-2.74, 95.65) * mm, "end": v(-2.52, 94.47) * mm});
            skArc(sketch, "E2434", {"start": v(-2.52, 94.47) * mm, "mid": v(-2.2, 93.42) * mm, "end": v(-1.74, 92.42) * mm});
            skArc(sketch, "E2435", {"start": v(-1.74, 92.42) * mm, "mid": v(-1.24, 91.6) * mm, "end": v(-0.64, 90.84) * mm});
            skArc(sketch, "E2436", {"start": v(-0.64, 90.84) * mm, "mid": v(0.08, 90.1) * mm, "end": v(0.87, 89.44) * mm});
            skArc(sketch, "E2437", {"start": v(0.87, 89.44) * mm, "mid": v(1.73, 88.86) * mm, "end": v(2.64, 88.36) * mm});
            skArc(sketch, "E2438", {"start": v(2.64, 88.36) * mm, "mid": v(3.55, 87.97) * mm, "end": v(4.5, 87.68) * mm});
            skArc(sketch, "E2439", {"start": v(4.5, 87.68) * mm, "mid": v(6.56, 87.44) * mm, "end": v(8.62, 87.71) * mm});
            skArc(sketch, "E2440", {"start": v(8.62, 87.71) * mm, "mid": v(10.45, 88.48) * mm, "end": v(12, 89.73) * mm});
            skArc(sketch, "E2441", {"start": v(12, 89.73) * mm, "mid": v(13.02, 91.26) * mm, "end": v(13.53, 93.03) * mm});
            skArc(sketch, "E2442", {"start": v(13.53, 93.03) * mm, "mid": v(13.46, 94.87) * mm, "end": v(12.8, 96.58) * mm});
            skArc(sketch, "E2443", {"start": v(12.8, 96.58) * mm, "mid": v(12.54, 97.02) * mm, "end": v(12.24, 97.43) * mm});
            skArc(sketch, "E2444", {"start": v(12.24, 97.43) * mm, "mid": v(12.04, 97.61) * mm, "end": v(11.78, 97.7) * mm});
            skArc(sketch, "E2445", {"start": v(11.78, 97.7) * mm, "mid": v(11.52, 97.7) * mm, "end": v(11.28, 97.59) * mm});
            skArc(sketch, "E2446", {"start": v(11.28, 97.59) * mm, "mid": v(10.9, 97.29) * mm, "end": v(10.56, 96.96) * mm});
            skArc(sketch, "E2447", {"start": v(10.56, 96.96) * mm, "mid": v(10.11, 96.6) * mm, "end": v(9.6, 96.33) * mm});
            skArc(sketch, "E2448", {"start": v(9.6, 96.33) * mm, "mid": v(9.03, 96.17) * mm, "end": v(8.44, 96.1) * mm});
            skArc(sketch, "E2449", {"start": v(8.44, 96.1) * mm, "mid": v(7.84, 96.16) * mm, "end": v(7.25, 96.32) * mm});
            skArc(sketch, "E2450", {"start": v(7.25, 96.32) * mm, "mid": v(6.72, 96.58) * mm, "end": v(6.24, 96.94) * mm});
            skArc(sketch, "E2451", {"start": v(6.24, 96.94) * mm, "mid": v(5.64, 97.7) * mm, "end": v(5.3, 98.6) * mm});
            skArc(sketch, "E2452", {"start": v(5.3, 98.6) * mm, "mid": v(5.27, 99.56) * mm, "end": v(5.54, 100.49) * mm});
            skArc(sketch, "E2453", {"start": v(5.54, 100.49) * mm, "mid": v(6.1, 101.34) * mm, "end": v(6.9, 101.99) * mm});
            skArc(sketch, "E2454", {"start": v(6.9, 101.99) * mm, "mid": v(7.87, 102.42) * mm, "end": v(8.93, 102.6) * mm});
            skArc(sketch, "E2455", {"start": v(8.93, 102.6) * mm, "mid": v(10.08, 102.56) * mm, "end": v(11.2, 102.34) * mm});
            skArc(sketch, "E2456", {"start": v(11.2, 102.34) * mm, "mid": v(12.32, 101.94) * mm, "end": v(13.36, 101.39) * mm});
            skArc(sketch, "E2457", {"start": v(13.36, 101.39) * mm, "mid": v(14.33, 100.69) * mm, "end": v(15.2, 99.86) * mm});
            skArc(sketch, "E2458", {"start": v(15.2, 99.86) * mm, "mid": v(15.91, 98.93) * mm, "end": v(16.5, 97.9) * mm});
            skArc(sketch, "E2459", {"start": v(16.5, 97.9) * mm, "mid": v(16.85, 97) * mm, "end": v(17.08, 96.06) * mm});
            skArc(sketch, "E2460", {"start": v(17.08, 96.06) * mm, "mid": v(17.22, 94.96) * mm, "end": v(17.27, 93.85) * mm});
            skArc(sketch, "E2461", {"start": v(17.27, 93.85) * mm, "mid": v(17.21, 92.73) * mm, "end": v(17.06, 91.62) * mm});
            skArc(sketch, "E2462", {"start": v(17.06, 91.62) * mm, "mid": v(16.82, 90.63) * mm, "end": v(16.47, 89.68) * mm});
            skArc(sketch, "E2463", {"start": v(16.47, 89.68) * mm, "mid": v(15.46, 87.93) * mm, "end": v(14.12, 86.43) * mm});
            skArc(sketch, "E2464", {"start": v(14.12, 86.43) * mm, "mid": v(12.46, 85.2) * mm, "end": v(10.6, 84.31) * mm});
            skArc(sketch, "E2465", {"start": v(10.6, 84.31) * mm, "mid": v(8.55, 83.78) * mm, "end": v(6.43, 83.65) * mm});
            skArc(sketch, "E2466", {"start": v(6.43, 83.65) * mm, "mid": v(4.28, 83.9) * mm, "end": v(2.21, 84.54) * mm});
            skArc(sketch, "E2467", {"start": v(2.21, 84.54) * mm, "mid": v(1.74, 84.74) * mm, "end": v(1.27, 84.95) * mm});
            skArc(sketch, "E2468", {"start": v(1.27, 84.95) * mm, "mid": v(0.8, 85.17) * mm, "end": v(0.33, 85.41) * mm});
            skArc(sketch, "E2469", {"start": v(0.33, 85.41) * mm, "mid": v(-0.07, 85.63) * mm, "end": v(-0.47, 85.86) * mm});
            skArc(sketch, "E2470", {"start": v(-0.47, 85.86) * mm, "mid": v(-0.71, 86.02) * mm, "end": v(-0.94, 86.2) * mm});
            skLineSegment(sketch, "E2471", {"start": v(-0.94, 86.2) * mm, "end": v(-1.79, 86.93) * mm});
            skLineSegment(sketch, "E2472", {"start": v(-1.79, 86.93) * mm, "end": v(-2.51, 85.63) * mm});
            skArc(sketch, "E2473", {"start": v(-2.51, 85.63) * mm, "mid": v(-3.23, 84.5) * mm, "end": v(-4.06, 83.45) * mm});
            skArc(sketch, "E2474", {"start": v(-4.06, 83.45) * mm, "mid": v(-4.93, 82.58) * mm, "end": v(-5.91, 81.83) * mm});
            skArc(sketch, "E2475", {"start": v(-5.91, 81.83) * mm, "mid": v(-6.95, 81.25) * mm, "end": v(-8.06, 80.81) * mm});
            skArc(sketch, "E2476", {"start": v(-8.06, 80.81) * mm, "mid": v(-9.24, 80.53) * mm, "end": v(-10.44, 80.4) * mm});
            skArc(sketch, "E2477", {"start": v(-10.44, 80.4) * mm, "mid": v(-11.46, 80.37) * mm, "end": v(-12.48, 80.37) * mm});
            skArc(sketch, "E2478", {"start": v(-12.48, 80.37) * mm, "mid": v(-12.77, 80.47) * mm, "end": v(-12.95, 80.7) * mm});
            skArc(sketch, "E2479", {"start": v(-12.95, 80.7) * mm, "mid": v(-12.96, 81) * mm, "end": v(-12.8, 81.26) * mm});
            skArc(sketch, "E2480", {"start": v(-12.8, 81.26) * mm, "mid": v(-12, 81.88) * mm, "end": v(-11.19, 82.48) * mm});
            skArc(sketch, "E2481", {"start": v(-11.19, 82.48) * mm, "mid": v(-9.99, 83.41) * mm, "end": v(-8.87, 84.45) * mm});
            skArc(sketch, "E2482", {"start": v(-8.87, 84.45) * mm, "mid": v(-7.9, 85.54) * mm, "end": v(-7.02, 86.73) * mm});
            skArc(sketch, "E2483", {"start": v(-7.02, 86.73) * mm, "mid": v(-6.36, 87.85) * mm, "end": v(-5.83, 89.03) * mm});
            skArc(sketch, "E2484", {"start": v(-5.83, 89.03) * mm, "mid": v(-5.56, 90.03) * mm, "end": v(-5.5, 91.07) * mm});
            skArc(sketch, "E2485", {"start": v(-5.5, 91.07) * mm, "mid": v(-5.51, 91.31) * mm, "end": v(-5.54, 91.56) * mm});
            skArc(sketch, "E2486", {"start": v(-5.54, 91.56) * mm, "mid": v(-5.6, 91.93) * mm, "end": v(-5.67, 92.3) * mm});
            skArc(sketch, "E2487", {"start": v(-5.67, 92.3) * mm, "mid": v(-5.75, 92.71) * mm, "end": v(-5.84, 93.12) * mm});
            skArc(sketch, "E2488", {"start": v(-5.84, 93.12) * mm, "mid": v(-5.93, 93.52) * mm, "end": v(-6.04, 93.92) * mm});
            skLineSegment(sketch, "E2489", {"start": v(-6.04, 93.92) * mm, "end": v(-6.53, 95.83) * mm});
            skLineSegment(sketch, "E2490", {"start": v(-6.53, 95.83) * mm, "end": v(-10.76, 91.42) * mm});
            skArc(sketch, "E2491", {"start": v(-10.76, 91.42) * mm, "mid": v(-13.7, 88.52) * mm, "end": v(-16.81, 85.8) * mm});
            skArc(sketch, "E2492", {"start": v(-16.81, 85.8) * mm, "mid": v(-19.78, 83.52) * mm, "end": v(-22.92, 81.49) * mm});
            skArc(sketch, "E2493", {"start": v(-22.92, 81.49) * mm, "mid": v(-25.98, 79.83) * mm, "end": v(-29.18, 78.44) * mm});
            skArc(sketch, "E2494", {"start": v(-29.18, 78.44) * mm, "mid": v(-32.4, 77.36) * mm, "end": v(-35.7, 76.58) * mm});
            skArc(sketch, "E2495", {"start": v(-35.7, 76.58) * mm, "mid": v(-37.89, 76.24) * mm, "end": v(-40.09, 76.07) * mm});
            skArc(sketch, "E2496", {"start": v(-40.09, 76.07) * mm, "mid": v(-42.2, 76.07) * mm, "end": v(-44.3, 76.25) * mm});
            skArc(sketch, "E2497", {"start": v(-44.3, 76.25) * mm, "mid": v(-46.44, 76.6) * mm, "end": v(-48.54, 77.13) * mm});
            skArc(sketch, "E2498", {"start": v(-48.54, 77.13) * mm, "mid": v(-50.78, 77.87) * mm, "end": v(-52.96, 78.74) * mm});
            skArc(sketch, "E2499", {"start": v(-52.96, 78.74) * mm, "mid": v(-54.7, 79.58) * mm, "end": v(-56.37, 80.53) * mm});
            skArc(sketch, "E2500", {"start": v(-56.37, 80.53) * mm, "mid": v(-57.85, 81.55) * mm, "end": v(-59.24, 82.7) * mm});
            skArc(sketch, "E2501", {"start": v(-59.24, 82.7) * mm, "mid": v(-60.51, 83.94) * mm, "end": v(-61.66, 85.29) * mm});
            skArc(sketch, "E2502", {"start": v(-61.66, 85.29) * mm, "mid": v(-62.75, 86.8) * mm, "end": v(-63.7, 88.38) * mm});
            skArc(sketch, "E2503", {"start": v(-63.7, 88.38) * mm, "mid": v(-64.21, 89.33) * mm, "end": v(-64.7, 90.29) * mm});
            skArc(sketch, "E2504", {"start": v(-64.7, 90.29) * mm, "mid": v(-65, 90.99) * mm, "end": v(-65.26, 91.7) * mm});
            skArc(sketch, "E2505", {"start": v(-65.26, 91.7) * mm, "mid": v(-65.47, 92.48) * mm, "end": v(-65.64, 93.26) * mm});
            skArc(sketch, "E2506", {"start": v(-65.64, 93.26) * mm, "mid": v(-65.84, 94.47) * mm, "end": v(-66.02, 95.69) * mm});
            skArc(sketch, "E2507", {"start": v(-66.02, 95.69) * mm, "mid": v(-66.43, 98.33) * mm, "end": v(-66.9, 100.96) * mm});
            skArc(sketch, "E2508", {"start": v(-66.9, 100.96) * mm, "mid": v(-67.31, 102.6) * mm, "end": v(-67.89, 104.2) * mm});
            skArc(sketch, "E2509", {"start": v(-67.89, 104.2) * mm, "mid": v(-68.5, 105.37) * mm, "end": v(-69.28, 106.45) * mm});
            skArc(sketch, "E2510", {"start": v(-69.28, 106.45) * mm, "mid": v(-70.27, 107.49) * mm, "end": v(-71.38, 108.39) * mm});
            skArc(sketch, "E2511", {"start": v(-71.38, 108.39) * mm, "mid": v(-71.77, 108.67) * mm, "end": v(-72.16, 108.96) * mm});
            skArc(sketch, "E2512", {"start": v(-72.16, 108.96) * mm, "mid": v(-72.49, 109.22) * mm, "end": v(-72.81, 109.49) * mm});
            skArc(sketch, "E2513", {"start": v(-72.81, 109.49) * mm, "mid": v(-73.08, 109.71) * mm, "end": v(-73.34, 109.94) * mm});
            skArc(sketch, "E2514", {"start": v(-73.34, 109.94) * mm, "mid": v(-73.4, 110.02) * mm, "end": v(-73.43, 110.1) * mm});
            skArc(sketch, "E2515", {"start": v(-73.43, 110.1) * mm, "mid": v(-73.42, 110.18) * mm, "end": v(-73.36, 110.22) * mm});
            skArc(sketch, "E2516", {"start": v(-73.36, 110.22) * mm, "mid": v(-73.13, 110.28) * mm, "end": v(-72.9, 110.33) * mm});
            skArc(sketch, "E2517", {"start": v(-72.9, 110.33) * mm, "mid": v(-72.6, 110.39) * mm, "end": v(-72.29, 110.42) * mm});
            skArc(sketch, "E2518", {"start": v(-72.29, 110.42) * mm, "mid": v(-71.92, 110.46) * mm, "end": v(-71.56, 110.48) * mm});
            skArc(sketch, "E2519", {"start": v(-71.56, 110.48) * mm, "mid": v(-70.7, 110.47) * mm, "end": v(-69.85, 110.36) * mm});
            skArc(sketch, "E2520", {"start": v(-69.85, 110.36) * mm, "mid": v(-68.99, 110.15) * mm, "end": v(-68.15, 109.86) * mm});
            skArc(sketch, "E2521", {"start": v(-68.15, 109.86) * mm, "mid": v(-67.32, 109.47) * mm, "end": v(-66.53, 109) * mm});
            skArc(sketch, "E2522", {"start": v(-66.53, 109) * mm, "mid": v(-65.77, 108.45) * mm, "end": v(-65.07, 107.83) * mm});
            skLineSegment(sketch, "E2523", {"start": v(-65.07, 107.83) * mm, "end": v(-63.77, 106.58) * mm});
            skLineSegment(sketch, "E2524", {"start": v(-63.77, 106.58) * mm, "end": v(-61.96, 108.6) * mm});
            skArc(sketch, "E2525", {"start": v(-61.96, 108.6) * mm, "mid": v(-61.52, 109.08) * mm, "end": v(-61.05, 109.53) * mm});
            skArc(sketch, "E2526", {"start": v(-61.05, 109.53) * mm, "mid": v(-60.51, 110) * mm, "end": v(-59.96, 110.45) * mm});
            skArc(sketch, "E2527", {"start": v(-59.96, 110.45) * mm, "mid": v(-59.39, 110.87) * mm, "end": v(-58.8, 111.28) * mm});
            skArc(sketch, "E2528", {"start": v(-58.8, 111.28) * mm, "mid": v(-58.22, 111.64) * mm, "end": v(-57.63, 111.97) * mm});
            skArc(sketch, "E2529", {"start": v(-57.63, 111.97) * mm, "mid": v(-56.86, 112.36) * mm, "end": v(-56.08, 112.72) * mm});
            skArc(sketch, "E2530", {"start": v(-56.08, 112.72) * mm, "mid": v(-55.52, 112.95) * mm, "end": v(-54.93, 113.12) * mm});
            skArc(sketch, "E2531", {"start": v(-54.93, 113.12) * mm, "mid": v(-54.3, 113.25) * mm, "end": v(-53.64, 113.33) * mm});
            skArc(sketch, "E2532", {"start": v(-53.64, 113.33) * mm, "mid": v(-52.57, 113.4) * mm, "end": v(-51.5, 113.46) * mm});
            skArc(sketch, "E2533", {"start": v(-51.5, 113.46) * mm, "mid": v(-50.47, 113.5) * mm, "end": v(-49.46, 113.5) * mm});
            skArc(sketch, "E2534", {"start": v(-49.46, 113.5) * mm, "mid": v(-48.8, 113.49) * mm, "end": v(-48.13, 113.42) * mm});
            skArc(sketch, "E2535", {"start": v(-48.13, 113.42) * mm, "mid": v(-47.56, 113.33) * mm, "end": v(-47, 113.18) * mm});
            skArc(sketch, "E2536", {"start": v(-47, 113.18) * mm, "mid": v(-46.34, 112.96) * mm, "end": v(-45.7, 112.71) * mm});
            skArc(sketch, "E2537", {"start": v(-45.7, 112.71) * mm, "mid": v(-43.17, 111.36) * mm, "end": v(-40.98, 109.52) * mm});
            skArc(sketch, "E2538", {"start": v(-40.98, 109.52) * mm, "mid": v(-39.31, 107.35) * mm, "end": v(-38.2, 104.85) * mm});
            skArc(sketch, "E2539", {"start": v(-38.2, 104.85) * mm, "mid": v(-37.72, 102.26) * mm, "end": v(-37.9, 99.63) * mm});
            skArc(sketch, "E2540", {"start": v(-37.9, 99.63) * mm, "mid": v(-38.7, 97.12) * mm, "end": v(-40.09, 94.88) * mm});
            skArc(sketch, "E2541", {"start": v(-40.09, 94.88) * mm, "mid": v(-40.83, 94.02) * mm, "end": v(-41.64, 93.23) * mm});
            skArc(sketch, "E2542", {"start": v(-41.64, 93.23) * mm, "mid": v(-42.4, 92.63) * mm, "end": v(-43.21, 92.13) * mm});
            skArc(sketch, "E2543", {"start": v(-43.21, 92.13) * mm, "mid": v(-44.07, 91.74) * mm, "end": v(-44.97, 91.47) * mm});
            skArc(sketch, "E2544", {"start": v(-44.97, 91.47) * mm, "mid": v(-46.01, 91.28) * mm, "end": v(-47.07, 91.19) * mm});
            skArc(sketch, "E2545", {"start": v(-47.07, 91.19) * mm, "mid": v(-48.12, 91.2) * mm, "end": v(-49.17, 91.3) * mm});
            skArc(sketch, "E2546", {"start": v(-49.17, 91.3) * mm, "mid": v(-50.12, 91.48) * mm, "end": v(-51.03, 91.79) * mm});
            skArc(sketch, "E2547", {"start": v(-51.03, 91.79) * mm, "mid": v(-51.83, 92.17) * mm, "end": v(-52.56, 92.65) * mm});
            skArc(sketch, "E2548", {"start": v(-52.56, 92.65) * mm, "mid": v(-53.17, 93.2) * mm, "end": v(-53.68, 93.84) * mm});
            skArc(sketch, "E2549", {"start": v(-53.68, 93.84) * mm, "mid": v(-54, 94.35) * mm, "end": v(-54.26, 94.89) * mm});
            skArc(sketch, "E2550", {"start": v(-54.26, 94.89) * mm, "mid": v(-54.41, 95.33) * mm, "end": v(-54.48, 95.79) * mm});
            skArc(sketch, "E2551", {"start": v(-54.48, 95.79) * mm, "mid": v(-54.45, 96.25) * mm, "end": v(-54.35, 96.7) * mm});
            skArc(sketch, "E2552", {"start": v(-54.35, 96.7) * mm, "mid": v(-54.13, 97.26) * mm, "end": v(-53.86, 97.8) * mm});
            skArc(sketch, "E2553", {"start": v(-53.86, 97.8) * mm, "mid": v(-53.28, 98.57) * mm, "end": v(-52.49, 99.14) * mm});
            skArc(sketch, "E2554", {"start": v(-52.49, 99.14) * mm, "mid": v(-51.57, 99.45) * mm, "end": v(-50.6, 99.48) * mm});
            skArc(sketch, "E2555", {"start": v(-50.6, 99.48) * mm, "mid": v(-49.65, 99.22) * mm, "end": v(-48.8, 98.7) * mm});
            skArc(sketch, "E2556", {"start": v(-48.8, 98.7) * mm, "mid": v(-48.12, 97.95) * mm, "end": v(-47.67, 97.04) * mm});
            skArc(sketch, "E2557", {"start": v(-47.67, 97.04) * mm, "mid": v(-47.44, 96.51) * mm, "end": v(-47.14, 96.02) * mm});
            skArc(sketch, "E2558", {"start": v(-47.14, 96.02) * mm, "mid": v(-46.86, 95.75) * mm, "end": v(-46.49, 95.6) * mm});
            skArc(sketch, "E2559", {"start": v(-46.49, 95.6) * mm, "mid": v(-46.04, 95.59) * mm, "end": v(-45.6, 95.72) * mm});
            skArc(sketch, "E2560", {"start": v(-45.6, 95.72) * mm, "mid": v(-44.95, 96.05) * mm, "end": v(-44.33, 96.44) * mm});
            skArc(sketch, "E2561", {"start": v(-44.33, 96.44) * mm, "mid": v(-43.8, 96.87) * mm, "end": v(-43.34, 97.38) * mm});
            skArc(sketch, "E2562", {"start": v(-43.34, 97.38) * mm, "mid": v(-42.9, 98.06) * mm, "end": v(-42.52, 98.78) * mm});
            skArc(sketch, "E2563", {"start": v(-42.52, 98.78) * mm, "mid": v(-42.2, 99.56) * mm, "end": v(-41.98, 100.37) * mm});
            skArc(sketch, "E2564", {"start": v(-41.98, 100.37) * mm, "mid": v(-41.86, 101.12) * mm, "end": v(-41.84, 101.88) * mm});
            skArc(sketch, "E2565", {"start": v(-41.84, 101.88) * mm, "mid": v(-42, 102.97) * mm, "end": v(-42.34, 104) * mm});
            skArc(sketch, "E2566", {"start": v(-42.34, 104) * mm, "mid": v(-42.92, 105.1) * mm, "end": v(-43.64, 106.11) * mm});
            skArc(sketch, "E2567", {"start": v(-43.64, 106.11) * mm, "mid": v(-44.51, 107.07) * mm, "end": v(-45.5, 107.9) * mm});
            skArc(sketch, "E2568", {"start": v(-45.5, 107.9) * mm, "mid": v(-46.54, 108.58) * mm, "end": v(-47.67, 109.1) * mm});
            skArc(sketch, "E2569", {"start": v(-47.67, 109.1) * mm, "mid": v(-48.64, 109.4) * mm, "end": v(-49.63, 109.56) * mm});
            skArc(sketch, "E2570", {"start": v(-49.63, 109.56) * mm, "mid": v(-50.76, 109.62) * mm, "end": v(-51.9, 109.58) * mm});
            skArc(sketch, "E2571", {"start": v(-51.9, 109.58) * mm, "mid": v(-53.03, 109.43) * mm, "end": v(-54.15, 109.18) * mm});
            skArc(sketch, "E2572", {"start": v(-54.15, 109.18) * mm, "mid": v(-55.13, 108.84) * mm, "end": v(-56.06, 108.4) * mm});
            skArc(sketch, "E2573", {"start": v(-56.06, 108.4) * mm, "mid": v(-57.38, 107.52) * mm, "end": v(-58.58, 106.49) * mm});
            skArc(sketch, "E2574", {"start": v(-58.58, 106.49) * mm, "mid": v(-59.62, 105.3) * mm, "end": v(-60.49, 104) * mm});
            skArc(sketch, "E2575", {"start": v(-60.49, 104) * mm, "mid": v(-61.19, 102.55) * mm, "end": v(-61.7, 101.03) * mm});
            skArc(sketch, "E2576", {"start": v(-61.7, 101.03) * mm, "mid": v(-62.02, 99.38) * mm, "end": v(-62.15, 97.7) * mm});
            skArc(sketch, "E2577", {"start": v(-62.15, 97.7) * mm, "mid": v(-61.86, 94.45) * mm, "end": v(-60.86, 91.34) * mm});
            skArc(sketch, "E2578", {"start": v(-60.86, 91.34) * mm, "mid": v(-59.2, 88.41) * mm, "end": v(-56.98, 85.88) * mm});
            skArc(sketch, "E2579", {"start": v(-56.98, 85.88) * mm, "mid": v(-54.1, 83.65) * mm, "end": v(-50.87, 81.97) * mm});
            skArc(sketch, "E2580", {"start": v(-50.87, 81.97) * mm, "mid": v(-47.13, 80.75) * mm, "end": v(-43.25, 80.07) * mm});
            skArc(sketch, "E2581", {"start": v(-43.25, 80.07) * mm, "mid": v(-40.35, 79.97) * mm, "end": v(-37.46, 80.24) * mm});
            skArc(sketch, "E2582", {"start": v(-37.46, 80.24) * mm, "mid": v(-34.31, 80.9) * mm, "end": v(-31.23, 81.85) * mm});
            skArc(sketch, "E2583", {"start": v(-31.23, 81.85) * mm, "mid": v(-28.05, 83.17) * mm, "end": v(-24.98, 84.76) * mm});
            skArc(sketch, "E2584", {"start": v(-24.98, 84.76) * mm, "mid": v(-21.98, 86.67) * mm, "end": v(-19.14, 88.8) * mm});
            skArc(sketch, "E2585", {"start": v(-19.14, 88.8) * mm, "mid": v(-17.21, 90.47) * mm, "end": v(-15.38, 92.23) * mm});
            skArc(sketch, "E2586", {"start": v(-15.38, 92.23) * mm, "mid": v(-13.44, 94.28) * mm, "end": v(-11.58, 96.4) * mm});
            skArc(sketch, "E2587", {"start": v(-11.58, 96.4) * mm, "mid": v(-9.41, 99.05) * mm, "end": v(-7.32, 101.77) * mm});
            skArc(sketch, "E2588", {"start": v(-7.32, 101.77) * mm, "mid": v(-4.7, 105.36) * mm, "end": v(-2.11, 108.98) * mm});
            skArc(sketch, "E2589", {"start": v(-2.11, 108.98) * mm, "mid": v(-1.34, 110.08) * mm, "end": v(-0.57, 111.17) * mm});
            skArc(sketch, "E2590", {"start": v(-0.57, 111.17) * mm, "mid": v(0.2, 112.26) * mm, "end": v(0.99, 113.35) * mm});
            skArc(sketch, "E2591", {"start": v(0.99, 113.35) * mm, "mid": v(1.67, 114.3) * mm, "end": v(2.36, 115.25) * mm});
            skArc(sketch, "E2592", {"start": v(2.36, 115.25) * mm, "mid": v(2.78, 115.82) * mm, "end": v(3.22, 116.39) * mm});
            skArc(sketch, "E2593", {"start": v(3.22, 116.39) * mm, "mid": v(3.52, 116.8) * mm, "end": v(3.82, 117.2) * mm});
            skArc(sketch, "E2594", {"start": v(3.82, 117.2) * mm, "mid": v(4.06, 117.56) * mm, "end": v(4.3, 117.92) * mm});
            skArc(sketch, "E2595", {"start": v(4.3, 117.92) * mm, "mid": v(4.47, 118.22) * mm, "end": v(4.65, 118.52) * mm});
            skArc(sketch, "E2596", {"start": v(4.65, 118.52) * mm, "mid": v(4.66, 118.6) * mm, "end": v(4.63, 118.66) * mm});
            skArc(sketch, "E2597", {"start": v(4.63, 118.66) * mm, "mid": v(4.55, 118.7) * mm, "end": v(4.46, 118.7) * mm});
            skArc(sketch, "E2598", {"start": v(4.46, 118.7) * mm, "mid": v(4.01, 118.59) * mm, "end": v(3.57, 118.47) * mm});
            skArc(sketch, "E2599", {"start": v(3.57, 118.47) * mm, "mid": v(3.03, 118.32) * mm, "end": v(2.5, 118.17) * mm});
            skArc(sketch, "E2600", {"start": v(2.5, 118.17) * mm, "mid": v(1.9, 117.97) * mm, "end": v(1.28, 117.77) * mm});
            skArc(sketch, "E2601", {"start": v(1.28, 117.77) * mm, "mid": v(0.58, 117.54) * mm, "end": v(-0.12, 117.32) * mm});
            skArc(sketch, "E2602", {"start": v(-0.12, 117.32) * mm, "mid": v(-0.93, 117.09) * mm, "end": v(-1.75, 116.86) * mm});
            skArc(sketch, "E2603", {"start": v(-1.75, 116.86) * mm, "mid": v(-2.54, 116.65) * mm, "end": v(-3.34, 116.44) * mm});
            skArc(sketch, "E2604", {"start": v(-3.34, 116.44) * mm, "mid": v(-3.97, 116.3) * mm, "end": v(-4.61, 116.16) * mm});
            skArc(sketch, "E2605", {"start": v(-4.61, 116.16) * mm, "mid": v(-6.78, 115.62) * mm, "end": v(-8.88, 114.9) * mm});
            skArc(sketch, "E2606", {"start": v(-8.88, 114.9) * mm, "mid": v(-10.77, 114.02) * mm, "end": v(-12.56, 112.94) * mm});
            skArc(sketch, "E2607", {"start": v(-12.56, 112.94) * mm, "mid": v(-14.17, 111.7) * mm, "end": v(-15.63, 110.29) * mm});
            skArc(sketch, "E2608", {"start": v(-15.63, 110.29) * mm, "mid": v(-16.95, 108.7) * mm, "end": v(-18.09, 106.98) * mm});
            skLineSegment(sketch, "E2609", {"start": v(-18.09, 106.98) * mm, "end": v(-19.44, 104.67) * mm});
            skLineSegment(sketch, "E2610", {"start": v(-19.44, 104.67) * mm, "end": v(-20.08, 106.02) * mm});
            skArc(sketch, "E2611", {"start": v(-20.08, 106.02) * mm, "mid": v(-20.48, 107.1) * mm, "end": v(-20.7, 108.23) * mm});
            skArc(sketch, "E2612", {"start": v(-20.7, 108.23) * mm, "mid": v(-20.73, 109.38) * mm, "end": v(-20.57, 110.51) * mm});
            skArc(sketch, "E2613", {"start": v(-20.57, 110.51) * mm, "mid": v(-20.21, 111.7) * mm, "end": v(-19.68, 112.84) * mm});
            skArc(sketch, "E2614", {"start": v(-19.68, 112.84) * mm, "mid": v(-18.91, 114.04) * mm, "end": v(-18.03, 115.16) * mm});
            skLineSegment(sketch, "E2615", {"start": v(-18.03, 115.16) * mm, "end": v(-16.5, 116.91) * mm});
            skLineSegment(sketch, "E2616", {"start": v(-16.5, 116.91) * mm, "end": v(-17.42, 117.57) * mm});
            skArc(sketch, "E2617", {"start": v(-17.42, 117.57) * mm, "mid": v(-17.65, 117.74) * mm, "end": v(-17.87, 117.9) * mm});
            skArc(sketch, "E2618", {"start": v(-17.87, 117.9) * mm, "mid": v(-18.2, 118.16) * mm, "end": v(-18.51, 118.42) * mm});
            skArc(sketch, "E2619", {"start": v(-18.51, 118.42) * mm, "mid": v(-18.86, 118.7) * mm, "end": v(-19.2, 119) * mm});
            skArc(sketch, "E2620", {"start": v(-19.2, 119) * mm, "mid": v(-19.53, 119.27) * mm, "end": v(-19.85, 119.55) * mm});
            skArc(sketch, "E2621", {"start": v(-19.85, 119.55) * mm, "mid": v(-22.22, 122.3) * mm, "end": v(-23.72, 125.6) * mm});
            skArc(sketch, "E2622", {"start": v(-23.72, 125.6) * mm, "mid": v(-24.26, 129.24) * mm, "end": v(-23.8, 132.89) * mm});
            skArc(sketch, "E2623", {"start": v(-23.8, 132.89) * mm, "mid": v(-22.4, 136.1) * mm, "end": v(-20.13, 138.79) * mm});
            skArc(sketch, "E2624", {"start": v(-20.13, 138.79) * mm, "mid": v(-17.28, 140.54) * mm, "end": v(-14.02, 141.25) * mm});
            skArc(sketch, "E2625", {"start": v(-14.02, 141.25) * mm, "mid": v(-12.17, 141.15) * mm, "end": v(-10.37, 140.72) * mm});
            skArc(sketch, "E2626", {"start": v(-10.37, 140.72) * mm, "mid": v(-8.66, 139.95) * mm, "end": v(-7.12, 138.89) * mm});
            skArc(sketch, "E2627", {"start": v(-7.12, 138.89) * mm, "mid": v(-5.84, 137.6) * mm, "end": v(-4.83, 136.1) * mm});
            skArc(sketch, "E2628", {"start": v(-4.83, 136.1) * mm, "mid": v(-4.19, 134.53) * mm, "end": v(-3.92, 132.86) * mm});
            skArc(sketch, "E2629", {"start": v(-3.92, 132.86) * mm, "mid": v(-3.93, 132.2) * mm, "end": v(-4.03, 131.56) * mm});
            skArc(sketch, "E2630", {"start": v(-4.03, 131.56) * mm, "mid": v(-4.23, 130.75) * mm, "end": v(-4.48, 129.96) * mm});
            skArc(sketch, "E2631", {"start": v(-4.48, 129.96) * mm, "mid": v(-4.77, 129.2) * mm, "end": v(-5.11, 128.46) * mm});
            skArc(sketch, "E2632", {"start": v(-5.11, 128.46) * mm, "mid": v(-5.42, 127.94) * mm, "end": v(-5.8, 127.48) * mm});
            skArc(sketch, "E2633", {"start": v(-5.8, 127.48) * mm, "mid": v(-6.55, 126.91) * mm, "end": v(-7.42, 126.58) * mm});
            skArc(sketch, "E2634", {"start": v(-7.42, 126.58) * mm, "mid": v(-8.36, 126.5) * mm, "end": v(-9.29, 126.69) * mm});
            skArc(sketch, "E2635", {"start": v(-9.29, 126.69) * mm, "mid": v(-10.1, 127.12) * mm, "end": v(-10.78, 127.76) * mm});
            skArc(sketch, "E2636", {"start": v(-10.78, 127.76) * mm, "mid": v(-11.22, 128.55) * mm, "end": v(-11.4, 129.44) * mm});
            skArc(sketch, "E2637", {"start": v(-11.4, 129.44) * mm, "mid": v(-11.36, 130) * mm, "end": v(-11.22, 130.54) * mm});
            skArc(sketch, "E2638", {"start": v(-11.22, 130.54) * mm, "mid": v(-10.97, 131.1) * mm, "end": v(-10.63, 131.6) * mm});
            skArc(sketch, "E2639", {"start": v(-10.63, 131.6) * mm, "mid": v(-10.24, 132.04) * mm, "end": v(-9.79, 132.4) * mm});
            skArc(sketch, "E2640", {"start": v(-9.79, 132.4) * mm, "mid": v(-9.36, 132.62) * mm, "end": v(-8.89, 132.7) * mm});
            skArc(sketch, "E2641", {"start": v(-8.89, 132.7) * mm, "mid": v(-8.58, 132.8) * mm, "end": v(-8.34, 133) * mm});
            skArc(sketch, "E2642", {"start": v(-8.34, 133) * mm, "mid": v(-8.19, 133.3) * mm, "end": v(-8.15, 133.65) * mm});
            skArc(sketch, "E2643", {"start": v(-8.15, 133.65) * mm, "mid": v(-8.22, 134.12) * mm, "end": v(-8.4, 134.57) * mm});
            skArc(sketch, "E2644", {"start": v(-8.4, 134.57) * mm, "mid": v(-8.68, 135.06) * mm, "end": v(-9.03, 135.52) * mm});
            skArc(sketch, "E2645", {"start": v(-9.03, 135.52) * mm, "mid": v(-9.94, 136.37) * mm, "end": v(-11.02, 136.99) * mm});
            skArc(sketch, "E2646", {"start": v(-11.02, 136.99) * mm, "mid": v(-12.24, 137.37) * mm, "end": v(-13.52, 137.49) * mm});
            skArc(sketch, "E2647", {"start": v(-13.52, 137.49) * mm, "mid": v(-14.83, 137.34) * mm, "end": v(-16.09, 136.93) * mm});
            skArc(sketch, "E2648", {"start": v(-16.09, 136.93) * mm, "mid": v(-17.26, 136.28) * mm, "end": v(-18.29, 135.41) * mm});
            skArc(sketch, "E2649", {"start": v(-18.29, 135.41) * mm, "mid": v(-18.84, 134.78) * mm, "end": v(-19.32, 134.08) * mm});
            skArc(sketch, "E2650", {"start": v(-19.32, 134.08) * mm, "mid": v(-19.73, 133.33) * mm, "end": v(-20.04, 132.54) * mm});
            skArc(sketch, "E2651", {"start": v(-20.04, 132.54) * mm, "mid": v(-20.28, 131.67) * mm, "end": v(-20.44, 130.78) * mm});
            skArc(sketch, "E2652", {"start": v(-20.44, 130.78) * mm, "mid": v(-20.51, 129.78) * mm, "end": v(-20.5, 128.79) * mm});
            skArc(sketch, "E2653", {"start": v(-20.5, 128.79) * mm, "mid": v(-20.42, 127.7) * mm, "end": v(-20.23, 126.65) * mm});
            skArc(sketch, "E2654", {"start": v(-20.23, 126.65) * mm, "mid": v(-19.96, 125.72) * mm, "end": v(-19.57, 124.83) * mm});
            skArc(sketch, "E2655", {"start": v(-19.57, 124.83) * mm, "mid": v(-19.08, 123.99) * mm, "end": v(-18.48, 123.22) * mm});
            skArc(sketch, "E2656", {"start": v(-18.48, 123.22) * mm, "mid": v(-17.72, 122.42) * mm, "end": v(-16.9, 121.7) * mm});
            skArc(sketch, "E2657", {"start": v(-16.9, 121.7) * mm, "mid": v(-14.35, 120.19) * mm, "end": v(-11.47, 119.46) * mm});
            skArc(sketch, "E2658", {"start": v(-11.47, 119.46) * mm, "mid": v(-7.9, 119.37) * mm, "end": v(-4.36, 119.88) * mm});
            skArc(sketch, "E2659", {"start": v(-4.36, 119.88) * mm, "mid": v(0.44, 121.25) * mm, "end": v(5.08, 123.12) * mm});
            skArc(sketch, "E2660", {"start": v(5.08, 123.12) * mm, "mid": v(11.58, 126.3) * mm, "end": v(17.95, 129.7) * mm});
            skArc(sketch, "E2661", {"start": v(17.95, 129.7) * mm, "mid": v(20.71, 131.17) * mm, "end": v(23.53, 132.52) * mm});
            skArc(sketch, "E2662", {"start": v(23.53, 132.52) * mm, "mid": v(25.97, 133.53) * mm, "end": v(28.46, 134.37) * mm});
            skArc(sketch, "E2663", {"start": v(28.46, 134.37) * mm, "mid": v(31, 135.05) * mm, "end": v(33.6, 135.55) * mm});
            skArc(sketch, "E2664", {"start": v(33.6, 135.55) * mm, "mid": v(36.68, 135.97) * mm, "end": v(39.79, 136.27) * mm});
            skArc(sketch, "E2665", {"start": v(39.79, 136.27) * mm, "mid": v(42.37, 136.42) * mm, "end": v(44.96, 136.48) * mm});
            skArc(sketch, "E2666", {"start": v(44.96, 136.48) * mm, "mid": v(47.1, 136.43) * mm, "end": v(49.24, 136.24) * mm});
            skArc(sketch, "E2667", {"start": v(49.24, 136.24) * mm, "mid": v(51.3, 135.93) * mm, "end": v(53.32, 135.49) * mm});
            skArc(sketch, "E2668", {"start": v(53.32, 135.49) * mm, "mid": v(55.6, 134.86) * mm, "end": v(57.84, 134.14) * mm});
            skArc(sketch, "E2669", {"start": v(57.84, 134.14) * mm, "mid": v(58.86, 133.79) * mm, "end": v(59.9, 133.46) * mm});
            skArc(sketch, "E2670", {"start": v(67.64, 129.12) * mm, "mid": v(63.97, 131.65) * mm, "end": v(59.9, 133.46) * mm});
            skSolve(sketch);
        }
        {
            var Q0;
            Q0=qSketchRegion(id+"F22",true);
            var Q1;
            Q1=makeQuery(id+"F21.opExtrude","CAP_FACE",FACE,{"disambiguationData":[OSD([sQuery(id+"F20.wireOp",EDGE,"E2246"),sQuery(id+"F20.wireOp",EDGE,"E2247"),sQuery(id+"F20.wireOp",EDGE,"E2248"),sQuery(id+"F20.wireOp",EDGE,"E2251.bottom"),sQuery(id+"F20.wireOp",EDGE,"E2251.top"),sQuery(id+"F20.wireOp",EDGE,"E2251.left"),sQuery(id+"F20.wireOp",EDGE,"E2251.right"),sQuery(id+"F20.wireOp",EDGE,"E2252.trimOffspring"),sQuery(id+"F20.wireOp",EDGE,"E2254"),sQuery(id+"F20.wireOp",EDGE,"E2255.0"),sQuery(id+"F20.wireOp",EDGE,"E2256.MirrorCS"),sQuery(id+"F20.wireOp",EDGE,"E2257.MirrorCS"),sQuery(id+"F20.wireOp",EDGE,"E2258.trimOffspring"),sQuery(id+"F20.wireOp",EDGE,"E2259.trimOffspring"),sQuery(id+"F20.wireOp",EDGE,"E2260.trimOffspring"),sQuery(id+"F20.wireOp",EDGE,"E2261.trimOffspring"),sQuery(id+"F20.wireOp",EDGE,"E2262.filletArc"),sQuery(id+"F20.wireOp",EDGE,"E2263.filletArc"),sQuery(id+"F20.wireOp",EDGE,"E2264.filletArc"),sQuery(id+"F20.wireOp",EDGE,"E2265.filletArc")])],"isStart":true});
            extrude(context, id + "F23", {"entities" : qUnion([Q0]), "operationType" : NewBodyOperationType.ADD, "endBound" : BoundingType.UP_TO_SURFACE, "oppositeDirection" : true, "depth" : 25.4 * mm, "endBoundEntityFace" : qUnion([Q1]), "offsetDistance" : 25.4 * mm});
        }
        {
            var Q0;
            {var subQ14=sQuery(id+"F20.wireOp",EDGE,"E2251.left");var subQ16=sQuery(id+"F20.wireOp",EDGE,"E2251.bottom");Q0=makeQuery(id+"F23.boolean.opBoolean","SPLIT",FACE,{"disambiguationData":[TD([makeQuery(id+"F21.opExtrude","SWEPT_FACE",FACE,{"disambiguationData":[OSD([subQ16])]})])],"derivedFrom":makeQuery(id+"F21.opExtrude","SWEPT_FACE",FACE,{"disambiguationData":[OSD([subQ14])]})});}
            var sketch = newSketch(context, id + "F24", { "sketchPlane" : qUnion([Q0])});
            skPoint(sketch, "E2671", {"position": v(0, 133.35) * mm});
            skPoint(sketch, "E2672", {"position": v(0, 50.8) * mm});
            skLineSegment(sketch, "E2673", {"start": v(0, 139.7) * mm, "end": v(0, 133.35) * mm, "construction": true});
            skLineSegment(sketch, "E2674", {"start": v(0, 44.45) * mm, "end": v(0, 50.8) * mm, "construction": true});
            skSolve(sketch);
        }
        {
            var Q0;
            Q0=sQuery(id+"F24.wireOp",VERTEX,"E2671");
            var Q1;
            Q1=sQuery(id+"F24.wireOp",VERTEX,"E2672");
            var Q2;
            Q2=makeQuery(id+"F21.opExtrude","SWEPT_BODY",BODY,{"disambiguationData":[OSD([sQuery(id+"F20.wireOp",EDGE,"E2246"),sQuery(id+"F20.wireOp",EDGE,"E2247"),sQuery(id+"F20.wireOp",EDGE,"E2248"),sQuery(id+"F20.wireOp",EDGE,"E2251.bottom"),sQuery(id+"F20.wireOp",EDGE,"E2251.top"),sQuery(id+"F20.wireOp",EDGE,"E2251.left"),sQuery(id+"F20.wireOp",EDGE,"E2251.right"),sQuery(id+"F20.wireOp",EDGE,"E2252.trimOffspring"),sQuery(id+"F20.wireOp",EDGE,"E2254"),sQuery(id+"F20.wireOp",EDGE,"E2255.0"),sQuery(id+"F20.wireOp",EDGE,"E2256.MirrorCS"),sQuery(id+"F20.wireOp",EDGE,"E2257.MirrorCS"),sQuery(id+"F20.wireOp",EDGE,"E2258.trimOffspring"),sQuery(id+"F20.wireOp",EDGE,"E2259.trimOffspring"),sQuery(id+"F20.wireOp",EDGE,"E2260.trimOffspring"),sQuery(id+"F20.wireOp",EDGE,"E2261.trimOffspring"),sQuery(id+"F20.wireOp",EDGE,"E2262.filletArc"),sQuery(id+"F20.wireOp",EDGE,"E2263.filletArc"),sQuery(id+"F20.wireOp",EDGE,"E2264.filletArc"),sQuery(id+"F20.wireOp",EDGE,"E2265.filletArc")])]});
            hole(context, id + "F25", {"style" : HoleStyle.C_SINK, "endStyle" : HoleEndStyle.THROUGH, "standardTappedOrClearance" : lookupTablePath({ "standard" : "ANSI", "fit" : "Normal (ASME)", "size" : "#8", "type" : "Clearance" }), "standardBlindInLast" : lookupTablePath({ "fit" : "Free", "standard" : "ANSI", "size" : "#8", "type" : "Clearance" }), "holeDiameter" : 4.5 * mm, "cSinkDiameter" : 9.12 * mm, "cSinkAngle" : 82 * degree, "majorDiameter" : 6.35 * mm, "isTappedThrough" : true, "tappedDepth" : 12.7 * mm, "tapClearance" : 3, "locations" : qUnion([Q0, Q1]), "scope" : qUnion([Q2])});
        }
        {
            var Q0;
            Q0=makeQuery(id+"F23.boolean.opBoolean","MERGE",FACE,{"derivedFrom":[makeQuery(id+"F21.opExtrude","CAP_FACE",FACE,{"disambiguationData":[OSD([sQuery(id+"F20.wireOp",EDGE,"E2246"),sQuery(id+"F20.wireOp",EDGE,"E2247"),sQuery(id+"F20.wireOp",EDGE,"E2248"),sQuery(id+"F20.wireOp",EDGE,"E2251.bottom"),sQuery(id+"F20.wireOp",EDGE,"E2251.top"),sQuery(id+"F20.wireOp",EDGE,"E2251.left"),sQuery(id+"F20.wireOp",EDGE,"E2251.right"),sQuery(id+"F20.wireOp",EDGE,"E2252.trimOffspring"),sQuery(id+"F20.wireOp",EDGE,"E2254"),sQuery(id+"F20.wireOp",EDGE,"E2255.0"),sQuery(id+"F20.wireOp",EDGE,"E2256.MirrorCS"),sQuery(id+"F20.wireOp",EDGE,"E2257.MirrorCS"),sQuery(id+"F20.wireOp",EDGE,"E2258.trimOffspring"),sQuery(id+"F20.wireOp",EDGE,"E2259.trimOffspring"),sQuery(id+"F20.wireOp",EDGE,"E2260.trimOffspring"),sQuery(id+"F20.wireOp",EDGE,"E2261.trimOffspring"),sQuery(id+"F20.wireOp",EDGE,"E2262.filletArc"),sQuery(id+"F20.wireOp",EDGE,"E2263.filletArc"),sQuery(id+"F20.wireOp",EDGE,"E2264.filletArc"),sQuery(id+"F20.wireOp",EDGE,"E2265.filletArc")])],"isStart":false}),makeQuery(id+"F23.opExtrude","CAP_FACE",FACE,{"disambiguationData":[OSD([sQuery(id+"F22.wireOp",EDGE,"E2268"),sQuery(id+"F22.wireOp",EDGE,"E2269"),sQuery(id+"F22.wireOp",EDGE,"E2270"),sQuery(id+"F22.wireOp",EDGE,"E2271"),sQuery(id+"F22.wireOp",EDGE,"E2272"),sQuery(id+"F22.wireOp",EDGE,"E2273"),sQuery(id+"F22.wireOp",EDGE,"E2274"),sQuery(id+"F22.wireOp",EDGE,"E2275"),sQuery(id+"F22.wireOp",EDGE,"E2276"),sQuery(id+"F22.wireOp",EDGE,"E2277"),sQuery(id+"F22.wireOp",EDGE,"E2278"),sQuery(id+"F22.wireOp",EDGE,"E2279"),sQuery(id+"F22.wireOp",EDGE,"E2280"),sQuery(id+"F22.wireOp",EDGE,"E2281"),sQuery(id+"F22.wireOp",EDGE,"E2282"),sQuery(id+"F22.wireOp",EDGE,"E2283"),sQuery(id+"F22.wireOp",EDGE,"E2284"),sQuery(id+"F22.wireOp",EDGE,"E2285"),sQuery(id+"F22.wireOp",EDGE,"E2286"),sQuery(id+"F22.wireOp",EDGE,"E2287"),sQuery(id+"F22.wireOp",EDGE,"E2288"),sQuery(id+"F22.wireOp",EDGE,"E2289"),sQuery(id+"F22.wireOp",EDGE,"E2290"),sQuery(id+"F22.wireOp",EDGE,"E2291"),sQuery(id+"F22.wireOp",EDGE,"E2292"),sQuery(id+"F22.wireOp",EDGE,"E2293"),sQuery(id+"F22.wireOp",EDGE,"E2294"),sQuery(id+"F22.wireOp",EDGE,"E2295"),sQuery(id+"F22.wireOp",EDGE,"E2296"),sQuery(id+"F22.wireOp",EDGE,"E2297"),sQuery(id+"F22.wireOp",EDGE,"E2298"),sQuery(id+"F22.wireOp",EDGE,"E2299"),sQuery(id+"F22.wireOp",EDGE,"E2300"),sQuery(id+"F22.wireOp",EDGE,"E2301"),sQuery(id+"F22.wireOp",EDGE,"E2302"),sQuery(id+"F22.wireOp",EDGE,"E2303"),sQuery(id+"F22.wireOp",EDGE,"E2304"),sQuery(id+"F22.wireOp",EDGE,"E2305"),sQuery(id+"F22.wireOp",EDGE,"E2306"),sQuery(id+"F22.wireOp",EDGE,"E2307"),sQuery(id+"F22.wireOp",EDGE,"E2308"),sQuery(id+"F22.wireOp",EDGE,"E2309"),sQuery(id+"F22.wireOp",EDGE,"E2310"),sQuery(id+"F22.wireOp",EDGE,"E2311"),sQuery(id+"F22.wireOp",EDGE,"E2312"),sQuery(id+"F22.wireOp",EDGE,"E2313"),sQuery(id+"F22.wireOp",EDGE,"E2314"),sQuery(id+"F22.wireOp",EDGE,"E2315"),sQuery(id+"F22.wireOp",EDGE,"E2316"),sQuery(id+"F22.wireOp",EDGE,"E2317"),sQuery(id+"F22.wireOp",EDGE,"E2318"),sQuery(id+"F22.wireOp",EDGE,"E2319"),sQuery(id+"F22.wireOp",EDGE,"E2320"),sQuery(id+"F22.wireOp",EDGE,"E2321"),sQuery(id+"F22.wireOp",EDGE,"E2322"),sQuery(id+"F22.wireOp",EDGE,"E2323"),sQuery(id+"F22.wireOp",EDGE,"E2324"),sQuery(id+"F22.wireOp",EDGE,"E2325"),sQuery(id+"F22.wireOp",EDGE,"E2326"),sQuery(id+"F22.wireOp",EDGE,"E2327"),sQuery(id+"F22.wireOp",EDGE,"E2328"),sQuery(id+"F22.wireOp",EDGE,"E2329"),sQuery(id+"F22.wireOp",EDGE,"E2330"),sQuery(id+"F22.wireOp",EDGE,"E2331"),sQuery(id+"F22.wireOp",EDGE,"E2332"),sQuery(id+"F22.wireOp",EDGE,"E2333"),sQuery(id+"F22.wireOp",EDGE,"E2334"),sQuery(id+"F22.wireOp",EDGE,"E2335"),sQuery(id+"F22.wireOp",EDGE,"E2336"),sQuery(id+"F22.wireOp",EDGE,"E2337"),sQuery(id+"F22.wireOp",EDGE,"E2338"),sQuery(id+"F22.wireOp",EDGE,"E2339"),sQuery(id+"F22.wireOp",EDGE,"E2340"),sQuery(id+"F22.wireOp",EDGE,"E2341"),sQuery(id+"F22.wireOp",EDGE,"E2342"),sQuery(id+"F22.wireOp",EDGE,"E2343"),sQuery(id+"F22.wireOp",EDGE,"E2344"),sQuery(id+"F22.wireOp",EDGE,"E2345"),sQuery(id+"F22.wireOp",EDGE,"E2346"),sQuery(id+"F22.wireOp",EDGE,"E2347"),sQuery(id+"F22.wireOp",EDGE,"E2348"),sQuery(id+"F22.wireOp",EDGE,"E2349"),sQuery(id+"F22.wireOp",EDGE,"E2350"),sQuery(id+"F22.wireOp",EDGE,"E2351"),sQuery(id+"F22.wireOp",EDGE,"E2352"),sQuery(id+"F22.wireOp",EDGE,"E2353"),sQuery(id+"F22.wireOp",EDGE,"E2354"),sQuery(id+"F22.wireOp",EDGE,"E2355"),sQuery(id+"F22.wireOp",EDGE,"E2356"),sQuery(id+"F22.wireOp",EDGE,"E2357"),sQuery(id+"F22.wireOp",EDGE,"E2358"),sQuery(id+"F22.wireOp",EDGE,"E2359"),sQuery(id+"F22.wireOp",EDGE,"E2360"),sQuery(id+"F22.wireOp",EDGE,"E2361"),sQuery(id+"F22.wireOp",EDGE,"E2362"),sQuery(id+"F22.wireOp",EDGE,"E2363"),sQuery(id+"F22.wireOp",EDGE,"E2364"),sQuery(id+"F22.wireOp",EDGE,"E2365"),sQuery(id+"F22.wireOp",EDGE,"E2366"),sQuery(id+"F22.wireOp",EDGE,"E2367"),sQuery(id+"F22.wireOp",EDGE,"E2368"),sQuery(id+"F22.wireOp",EDGE,"E2369"),sQuery(id+"F22.wireOp",EDGE,"E2370"),sQuery(id+"F22.wireOp",EDGE,"E2371"),sQuery(id+"F22.wireOp",EDGE,"E2372"),sQuery(id+"F22.wireOp",EDGE,"E2373"),sQuery(id+"F22.wireOp",EDGE,"E2374"),sQuery(id+"F22.wireOp",EDGE,"E2375"),sQuery(id+"F22.wireOp",EDGE,"E2376"),sQuery(id+"F22.wireOp",EDGE,"E2377"),sQuery(id+"F22.wireOp",EDGE,"E2378"),sQuery(id+"F22.wireOp",EDGE,"E2379"),sQuery(id+"F22.wireOp",EDGE,"E2380"),sQuery(id+"F22.wireOp",EDGE,"E2381"),sQuery(id+"F22.wireOp",EDGE,"E2382"),sQuery(id+"F22.wireOp",EDGE,"E2383"),sQuery(id+"F22.wireOp",EDGE,"E2384"),sQuery(id+"F22.wireOp",EDGE,"E2385"),sQuery(id+"F22.wireOp",EDGE,"E2386"),sQuery(id+"F22.wireOp",EDGE,"E2387"),sQuery(id+"F22.wireOp",EDGE,"E2388"),sQuery(id+"F22.wireOp",EDGE,"E2389"),sQuery(id+"F22.wireOp",EDGE,"E2390"),sQuery(id+"F22.wireOp",EDGE,"E2391"),sQuery(id+"F22.wireOp",EDGE,"E2392"),sQuery(id+"F22.wireOp",EDGE,"E2393"),sQuery(id+"F22.wireOp",EDGE,"E2394"),sQuery(id+"F22.wireOp",EDGE,"E2395"),sQuery(id+"F22.wireOp",EDGE,"E2396"),sQuery(id+"F22.wireOp",EDGE,"E2397"),sQuery(id+"F22.wireOp",EDGE,"E2398"),sQuery(id+"F22.wireOp",EDGE,"E2399"),sQuery(id+"F22.wireOp",EDGE,"E2400"),sQuery(id+"F22.wireOp",EDGE,"E2401"),sQuery(id+"F22.wireOp",EDGE,"E2402"),sQuery(id+"F22.wireOp",EDGE,"E2403"),sQuery(id+"F22.wireOp",EDGE,"E2404"),sQuery(id+"F22.wireOp",EDGE,"E2405"),sQuery(id+"F22.wireOp",EDGE,"E2406"),sQuery(id+"F22.wireOp",EDGE,"E2407"),sQuery(id+"F22.wireOp",EDGE,"E2408"),sQuery(id+"F22.wireOp",EDGE,"E2409"),sQuery(id+"F22.wireOp",EDGE,"E2410"),sQuery(id+"F22.wireOp",EDGE,"E2411"),sQuery(id+"F22.wireOp",EDGE,"E2412"),sQuery(id+"F22.wireOp",EDGE,"E2413"),sQuery(id+"F22.wireOp",EDGE,"E2414"),sQuery(id+"F22.wireOp",EDGE,"E2415"),sQuery(id+"F22.wireOp",EDGE,"E2416"),sQuery(id+"F22.wireOp",EDGE,"E2417"),sQuery(id+"F22.wireOp",EDGE,"E2418"),sQuery(id+"F22.wireOp",EDGE,"E2419"),sQuery(id+"F22.wireOp",EDGE,"E2420"),sQuery(id+"F22.wireOp",EDGE,"E2421"),sQuery(id+"F22.wireOp",EDGE,"E2422"),sQuery(id+"F22.wireOp",EDGE,"E2423"),sQuery(id+"F22.wireOp",EDGE,"E2424"),sQuery(id+"F22.wireOp",EDGE,"E2425"),sQuery(id+"F22.wireOp",EDGE,"E2426"),sQuery(id+"F22.wireOp",EDGE,"E2427"),sQuery(id+"F22.wireOp",EDGE,"E2428"),sQuery(id+"F22.wireOp",EDGE,"E2429"),sQuery(id+"F22.wireOp",EDGE,"E2430"),sQuery(id+"F22.wireOp",EDGE,"E2431"),sQuery(id+"F22.wireOp",EDGE,"E2432"),sQuery(id+"F22.wireOp",EDGE,"E2433"),sQuery(id+"F22.wireOp",EDGE,"E2434"),sQuery(id+"F22.wireOp",EDGE,"E2435"),sQuery(id+"F22.wireOp",EDGE,"E2436"),sQuery(id+"F22.wireOp",EDGE,"E2437"),sQuery(id+"F22.wireOp",EDGE,"E2438"),sQuery(id+"F22.wireOp",EDGE,"E2439"),sQuery(id+"F22.wireOp",EDGE,"E2440"),sQuery(id+"F22.wireOp",EDGE,"E2441"),sQuery(id+"F22.wireOp",EDGE,"E2442"),sQuery(id+"F22.wireOp",EDGE,"E2443"),sQuery(id+"F22.wireOp",EDGE,"E2444"),sQuery(id+"F22.wireOp",EDGE,"E2445"),sQuery(id+"F22.wireOp",EDGE,"E2446"),sQuery(id+"F22.wireOp",EDGE,"E2447"),sQuery(id+"F22.wireOp",EDGE,"E2448"),sQuery(id+"F22.wireOp",EDGE,"E2449"),sQuery(id+"F22.wireOp",EDGE,"E2450"),sQuery(id+"F22.wireOp",EDGE,"E2451"),sQuery(id+"F22.wireOp",EDGE,"E2452"),sQuery(id+"F22.wireOp",EDGE,"E2453"),sQuery(id+"F22.wireOp",EDGE,"E2454"),sQuery(id+"F22.wireOp",EDGE,"E2455"),sQuery(id+"F22.wireOp",EDGE,"E2456"),sQuery(id+"F22.wireOp",EDGE,"E2457"),sQuery(id+"F22.wireOp",EDGE,"E2458"),sQuery(id+"F22.wireOp",EDGE,"E2459"),sQuery(id+"F22.wireOp",EDGE,"E2460"),sQuery(id+"F22.wireOp",EDGE,"E2461"),sQuery(id+"F22.wireOp",EDGE,"E2462"),sQuery(id+"F22.wireOp",EDGE,"E2463"),sQuery(id+"F22.wireOp",EDGE,"E2464"),sQuery(id+"F22.wireOp",EDGE,"E2465"),sQuery(id+"F22.wireOp",EDGE,"E2466"),sQuery(id+"F22.wireOp",EDGE,"E2467"),sQuery(id+"F22.wireOp",EDGE,"E2468"),sQuery(id+"F22.wireOp",EDGE,"E2469"),sQuery(id+"F22.wireOp",EDGE,"E2470"),sQuery(id+"F22.wireOp",EDGE,"E2471"),sQuery(id+"F22.wireOp",EDGE,"E2472"),sQuery(id+"F22.wireOp",EDGE,"E2473"),sQuery(id+"F22.wireOp",EDGE,"E2474"),sQuery(id+"F22.wireOp",EDGE,"E2475"),sQuery(id+"F22.wireOp",EDGE,"E2476"),sQuery(id+"F22.wireOp",EDGE,"E2477"),sQuery(id+"F22.wireOp",EDGE,"E2478"),sQuery(id+"F22.wireOp",EDGE,"E2479"),sQuery(id+"F22.wireOp",EDGE,"E2480"),sQuery(id+"F22.wireOp",EDGE,"E2481"),sQuery(id+"F22.wireOp",EDGE,"E2482"),sQuery(id+"F22.wireOp",EDGE,"E2483"),sQuery(id+"F22.wireOp",EDGE,"E2484"),sQuery(id+"F22.wireOp",EDGE,"E2485"),sQuery(id+"F22.wireOp",EDGE,"E2486"),sQuery(id+"F22.wireOp",EDGE,"E2487"),sQuery(id+"F22.wireOp",EDGE,"E2488"),sQuery(id+"F22.wireOp",EDGE,"E2489"),sQuery(id+"F22.wireOp",EDGE,"E2490"),sQuery(id+"F22.wireOp",EDGE,"E2491"),sQuery(id+"F22.wireOp",EDGE,"E2492"),sQuery(id+"F22.wireOp",EDGE,"E2493"),sQuery(id+"F22.wireOp",EDGE,"E2494"),sQuery(id+"F22.wireOp",EDGE,"E2495"),sQuery(id+"F22.wireOp",EDGE,"E2496"),sQuery(id+"F22.wireOp",EDGE,"E2497"),sQuery(id+"F22.wireOp",EDGE,"E2498"),sQuery(id+"F22.wireOp",EDGE,"E2499"),sQuery(id+"F22.wireOp",EDGE,"E2500"),sQuery(id+"F22.wireOp",EDGE,"E2501"),sQuery(id+"F22.wireOp",EDGE,"E2502"),sQuery(id+"F22.wireOp",EDGE,"E2503"),sQuery(id+"F22.wireOp",EDGE,"E2504"),sQuery(id+"F22.wireOp",EDGE,"E2505"),sQuery(id+"F22.wireOp",EDGE,"E2506"),sQuery(id+"F22.wireOp",EDGE,"E2507"),sQuery(id+"F22.wireOp",EDGE,"E2508"),sQuery(id+"F22.wireOp",EDGE,"E2509"),sQuery(id+"F22.wireOp",EDGE,"E2510"),sQuery(id+"F22.wireOp",EDGE,"E2511"),sQuery(id+"F22.wireOp",EDGE,"E2512"),sQuery(id+"F22.wireOp",EDGE,"E2513"),sQuery(id+"F22.wireOp",EDGE,"E2514"),sQuery(id+"F22.wireOp",EDGE,"E2515"),sQuery(id+"F22.wireOp",EDGE,"E2516"),sQuery(id+"F22.wireOp",EDGE,"E2517"),sQuery(id+"F22.wireOp",EDGE,"E2518"),sQuery(id+"F22.wireOp",EDGE,"E2519"),sQuery(id+"F22.wireOp",EDGE,"E2520"),sQuery(id+"F22.wireOp",EDGE,"E2521"),sQuery(id+"F22.wireOp",EDGE,"E2522"),sQuery(id+"F22.wireOp",EDGE,"E2523"),sQuery(id+"F22.wireOp",EDGE,"E2524"),sQuery(id+"F22.wireOp",EDGE,"E2525"),sQuery(id+"F22.wireOp",EDGE,"E2526"),sQuery(id+"F22.wireOp",EDGE,"E2527"),sQuery(id+"F22.wireOp",EDGE,"E2528"),sQuery(id+"F22.wireOp",EDGE,"E2529"),sQuery(id+"F22.wireOp",EDGE,"E2530"),sQuery(id+"F22.wireOp",EDGE,"E2531"),sQuery(id+"F22.wireOp",EDGE,"E2532"),sQuery(id+"F22.wireOp",EDGE,"E2533"),sQuery(id+"F22.wireOp",EDGE,"E2534"),sQuery(id+"F22.wireOp",EDGE,"E2535"),sQuery(id+"F22.wireOp",EDGE,"E2536"),sQuery(id+"F22.wireOp",EDGE,"E2537"),sQuery(id+"F22.wireOp",EDGE,"E2538"),sQuery(id+"F22.wireOp",EDGE,"E2539"),sQuery(id+"F22.wireOp",EDGE,"E2540"),sQuery(id+"F22.wireOp",EDGE,"E2541"),sQuery(id+"F22.wireOp",EDGE,"E2542"),sQuery(id+"F22.wireOp",EDGE,"E2543"),sQuery(id+"F22.wireOp",EDGE,"E2544"),sQuery(id+"F22.wireOp",EDGE,"E2545"),sQuery(id+"F22.wireOp",EDGE,"E2546"),sQuery(id+"F22.wireOp",EDGE,"E2547"),sQuery(id+"F22.wireOp",EDGE,"E2548"),sQuery(id+"F22.wireOp",EDGE,"E2549"),sQuery(id+"F22.wireOp",EDGE,"E2550"),sQuery(id+"F22.wireOp",EDGE,"E2551"),sQuery(id+"F22.wireOp",EDGE,"E2552"),sQuery(id+"F22.wireOp",EDGE,"E2553"),sQuery(id+"F22.wireOp",EDGE,"E2554"),sQuery(id+"F22.wireOp",EDGE,"E2555"),sQuery(id+"F22.wireOp",EDGE,"E2556"),sQuery(id+"F22.wireOp",EDGE,"E2557"),sQuery(id+"F22.wireOp",EDGE,"E2558"),sQuery(id+"F22.wireOp",EDGE,"E2559"),sQuery(id+"F22.wireOp",EDGE,"E2560"),sQuery(id+"F22.wireOp",EDGE,"E2561"),sQuery(id+"F22.wireOp",EDGE,"E2562"),sQuery(id+"F22.wireOp",EDGE,"E2563"),sQuery(id+"F22.wireOp",EDGE,"E2564"),sQuery(id+"F22.wireOp",EDGE,"E2565"),sQuery(id+"F22.wireOp",EDGE,"E2566"),sQuery(id+"F22.wireOp",EDGE,"E2567"),sQuery(id+"F22.wireOp",EDGE,"E2568"),sQuery(id+"F22.wireOp",EDGE,"E2569"),sQuery(id+"F22.wireOp",EDGE,"E2570"),sQuery(id+"F22.wireOp",EDGE,"E2571"),sQuery(id+"F22.wireOp",EDGE,"E2572"),sQuery(id+"F22.wireOp",EDGE,"E2573"),sQuery(id+"F22.wireOp",EDGE,"E2574"),sQuery(id+"F22.wireOp",EDGE,"E2575"),sQuery(id+"F22.wireOp",EDGE,"E2576"),sQuery(id+"F22.wireOp",EDGE,"E2577"),sQuery(id+"F22.wireOp",EDGE,"E2578"),sQuery(id+"F22.wireOp",EDGE,"E2579"),sQuery(id+"F22.wireOp",EDGE,"E2580"),sQuery(id+"F22.wireOp",EDGE,"E2581"),sQuery(id+"F22.wireOp",EDGE,"E2582"),sQuery(id+"F22.wireOp",EDGE,"E2583"),sQuery(id+"F22.wireOp",EDGE,"E2584"),sQuery(id+"F22.wireOp",EDGE,"E2585"),sQuery(id+"F22.wireOp",EDGE,"E2586"),sQuery(id+"F22.wireOp",EDGE,"E2587"),sQuery(id+"F22.wireOp",EDGE,"E2588"),sQuery(id+"F22.wireOp",EDGE,"E2589"),sQuery(id+"F22.wireOp",EDGE,"E2590"),sQuery(id+"F22.wireOp",EDGE,"E2591"),sQuery(id+"F22.wireOp",EDGE,"E2592"),sQuery(id+"F22.wireOp",EDGE,"E2593"),sQuery(id+"F22.wireOp",EDGE,"E2594"),sQuery(id+"F22.wireOp",EDGE,"E2595"),sQuery(id+"F22.wireOp",EDGE,"E2596"),sQuery(id+"F22.wireOp",EDGE,"E2597"),sQuery(id+"F22.wireOp",EDGE,"E2598"),sQuery(id+"F22.wireOp",EDGE,"E2599"),sQuery(id+"F22.wireOp",EDGE,"E2600"),sQuery(id+"F22.wireOp",EDGE,"E2601"),sQuery(id+"F22.wireOp",EDGE,"E2602"),sQuery(id+"F22.wireOp",EDGE,"E2603"),sQuery(id+"F22.wireOp",EDGE,"E2604"),sQuery(id+"F22.wireOp",EDGE,"E2605"),sQuery(id+"F22.wireOp",EDGE,"E2606"),sQuery(id+"F22.wireOp",EDGE,"E2607"),sQuery(id+"F22.wireOp",EDGE,"E2608"),sQuery(id+"F22.wireOp",EDGE,"E2609"),sQuery(id+"F22.wireOp",EDGE,"E2610"),sQuery(id+"F22.wireOp",EDGE,"E2611"),sQuery(id+"F22.wireOp",EDGE,"E2612"),sQuery(id+"F22.wireOp",EDGE,"E2613"),sQuery(id+"F22.wireOp",EDGE,"E2614"),sQuery(id+"F22.wireOp",EDGE,"E2615"),sQuery(id+"F22.wireOp",EDGE,"E2616"),sQuery(id+"F22.wireOp",EDGE,"E2617"),sQuery(id+"F22.wireOp",EDGE,"E2618"),sQuery(id+"F22.wireOp",EDGE,"E2619"),sQuery(id+"F22.wireOp",EDGE,"E2620"),sQuery(id+"F22.wireOp",EDGE,"E2621"),sQuery(id+"F22.wireOp",EDGE,"E2622"),sQuery(id+"F22.wireOp",EDGE,"E2623"),sQuery(id+"F22.wireOp",EDGE,"E2624"),sQuery(id+"F22.wireOp",EDGE,"E2625"),sQuery(id+"F22.wireOp",EDGE,"E2626"),sQuery(id+"F22.wireOp",EDGE,"E2627"),sQuery(id+"F22.wireOp",EDGE,"E2628"),sQuery(id+"F22.wireOp",EDGE,"E2629"),sQuery(id+"F22.wireOp",EDGE,"E2630"),sQuery(id+"F22.wireOp",EDGE,"E2631"),sQuery(id+"F22.wireOp",EDGE,"E2632"),sQuery(id+"F22.wireOp",EDGE,"E2633"),sQuery(id+"F22.wireOp",EDGE,"E2634"),sQuery(id+"F22.wireOp",EDGE,"E2635"),sQuery(id+"F22.wireOp",EDGE,"E2636"),sQuery(id+"F22.wireOp",EDGE,"E2637"),sQuery(id+"F22.wireOp",EDGE,"E2638"),sQuery(id+"F22.wireOp",EDGE,"E2639"),sQuery(id+"F22.wireOp",EDGE,"E2640"),sQuery(id+"F22.wireOp",EDGE,"E2641"),sQuery(id+"F22.wireOp",EDGE,"E2642"),sQuery(id+"F22.wireOp",EDGE,"E2643"),sQuery(id+"F22.wireOp",EDGE,"E2644"),sQuery(id+"F22.wireOp",EDGE,"E2645"),sQuery(id+"F22.wireOp",EDGE,"E2646"),sQuery(id+"F22.wireOp",EDGE,"E2647"),sQuery(id+"F22.wireOp",EDGE,"E2648"),sQuery(id+"F22.wireOp",EDGE,"E2649"),sQuery(id+"F22.wireOp",EDGE,"E2650"),sQuery(id+"F22.wireOp",EDGE,"E2651"),sQuery(id+"F22.wireOp",EDGE,"E2652"),sQuery(id+"F22.wireOp",EDGE,"E2653"),sQuery(id+"F22.wireOp",EDGE,"E2654"),sQuery(id+"F22.wireOp",EDGE,"E2655"),sQuery(id+"F22.wireOp",EDGE,"E2656"),sQuery(id+"F22.wireOp",EDGE,"E2657"),sQuery(id+"F22.wireOp",EDGE,"E2658"),sQuery(id+"F22.wireOp",EDGE,"E2659"),sQuery(id+"F22.wireOp",EDGE,"E2660"),sQuery(id+"F22.wireOp",EDGE,"E2661"),sQuery(id+"F22.wireOp",EDGE,"E2662"),sQuery(id+"F22.wireOp",EDGE,"E2663"),sQuery(id+"F22.wireOp",EDGE,"E2664"),sQuery(id+"F22.wireOp",EDGE,"E2665"),sQuery(id+"F22.wireOp",EDGE,"E2666"),sQuery(id+"F22.wireOp",EDGE,"E2667"),sQuery(id+"F22.wireOp",EDGE,"E2668"),sQuery(id+"F22.wireOp",EDGE,"E2669"),sQuery(id+"F22.wireOp",EDGE,"E2670")])],"isStart":true})]});
            var sketch = newSketch(context, id + "F26", { "sketchPlane" : qUnion([Q0])});
            skLineSegment(sketch, "E2675", {"start": v(-76.2, 69.85) * mm, "end": v(75.52, 69.85) * mm});
            skLineSegment(sketch, "E2676", {"start": v(75.52, 69.85) * mm, "end": v(75.52, 59.7) * mm});
            skLineSegment(sketch, "E2677", {"start": v(75.52, 59.7) * mm, "end": v(-76.2, 59.7) * mm});
            skLineSegment(sketch, "E2678", {"start": v(-76.2, 59.7) * mm, "end": v(-76.2, 69.85) * mm});
            skSolve(sketch);
        }
        {
            var Q0;
            Q0=qSketchRegion(id+"F26",true);
            extrude(context, id + "F27", {"entities" : qUnion([Q0]), "operationType" : NewBodyOperationType.REMOVE, "oppositeDirection" : true, "depth" : 6.35 * mm, "offsetDistance" : 25.4 * mm});
        }
    });
